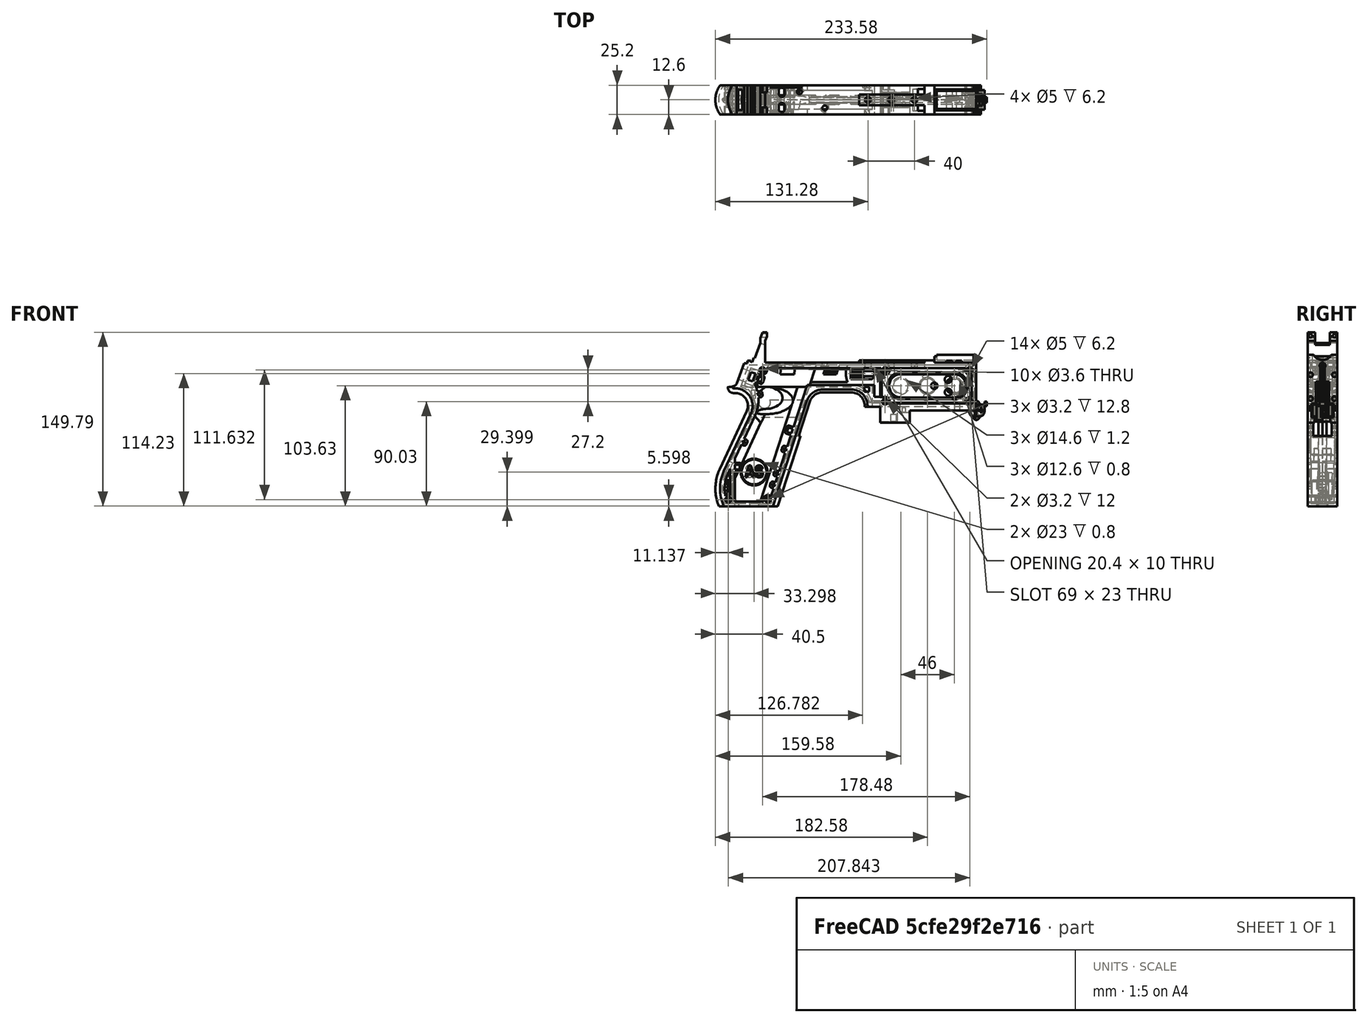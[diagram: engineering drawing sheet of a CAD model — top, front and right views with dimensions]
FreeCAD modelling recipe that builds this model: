
FCSTD DOCUMENT  (FreeCAD 1.0R39319 (Git))
Label: PICON-OF_ver_58
License: All rights reserved
LicenseURL: https://en.wikipedia.org/wiki/All_rights_reserved
objects: Sketcher::SketchObject×124, Part::Extrusion×63, Part::Cut×48, PartDesign::Pad×29, PartDesign::Pocket×21, PartDesign::Chamfer×15, PartDesign::Body×10, PartDesign::Fillet×6, Part::MultiFuse×5, Part::Part2DObjectPython×4, PartDesign::SubtractivePipe×4, PartDesign::SubtractiveLoft×4, PartDesign::Plane×3, PartDesign::SubShapeBinder×2, Part::Sweep×1, PartDesign::ShapeBinder×1, Mesh::Feature×1, PartDesign::Point×1, PartDesign::Groove×1
note: 626 computed .brp shape members not serialized (recipe doc carries the construction recipe); baked Part::Feature solids carry a one-line shape summary decoded from their .brp

FEATURE [Sketcher::SketchObject] Sketch  label="corpo principale"
  ArcFitTolerance = 1e-06
  AttacherType = Attacher::AttachEngine3D
  AttachmentSupport = -> [XZ_Plane]
  FullyConstrained = true
  MakeInternals = false
  MapMode = 5
  Placement = pos=(0,0,0) rot=(1,0,0;1.5708rad)
  sketch-geometry (65):
    g0: LineSegment StartX=0 StartY=0 StartZ=0 EndX=-57.2 EndY=0 EndZ=0
    g1: LineSegment StartX=-57.2 StartY=0 StartZ=0 EndX=-57.2 EndY=-10.4 EndZ=0
    g2: LineSegment StartX=-57.2 StartY=-10.4 StartZ=0 EndX=-82.8 EndY=-10.4 EndZ=0
    g3: LineSegment StartX=-82.8 StartY=-10.4 StartZ=0 EndX=-82.8 EndY=3.2 EndZ=0
    g4: LineSegment StartX=-82.8 StartY=3.2 StartZ=0 EndX=-93.6 EndY=3.2 EndZ=0
    g5: LineSegment StartX=-93.6 StartY=3.2 StartZ=0 EndX=-93.6 EndY=4 EndZ=0
    g6: LineSegment StartX=-107.6 StartY=18 StartZ=0 EndX=-132.428 EndY=18 EndZ=0
    g7: LineSegment StartX=-145.743 StartY=8.32624 StartZ=0 EndX=-175.232 EndY=-82.4316 EndZ=0
    g8: LineSegment StartX=-175.232 StartY=-82.4316 StartZ=0 EndX=-217.232 EndY=-82.4316 EndZ=0
    g9: LineSegment StartX=-217.232 StartY=-52.1862 StartZ=0 EndX=-193.988 EndY=-2.33927 EndZ=0
    g10: LineSegment StartX=-206.196 StartY=23.0857 StartZ=0 EndX=-199.861 EndY=40.4914 EndZ=0
    g11: LineSegment StartX=-199.861 StartY=40.4914 StartZ=0 EndX=-197.061 EndY=40.4914 EndZ=0
    g12: LineSegment StartX=-197.061 StartY=40.4914 StartZ=0 EndX=-197.061 EndY=42.8914 EndZ=0
    g13: LineSegment StartX=-197.061 StartY=42.8914 StartZ=0 EndX=-194.261 EndY=42.8914 EndZ=0
    g14: LineSegment StartX=-194.261 StartY=42.8914 StartZ=0 EndX=-194.535 EndY=42.1397 EndZ=0
    g15: LineSegment StartX=-194.535 StartY=42.1397 StartZ=0 EndX=-193.031 EndY=41.5924 EndZ=0
    g16: LineSegment StartX=-193.031 StartY=41.5924 StartZ=0 EndX=-191.663 EndY=45.3512 EndZ=0
    g17: LineSegment StartX=-191.663 StartY=45.3512 StartZ=0 EndX=-190.536 EndY=44.9408 EndZ=0
    g18: LineSegment StartX=-190.536 StartY=44.9408 StartZ=0 EndX=-185.747 EndY=58.0965 EndZ=0
    g19: LineSegment StartX=-185.747 StartY=58.0965 StartZ=0 EndX=-185.747 EndY=62.0965 EndZ=0
    g20: LineSegment StartX=-185.747 StartY=62.0965 StartZ=0 EndX=-183.832 EndY=67.3588 EndZ=0
    g21: LineSegment StartX=-183.832 StartY=67.3588 StartZ=0 EndX=-180.232 EndY=67.3588 EndZ=0
    g22: LineSegment StartX=-180.232 StartY=67.3588 StartZ=0 EndX=-180.232 EndY=63.7588 EndZ=0
    g23: LineSegment StartX=-180.232 StartY=63.7588 StartZ=0 EndX=-181.6 EndY=60 EndZ=0
    g24: LineSegment StartX=-181.6 StartY=60 StartZ=0 EndX=-181.6 EndY=41.2 EndZ=0
    g25: LineSegment StartX=-181.6 StartY=41.2 StartZ=0 EndX=-100.8 EndY=41.2 EndZ=0
    g26: LineSegment StartX=-36 StartY=43.2 StartZ=0 EndX=-36 EndY=41.2 EndZ=0
    g27: LineSegment StartX=0 StartY=48 StartZ=0 EndX=0 EndY=0 EndZ=0
    g28: LineSegment StartX=-209.901 StartY=19.85 StartZ=0 EndX=-209.901 EndY=20.1 EndZ=0
    g29: LineSegment StartX=-208.001 StartY=22 StartZ=0 EndX=-207.747 EndY=22 EndZ=0
    g30: LineSegment StartX=-207.583 StartY=19 StartZ=0 EndX=-209.051 EndY=19 EndZ=0
    g31: ArcOfCircle CenterX=-208.001 CenterY=20.1 CenterZ=0 NormalX=0 NormalY=0 NormalZ=1 AngleXU=0 Radius=1.9 StartAngle=1.5708 EndAngle=3.14159
    g32: GeomPoint [constr] X=-209.901 Y=22 Z=0
    g33: ArcOfCircle CenterX=-209.051 CenterY=19.85 CenterZ=0 NormalX=0 NormalY=0 NormalZ=1 AngleXU=0 Radius=0.85 StartAngle=3.14159 EndAngle=4.71239
    g34: GeomPoint [constr] X=-209.901 Y=19 Z=0
    g35: ArcOfCircle CenterX=-207.747 CenterY=23.65 CenterZ=0 NormalX=0 NormalY=0 NormalZ=1 AngleXU=0 Radius=1.65 StartAngle=4.71239 EndAngle=5.93412
    g36: GeomPoint [constr] X=-206.591 Y=22 Z=0
    g37: LineSegment StartX=-4 StartY=6 StartZ=0 EndX=-4 EndY=36.4 EndZ=0
    g38: LineSegment StartX=-4 StartY=36.4 StartZ=0 EndX=-185.2 EndY=36.4 EndZ=0
    g39: LineSegment StartX=-185.2 StartY=36.4 StartZ=0 EndX=-190.441 EndY=22 EndZ=0
    g40: LineSegment StartX=-214.575 StartY=-78.4316 StartZ=0 EndX=-178.142 EndY=-78.4316 EndZ=0
    g41: LineSegment StartX=-178.142 StartY=-78.4316 StartZ=0 EndX=-145.51 EndY=22 EndZ=0
    g42: LineSegment StartX=-145.51 StartY=22 StartZ=0 EndX=-87.91 EndY=22 EndZ=0
    g43: LineSegment StartX=-87.91 StartY=22 StartZ=0 EndX=-87.91 EndY=11.6 EndZ=0
    g44: LineSegment StartX=-87.91 StartY=11.6 StartZ=0 EndX=-80.11 EndY=11.6 EndZ=0
    g45: LineSegment StartX=-80.11 StartY=11.6 StartZ=0 EndX=-80.11 EndY=6 EndZ=0
    g46: LineSegment StartX=-80.11 StartY=6 StartZ=0 EndX=-4 EndY=6 EndZ=0
    g47: LineSegment StartX=-190.363 StartY=-4.02975 StartZ=0 EndX=-213.607 EndY=-53.8767 EndZ=0
    g48: ArcOfCircle CenterX=-132.428 CenterY=4 CenterZ=0 NormalX=0 NormalY=0 NormalZ=1 AngleXU=0 Radius=14 StartAngle=1.5708 EndAngle=2.82743
    g49: GeomPoint [constr] X=-142.6 Y=18 Z=0
    g50: ArcOfCircle CenterX=-107.6 CenterY=4 CenterZ=0 NormalX=0 NormalY=0 NormalZ=1 AngleXU=0 Radius=14 StartAngle=0 EndAngle=1.5708
    g51: GeomPoint [constr] X=-93.6 Y=18 Z=0
    g52: ArcOfCircle CenterX=-184.801 CenterY=-67.3089 CenterZ=0 NormalX=0 NormalY=0 NormalZ=1 AngleXU=0 Radius=35.7833 StartAngle=2.70526 EndAngle=3.57792
    g53: ArcOfCircle CenterX=-207.583 CenterY=4 CenterZ=0 NormalX=0 NormalY=0 NormalZ=1 AngleXU=0 Radius=15 StartAngle=5.84685 EndAngle=7.85398
    g54: LineSegment [constr] StartX=-213.607 StartY=-53.8767 StartZ=0 EndX=-217.232 EndY=-52.1862 EndZ=0
    g55: ArcOfCircle CenterX=-184.801 CenterY=-67.3089 CenterZ=0 NormalX=0 NormalY=0 NormalZ=1 AngleXU=0 Radius=31.7833 StartAngle=2.70526 EndAngle=3.49911
    g56: ArcOfCircle CenterX=-218.095 CenterY=8.90192 CenterZ=0 NormalX=0 NormalY=0 NormalZ=1 AngleXU=0 Radius=30.5989 StartAngle=5.84685 EndAngle=6.72553
    g57: LineSegment StartX=-44.6 StartY=43.2 StartZ=0 EndX=-36 EndY=43.2 EndZ=0
    g58: LineSegment StartX=-100.8 StartY=41.2 StartZ=0 EndX=-44.6 EndY=41.2 EndZ=0
    g59: LineSegment StartX=-44.6 StartY=41.2 StartZ=0 EndX=-44.6 EndY=43.2 EndZ=0
    g60: LineSegment StartX=-2.4 StartY=48 StartZ=0 EndX=0 EndY=48 EndZ=0
    g61: LineSegment StartX=-36 StartY=41.2 StartZ=0 EndX=-2.4 EndY=41.2 EndZ=0
    g62: LineSegment StartX=-2.4 StartY=41.2 StartZ=0 EndX=-2.4 EndY=48 EndZ=0
    g63: LineSegment [constr] StartX=-181.6 StartY=36.4 StartZ=0 EndX=-152.209 EndY=36.4 EndZ=0
    g64: LineSegment [constr] StartX=-181.6 StartY=36.4 StartZ=0 EndX=-130.41 EndY=36.4 EndZ=0
  constraints (183):
    c: Coincident(g-1,g0)
    c: PointOnObject(g0,g-1)
    c: Coincident(g0,g1)
    c: Vertical(g1)
    c: Coincident(g1,g2)
    c: Horizontal(g2)
    c: Coincident(g2,g3)
    c: Vertical(g3)
    c: Coincident(g3,g4)
    c: Coincident(g4,g5)
    c: Vertical(g5)
    c: Horizontal(g6)
    c: Coincident(g7,g8)
    c: Horizontal(g8)
    c: Coincident(g10,g11)
    c: Horizontal(g11)
    c: Coincident(g11,g12)
    c: Vertical(g12)
    c: Coincident(g12,g13)
    c: Horizontal(g13)
    c: Coincident(g13,g14)
    c: Coincident(g14,g15)
    c: Coincident(g15,g16)
    c: Coincident(g16,g17)
    c: Coincident(g17,g18)
    c: Coincident(g18,g19)
    c: Vertical(g19)
    c: Coincident(g19,g20)
    c: Coincident(g20,g21)
    c: Horizontal(g21)
    c: Coincident(g21,g22)
    c: Vertical(g22)
    c: Coincident(g22,g23)
    c: Coincident(g23,g24)
    c: Vertical(g24)
    c: Coincident(g24,g25)
    c: Horizontal(g25)
    c: Coincident(g57,g26)
    c: Vertical(g26)
    c: Coincident(g26,g61)
    c: PointOnObject(g60,g-2)
    c: Coincident(g60,g27)
    c: Coincident(g27,g0)
    c: DistanceY(g27,g27) = 48
    c: DistanceY(g1,g1) = 10.4
    c: DistanceX(g0,g0) = 57.2
    c: DistanceX(g2,g2) = 25.6
    c: Horizontal(g4)
    c: DistanceY(g3,g3) = 13.6
    c: DistanceX(g4,g4) = 10.8
    c: DistanceY(g5,g51) = 14.8
    c: DistanceX(g49,g51) = 49
    c: Distance(g7,g49) = 105.6
    c: DistanceX(g61,g60) = 36
    c: DistanceX(g25,g25) = 80.8
    c: DistanceY(g24,g24) = 18.8
    c: DistanceY(g22,g22) = 3.6
    c: Distance(g23) = 4
    c: Angle(g-1,g23) = 1.22173
    c: DistanceX(g21,g21) = 3.6
    c: Distance(g20) = 5.6
    c: Angle(g-1,g20) = 1.22173
    c: DistanceY(g19,g19) = 4
    c: Distance(g18) = 14
    c: Angle(g-1,g18) = 1.22173
    c: Distance(g17) = 1.2
    c: Distance(g16) = 4
    c: Angle(g16) = 1.22173
    c: Perpendicular(g18,g17)
    c: Distance(g15) = 1.6
    c: Perpendicular(g16,g15)
    c: Distance(g14) = 0.8
    c: DistanceX(g13,g13) = 2.8
    c: Perpendicular(g15,g14)
    c: DistanceY(g12,g12) = 2.4
    c: DistanceX(g11,g11) = 2.8
    c: Distance(g9) = 55
    c: Angle(g9,g-1) = 2.00713
    c: Horizontal(g29)
    c: Vertical(g28)
    c: Horizontal(g30)
    c: PointOnObject(g32,g29)
    c: PointOnObject(g32,g28)
    c: Tangent(g29,g31) = 1.5708
    c: Tangent(g28,g31) = 1.5708
    c: PointOnObject(g34,g28)
    c: PointOnObject(g34,g30)
    c: Tangent(g28,g33) = 1.5708
    c: Tangent(g30,g33) = 1.5708
    c: PointOnObject(g36,g29)
    c: PointOnObject(g36,g10)
    c: Tangent(g29,g35) = -1.5708
    c: Tangent(g10,g35) = -1.5708
    c: Angle(g-1,g10) = 1.22173
    c: Radius(g35) = 1.65
    c: Vertical(g37)
    c: Coincident(g37,g38)
    c: Horizontal(g38)
    c: Coincident(g38,g39)
    c: Horizontal(g40)
    c: Coincident(g40,g41)
    c: Coincident(g41,g42)
    c: Horizontal(g42)
    c: Coincident(g42,g43)
    c: Vertical(g43)
    c: Coincident(g43,g44)
    c: Horizontal(g44)
    c: Coincident(g44,g45)
    c: Vertical(g45)
    c: Coincident(g45,g46)
    c: Coincident(g46,g37)
    c: Horizontal(g46)
    c: DistanceY(g0,g37) = 6
    c: DistanceX(g37,g0) = 4
    c: DistanceY(g37,g25) = 4.8
    c: DistanceX(g38,g38) = 181.2
    c: DistanceX(g42,g42) = 57.6
    c: DistanceY(g49,g41) = 4
    c: DistanceX(g41,g49) = 2.91
    c: DistanceY(g43,g43) = 10.4
    c: DistanceX(g44,g44) = 7.8
    c: DistanceY(g7,g40) = 4
    c: Distance(g47) = 55
    c: Angle(g-1,g39) = 1.22173
    c: PointOnObject(g49,g7)
    c: PointOnObject(g49,g6)
    c: Tangent(g7,g48) = -1.5708
    c: Tangent(g6,g48) = -1.5708
    c: PointOnObject(g51,g5)
    c: PointOnObject(g51,g6)
    c: Tangent(g5,g50) = -1.5708
    c: Tangent(g6,g50) = -1.5708
    c: Radius(g50) = 14
    c: Radius(g48) = 14
    c: DistanceX(g8,g8) = 42
    c: Angle(g7,g-1) = 1.88496
    c: Parallel(g41,g7)
    c: Parallel(g47,g9)
    c: Coincident(g52,g8)
    c: Tangent(g52,g9) = 1.5708
    c: DistanceX(g9,g8) = 0
    c: Tangent(g53,g9) = -1.5708
    c: Tangent(g53,g30) = -1.5708
    c: Diameter(g53) = 30
    c: DistanceY(g53,g0) = -4
    c: Coincident(g54,g47)
    c: Distance(g54) = 4
    c: Coincident(g54,g9)
    c: Coincident(g55,g40)
    c: Tangent(g55,g47) = -1.5708
    c: Coincident(g52,g55)
    c: Coincident(g56,g39)
    c: Tangent(g56,g47) = 1.5708
    c: Horizontal(g57)
    c: DistanceX(g57,g57) = 8.6
    c: Coincident(g58,g25)
    c: Horizontal(g58)
    c: Coincident(g59,g58)
    c: Vertical(g59)
    c: DistanceY(g58,g57) = 2
    c: DistanceX(g58,g58) = 56.2
    c: Coincident(g59,g57)
    c: DistanceY(g41,g36) = 0
    c: DistanceY(g36,g39) = 0
    c: DistanceY(g28,g28) = 0.25
    c: DistanceX(g30,g36) = 2.46
    c: DistanceX(g28,g29) = 1.9
    c: Coincident(g62,g60)
    c: Horizontal(g60)
    c: DistanceX(g62,g27) = 2.4
    c: Coincident(g61,g62)
    c: DistanceY(g26,g26) = 2
    c: Vertical(g62)
    c: DistanceY(g61,g60) = 6.8
    c: Horizontal(g61)
    c: Distance(g63) = 29.391
    c: PointOnObject(g63,g38)
    c: PointOnObject(g63,g38)
    c: Distance(g64) = 51.19
    c: PointOnObject(g64,g38)
    c: PointOnObject(g64,g38)
    c: DistanceX(g24,g63) = 0
    c: DistanceX(g24,g64) = 0
FEATURE [Part::Extrusion] Extrude  label="Extrude corpo principale"
  Base = -> Sketch
  Dir = (0,-1,2e-16)
  DirMode = 2
  FaceMakerClass = Part::FaceMakerBullseye
  FaceMakerMode = 3
  LengthFwd = 25.2
  LengthRev = 12.6
  Solid = true
  Symmetric = true
FEATURE [Sketcher::SketchObject] Sketch002  label="scavo grilletto"
  ArcFitTolerance = 1e-06
  AttachmentSupport = -> [XZ_Plane]
  ExternalGeometry = -> [Sketch]
  FullyConstrained = true
  MakeInternals = false
  MapMode = 5
  Placement = pos=(0,0,0) rot=(1,0,0;1.5708rad)
  sketch-geometry (4):
    g0: LineSegment StartX=-89.51 StartY=22 StartZ=0 EndX=-152.71 EndY=22 EndZ=0
    g1: LineSegment StartX=-152.71 StartY=22 StartZ=0 EndX=-167.006 EndY=-22 EndZ=0
    g2: LineSegment StartX=-167.006 StartY=-22 StartZ=0 EndX=-89.51 EndY=-22 EndZ=0
    g3: LineSegment StartX=-89.51 StartY=-22 StartZ=0 EndX=-89.51 EndY=22 EndZ=0
  constraints (12):
    c: Horizontal(g0)
    c: Coincident(g0,g1)
    c: Coincident(g1,g2)
    c: Horizontal(g2)
    c: Coincident(g2,g3)
    c: Coincident(g3,g0)
    c: Vertical(g3)
    c: Angle(g1,g0) = 1.88496
    c: DistanceY(g3,g3) = 44
    c: DistanceX(g0,g0) = 63.2
    c: DistanceX(g0,g-3) = 1.6
    c: DistanceY(g-3,g0) = 0
FEATURE [Sketcher::SketchObject] Sketch004  label="traiettoria arrotondamento impugnatura anteriore"
  ArcFitTolerance = 1e-06
  AttachmentSupport = -> [XZ_Plane]
  ExternalGeometry = -> [Sketch]
  FullyConstrained = true
  MakeInternals = false
  MapMode = 5
  Placement = pos=(0,0,0) rot=(1,0,0;1.5708rad)
  sketch-geometry (13):
    g0: LineSegment StartX=-175.232 StartY=-82.4316 StartZ=0 EndX=-145.743 EndY=8.32624 EndZ=0
    g1: LineSegment StartX=-93.6 StartY=3.2 StartZ=0 EndX=-93.6 EndY=4 EndZ=0
    g2: LineSegment StartX=-132.428 StartY=18 StartZ=0 EndX=-107.6 EndY=18 EndZ=0
    g3: ArcOfCircle CenterX=-132.428 CenterY=4 CenterZ=0 NormalX=0 NormalY=0 NormalZ=1 AngleXU=0 Radius=14 StartAngle=1.5708 EndAngle=2.82743
    g4: ArcOfCircle CenterX=-107.6 CenterY=4 CenterZ=0 NormalX=0 NormalY=0 NormalZ=1 AngleXU=0 Radius=14 StartAngle=0 EndAngle=1.5708
    g5: LineSegment StartX=-175.232 StartY=-82.4316 StartZ=0 EndX=-217.232 EndY=-82.4316 EndZ=0
    g6: LineSegment StartX=-217.232 StartY=-52.1862 StartZ=0 EndX=-193.988 EndY=-2.33927 EndZ=0
    g7: LineSegment StartX=-209.051 StartY=19 StartZ=0 EndX=-207.583 EndY=19 EndZ=0
    g8: LineSegment StartX=-209.901 StartY=20.1 StartZ=0 EndX=-209.901 EndY=19.85 EndZ=0
    g9: ArcOfCircle CenterX=-184.801 CenterY=-67.3089 CenterZ=0 NormalX=0 NormalY=0 NormalZ=1 AngleXU=0 Radius=35.7833 StartAngle=2.70526 EndAngle=3.57792
    g10: ArcOfCircle CenterX=-207.583 CenterY=4 CenterZ=0 NormalX=0 NormalY=0 NormalZ=1 AngleXU=0 Radius=15 StartAngle=5.84685 EndAngle=7.85398
    g11: ArcOfCircle CenterX=-209.051 CenterY=19.85 CenterZ=0 NormalX=0 NormalY=0 NormalZ=1 AngleXU=0 Radius=0.85 StartAngle=3.14159 EndAngle=4.71239
    g12: ArcOfCircle CenterX=-208.001 CenterY=20.1 CenterZ=0 NormalX=0 NormalY=0 NormalZ=1 AngleXU=0 Radius=1.9 StartAngle=1.5708 EndAngle=3.14159
  constraints (26):
    c: Coincident(g0,g-3)
    c: Coincident(g0,g-6)
    c: Coincident(g1,g-8)
    c: Coincident(g1,g-7)
    c: Coincident(g2,g-5)
    c: Coincident(g2,g-4)
    c: Coincident(g3,g2)
    c: Tangent(g3,g0) = 1.5708
    c: Coincident(g4,g1)
    c: Tangent(g4,g2) = 1.5708
    c: Coincident(g5,g0)
    c: Coincident(g5,g-9)
    c: Coincident(g6,g-12)
    c: Coincident(g6,g-11)
    c: Coincident(g7,g-15)
    c: Coincident(g7,g-14)
    c: Coincident(g8,g-16)
    c: Coincident(g8,g-17)
    c: Tangent(g9,g6) = 1.5708
    c: Coincident(g9,g5)
    c: Coincident(g10,g7)
    c: Tangent(g10,g6) = -1.5708
    c: Tangent(g11,g7) = -1.5708
    c: Coincident(g11,g8)
    c: Tangent(g12,g8) = -1.5708
    c: Coincident(g12,g-17)
FEATURE [PartDesign::Plane] DatumPlane  label="Piano per disegno arrotondamento impugnatura"
  AttachmentSupport = -> [Sketch]
  Length = 73.6581
  MapMode = 7
  Placement = pos=(-145.743,1.8e-15,8.32624) rot=(0.154555,0.154555,0.97582;1.59527rad)
  ResizeMode = 0
  Width = 303.511
FEATURE [Sketcher::SketchObject] Sketch005  label="forma arrotondamento impugnatura anteriore"
  ArcFitTolerance = 1e-06
  AttachmentSupport = -> [DatumPlane]
  FullyConstrained = true
  MakeInternals = false
  MapMode = 5
  Placement = pos=(-145.743,1.8e-15,8.32624) rot=(0.154555,0.154555,0.97582;1.59527rad)
  sketch-geometry (5):
    g0: GeomPoint [constr] X=0 Y=-4 Z=0
    g1: GeomPoint [constr] X=-12.6 Y=7.1e-15 Z=0
    g2: GeomPoint [constr] X=12.6 Y=4.97e-14 Z=0
    g3: LineSegment StartX=-12.6 StartY=7.1e-15 StartZ=0 EndX=12.6 EndY=4.97e-14 EndZ=0
    g4: ArcOfCircle CenterX=-3.88e-14 CenterY=17.845 CenterZ=0 NormalX=0 NormalY=0 NormalZ=1 AngleXU=0 Radius=21.845 StartAngle=4.09759 EndAngle=5.32718
  constraints (11):
    c: DistanceY(g0,g-1) = 4
    c: DistanceX(g-1,g0) = 0
    c: DistanceX(g1,g-1) = 12.6
    c: DistanceX(g-1,g2) = 12.6
    c: DistanceY(g-1,g2) = 0
    c: DistanceY(g-1,g1) = 0
    c: Coincident(g3,g1)
    c: Coincident(g3,g2)
    c: Coincident(g4,g1)
    c: Coincident(g4,g2)
    c: PointOnObject(g0,g4)
FEATURE [Part::Sweep] Sweep  label="Sweep impugnatura"
  Frenet = true
  Sections = -> [Sketch005]
  Solid = true
  Spine = -> Sketch [Edge32,Edge33,Edge34,Edge35,Edge36,Edge37,Edge38,Edge39,Edge40,Edge41,Edge42,Edge43,Edge44]
  Transition = 1
FEATURE [Sketcher::SketchObject] Sketch008  label="buchi e pulizie varie"
  ArcFitTolerance = 1e-06
  AttachmentSupport = -> [XZ_Plane]
  ExternalGeometry = -> [Sketch]
  FullyConstrained = true
  MakeInternals = false
  MapMode = 5
  Placement = pos=(0,0,0) rot=(1,0,0;1.5708rad)
  sketch-geometry (26):
    g0: LineSegment StartX=-96.278 StartY=20.155 StartZ=0 EndX=-92.278 EndY=20.155 EndZ=0
    g1: LineSegment StartX=-92.278 StartY=20.155 StartZ=0 EndX=-92.278 EndY=16.155 EndZ=0
    g2: LineSegment StartX=-92.278 StartY=16.155 StartZ=0 EndX=-96.278 EndY=16.155 EndZ=0
    g3: LineSegment StartX=-96.278 StartY=16.155 StartZ=0 EndX=-96.278 EndY=20.155 EndZ=0
    g4: LineSegment StartX=-222.232 StartY=-82.4316 StartZ=0 EndX=-170.232 EndY=-82.4316 EndZ=0
    g5: LineSegment StartX=-170.232 StartY=-82.4316 StartZ=0 EndX=-170.232 EndY=-86.4316 EndZ=0
    g6: LineSegment StartX=-170.232 StartY=-86.4316 StartZ=0 EndX=-222.232 EndY=-86.4316 EndZ=0
    g7: LineSegment StartX=-222.232 StartY=-86.4316 StartZ=0 EndX=-222.232 EndY=-82.4316 EndZ=0
    g8: LineSegment StartX=-213.901 StartY=20.1 StartZ=0 EndX=-213.901 EndY=26 EndZ=0
    g9: LineSegment StartX=-213.901 StartY=26 StartZ=0 EndX=-206.196 EndY=26 EndZ=0
    g10: LineSegment StartX=-17.4 StartY=42.8 StartZ=0 EndX=-12.4 EndY=42.8 EndZ=0
    g11: LineSegment StartX=-12.4 StartY=42.8 StartZ=0 EndX=-12.4 EndY=41.2 EndZ=0
    g12: LineSegment StartX=-12.4 StartY=41.2 StartZ=0 EndX=-17.4 EndY=41.2 EndZ=0
    g13: LineSegment StartX=-17.4 StartY=41.2 StartZ=0 EndX=-17.4 EndY=42.8 EndZ=0
    g14: LineSegment StartX=-25.9 StartY=42.8 StartZ=0 EndX=-20.9 EndY=42.8 EndZ=0
    g15: LineSegment StartX=-20.9 StartY=42.8 StartZ=0 EndX=-20.9 EndY=41.2 EndZ=0
    g16: LineSegment StartX=-20.9 StartY=41.2 StartZ=0 EndX=-25.9 EndY=41.2 EndZ=0
    g17: LineSegment StartX=-25.9 StartY=41.2 StartZ=0 EndX=-25.9 EndY=42.8 EndZ=0
    g18: GeomPoint [constr] X=-206.196 Y=23.0857 Z=0
    g19: GeomPoint [constr] X=-213.901 Y=20.1 Z=0
    g20: BSplineCurve PolesCount=4 KnotsCount=2 Degree=3 IsPeriodic=0
    g21-g24: Circle [constr] x4 (B-spline internal-alignment scaffolding for g20; pole/knot coordinates omitted)
    g25: LineSegment StartX=-206.196 StartY=26 StartZ=0 EndX=-206.196 EndY=23.0857 EndZ=0
  constraints (73):
    c: Horizontal(g0)
    c: Coincident(g1,g0)
    c: Vertical(g1)
    c: Coincident(g2,g1)
    c: Horizontal(g2)
    c: Coincident(g3,g2)
    c: Coincident(g3,g0)
    c: Vertical(g3)
    c: DistanceX(g0,g-4) = 4.368
    c: DistanceY(g0,g-4) = 1.845
    c: DistanceY(g1,g1) = 4
    c: DistanceX(g2,g2) = 4
    c: Horizontal(g4)
    c: Coincident(g5,g4)
    c: Vertical(g5)
    c: Coincident(g6,g5)
    c: Horizontal(g6)
    c: Coincident(g7,g6)
    c: Coincident(g7,g4)
    c: Vertical(g7)
    c: DistanceY(g7,g7) = 4
    c: DistanceX(g4,g-5) = 5
    c: DistanceX(g-5,g4) = 5
    c: DistanceY(g4,g-5) = 0
    c: Coincident(g9,g8)
    c: Parallel(g9,g-6)
    c: DistanceX(g8,g-8) = 4
    c: Horizontal(g10)
    c: Coincident(g11,g10)
    c: Vertical(g11)
    c: Coincident(g12,g11)
    c: Horizontal(g12)
    c: Coincident(g13,g12)
    c: Coincident(g13,g10)
    c: Vertical(g13)
    c: Horizontal(g14)
    c: Coincident(g15,g14)
    c: Vertical(g15)
    c: Coincident(g16,g15)
    c: Horizontal(g16)
    c: Coincident(g17,g16)
    c: Coincident(g17,g14)
    c: Vertical(g17)
    c: DistanceY(g11,g10) = 1.6
    c: DistanceX(g10,g10) = 5
    c: DistanceY(g15,g14) = 1.6
    c: DistanceX(g14,g14) = 5
    c: DistanceX(g15,g12) = 3.5
    c: DistanceX(g11,g-9) = 10
    c: DistanceY(g-9,g11) = 0
    c: DistanceY(g-9,g15) = 0
    c: Perpendicular(g8,g9)
    c: DistanceY(g-7,g9) = 4
    c: DistanceY(g8,g-8) = 0
    c: InternalAlignment(g18,g20)
    c: InternalAlignment(g19,g20)
    c: InternalAlignment(g21,g20)
    c: Weight(g21) = 1
    c: InternalAlignment(g22,g20)
    c: Equal(g22,g21)
    c: InternalAlignment(g23,g20)
    c: Equal(g23,g21)
    c: InternalAlignment(g24,g20)
    c: Equal(g24,g21)
    c: Coincident(g18,g-12)
    c: Coincident(g19,g8)
    c: Coincident(g25,g9)
    c: Coincident(g25,g20)
    c: Vertical(g25)
    c: DistanceY(g20,g23) = 0
    c: DistanceY(g22,g18) = 2.26
    c: DistanceX(g22,g18) = 0.93
    c: DistanceX(g20,g23) = 2.9
FEATURE [Part::Extrusion] Extrude004  label="Extrude Buchi e pulizie varie"
  Base = -> Sketch008
  Dir = (0,-1,2e-16)
  DirMode = 2
  FaceMakerClass = Part::FaceMakerBullseye
  FaceMakerMode = 3
  LengthFwd = 25.2
  LengthRev = 0
  Solid = true
  Symmetric = true
FEATURE [Sketcher::SketchObject] Sketch009  label="rinforzi"
  ArcFitTolerance = 1e-06
  AttachmentSupport = -> [XZ_Plane]
  ExternalGeometry = -> [Sketch]
  FullyConstrained = true
  MakeInternals = false
  MapMode = 5
  Placement = pos=(0,0,0) rot=(1,0,0;1.5708rad)
  sketch-geometry (9):
    g0: LineSegment StartX=-87.91 StartY=22 StartZ=0 EndX=-87.91 EndY=36.4 EndZ=0
    g1: LineSegment StartX=-87.91 StartY=36.4 StartZ=0 EndX=-97.91 EndY=36.4 EndZ=0
    g2: LineSegment StartX=-97.91 StartY=36.4 StartZ=0 EndX=-97.91 EndY=22 EndZ=0
    g3: LineSegment StartX=-97.91 StartY=22 StartZ=0 EndX=-87.91 EndY=22 EndZ=0
    g4: LineSegment StartX=-149.713 StartY=9.06563 StartZ=0 EndX=-154.586 EndY=-5.93437 EndZ=0
    g5: LineSegment StartX=-154.586 StartY=-5.93437 StartZ=0 EndX=-191.863 EndY=-5.93437 EndZ=0
    g6: LineSegment StartX=-191.863 StartY=-5.93437 StartZ=0 EndX=-191.863 EndY=9.06563 EndZ=0
    g7: LineSegment StartX=-191.863 StartY=9.06563 StartZ=0 EndX=-149.713 EndY=9.06563 EndZ=0
    g8: LineSegment [constr] StartX=-145.51 StartY=22 StartZ=0 EndX=-149.713 EndY=9.06563 EndZ=0
  constraints (25):
    c: Vertical(g0)
    c: Coincident(g1,g0)
    c: Horizontal(g1)
    c: Coincident(g2,g1)
    c: Vertical(g2)
    c: Coincident(g3,g2)
    c: Coincident(g3,g0)
    c: Horizontal(g3)
    c: Coincident(g0,g-4)
    c: DistanceX(g3,g3) = 10
    c: DistanceY(g0,g-3) = 0
    c: Coincident(g5,g4)
    c: Horizontal(g5)
    c: Coincident(g6,g5)
    c: Vertical(g6)
    c: Coincident(g7,g6)
    c: Coincident(g7,g4)
    c: Horizontal(g7)
    c: Distance(g8) = 13.6
    c: Parallel(g-6,g8)
    c: Coincident(g-6,g8)
    c: Parallel(g4,g-6)
    c: DistanceY(g4,g4) = 15
    c: Coincident(g4,g8)
    c: DistanceX(g-5,g5) = -1.5
FEATURE [Part::Extrusion] Extrude001  label="Extrude scavo grilletto"
  Base = -> Sketch002
  Dir = (0,-1,2e-16)
  DirMode = 2
  FaceMakerClass = Part::FaceMakerBullseye
  FaceMakerMode = 3
  LengthFwd = 16
  LengthRev = 0
  Solid = true
  Symmetric = true
FEATURE [Part::Extrusion] Extrude005  label="Extrude Rinforzi"
  Base = -> Sketch009
  Dir = (0,-1,2e-16)
  DirMode = 2
  FaceMakerClass = Part::FaceMakerBullseye
  FaceMakerMode = 3
  LengthFwd = 2
  LengthRev = 0
  Placement = pos=(0,12.6,0) rot=(0,0,1;0rad)
  Solid = true
  Symmetric = false
FEATURE [PartDesign::ShapeBinder] CopyCut
  TraceSupport = false
FEATURE [PartDesign::Plane] DatumPlane001
  AttachmentSupport = -> [CopyCut]
  Length = 283.944
  MapMode = 5
  Placement = pos=(0,12.6,0) rot=(0,0.707107,0.707107;3.14159rad)
  ResizeMode = 0
  Width = 188.15
FEATURE [Sketcher::SketchObject] Sketch010  label="buco neopixel"
  ArcFitTolerance = 1e-06
  AttachmentSupport = -> [XZ_Plane]
  ExternalGeometry = -> [Sketch]
  FullyConstrained = true
  MakeInternals = false
  MapMode = 5
  Placement = pos=(0,0,0) rot=(1,0,0;1.5708rad)
  sketch-geometry (5):
    g0: LineSegment [constr] StartX=-199.861 StartY=40.4914 StartZ=0 EndX=-201.368 EndY=36.3521 EndZ=0
    g1: LineSegment StartX=-201.368 StartY=36.3521 StartZ=0 EndX=-204.932 EndY=26.5605 EndZ=0
    g2: LineSegment StartX=-201.368 StartY=36.3521 StartZ=0 EndX=-180.2 EndY=28.6477 EndZ=0
    g3: LineSegment StartX=-180.2 StartY=28.6477 StartZ=0 EndX=-183.764 EndY=18.8561 EndZ=0
    g4: LineSegment StartX=-183.764 StartY=18.8561 StartZ=0 EndX=-204.932 EndY=26.5605 EndZ=0
  constraints (14):
    c: Parallel(g0,g-3)
    c: Distance(g0) = 4.405
    c: Coincident(g0,g-3)
    c: Coincident(g2,g1)
    c: Coincident(g3,g2)
    c: Coincident(g4,g3)
    c: Coincident(g4,g1)
    c: Parallel(g1,g-3)
    c: Distance(g1) = 10.42
    c: Coincident(g1,g0)
    c: Parallel(g2,g4)
    c: Perpendicular(g1,g2)
    c: DistanceX(g-4,g2) = 5
    c: Parallel(g3,g1)
FEATURE [Part::Extrusion] Extrude006  label="Extrude buco neopixel"
  Base = -> Sketch010
  Dir = (0,-1,2e-16)
  DirMode = 2
  FaceMakerClass = Part::FaceMakerBullseye
  FaceMakerMode = 3
  LengthFwd = 17.2
  LengthRev = 0
  Solid = true
  Symmetric = true
FEATURE [Sketcher::SketchObject] Sketch011  label="fermo grilletto"
  ArcFitTolerance = 1e-06
  AttachmentSupport = -> [XZ_Plane]
  ExternalGeometry = -> [Sketch]
  FullyConstrained = true
  MakeInternals = false
  MapMode = 5
  Placement = pos=(0,0,0) rot=(1,0,0;1.5708rad)
  sketch-geometry (18):
    g0: LineSegment [constr] StartX=-145.51 StartY=22 StartZ=0 EndX=-157.347 EndY=-14.4293 EndZ=0
    g1: LineSegment [constr] StartX=-157.347 StartY=-14.4293 StartZ=0 EndX=-157.841 EndY=-15.951 EndZ=0
    g2: LineSegment StartX=-161.151 StartY=-13.1932 StartZ=0 EndX=-155.825 EndY=-14.9237 EndZ=0
    g3: LineSegment StartX=-163.167 StartY=-14.2205 StartZ=0 EndX=-164.403 EndY=-18.0247 EndZ=0
    g4: LineSegment StartX=-163.376 StartY=-20.0408 StartZ=0 EndX=-158.05 EndY=-21.7713 EndZ=0
    g5: LineSegment StartX=-158.05 StartY=-21.7713 StartZ=0 EndX=-155.825 EndY=-14.9237 EndZ=0
    g6: LineSegment StartX=-161.645 StartY=-14.7149 StartZ=0 EndX=-157.841 EndY=-15.951 EndZ=0
    g7: LineSegment StartX=-157.841 StartY=-15.951 StartZ=0 EndX=-159.077 EndY=-19.7552 EndZ=0
    g8: LineSegment StartX=-159.077 StartY=-19.7552 StartZ=0 EndX=-162.881 EndY=-18.5191 EndZ=0
    g9: LineSegment StartX=-162.881 StartY=-18.5191 StartZ=0 EndX=-161.645 EndY=-14.7149 EndZ=0
    g10: LineSegment [constr] StartX=-161.645 StartY=-14.7149 StartZ=0 EndX=-161.151 EndY=-13.1932 EndZ=0
    g11: LineSegment [constr] StartX=-159.077 StartY=-19.7552 StartZ=0 EndX=-157.555 EndY=-20.2496 EndZ=0
    g12: LineSegment [constr] StartX=-159.077 StartY=-19.7552 StartZ=0 EndX=-159.572 EndY=-21.2769 EndZ=0
    g13: LineSegment [constr] StartX=-161.645 StartY=-14.7149 StartZ=0 EndX=-163.167 EndY=-14.2205 EndZ=0
    g14: ArcOfCircle CenterX=-161.645 CenterY=-14.7149 CenterZ=0 NormalX=0 NormalY=0 NormalZ=1 AngleXU=0 Radius=1.6 StartAngle=1.25664 EndAngle=2.82743
    g15: GeomPoint [constr] X=-162.673 Y=-12.6988 Z=0
    g16: ArcOfCircle CenterX=-162.881 CenterY=-18.5191 CenterZ=0 NormalX=0 NormalY=0 NormalZ=1 AngleXU=0 Radius=1.6 StartAngle=2.82743 EndAngle=4.39823
    g17: GeomPoint [constr] X=-164.897 Y=-19.5464 Z=0
  constraints (48):
    c: Parallel(g0,g-3)
    c: Distance(g0) = 38.304
    c: Coincident(g0,g-3)
    c: Parallel(g1,g-3)
    c: Distance(g1) = 1.6
    c: Coincident(g1,g0)
    c: Coincident(g5,g4)
    c: Coincident(g5,g2)
    c: Coincident(g7,g6)
    c: Coincident(g8,g7)
    c: Coincident(g9,g8)
    c: Coincident(g9,g6)
    c: Parallel(g7,g-3)
    c: Parallel(g9,g7)
    c: Perpendicular(g6,g7)
    c: Parallel(g6,g8)
    c: Distance(g6) = 4
    c: Distance(g9) = 4
    c: Parallel(g5,g7)
    c: Parallel(g9,g3)
    c: Parallel(g2,g6)
    c: Parallel(g4,g8)
    c: Parallel(g13,g6)
    c: Parallel(g10,g9)
    c: Parallel(g11,g8)
    c: Parallel(g12,g7)
    c: Distance(g10) = 1.6
    c: Distance(g13) = 1.6
    c: Distance(g12) = 1.6
    c: Distance(g11) = 1.6
    c: Coincident(g10,g6)
    c: Coincident(g13,g6)
    c: Coincident(g12,g7)
    c: Coincident(g11,g7)
    c: Distance(g10,g15) = 1.6
    c: Distance(g15,g13) = 1.6
    c: Distance(g4,g12) = 1.6
    c: Distance(g4,g11) = 1.6
    c: PointOnObject(g15,g2)
    c: Tangent(g3,g14) = -1.5708
    c: Tangent(g2,g14) = 1.5708
    c: PointOnObject(g17,g4)
    c: PointOnObject(g17,g3)
    c: Tangent(g4,g16) = -1.5708
    c: Tangent(g3,g16) = -1.5708
    c: Equal(g16,g14)
    c: Coincident(g16,g8)
    c: Coincident(g6,g1)
FEATURE [Part::Extrusion] Extrude007  label="Extrude fermo grilletto"
  Base = -> Sketch011
  Dir = (0,-1,2e-16)
  DirMode = 2
  FaceMakerClass = Part::FaceMakerBullseye
  FaceMakerMode = 3
  LengthFwd = 25.2
  LengthRev = 0
  Solid = true
  Symmetric = true
FEATURE [Sketcher::SketchObject] Sketch012  label="buco oled"
  ArcFitTolerance = 1e-06
  AttachmentSupport = -> [XZ_Plane]
  ExternalGeometry = -> [Sketch]
  FullyConstrained = true
  MakeInternals = false
  MapMode = 5
  Placement = pos=(0,0,0) rot=(1,0,0;1.5708rad)
  sketch-geometry (4):
    g0: LineSegment StartX=-185.747 StartY=58.0965 StartZ=0 EndX=-180.232 EndY=56.0891 EndZ=0
    g1: LineSegment StartX=-185.747 StartY=58.0965 StartZ=0 EndX=-185.747 EndY=67.3588 EndZ=0
    g2: LineSegment StartX=-185.747 StartY=67.3588 StartZ=0 EndX=-180.232 EndY=67.3588 EndZ=0
    g3: LineSegment StartX=-180.232 StartY=67.3588 StartZ=0 EndX=-180.232 EndY=56.0891 EndZ=0
  constraints (10):
    c: Coincident(g1,g0)
    c: Coincident(g2,g1)
    c: Coincident(g3,g2)
    c: Coincident(g3,g0)
    c: Parallel(g1,g-5)
    c: Perpendicular(g-3,g0)
    c: Parallel(g2,g-6)
    c: Parallel(g3,g-4)
    c: Coincident(g0,g-5)
    c: Coincident(g2,g-6)
FEATURE [Part::Extrusion] Extrude008  label="Extrude buco oled"
  Base = -> Sketch012
  Dir = (0,-1,2e-16)
  DirMode = 2
  FaceMakerClass = Part::FaceMakerBullseye
  FaceMakerMode = 3
  LengthFwd = 12.8
  LengthRev = 0
  Solid = true
  Symmetric = true
FEATURE [Sketcher::SketchObject] Sketch013  label="buco pompa"
  ArcFitTolerance = 1e-06
  AttachmentSupport = -> [XZ_Plane]
  ExternalGeometry = -> [Sketch]
  FullyConstrained = true
  MakeInternals = false
  MapMode = 5
  Placement = pos=(0,0,0) rot=(1,0,0;1.5708rad)
  sketch-geometry (8):
    g0: LineSegment StartX=-82.8 StartY=-10.4 StartZ=0 EndX=-82.8 EndY=-9.6 EndZ=0
    g1: LineSegment StartX=-82.8 StartY=-9.6 StartZ=0 EndX=-67.9 EndY=-9.6 EndZ=0
    g2: LineSegment StartX=-67.9 StartY=-9.6 StartZ=0 EndX=-67.9 EndY=6 EndZ=0
    g3: LineSegment StartX=-67.9 StartY=6 StartZ=0 EndX=-65.9 EndY=6 EndZ=0
    g4: LineSegment StartX=-65.9 StartY=6 StartZ=0 EndX=-65.9 EndY=-1.7 EndZ=0
    g5: LineSegment StartX=-65.9 StartY=-1.7 StartZ=0 EndX=-57.2 EndY=-1.7 EndZ=0
    g6: LineSegment StartX=-57.2 StartY=-1.7 StartZ=0 EndX=-57.2 EndY=-10.4 EndZ=0
    g7: LineSegment StartX=-57.2 StartY=-10.4 StartZ=0 EndX=-82.8 EndY=-10.4 EndZ=0
  constraints (22):
    c: Vertical(g0)
    c: Coincident(g1,g0)
    c: Horizontal(g1)
    c: Coincident(g2,g1)
    c: Vertical(g2)
    c: Coincident(g3,g2)
    c: Horizontal(g3)
    c: Coincident(g4,g3)
    c: Vertical(g4)
    c: Coincident(g5,g4)
    c: Horizontal(g5)
    c: Coincident(g6,g5)
    c: Vertical(g6)
    c: Coincident(g7,g6)
    c: Coincident(g7,g0)
    c: DistanceY(g0,g0) = 0.8
    c: DistanceY(g6,g6) = 8.7
    c: DistanceX(g1,g1) = 14.9
    c: DistanceX(g3,g3) = 2
    c: Coincident(g0,g-4)
    c: DistanceY(g2,g-6) = 0
    c: Coincident(g6,g-5)
FEATURE [Part::Extrusion] Extrude009  label="Extrude buco pompa"
  Base = -> Sketch013
  Dir = (0,-1,2e-16)
  DirMode = 2
  FaceMakerClass = Part::FaceMakerBullseye
  FaceMakerMode = 3
  LengthFwd = 13.2
  LengthRev = 0
  Solid = true
  Symmetric = true
FEATURE [Sketcher::SketchObject] Sketch014  label="buco frontale"
  ArcFitTolerance = 1e-06
  AttachmentSupport = -> [XZ_Plane]
  ExternalGeometry = -> [Sketch]
  FullyConstrained = true
  MakeInternals = false
  MapMode = 5
  Placement = pos=(0,0,0) rot=(1,0,0;1.5708rad)
  sketch-geometry (10):
    g0: LineSegment StartX=0 StartY=0 StartZ=0 EndX=0 EndY=24.671 EndZ=0
    g1: LineSegment StartX=0 StartY=24.671 StartZ=0 EndX=-4 EndY=24.671 EndZ=0
    g2: LineSegment StartX=-4 StartY=24.671 StartZ=0 EndX=-4 EndY=16 EndZ=0
    g3: LineSegment StartX=-4 StartY=16 StartZ=0 EndX=-2.4 EndY=16 EndZ=0
    g4: LineSegment StartX=-2.4 StartY=16 StartZ=0 EndX=-2.4 EndY=10 EndZ=0
    g5: LineSegment StartX=-2.4 StartY=10 StartZ=0 EndX=-12 EndY=10 EndZ=0
    g6: LineSegment StartX=-12 StartY=10 StartZ=0 EndX=-12 EndY=6 EndZ=0
    g7: LineSegment StartX=-12 StartY=6 StartZ=0 EndX=-2.4 EndY=6 EndZ=0
    g8: LineSegment StartX=-2.4 StartY=6 StartZ=0 EndX=-2.4 EndY=0 EndZ=0
    g9: LineSegment StartX=-2.4 StartY=0 StartZ=0 EndX=0 EndY=0 EndZ=0
  constraints (29):
    c: Vertical(g0)
    c: Coincident(g1,g0)
    c: Horizontal(g1)
    c: Coincident(g2,g1)
    c: Vertical(g2)
    c: Coincident(g3,g2)
    c: Horizontal(g3)
    c: Coincident(g4,g3)
    c: Vertical(g4)
    c: Coincident(g5,g4)
    c: Horizontal(g5)
    c: Coincident(g6,g5)
    c: Vertical(g6)
    c: Coincident(g7,g6)
    c: Coincident(g8,g7)
    c: Vertical(g8)
    c: Coincident(g9,g8)
    c: Coincident(g9,g0)
    c: Horizontal(g9)
    c: DistanceY(g0,g0) = 24.671
    c: Horizontal(g7)
    c: DistanceY(g6,g6) = 4
    c: DistanceY(g4,g4) = 6
    c: DistanceX(g9,g9) = 2.4
    c: Coincident(g0,g-1)
    c: DistanceY(g-3,g7) = 0
    c: DistanceX(g8,g4) = 0
    c: DistanceX(g-3,g1) = 0
    c: DistanceX(g6,g-3) = 8
FEATURE [Part::Extrusion] Extrude010  label="Extrude buco frontale"
  Base = -> Sketch014
  Dir = (0,-1,2e-16)
  DirMode = 2
  FaceMakerClass = Part::FaceMakerBullseye
  FaceMakerMode = 3
  LengthFwd = 11.2
  LengthRev = 0
  Solid = true
  Symmetric = true
FEATURE [Sketcher::SketchObject] Sketch015  label="guida rail"
  ArcFitTolerance = 1e-06
  AttachmentSupport = -> [XZ_Plane]
  ExternalGeometry = -> [Sketch]
  FullyConstrained = true
  MakeInternals = false
  MapMode = 5
  Placement = pos=(0,0,0) rot=(1,0,0;1.5708rad)
  sketch-geometry (4):
    g0: LineSegment StartX=-100.8 StartY=43.2 StartZ=0 EndX=-44.6 EndY=43.2 EndZ=0
    g1: LineSegment StartX=-44.6 StartY=43.2 StartZ=0 EndX=-44.6 EndY=41.2 EndZ=0
    g2: LineSegment StartX=-44.6 StartY=41.2 StartZ=0 EndX=-100.8 EndY=41.2 EndZ=0
    g3: LineSegment StartX=-100.8 StartY=41.2 StartZ=0 EndX=-100.8 EndY=43.2 EndZ=0
  constraints (9):
    c: Horizontal(g0)
    c: Coincident(g1,g0)
    c: Coincident(g2,g1)
    c: Coincident(g3,g2)
    c: Coincident(g3,g0)
    c: Vertical(g3)
    c: Coincident(g2,g-3)
    c: Coincident(g1,g-3)
    c: Coincident(g0,g-4)
FEATURE [Part::Extrusion] Extrude011  label="Extrude guida rail"
  Base = -> Sketch015
  Dir = (0,-1,2e-16)
  DirMode = 2
  FaceMakerClass = Part::FaceMakerBullseye
  FaceMakerMode = 3
  LengthFwd = 9
  LengthRev = 0
  Solid = true
  Symmetric = true
FEATURE [Sketcher::SketchObject] Sketch016  label="guide per coperture laterali"
  ArcFitTolerance = 1e-06
  AttachmentSupport = -> [XZ_Plane]
  ExternalGeometry = -> [Sketch]
  FullyConstrained = true
  MakeInternals = false
  MapMode = 5
  Placement = pos=(0,0,0) rot=(1,0,0;1.5708rad)
  sketch-geometry (14):
    g0: Circle CenterX=-5.6 CenterY=7.6 CenterZ=0 NormalX=0 NormalY=0 NormalZ=1 AngleXU=0 Radius=1.6
    g1: Circle CenterX=-5.6 CenterY=7.6 CenterZ=0 NormalX=0 NormalY=0 NormalZ=1 AngleXU=0 Radius=4
    g2: Circle CenterX=-5.6 CenterY=34.8 CenterZ=0 NormalX=0 NormalY=0 NormalZ=1 AngleXU=0 Radius=1.6
    g3: Circle CenterX=-5.6 CenterY=34.8 CenterZ=0 NormalX=0 NormalY=0 NormalZ=1 AngleXU=0 Radius=4
    g4: Circle CenterX=-184.08 CenterY=34.8 CenterZ=0 NormalX=0 NormalY=0 NormalZ=1 AngleXU=0 Radius=1.6
    g5: Circle CenterX=-184.08 CenterY=34.8 CenterZ=0 NormalX=0 NormalY=0 NormalZ=1 AngleXU=0 Radius=4
    g6: Circle CenterX=-179.305 CenterY=-76.8316 CenterZ=0 NormalX=0 NormalY=0 NormalZ=1 AngleXU=0 Radius=1.6
    g7: Circle CenterX=-179.305 CenterY=-76.8316 CenterZ=0 NormalX=0 NormalY=0 NormalZ=1 AngleXU=0 Radius=4
    g8: Circle CenterX=-213.443 CenterY=-76.8316 CenterZ=0 NormalX=0 NormalY=0 NormalZ=1 AngleXU=0 Radius=1.6
    g9: Circle CenterX=-213.443 CenterY=-76.8316 CenterZ=0 NormalX=0 NormalY=0 NormalZ=1 AngleXU=0 Radius=4
    g10: Circle CenterX=-78.51 CenterY=7.6 CenterZ=0 NormalX=0 NormalY=0 NormalZ=1 AngleXU=0 Radius=1.6
    g11: Circle CenterX=-78.51 CenterY=7.6 CenterZ=0 NormalX=0 NormalY=0 NormalZ=1 AngleXU=0 Radius=4
    g12: Circle CenterX=-78.51 CenterY=34.8 CenterZ=0 NormalX=0 NormalY=0 NormalZ=1 AngleXU=0 Radius=1.6
    g13: Circle CenterX=-78.51 CenterY=34.8 CenterZ=0 NormalX=0 NormalY=0 NormalZ=1 AngleXU=0 Radius=4
  constraints (35):
    c: Diameter(g0) = 3.2
    c: Diameter(g1) = 8
    c: Coincident(g0,g1)
    c: Diameter(g2) = 3.2
    c: Diameter(g3) = 8
    c: Coincident(g3,g2)
    c: Tangent(g2,g-7)
    c: Diameter(g4) = 3.2
    c: Diameter(g5) = 8
    c: Coincident(g5,g4)
    c: Tangent(g4,g-7)
    c: Tangent(g4,g-8)
    c: Diameter(g6) = 3.2
    c: Diameter(g7) = 8
    c: Coincident(g7,g6)
    c: Tangent(g6,g-9)
    c: Tangent(g6,g-10)
    c: Diameter(g8) = 3.2
    c: Diameter(g9) = 8
    c: Coincident(g9,g8)
    c: Tangent(g8,g-10)
    c: Tangent(g8,g-11)
    c: Diameter(g10) = 3.2
    c: Diameter(g11) = 8
    c: Diameter(g12) = 3.2
    c: Diameter(g13) = 8
    c: Coincident(g12,g13)
    c: Coincident(g10,g11)
    c: Tangent(g12,g-7)
    c: DistanceX(g12,g10) = 0
    c: Tangent(g2,g-6)
    c: Tangent(g0,g-6)
    c: Tangent(g0,g-3)
    c: Tangent(g10,g-3)
    c: Tangent(g10,g-4)
FEATURE [Part::Extrusion] Extrude012  label="extrude guide per coperture laterali"
  Base = -> Sketch016
  Dir = (0,-1,2e-16)
  DirMode = 2
  FaceMakerClass = Part::FaceMakerBullseye
  FaceMakerMode = 3
  LengthFwd = 25.2
  LengthRev = 0
  Solid = true
  Symmetric = true
FEATURE [Sketcher::SketchObject] Sketch017  label="supporto CAM"
  ArcFitTolerance = 1e-06
  AttachmentSupport = -> [XZ_Plane]
  ExternalGeometry = -> [Sketch]
  FullyConstrained = true
  MakeInternals = false
  MapMode = 5
  Placement = pos=(0,0,0) rot=(1,0,0;1.5708rad)
  sketch-geometry (6):
    g0: LineSegment StartX=-2.4 StartY=48 StartZ=0 EndX=-2.4 EndY=41.2 EndZ=0
    g1: LineSegment StartX=-2.4 StartY=48 StartZ=0 EndX=-34 EndY=48 EndZ=0
    g2: LineSegment StartX=-34 StartY=48 StartZ=0 EndX=-34 EndY=46.72 EndZ=0
    g3: LineSegment StartX=-34 StartY=46.72 StartZ=0 EndX=-36 EndY=46.72 EndZ=0
    g4: LineSegment StartX=-36 StartY=46.72 StartZ=0 EndX=-36 EndY=41.2 EndZ=0
    g5: LineSegment StartX=-36 StartY=41.2 StartZ=0 EndX=-2.4 EndY=41.2 EndZ=0
  constraints (15):
    c: Coincident(g1,g0)
    c: Horizontal(g1)
    c: Coincident(g2,g1)
    c: Vertical(g2)
    c: Coincident(g3,g2)
    c: Horizontal(g3)
    c: Coincident(g4,g3)
    c: Coincident(g5,g4)
    c: DistanceX(g1,g0) = 31.6
    c: Coincident(g5,g0)
    c: Vertical(g4)
    c: DistanceY(g2,g1) = 1.28
    c: Coincident(g0,g-3)
    c: Coincident(g0,g-3)
    c: Coincident(g4,g-4)
FEATURE [Part::Extrusion] Extrude013  label="Extrude supporto CAM"
  Base = -> Sketch017
  Dir = (0,-1,2e-16)
  DirMode = 2
  FaceMakerClass = Part::FaceMakerBullseye
  FaceMakerMode = 3
  LengthFwd = 17.8
  LengthRev = 0
  Solid = true
  Symmetric = true
FEATURE [Sketcher::SketchObject] Sketch018  label="Scavo CAM"
  ArcFitTolerance = 1e-06
  AttachmentSupport = -> [YZ_Plane]
  ExternalGeometry = -> [Sketch]
  FullyConstrained = true
  MakeInternals = false
  MapMode = 5
  Placement = pos=(0,0,0) rot=(0.57735,0.57735,0.57735;2.0944rad)
  sketch-geometry (4):
    g0: LineSegment StartX=-7.73 StartY=48 StartZ=0 EndX=7.73 EndY=48 EndZ=0
    g1: LineSegment [constr] StartX=1.07e-14 StartY=48 StartZ=0 EndX=0 EndY=43.5155 EndZ=0
    g2: ArcOfCircle CenterX=9e-15 CenterY=52.42 CenterZ=0 NormalX=0 NormalY=0 NormalZ=1 AngleXU=0 Radius=8.90445 StartAngle=3.66102 EndAngle=5.76376
    g3: Circle [constr] CenterX=9e-15 CenterY=52.42 CenterZ=0 NormalX=0 NormalY=0 NormalZ=1 AngleXU=0 Radius=8.9
  constraints (13):
    c: Horizontal(g0)
    c: DistanceY(g-3,g0) = 0
    c: DistanceX(g0,g0) = 15.46
    c: DistanceX(g0,g-3) = 7.73
    c: DistanceX(g-3) = 0
    c: Coincident(g1,g-3)
    c: PointOnObject(g1,g-2)
    c: Coincident(g2,g0)
    c: Coincident(g2,g0)
    c: PointOnObject(g1,g2)
    c: Diameter(g3) = 17.8
    c: DistanceY(g1,g3) = 4.42
    c: Coincident(g2,g3)
FEATURE [Part::Extrusion] Extrude014  label="Extrude Scavo CAM"
  Base = -> Sketch018
  Dir = (1,0,0)
  DirMode = 2
  FaceMakerClass = Part::FaceMakerBullseye
  FaceMakerMode = 3
  LengthFwd = -34
  LengthRev = 0
  Solid = true
  Symmetric = false
FEATURE [Sketcher::SketchObject] Sketch019  label="scavo rumble"
  ArcFitTolerance = 1e-06
  AttachmentSupport = -> [XZ_Plane]
  ExternalGeometry = -> [Sketch]
  FullyConstrained = true
  MakeInternals = false
  MapMode = 5
  Placement = pos=(0,0,0) rot=(1,0,0;1.5708rad)
  sketch-geometry (6):
    g0: LineSegment StartX=-168.716 StartY=-37.1227 StartZ=0 EndX=-163.58 EndY=-38.7914 EndZ=0
    g1: LineSegment StartX=-163.58 StartY=-38.7914 StartZ=0 EndX=-170.687 EndY=-60.6657 EndZ=0
    g2: LineSegment StartX=-170.687 StartY=-60.6657 StartZ=0 EndX=-175.823 EndY=-58.997 EndZ=0
    g3: LineSegment StartX=-175.823 StartY=-58.997 StartZ=0 EndX=-168.716 EndY=-37.1227 EndZ=0
    g4: LineSegment [constr] StartX=-145.51 StartY=22 StartZ=0 EndX=-165.102 EndY=-38.297 EndZ=0
    g5: LineSegment [constr] StartX=-163.58 StartY=-38.7914 StartZ=0 EndX=-165.102 EndY=-38.297 EndZ=0
  constraints (17):
    c: Coincident(g1,g0)
    c: Coincident(g2,g1)
    c: Coincident(g3,g2)
    c: Coincident(g3,g0)
    c: Parallel(g3,g-3)
    c: Parallel(g3,g1)
    c: Perpendicular(g3,g0)
    c: Perpendicular(g2,g3)
    c: Distance(g2,g0) = 23
    c: Parallel(g4,g-3)
    c: Distance(g4) = 63.4
    c: Coincident(g4,g-3)
    c: Parallel(g5,g0)
    c: Coincident(g5,g0)
    c: Coincident(g5,g4)
    c: Distance(g4,g0) = 3.8
    c: Distance(g4,g0) = 1.6
FEATURE [Part::Extrusion] Extrude015  label="scavo rumble001"
  Base = -> Sketch019
  Dir = (0,-1,2e-16)
  DirMode = 2
  FaceMakerClass = Part::FaceMakerBullseye
  FaceMakerMode = 3
  LengthFwd = 21
  LengthRev = 0
  Solid = true
  Symmetric = true
FEATURE [Sketcher::SketchObject] Sketch020  label="fermo rumble"
  ArcFitTolerance = 1e-06
  AttachmentSupport = -> [XZ_Plane]
  ExternalGeometry = -> [Sketch019,Sketch]
  FullyConstrained = true
  MakeInternals = false
  MapMode = 5
  Placement = pos=(0,0,0) rot=(1,0,0;1.5708rad)
  sketch-geometry (16):
    g0: LineSegment [constr] StartX=-170.849 StartY=-55.9866 StartZ=0 EndX=-172.209 EndY=-60.1713 EndZ=0
    g1: LineSegment [constr] StartX=-172.209 StartY=-60.1713 StartZ=0 EndX=-170.687 EndY=-60.6657 EndZ=0
    g2: LineSegment StartX=-172.262 StartY=-53.2145 StartZ=0 EndX=-170.17 EndY=-53.8943 EndZ=0
    g3: LineSegment StartX=-170.17 StartY=-53.8943 StartZ=0 EndX=-170.849 EndY=-55.9866 EndZ=0
    g4: LineSegment StartX=-170.849 StartY=-55.9866 StartZ=0 EndX=-172.942 EndY=-55.3068 EndZ=0
    g5: LineSegment StartX=-172.942 StartY=-55.3068 StartZ=0 EndX=-172.262 EndY=-53.2145 EndZ=0
    g6: LineSegment StartX=-171.767 StartY=-51.6928 StartZ=0 EndX=-168.344 EndY=-52.8052 EndZ=0
    g7: LineSegment StartX=-168.344 StartY=-52.8052 StartZ=0 EndX=-169.951 EndY=-57.7507 EndZ=0
    g8: LineSegment StartX=-169.951 StartY=-57.7507 StartZ=0 EndX=-173.374 EndY=-56.6383 EndZ=0
    g9: LineSegment StartX=-174.402 StartY=-54.6222 StartZ=0 EndX=-173.784 EndY=-52.72 EndZ=0
    g10: LineSegment [constr] StartX=-173.784 StartY=-52.72 StartZ=0 EndX=-173.289 EndY=-51.1984 EndZ=0
    g11: LineSegment [constr] StartX=-173.289 StartY=-51.1984 StartZ=0 EndX=-171.767 EndY=-51.6928 EndZ=0
    g12: ArcOfCircle CenterX=-172.88 CenterY=-55.1166 CenterZ=0 NormalX=0 NormalY=0 NormalZ=1 AngleXU=0 Radius=1.6 StartAngle=2.82743 EndAngle=4.39823
    g13: GeomPoint [constr] X=-174.896 Y=-56.1438 Z=0
    g14: ArcOfCircle CenterX=-172.262 CenterY=-53.2145 CenterZ=0 NormalX=0 NormalY=0 NormalZ=1 AngleXU=0 Radius=1.6 StartAngle=1.25664 EndAngle=2.82743
    g15: GeomPoint [constr] X=-173.289 Y=-51.1984 Z=0
  constraints (42):
    c: Parallel(g0,g-4)
    c: Distance(g0) = 4.4
    c: Coincident(g1,g0)
    c: Perpendicular(g0,g1)
    c: Distance(g1) = 1.6
    c: Coincident(g1,g-5)
    c: Coincident(g3,g2)
    c: Coincident(g4,g3)
    c: Coincident(g5,g4)
    c: Coincident(g5,g2)
    c: Parallel(g3,g-4)
    c: Parallel(g3,g5)
    c: Perpendicular(g2,g3)
    c: Parallel(g4,g2)
    c: Distance(g2) = 2.2
    c: Distance(g3) = 2.2
    c: Coincident(g7,g6)
    c: Coincident(g8,g7)
    c: Parallel(g7,g-4)
    c: Parallel(g7,g9)
    c: Perpendicular(g6,g7)
    c: Parallel(g6,g8)
    c: Distance(g6,g15) = 5.2
    c: Distance(g7) = 5.2
    c: Coincident(g11,g10)
    c: Parallel(g10,g9)
    c: Parallel(g11,g6)
    c: Distance(g10) = 1.6
    c: Distance(g11) = 1.6
    c: Coincident(g10,g15)
    c: Distance(g11,g2) = 1.6
    c: Distance(g2,g10) = 1.6
    c: PointOnObject(g13,g8)
    c: PointOnObject(g13,g9)
    c: Tangent(g8,g12) = 1.5708
    c: Tangent(g9,g12) = 1.5708
    c: PointOnObject(g15,g9)
    c: Tangent(g6,g14) = 1.5708
    c: Tangent(g9,g14) = 1.5708
    c: Equal(g12,g14)
    c: Coincident(g6,g11)
    c: Coincident(g3,g0)
FEATURE [Part::Extrusion] Extrude016  label="Extrude fermo rumble"
  Base = -> Sketch020
  Dir = (0,-1,2e-16)
  DirMode = 2
  FaceMakerClass = Part::FaceMakerBullseye
  FaceMakerMode = 3
  LengthFwd = 25.2
  LengthRev = 0
  Solid = true
  Symmetric = true
FEATURE [Sketcher::SketchObject] Sketch021  label="perno fermo rumble001"
  ArcFitTolerance = 1e-06
  AttachmentSupport = -> [XZ_Plane001]
  FullyConstrained = true
  MakeInternals = false
  MapMode = 5
  Placement = pos=(0,0,0) rot=(1,0,0;1.5708rad)
  sketch-geometry (16):
    g0: LineSegment StartX=0 StartY=0.45 StartZ=0 EndX=0 EndY=1.55 EndZ=0
    g1: LineSegment StartX=0.45 StartY=2 StartZ=0 EndX=1.55 EndY=2 EndZ=0
    g2: LineSegment StartX=2 StartY=1.55 StartZ=0 EndX=2 EndY=0.45 EndZ=0
    g3: LineSegment StartX=1.55 StartY=0 StartZ=0 EndX=0.45 EndY=0 EndZ=0
    g4: ArcOfCircle [constr] CenterX=0.45 CenterY=1.55 CenterZ=0 NormalX=0 NormalY=0 NormalZ=1 AngleXU=0 Radius=0.45 StartAngle=1.5708 EndAngle=3.14159
    g5: GeomPoint [constr] X=0 Y=2 Z=0
    g6: LineSegment StartX=0.45 StartY=2 StartZ=0 EndX=0 EndY=1.55 EndZ=0
    g7: ArcOfCircle [constr] CenterX=1.55 CenterY=1.55 CenterZ=0 NormalX=0 NormalY=0 NormalZ=1 AngleXU=0 Radius=0.45 StartAngle=0 EndAngle=1.5708
    g8: GeomPoint [constr] X=2 Y=2 Z=0
    g9: LineSegment StartX=2 StartY=1.55 StartZ=0 EndX=1.55 EndY=2 EndZ=0
    g10: ArcOfCircle [constr] CenterX=1.55 CenterY=0.45 CenterZ=0 NormalX=0 NormalY=0 NormalZ=1 AngleXU=0 Radius=0.45 StartAngle=4.71239 EndAngle=6.28319
    g11: GeomPoint [constr] X=2 Y=0 Z=0
    g12: LineSegment StartX=1.55 StartY=0 StartZ=0 EndX=2 EndY=0.45 EndZ=0
    g13: ArcOfCircle [constr] CenterX=0.45 CenterY=0.45 CenterZ=0 NormalX=0 NormalY=0 NormalZ=1 AngleXU=0 Radius=0.45 StartAngle=3.14159 EndAngle=4.71239
    g14: GeomPoint [constr] X=0 Y=0 Z=0
    g15: LineSegment StartX=0 StartY=0.45 StartZ=0 EndX=0.45 EndY=0 EndZ=0
  constraints (35):
    c: Coincident(g14,g-1)
    c: PointOnObject(g5,g-2)
    c: Horizontal(g1)
    c: Vertical(g2)
    c: Horizontal(g3)
    c: DistanceX(g5,g8) = 2
    c: DistanceY(g11,g8) = 2
    c: PointOnObject(g5,g0)
    c: PointOnObject(g5,g1)
    c: Tangent(g0,g4) = 1.5708
    c: Tangent(g1,g4) = 1.5708
    c: Coincident(g6,g0)
    c: Coincident(g6,g1)
    c: PointOnObject(g8,g2)
    c: PointOnObject(g8,g1)
    c: Tangent(g2,g7) = 1.5708
    c: Tangent(g1,g7) = 1.5708
    c: Coincident(g9,g2)
    c: Coincident(g9,g1)
    c: PointOnObject(g11,g2)
    c: PointOnObject(g11,g3)
    c: Tangent(g2,g10) = 1.5708
    c: Tangent(g3,g10) = 1.5708
    c: Coincident(g12,g2)
    c: Coincident(g12,g3)
    c: PointOnObject(g14,g0)
    c: PointOnObject(g14,g3)
    c: Tangent(g0,g13) = 1.5708
    c: Tangent(g3,g13) = 1.5708
    c: Coincident(g15,g0)
    c: Coincident(g15,g3)
    c: Equal(g6,g9)
    c: Equal(g9,g12)
    c: Equal(g12,g15)
    c: DistanceX(g14,g3) = 0.45
FEATURE [Sketcher::SketchObject] Sketch022  label="fori per M3x5(OD)x6(L)"
  ArcFitTolerance = 1e-06
  AttachmentSupport = -> [XZ_Plane]
  ExternalGeometry = -> [Sketch016]
  FullyConstrained = true
  MakeInternals = false
  MapMode = 5
  Placement = pos=(0,0,0) rot=(1,0,0;1.5708rad)
  sketch-geometry (7):
    g0: Circle CenterX=-5.6 CenterY=34.8 CenterZ=0 NormalX=0 NormalY=0 NormalZ=1 AngleXU=0 Radius=2.5
    g1: Circle CenterX=-5.6 CenterY=7.6 CenterZ=0 NormalX=0 NormalY=0 NormalZ=1 AngleXU=0 Radius=2.5
    g2: Circle CenterX=-78.51 CenterY=34.8 CenterZ=0 NormalX=0 NormalY=0 NormalZ=1 AngleXU=0 Radius=2.5
    g3: Circle CenterX=-78.51 CenterY=7.6 CenterZ=0 NormalX=0 NormalY=0 NormalZ=1 AngleXU=0 Radius=2.5
    g4: Circle CenterX=-184.08 CenterY=34.8 CenterZ=0 NormalX=0 NormalY=0 NormalZ=1 AngleXU=0 Radius=2.5
    g5: Circle CenterX=-179.305 CenterY=-76.8316 CenterZ=0 NormalX=0 NormalY=0 NormalZ=1 AngleXU=0 Radius=2.5
    g6: Circle CenterX=-213.443 CenterY=-76.8316 CenterZ=0 NormalX=0 NormalY=0 NormalZ=1 AngleXU=0 Radius=2.5
  constraints (14):
    c: Diameter(g0) = 5
    c: Diameter(g1) = 5
    c: Diameter(g2) = 5
    c: Diameter(g3) = 5
    c: Diameter(g4) = 5
    c: Diameter(g5) = 5
    c: Diameter(g6) = 5
    c: Coincident(g0,g-8)
    c: Coincident(g1,g-9)
    c: Coincident(g2,g-6)
    c: Coincident(g3,g-7)
    c: Coincident(g4,g-5)
    c: Coincident(g5,g-4)
    c: Coincident(g6,g-3)
FEATURE [Part::Extrusion] Extrude018  label="Extrude fori M3x5x6 - dx"
  Base = -> Sketch022
  Dir = (0,-1,2e-16)
  DirMode = 2
  FaceMakerClass = Part::FaceMakerBullseye
  FaceMakerMode = 3
  LengthFwd = 6.2
  LengthRev = 0
  Placement = pos=(0,-9.5,0) rot=(0,0,1;0rad)
  Solid = true
  Symmetric = true
FEATURE [Part::Extrusion] Extrude019  label="Extrude fori M3x5x6 - sx"
  Base = -> Sketch022
  Dir = (0,-1,2e-16)
  DirMode = 2
  FaceMakerClass = Part::FaceMakerBullseye
  FaceMakerMode = 3
  LengthFwd = 6.2
  LengthRev = 0
  Placement = pos=(0,9.5,0) rot=(0,0,1;0rad)
  Solid = true
  Symmetric = true
FEATURE [Sketcher::SketchObject] Sketch023  label="foro anteriore M3x5x6"
  ArcFitTolerance = 1e-06
  AttachmentSupport = -> [YZ_Plane]
  FullyConstrained = true
  MakeInternals = false
  MapMode = 5
  Placement = pos=(0,0,0) rot=(0.57735,0.57735,0.57735;2.0944rad)
  sketch-geometry (2):
    g0: LineSegment [constr] StartX=0 StartY=0 StartZ=0 EndX=0 EndY=38.6 EndZ=0
    g1: Circle CenterX=0 CenterY=38.6 CenterZ=0 NormalX=0 NormalY=0 NormalZ=1 AngleXU=0 Radius=2.5
  constraints (5):
    c: Coincident(g0,g-1)
    c: PointOnObject(g0,g-2)
    c: DistanceY(g0,g0) = 38.6
    c: Diameter(g1) = 5
    c: Coincident(g1,g0)
FEATURE [Part::Extrusion] Extrude020  label="Extrude foro anteriore M3x5x6"
  Base = -> Sketch023
  Dir = (1,0,0)
  DirMode = 2
  FaceMakerClass = Part::FaceMakerBullseye
  FaceMakerMode = 3
  LengthFwd = -6.2
  LengthRev = 0
  Solid = true
  Symmetric = false
FEATURE [Sketcher::SketchObject] Sketch024  label="fori per viti frontale"
  ArcFitTolerance = 1e-06
  AttachmentSupport = -> [YZ_Plane]
  FullyConstrained = true
  MakeInternals = false
  MapMode = 5
  Placement = pos=(0,0,0) rot=(0.57735,0.57735,0.57735;2.0944rad)
  sketch-geometry (9):
    g0: LineSegment [constr] StartX=-10.3 StartY=30.721 StartZ=0 EndX=10.3 EndY=30.721 EndZ=0
    g1: LineSegment [constr] StartX=10.3 StartY=30.721 StartZ=0 EndX=10.3 EndY=10.121 EndZ=0
    g2: LineSegment [constr] StartX=10.3 StartY=10.121 StartZ=0 EndX=-10.3 EndY=10.121 EndZ=0
    g3: LineSegment [constr] StartX=-10.3 StartY=10.121 StartZ=0 EndX=-10.3 EndY=30.721 EndZ=0
    g4: LineSegment [constr] StartX=0 StartY=0 StartZ=0 EndX=0 EndY=10.121 EndZ=0
    g5: Circle CenterX=-10.3 CenterY=30.721 CenterZ=0 NormalX=0 NormalY=0 NormalZ=1 AngleXU=0 Radius=2
    g6: Circle CenterX=10.3 CenterY=30.721 CenterZ=0 NormalX=0 NormalY=0 NormalZ=1 AngleXU=0 Radius=2
    g7: Circle CenterX=-10.3 CenterY=10.121 CenterZ=0 NormalX=0 NormalY=0 NormalZ=1 AngleXU=0 Radius=2
    g8: Circle CenterX=10.3 CenterY=10.121 CenterZ=0 NormalX=0 NormalY=0 NormalZ=1 AngleXU=0 Radius=2
  constraints (22):
    c: Horizontal(g0)
    c: Coincident(g1,g0)
    c: Vertical(g1)
    c: Coincident(g2,g1)
    c: Horizontal(g2)
    c: Coincident(g3,g2)
    c: Coincident(g3,g0)
    c: Vertical(g3)
    c: DistanceX(g0,g0) = 20.6
    c: DistanceY(g3,g3) = 20.6
    c: Coincident(g4,g-1)
    c: PointOnObject(g4,g-2)
    c: DistanceY(g4,g4) = 10.121
    c: Symmetric(g2,g2,g4)
    c: Diameter(g5) = 4
    c: Diameter(g6) = 4
    c: Diameter(g7) = 4
    c: Diameter(g8) = 4
    c: Coincident(g5,g0)
    c: Coincident(g6,g0)
    c: Coincident(g7,g2)
    c: Coincident(g8,g1)
FEATURE [Part::Extrusion] Extrude021  label="Extrude fori per viti frontale"
  Base = -> Sketch024
  Dir = (1,0,0)
  DirMode = 2
  FaceMakerClass = Part::FaceMakerBullseye
  FaceMakerMode = 3
  LengthFwd = -2.4
  LengthRev = 0
  Solid = true
  Symmetric = false
FEATURE [Sketcher::SketchObject] Sketch025  label="foro per filo CAM"
  ArcFitTolerance = 1e-06
  AttachmentSupport = -> [XZ_Plane]
  ExternalGeometry = -> [Sketch]
  FullyConstrained = true
  MakeInternals = false
  MapMode = 5
  Placement = pos=(0,0,0) rot=(1,0,0;1.5708rad)
  sketch-geometry (4):
    g0: LineSegment StartX=-44.6 StartY=41.2 StartZ=0 EndX=-44.6 EndY=36.4 EndZ=0
    g1: LineSegment StartX=-44.6 StartY=36.4 StartZ=0 EndX=-54.6 EndY=36.4 EndZ=0
    g2: LineSegment StartX=-54.6 StartY=36.4 StartZ=0 EndX=-50.4 EndY=41.2 EndZ=0
    g3: LineSegment StartX=-50.4 StartY=41.2 StartZ=0 EndX=-44.6 EndY=41.2 EndZ=0
  constraints (11):
    c: Vertical(g0)
    c: Coincident(g1,g0)
    c: Horizontal(g1)
    c: Coincident(g2,g1)
    c: Coincident(g3,g2)
    c: Coincident(g3,g0)
    c: Horizontal(g3)
    c: Coincident(g0,g-3)
    c: DistanceY(g0,g-4) = 0
    c: DistanceX(g3,g3) = 5.8
    c: DistanceX(g1,g1) = 10
FEATURE [Part::Extrusion] Extrude022  label="Extrude foro per filo CAM dx"
  Base = -> Sketch025
  Dir = (0,-1,2e-16)
  DirMode = 2
  FaceMakerClass = Part::FaceMakerBullseye
  FaceMakerMode = 3
  LengthFwd = 4.9
  LengthRev = 0
  Placement = pos=(0,6.95,0) rot=(0,0,1;0rad)
  Solid = true
  Symmetric = true
FEATURE [Part::Extrusion] Extrude023  label="Extrude foro per filo CAM sx"
  Base = -> Sketch025
  Dir = (0,-1,2e-16)
  DirMode = 2
  FaceMakerClass = Part::FaceMakerBullseye
  FaceMakerMode = 3
  LengthFwd = 4.9
  LengthRev = 0
  Placement = pos=(0,-6.95,0) rot=(0,0,1;0rad)
  Solid = true
  Symmetric = true
FEATURE [Sketcher::SketchObject] Sketch026  label="foro sotto anteriore M3x5x6"
  ArcFitTolerance = 1e-06
  AttachmentSupport = -> [XY_Plane]
  FullyConstrained = true
  MakeInternals = false
  MapMode = 5
  sketch-geometry (2):
    g0: LineSegment [constr] StartX=0 StartY=0 StartZ=0 EndX=-16.5 EndY=0 EndZ=0
    g1: Circle CenterX=-16.5 CenterY=0 CenterZ=0 NormalX=0 NormalY=0 NormalZ=1 AngleXU=0 Radius=2.5
  constraints (5):
    c: Distance(g0) = 16.5
    c: Coincident(g0,g-1)
    c: PointOnObject(g0,g-1)
    c: Diameter(g1) = 5
    c: Coincident(g0,g1)
FEATURE [Sketcher::SketchObject] Sketch027  label="foro sotto posteriore M3x5x6"
  ArcFitTolerance = 1e-06
  AttachmentSupport = -> [XY_Plane]
  ExternalGeometry = -> [Sketch]
  FullyConstrained = true
  MakeInternals = false
  MapMode = 5
  sketch-geometry (2):
    g0: LineSegment [constr] StartX=-82.8 StartY=2e-16 StartZ=0 EndX=-71.3 EndY=2e-16 EndZ=0
    g1: Circle CenterX=-71.3 CenterY=2e-16 CenterZ=0 NormalX=0 NormalY=0 NormalZ=1 AngleXU=0 Radius=2.5
  constraints (5):
    c: Distance(g0) = 11.5
    c: Coincident(g0,g-3)
    c: PointOnObject(g0,g-3)
    c: Diameter(g1) = 5
    c: Coincident(g1,g0)
FEATURE [Sketcher::SketchObject] Sketch029  label="fori sotto impugnatura"
  ArcFitTolerance = 1e-06
  AttachmentSupport = -> [XY_Plane]
  ExternalGeometry = -> [Sketch]
  FullyConstrained = true
  MakeInternals = false
  MapMode = 5
  sketch-geometry (15):
    g0: LineSegment [constr] StartX=-175.232 StartY=-1.83e-14 StartZ=0 EndX=-191.232 EndY=0 EndZ=0
    g1: Circle CenterX=-191.232 CenterY=0 CenterZ=0 NormalX=0 NormalY=0 NormalZ=1 AngleXU=0 Radius=3.95
    g2: LineSegment [constr] StartX=-175.232 StartY=-1.83e-14 StartZ=0 EndX=-204.275 EndY=0 EndZ=0
    g3: LineSegment StartX=-204.275 StartY=3.525 StartZ=0 EndX=-204.275 EndY=-3.525 EndZ=0
    g4: LineSegment StartX=-205.4 StartY=-4.65 StartZ=0 EndX=-206.65 EndY=-4.65 EndZ=0
    g5: LineSegment StartX=-207.775 StartY=-3.525 StartZ=0 EndX=-207.775 EndY=3.525 EndZ=0
    g6: LineSegment StartX=-206.65 StartY=4.65 StartZ=0 EndX=-205.4 EndY=4.65 EndZ=0
    g7: ArcOfCircle CenterX=-206.65 CenterY=3.525 CenterZ=0 NormalX=0 NormalY=0 NormalZ=1 AngleXU=0 Radius=1.125 StartAngle=1.5708 EndAngle=3.14159
    g8: GeomPoint [constr] X=-207.775 Y=4.65 Z=0
    g9: ArcOfCircle CenterX=-205.4 CenterY=3.525 CenterZ=0 NormalX=0 NormalY=0 NormalZ=1 AngleXU=0 Radius=1.125 StartAngle=0 EndAngle=1.5708
    g10: GeomPoint [constr] X=-204.275 Y=4.65 Z=0
    g11: ArcOfCircle CenterX=-205.4 CenterY=-3.525 CenterZ=0 NormalX=0 NormalY=0 NormalZ=1 AngleXU=0 Radius=1.125 StartAngle=4.71239 EndAngle=6.28319
    g12: GeomPoint [constr] X=-204.275 Y=-4.65 Z=0
    g13: ArcOfCircle CenterX=-206.65 CenterY=-3.525 CenterZ=0 NormalX=0 NormalY=0 NormalZ=1 AngleXU=0 Radius=1.125 StartAngle=3.14159 EndAngle=4.71239
    g14: GeomPoint [constr] X=-207.775 Y=-4.65 Z=0
  constraints (35):
    c: Distance(g0) = 16
    c: Coincident(g0,g-3)
    c: PointOnObject(g0,g-1)
    c: Diameter(g1) = 7.9
    c: Coincident(g1,g0)
    c: Coincident(g2,g0)
    c: PointOnObject(g2,g-1)
    c: Vertical(g3)
    c: Horizontal(g4)
    c: Vertical(g5)
    c: Horizontal(g6)
    c: DistanceY(g12,g10) = 9.3
    c: DistanceX(g8,g10) = 3.5
    c: Symmetric(g10,g12,g2)
    c: PointOnObject(g8,g5)
    c: PointOnObject(g8,g6)
    c: Tangent(g5,g7) = 1.5708
    c: Tangent(g6,g7) = 1.5708
    c: PointOnObject(g10,g3)
    c: PointOnObject(g10,g6)
    c: Tangent(g3,g9) = 1.5708
    c: Tangent(g6,g9) = 1.5708
    c: PointOnObject(g12,g3)
    c: PointOnObject(g12,g4)
    c: Tangent(g3,g11) = 1.5708
    c: Tangent(g4,g11) = 1.5708
    c: PointOnObject(g14,g4)
    c: PointOnObject(g14,g5)
    c: Tangent(g4,g13) = 1.5708
    c: Tangent(g5,g13) = 1.5708
    c: Equal(g7,g9)
    c: Equal(g9,g11)
    c: Equal(g11,g13)
    c: DistanceX(g6,g6) = 1.25
    c: DistanceX(g-5,g5) = 6.8
FEATURE [Sketcher::SketchObject] Sketch030  label="fori superiori per solenoide e oled"
  ArcFitTolerance = 1e-06
  AttachmentSupport = -> [XY_Plane]
  ExternalGeometry = -> [Sketch]
  FullyConstrained = true
  MakeInternals = false
  MapMode = 5
  sketch-geometry (33):
    g0: LineSegment [constr] StartX=-181.6 StartY=1.12e-14 StartZ=0 EndX=-169.91 EndY=0 EndZ=0
    g1: LineSegment [constr] StartX=-169.91 StartY=0 StartZ=0 EndX=-169.91 EndY=-2.6 EndZ=0
    g2: LineSegment [constr] StartX=-169.91 StartY=0 StartZ=0 EndX=-169.91 EndY=2.6 EndZ=0
    g3: LineSegment StartX=-169.91 StartY=4.975 StartZ=0 EndX=-169.91 EndY=8.225 EndZ=0
    g4: LineSegment StartX=-167.535 StartY=10.6 StartZ=0 EndX=-167.285 EndY=10.6 EndZ=0
    g5: LineSegment StartX=-164.91 StartY=8.225 StartZ=0 EndX=-164.91 EndY=4.975 EndZ=0
    g6: LineSegment StartX=-167.285 StartY=2.6 StartZ=0 EndX=-167.535 EndY=2.6 EndZ=0
    g7: LineSegment StartX=-169.91 StartY=-4.975 StartZ=0 EndX=-169.91 EndY=-8.225 EndZ=0
    g8: LineSegment StartX=-167.535 StartY=-10.6 StartZ=0 EndX=-167.285 EndY=-10.6 EndZ=0
    g9: LineSegment StartX=-164.91 StartY=-8.225 StartZ=0 EndX=-164.91 EndY=-4.975 EndZ=0
    g10: LineSegment StartX=-167.285 StartY=-2.6 StartZ=0 EndX=-167.535 EndY=-2.6 EndZ=0
    g11: ArcOfCircle CenterX=-167.535 CenterY=8.225 CenterZ=0 NormalX=0 NormalY=0 NormalZ=1 AngleXU=0 Radius=2.375 StartAngle=1.5708 EndAngle=3.14159
    g12: GeomPoint [constr] X=-169.91 Y=10.6 Z=0
    g13: ArcOfCircle CenterX=-167.285 CenterY=8.225 CenterZ=0 NormalX=0 NormalY=0 NormalZ=1 AngleXU=0 Radius=2.375 StartAngle=0 EndAngle=1.5708
    g14: GeomPoint [constr] X=-164.91 Y=10.6 Z=0
    g15: ArcOfCircle CenterX=-167.285 CenterY=4.975 CenterZ=0 NormalX=0 NormalY=0 NormalZ=1 AngleXU=0 Radius=2.375 StartAngle=4.71239 EndAngle=6.28319
    g16: GeomPoint [constr] X=-164.91 Y=2.6 Z=0
    g17: ArcOfCircle CenterX=-167.535 CenterY=4.975 CenterZ=0 NormalX=0 NormalY=0 NormalZ=1 AngleXU=0 Radius=2.375 StartAngle=3.14159 EndAngle=4.71239
    g18: GeomPoint [constr] X=-169.91 Y=2.6 Z=0
    g19: ArcOfCircle CenterX=-167.535 CenterY=-4.975 CenterZ=0 NormalX=0 NormalY=0 NormalZ=1 AngleXU=0 Radius=2.375 StartAngle=1.5708 EndAngle=3.14159
    g20: GeomPoint [constr] X=-169.91 Y=-2.6 Z=0
    g21: ArcOfCircle CenterX=-167.285 CenterY=-4.975 CenterZ=0 NormalX=0 NormalY=0 NormalZ=1 AngleXU=0 Radius=2.375 StartAngle=0 EndAngle=1.5708
    g22: GeomPoint [constr] X=-164.91 Y=-2.6 Z=0
    g23: ArcOfCircle CenterX=-167.285 CenterY=-8.225 CenterZ=0 NormalX=0 NormalY=0 NormalZ=1 AngleXU=0 Radius=2.375 StartAngle=4.71239 EndAngle=6.28319
    g24: GeomPoint [constr] X=-164.91 Y=-10.6 Z=0
    g25: ArcOfCircle CenterX=-167.535 CenterY=-8.225 CenterZ=0 NormalX=0 NormalY=0 NormalZ=1 AngleXU=0 Radius=2.375 StartAngle=3.14159 EndAngle=4.71239
    g26: GeomPoint [constr] X=-169.91 Y=-10.6 Z=0
    g27: LineSegment [constr] StartX=-181.6 StartY=1.12e-14 StartZ=0 EndX=-152.209 EndY=0 EndZ=0
    g28: LineSegment [constr] StartX=-181.6 StartY=1.12e-14 StartZ=0 EndX=-130.41 EndY=0 EndZ=0
    g29: LineSegment [constr] StartX=-152.209 StartY=0 StartZ=0 EndX=-152.209 EndY=6.95 EndZ=0
    g30: LineSegment [constr] StartX=-130.41 StartY=0 StartZ=0 EndX=-130.41 EndY=-6.95 EndZ=0
    g31: Circle CenterX=-152.209 CenterY=6.95 CenterZ=0 NormalX=0 NormalY=0 NormalZ=1 AngleXU=0 Radius=2.1
    g32: Circle CenterX=-130.41 CenterY=-6.95 CenterZ=0 NormalX=0 NormalY=0 NormalZ=1 AngleXU=0 Radius=2.1
  constraints (79):
    c: Distance(g0) = 11.69
    c: PointOnObject(g0,g-1)
    c: Coincident(g-4,g0)
    c: Distance(g1) = 2.6
    c: Coincident(g1,g0)
    c: Vertical(g1)
    c: Distance(g2) = 2.6
    c: Coincident(g2,g0)
    c: Vertical(g2)
    c: Distance(g18,g12) = 8
    c: Coincident(g18,g2)
    c: Vertical(g3)
    c: Distance(g14,g12) = 5
    c: Horizontal(g4)
    c: Distance(g16,g14) = 8
    c: Vertical(g5)
    c: Distance(g26,g20) = 8
    c: Coincident(g20,g1)
    c: Vertical(g7)
    c: Distance(g26,g24) = 5
    c: Horizontal(g8)
    c: Distance(g24,g22) = 8
    c: Vertical(g9)
    c: PointOnObject(g12,g3)
    c: PointOnObject(g12,g4)
    c: Tangent(g3,g11) = 1.5708
    c: Tangent(g4,g11) = 1.5708
    c: PointOnObject(g14,g5)
    c: PointOnObject(g14,g4)
    c: Tangent(g5,g13) = 1.5708
    c: Tangent(g4,g13) = 1.5708
    c: PointOnObject(g16,g5)
    c: PointOnObject(g16,g6)
    c: Tangent(g5,g15) = 1.5708
    c: Tangent(g6,g15) = 1.5708
    c: PointOnObject(g18,g3)
    c: PointOnObject(g18,g6)
    c: Tangent(g3,g17) = 1.5708
    c: Tangent(g6,g17) = 1.5708
    c: Equal(g11,g13)
    c: Equal(g13,g15)
    c: Equal(g15,g17)
    c: DistanceX(g4,g4) = 0.25
    c: PointOnObject(g20,g7)
    c: PointOnObject(g20,g10)
    c: Tangent(g7,g19) = -1.5708
    c: Tangent(g10,g19) = -1.5708
    c: PointOnObject(g22,g9)
    c: PointOnObject(g22,g10)
    c: Tangent(g9,g21) = -1.5708
    c: Tangent(g10,g21) = -1.5708
    c: PointOnObject(g24,g9)
    c: PointOnObject(g24,g8)
    c: Tangent(g9,g23) = -1.5708
    c: Tangent(g8,g23) = -1.5708
    c: PointOnObject(g26,g8)
    c: PointOnObject(g26,g7)
    c: Tangent(g8,g25) = -1.5708
    c: Tangent(g7,g25) = -1.5708
    c: Equal(g19,g21)
    c: Equal(g21,g23)
    c: Equal(g23,g25)
    c: DistanceX(g10,g10) = 0.25
    c: Distance(g27) = 29.391
    c: Coincident(g27,g0)
    c: PointOnObject(g27,g-1)
    c: Distance(g28) = 51.19
    c: Coincident(g28,g0)
    c: PointOnObject(g28,g-1)
    c: Distance(g29) = 6.95
    c: Coincident(g29,g27)
    c: Vertical(g29)
    c: Distance(g30) = 6.95
    c: Coincident(g30,g28)
    c: Vertical(g30)
    c: Diameter(g31) = 4.2
    c: Diameter(g32) = 4.2
    c: Coincident(g32,g30)
    c: Coincident(g31,g29)
FEATURE [Sketcher::SketchObject] Sketch031  label="fori inferiori switch pompa"
  ArcFitTolerance = 1e-06
  AttachmentSupport = -> [XY_Plane]
  ExternalGeometry = -> [Sketch]
  FullyConstrained = true
  MakeInternals = false
  MapMode = 5
  sketch-geometry (4):
    g0: LineSegment [constr] StartX=-57.2 StartY=1.9e-15 StartZ=0 EndX=-62.45 EndY=1.9e-15 EndZ=0
    g1: LineSegment [constr] StartX=-62.45 StartY=3.25 StartZ=0 EndX=-62.45 EndY=-3.25 EndZ=0
    g2: Circle CenterX=-62.45 CenterY=3.25 CenterZ=0 NormalX=0 NormalY=0 NormalZ=1 AngleXU=0 Radius=1.6
    g3: Circle CenterX=-62.45 CenterY=-3.25 CenterZ=0 NormalX=0 NormalY=0 NormalZ=1 AngleXU=0 Radius=1.6
  constraints (10):
    c: Distance(g0) = 5.25
    c: Coincident(g0,g-3)
    c: PointOnObject(g0,g-3)
    c: Vertical(g1)
    c: DistanceY(g1,g1) = 6.5
    c: Symmetric(g1,g1,g0)
    c: Diameter(g2) = 3.2
    c: Diameter(g3) = 3.2
    c: Coincident(g2,g1)
    c: Coincident(g3,g1)
FEATURE [Sketcher::SketchObject] Sketch032  label="spazio per PILA 18650"
  ArcFitTolerance = 1e-06
  AttachmentSupport = -> [XY_Plane]
  ExternalGeometry = -> [Sketch]
  FullyConstrained = true
  MakeInternals = false
  MapMode = 5
  sketch-geometry (2):
    g0: LineSegment [constr] StartX=-178.142 StartY=-1.74e-14 StartZ=0 EndX=-191.142 EndY=-1.83e-14 EndZ=0
    g1: Circle CenterX=-191.142 CenterY=-1.83e-14 CenterZ=0 NormalX=0 NormalY=0 NormalZ=1 AngleXU=0 Radius=10.5
  constraints (5):
    c: Distance(g0) = 13
    c: Coincident(g0,g-3)
    c: PointOnObject(g0,g-4)
    c: Diameter(g1) = 21
    c: Coincident(g1,g0)
FEATURE [Part::Extrusion] Extrude030  label="Extrude spazio per PILA 18650"
  Base = -> Sketch032
  Dir = (0,0,1)
  DirLink = -> Sketch [Edge45]
  DirMode = 2
  FaceMakerClass = Part::FaceMakerBullseye
  FaceMakerMode = 3
  LengthFwd = 76
  LengthRev = 0
  Placement = pos=(6,0,-72) rot=(0,0,1;0rad)
  Solid = true
  Symmetric = false
FEATURE [Sketcher::SketchObject] Sketch033  label="fermo per scheda micro"
  ArcFitTolerance = 1e-06
  AttachmentSupport = -> [XZ_Plane]
  ExternalGeometry = -> [Sketch]
  FullyConstrained = true
  MakeInternals = false
  MapMode = 5
  Placement = pos=(0,0,0) rot=(1,0,0;1.5708rad)
  sketch-geometry (12):
    g0: LineSegment StartX=-11.6 StartY=6 StartZ=0 EndX=-4 EndY=6 EndZ=0
    g1: LineSegment StartX=-4 StartY=6 StartZ=0 EndX=-4 EndY=36.4 EndZ=0
    g2: LineSegment StartX=-4 StartY=36.4 StartZ=0 EndX=-11.6 EndY=36.4 EndZ=0
    g3: LineSegment StartX=-11.6 StartY=36.4 StartZ=0 EndX=-11.6 EndY=6 EndZ=0
    g4: LineSegment StartX=-80.11 StartY=11.6 StartZ=0 EndX=-70.51 EndY=11.6 EndZ=0
    g5: LineSegment StartX=-70.51 StartY=11.6 StartZ=0 EndX=-70.51 EndY=6 EndZ=0
    g6: LineSegment StartX=-70.51 StartY=6 StartZ=0 EndX=-80.11 EndY=6 EndZ=0
    g7: LineSegment StartX=-80.11 StartY=6 StartZ=0 EndX=-80.11 EndY=11.6 EndZ=0
    g8: LineSegment StartX=-78.51 StartY=36.4 StartZ=0 EndX=-70.51 EndY=36.4 EndZ=0
    g9: LineSegment StartX=-70.51 StartY=36.4 StartZ=0 EndX=-70.51 EndY=30.8 EndZ=0
    g10: LineSegment StartX=-70.51 StartY=30.8 StartZ=0 EndX=-78.51 EndY=30.8 EndZ=0
    g11: LineSegment StartX=-78.51 StartY=30.8 StartZ=0 EndX=-78.51 EndY=36.4 EndZ=0
  constraints (33):
    c: Horizontal(g0)
    c: Coincident(g1,g0)
    c: Coincident(g2,g1)
    c: Horizontal(g2)
    c: Coincident(g3,g2)
    c: Coincident(g3,g0)
    c: Vertical(g3)
    c: DistanceX(g2,g2) = 7.6
    c: Coincident(g1,g-3)
    c: Coincident(g0,g-3)
    c: Horizontal(g4)
    c: Coincident(g5,g4)
    c: Vertical(g5)
    c: Coincident(g6,g5)
    c: Horizontal(g6)
    c: Coincident(g7,g6)
    c: Coincident(g7,g4)
    c: Vertical(g7)
    c: DistanceY(g5,g5) = 5.6
    c: DistanceX(g4,g4) = 9.6
    c: Coincident(g9,g8)
    c: Vertical(g9)
    c: Coincident(g10,g9)
    c: Horizontal(g10)
    c: Coincident(g11,g10)
    c: Coincident(g11,g8)
    c: Vertical(g11)
    c: DistanceY(g9,g9) = 5.6
    c: DistanceX(g10,g10) = 8
    c: Coincident(g4,g-4)
    c: DistanceX(g4,g10) = 1.6
    c: Horizontal(g8)
    c: DistanceY(g8,g1) = 0
FEATURE [Sketcher::SketchObject] Sketch034  label="buchi guida rail"
  ArcFitTolerance = 1e-06
  AttachmentSupport = -> [XY_Plane]
  ExternalGeometry = -> [Sketch]
  FullyConstrained = true
  MakeInternals = false
  MapMode = 5
  sketch-geometry (6):
    g0: LineSegment [constr] StartX=-100.8 StartY=9.1e-15 StartZ=0 EndX=-93.3 EndY=0 EndZ=0
    g1: LineSegment [constr] StartX=-93.3 StartY=0 StartZ=0 EndX=-73.3 EndY=0 EndZ=0
    g2: LineSegment [constr] StartX=-73.3 StartY=0 StartZ=0 EndX=-53.3 EndY=0 EndZ=0
    g3: Circle CenterX=-93.3 CenterY=0 CenterZ=0 NormalX=0 NormalY=0 NormalZ=1 AngleXU=0 Radius=2.5
    g4: Circle CenterX=-73.3 CenterY=0 CenterZ=0 NormalX=0 NormalY=0 NormalZ=1 AngleXU=0 Radius=2.5
    g5: Circle CenterX=-53.3 CenterY=0 CenterZ=0 NormalX=0 NormalY=0 NormalZ=1 AngleXU=0 Radius=2.5
  constraints (15):
    c: Distance(g0) = 7.5
    c: Coincident(g0,g-3)
    c: PointOnObject(g0,g-1)
    c: Distance(g1) = 20
    c: Coincident(g1,g0)
    c: PointOnObject(g1,g-1)
    c: Distance(g2) = 20
    c: Coincident(g2,g1)
    c: PointOnObject(g2,g-1)
    c: Diameter(g3) = 5
    c: Diameter(g4) = 5
    c: Diameter(g5) = 5
    c: Coincident(g3,g0)
    c: Coincident(g4,g1)
    c: Coincident(g5,g2)
FEATURE [Part::Extrusion] Extrude032  label="Extrude buchi guida rail"
  Base = -> Sketch034
  Dir = (0,0,1)
  DirMode = 2
  FaceMakerClass = Part::FaceMakerBullseye
  FaceMakerMode = 3
  LengthFwd = -6.2
  LengthRev = 0
  Placement = pos=(0,0,43.2) rot=(0,0,1;0rad)
  Solid = true
  Symmetric = false
FEATURE [Part::Extrusion] Extrude033  label="Extrude fori superiori per solenoide e oled001"
  Base = -> Sketch030
  Dir = (0,0,1)
  DirMode = 2
  FaceMakerClass = Part::FaceMakerBullseye
  FaceMakerMode = 3
  LengthFwd = -4.8
  LengthRev = 0
  Placement = pos=(0,0,41.2) rot=(0,0,1;0rad)
  Solid = true
  Symmetric = false
FEATURE [Part::Extrusion] Extrude034  label="Extrude fori sotto impugnatura001"
  Base = -> Sketch029
  Dir = (0,0,1)
  DirMode = 2
  FaceMakerClass = Part::FaceMakerBullseye
  FaceMakerMode = 3
  LengthFwd = 5
  LengthRev = 0
  Placement = pos=(0,0,-83) rot=(0,0,1;0rad)
  Solid = true
  Symmetric = false
FEATURE [Part::Extrusion] Extrude035  label="Extrude fori inferiori switch pompa001"
  Base = -> Sketch031
  Dir = (0,0,1)
  DirMode = 2
  FaceMakerClass = Part::FaceMakerBullseye
  FaceMakerMode = 3
  LengthFwd = 4
  LengthRev = 0
  Placement = pos=(0,0,-1.7) rot=(0,0,1;0rad)
  Solid = true
  Symmetric = false
FEATURE [Part::Extrusion] Extrude036  label="Extrude foro sotto posteriore M3x5x007"
  Base = -> Sketch027
  Dir = (0,0,1)
  DirMode = 2
  FaceMakerClass = Part::FaceMakerBullseye
  FaceMakerMode = 3
  LengthFwd = 6.2
  LengthRev = 0
  Placement = pos=(0,0,-9.6) rot=(0,0,1;0rad)
  Solid = true
  Symmetric = false
FEATURE [Part::Extrusion] Extrude037  label="Extrude foro sotto anteriore M3x5x007"
  Base = -> Sketch026
  Dir = (0,0,1)
  DirMode = 2
  FaceMakerClass = Part::FaceMakerBullseye
  FaceMakerMode = 3
  LengthFwd = 6.2
  LengthRev = 0
  Solid = true
  Symmetric = false
FEATURE [Sketcher::SketchObject] Sketch035  label="foro per fissaggio micro"
  ArcFitTolerance = 1e-06
  AttachmentSupport = -> [XZ_Plane]
  ExternalGeometry = -> [Sketch,Sketch033]
  FullyConstrained = true
  MakeInternals = false
  MapMode = 5
  Placement = pos=(0,0,0) rot=(1,0,0;1.5708rad)
  sketch-geometry (3):
    g0: Circle CenterX=-7.8 CenterY=21.2 CenterZ=0 NormalX=0 NormalY=0 NormalZ=1 AngleXU=0 Radius=1.6
    g1: GeomPoint [constr] X=-4 Y=21.2 Z=0
    g2: LineSegment [constr] StartX=-4 StartY=21.2 StartZ=0 EndX=-11.6 EndY=21.2 EndZ=0
  constraints (6):
    c: Diameter(g0) = 3.2
    c: Symmetric(g-3,g-3,g1)
    c: Coincident(g2,g1)
    c: Horizontal(g2)
    c: DistanceX(g-4,g2) = 0
    c: Symmetric(g2,g1,g0)
FEATURE [Part::Extrusion] Extrude038  label="Extrude foro per fissaggio micro"
  Base = -> Sketch035
  Dir = (0,-1,2e-16)
  DirMode = 2
  FaceMakerClass = Part::FaceMakerBullseye
  FaceMakerMode = 3
  LengthFwd = 3
  LengthRev = 0
  Placement = pos=(0,8.6,0) rot=(0,0,1;0rad)
  Solid = true
  Symmetric = false
FEATURE [Sketcher::SketchObject] Sketch036  label="supporto per alimentatore"
  ArcFitTolerance = 1e-06
  AttachmentSupport = -> [XZ_Plane]
  ExternalGeometry = -> [Sketch,Sketch016,Sketch022]
  FullyConstrained = true
  MakeInternals = false
  MapMode = 5
  Placement = pos=(0,0,0) rot=(1,0,0;1.5708rad)
  sketch-geometry (5):
    g0: LineSegment StartX=-211.843 StartY=-50.0944 StartZ=0 EndX=-211.843 EndY=-80.4316 EndZ=0
    g1: LineSegment StartX=-211.843 StartY=-50.0944 StartZ=0 EndX=-207.775 EndY=-41.3701 EndZ=0
    g2: LineSegment [constr] StartX=-209.443 StartY=-50.0944 StartZ=0 EndX=-209.443 EndY=-80.4316 EndZ=0
    g3: LineSegment StartX=-207.775 StartY=-41.3701 StartZ=0 EndX=-207.775 EndY=-80.4316 EndZ=0
    g4: LineSegment StartX=-211.843 StartY=-80.4316 StartZ=0 EndX=-207.775 EndY=-80.4316 EndZ=0
  constraints (15):
    c: Vertical(g0)
    c: Coincident(g1,g0)
    c: Vertical(g2)
    c: Tangent(g2,g-5)
    c: Coincident(g3,g1)
    c: Vertical(g3)
    c: DistanceY(g-3,g3) = -2
    c: Tangent(g1,g-8)
    c: DistanceY(g-3,g0) = -2
    c: Coincident(g4,g0)
    c: Coincident(g4,g3)
    c: Tangent(g0,g-6)
    c: DistanceY(g-3,g2) = -2
    c: DistanceY(g2,g0) = 0
    c: DistanceX(g-3,g3) = 6.8
FEATURE [Part::Extrusion] Extrude039  label="Extrude039 supporto alimentatore"
  Base = -> Sketch036
  Dir = (0,-1,2e-16)
  DirMode = 2
  FaceMakerClass = Part::FaceMakerBullseye
  FaceMakerMode = 3
  LengthFwd = 25.2
  LengthRev = 0
  Solid = true
  Symmetric = true
FEATURE [Sketcher::SketchObject] Sketch037  label="scavo per alimentatore"
  ArcFitTolerance = 1e-06
  AttachmentSupport = -> [XZ_Plane]
  ExternalGeometry = -> [Sketch036]
  FullyConstrained = true
  MakeInternals = false
  MapMode = 5
  Placement = pos=(0,0,0) rot=(1,0,0;1.5708rad)
  sketch-geometry (4):
    g0: LineSegment StartX=-209.575 StartY=-50.4316 StartZ=0 EndX=-209.575 EndY=-80.4316 EndZ=0
    g1: LineSegment StartX=-209.575 StartY=-50.4316 StartZ=0 EndX=-207.775 EndY=-50.4316 EndZ=0
    g2: LineSegment StartX=-207.775 StartY=-50.4316 StartZ=0 EndX=-207.775 EndY=-80.4316 EndZ=0
    g3: LineSegment StartX=-207.775 StartY=-80.4316 StartZ=0 EndX=-209.575 EndY=-80.4316 EndZ=0
  constraints (11):
    c: Vertical(g0)
    c: Coincident(g1,g0)
    c: Horizontal(g1)
    c: Coincident(g2,g1)
    c: Vertical(g2)
    c: Coincident(g3,g2)
    c: Coincident(g3,g0)
    c: Horizontal(g3)
    c: DistanceX(g1,g1) = 1.8
    c: Coincident(g2,g-3)
    c: DistanceY(g2,g2) = 30
FEATURE [Part::Extrusion] Extrude040  label="Extrude040 scavo alimentatore"
  Base = -> Sketch037
  Dir = (0,-1,2e-16)
  DirMode = 2
  FaceMakerClass = Part::FaceMakerBullseye
  FaceMakerMode = 3
  LengthFwd = 19.5
  LengthRev = 0
  Solid = true
  Symmetric = true
FEATURE [Part::Extrusion] Extrude031  label="Extrude fermo per scheda micro"
  Base = -> Sketch033
  Dir = (0,-1,2e-16)
  DirMode = 2
  FaceMakerClass = Part::FaceMakerBullseye
  FaceMakerMode = 3
  LengthFwd = 3
  LengthRev = 0
  Placement = pos=(0,8.6,0) rot=(0,0,1;0rad)
  Solid = true
  Symmetric = false
FEATURE [Sketcher::SketchObject] Sketch038  label="scavo driver solenoide"
  ArcFitTolerance = 1e-06
  AttachmentSupport = -> [XZ_Plane]
  ExternalGeometry = -> [Sketch,Sketch036]
  FullyConstrained = true
  MakeInternals = false
  MapMode = 5
  Placement = pos=(0,0,0) rot=(1,0,0;1.5708rad)
  sketch-geometry (7):
    g0: LineSegment StartX=-192.222 StartY=-8.0175 StartZ=0 EndX=-194.941 EndY=-6.74965 EndZ=0
    g1: LineSegment StartX=-194.941 StartY=-6.74965 StartZ=0 EndX=-212.269 EndY=-43.9083 EndZ=0
    g2: LineSegment StartX=-192.222 StartY=-8.0175 StartZ=0 EndX=-188.779 EndY=-9.62345 EndZ=0
    g3: LineSegment StartX=-188.779 StartY=-9.62345 StartZ=0 EndX=-205.357 EndY=-45.1761 EndZ=0
    g4: LineSegment StartX=-205.357 StartY=-45.1761 StartZ=0 EndX=-209.55 EndY=-45.1761 EndZ=0
    g5: LineSegment [constr] StartX=-212.269 StartY=-43.9083 StartZ=0 EndX=-209.55 EndY=-45.1761 EndZ=0
    g6: LineSegment StartX=-212.269 StartY=-43.9083 StartZ=0 EndX=-209.55 EndY=-45.1761 EndZ=0
  constraints (20):
    c: Coincident(g1,g0)
    c: Coincident(g3,g2)
    c: Coincident(g4,g3)
    c: Distance(g2) = 3.8
    c: Distance(g1) = 41
    c: Coincident(g5,g1)
    c: Distance(g5) = 3
    c: Perpendicular(g5,g-3)
    c: Parallel(g1,g-3)
    c: Perpendicular(g1,g0)
    c: Distance(g0) = 3
    c: Coincident(g6,g1)
    c: Parallel(g3,g-3)
    c: Perpendicular(g2,g3)
    c: Coincident(g2,g0)
    c: Perpendicular(g-4,g4)
    c: PointOnObject(g5,g-3)
    c: Distance(g-3,g5) = 9.6
    c: Coincident(g4,g5)
    c: Coincident(g6,g4)
FEATURE [Part::Extrusion] Extrude041  label="Extrude scavo driver solenoide"
  Base = -> Sketch038
  Dir = (0,-1,2e-16)
  DirMode = 2
  FaceMakerClass = Part::FaceMakerBullseye
  FaceMakerMode = 3
  LengthFwd = 20.6
  LengthRev = 0
  Solid = true
  Symmetric = true
FEATURE [Sketcher::SketchObject] Sketch039  label="scavo per cavo usb per micro"
  ArcFitTolerance = 1e-06
  AttachmentSupport = -> [XZ_Plane]
  ExternalGeometry = -> [Sketch,Sketch016]
  FullyConstrained = true
  MakeInternals = false
  MapMode = 5
  Placement = pos=(0,0,0) rot=(1,0,0;1.5708rad)
  sketch-geometry (4):
    g0: LineSegment StartX=-82.51 StartY=36.4 StartZ=0 EndX=-74.51 EndY=36.4 EndZ=0
    g1: LineSegment StartX=-74.51 StartY=36.4 StartZ=0 EndX=-74.51 EndY=30.8 EndZ=0
    g2: LineSegment StartX=-74.51 StartY=30.8 StartZ=0 EndX=-82.51 EndY=30.8 EndZ=0
    g3: LineSegment StartX=-82.51 StartY=30.8 StartZ=0 EndX=-82.51 EndY=36.4 EndZ=0
  constraints (11):
    c: Coincident(g1,g0)
    c: Vertical(g1)
    c: Coincident(g2,g1)
    c: Horizontal(g2)
    c: Coincident(g3,g2)
    c: Coincident(g3,g0)
    c: Vertical(g3)
    c: Tangent(g0,g-3)
    c: Tangent(g2,g-4)
    c: Tangent(g3,g-4)
    c: Tangent(g1,g-4)
FEATURE [Part::Extrusion] Extrude042  label="Extrude scavo per cavo usb per micro"
  Base = -> Sketch039
  Dir = (0,-1,2e-16)
  DirMode = 2
  FaceMakerClass = Part::FaceMakerBullseye
  FaceMakerMode = 3
  LengthFwd = 11.2
  LengthRev = 0
  Solid = true
  Symmetric = true
FEATURE [Sketcher::SketchObject] Sketch040  label="scavo saldature alimentatore connettore 5v"
  ArcFitTolerance = 1e-06
  AttachmentSupport = -> [XZ_Plane]
  ExternalGeometry = -> [Sketch037]
  FullyConstrained = true
  MakeInternals = false
  MapMode = 5
  Placement = pos=(0,0,0) rot=(1,0,0;1.5708rad)
  sketch-geometry (4):
    g0: LineSegment StartX=-211.175 StartY=-52.4316 StartZ=0 EndX=-211.175 EndY=-56.4316 EndZ=0
    g1: LineSegment StartX=-211.175 StartY=-52.4316 StartZ=0 EndX=-209.575 EndY=-52.4316 EndZ=0
    g2: LineSegment StartX=-209.575 StartY=-52.4316 StartZ=0 EndX=-209.575 EndY=-56.4316 EndZ=0
    g3: LineSegment StartX=-209.575 StartY=-56.4316 StartZ=0 EndX=-211.175 EndY=-56.4316 EndZ=0
  constraints (11):
    c: Vertical(g0)
    c: Coincident(g1,g0)
    c: Horizontal(g1)
    c: Coincident(g2,g1)
    c: Coincident(g3,g2)
    c: Coincident(g3,g0)
    c: Horizontal(g3)
    c: DistanceX(g1,g1) = 1.6
    c: DistanceY(g2,g2) = 4
    c: Tangent(g2,g-3)
    c: DistanceY(g1,g-3) = 2
FEATURE [Part::Extrusion] Extrude043  label="Extrude scavo saldature alimentatore connettore 5v"
  Base = -> Sketch040
  Dir = (0,-1,2e-16)
  DirMode = 2
  FaceMakerClass = Part::FaceMakerBullseye
  FaceMakerMode = 3
  LengthFwd = 8
  LengthRev = 0
  Solid = true
  Symmetric = true
FEATURE [Sketcher::SketchObject] Sketch041  label="scavo saldature alimentatore connettore 5v verticali"
  ArcFitTolerance = 1e-06
  AttachmentSupport = -> [XZ_Plane]
  ExternalGeometry = -> [Sketch037]
  FullyConstrained = true
  MakeInternals = false
  MapMode = 5
  Placement = pos=(0,0,0) rot=(1,0,0;1.5708rad)
  sketch-geometry (4):
    g0: LineSegment StartX=-211.175 StartY=-53.6316 StartZ=0 EndX=-209.575 EndY=-53.6316 EndZ=0
    g1: LineSegment StartX=-209.575 StartY=-53.6316 StartZ=0 EndX=-209.575 EndY=-76.6316 EndZ=0
    g2: LineSegment StartX=-209.575 StartY=-76.6316 StartZ=0 EndX=-211.175 EndY=-76.6316 EndZ=0
    g3: LineSegment StartX=-211.175 StartY=-76.6316 StartZ=0 EndX=-211.175 EndY=-53.6316 EndZ=0
  constraints (11):
    c: Horizontal(g0)
    c: Coincident(g1,g0)
    c: Coincident(g2,g1)
    c: Horizontal(g2)
    c: Coincident(g3,g2)
    c: Coincident(g3,g0)
    c: Vertical(g3)
    c: DistanceY(g3,g3) = 23
    c: DistanceX(g0,g0) = 1.6
    c: Tangent(g1,g-3)
    c: DistanceY(g0,g-3) = 3.2
FEATURE [Part::Extrusion] Extrude044  label="Extrude scavo saldature alimentatore connettore 5v verticali"
  Base = -> Sketch041
  Dir = (0,-1,2e-16)
  DirMode = 2
  FaceMakerClass = Part::FaceMakerBullseye
  FaceMakerMode = 3
  LengthFwd = 3.2
  LengthRev = 0
  Placement = pos=(0,8.3,0) rot=(0,0,1;0rad)
  Solid = true
  Symmetric = false
FEATURE [Sketcher::SketchObject] Sketch042  label="fermi per driver solenoide e alimentatore"
  ArcFitTolerance = 1e-06
  AttachmentSupport = -> [XZ_Plane]
  ExternalGeometry = -> [Sketch036,Sketch037,Sketch,Sketch038]
  FullyConstrained = true
  MakeInternals = false
  MapMode = 5
  Placement = pos=(0,0,0) rot=(1,0,0;1.5708rad)
  sketch-geometry (27):
    g0: LineSegment StartX=-200.506 StartY=-25.7811 StartZ=0 EndX=-201.436 EndY=-27.775 EndZ=0
    g1: LineSegment StartX=-201.436 StartY=-27.775 StartZ=0 EndX=-199.442 EndY=-28.7048 EndZ=0
    g2: LineSegment StartX=-199.442 StartY=-28.7048 StartZ=0 EndX=-198.512 EndY=-26.7109 EndZ=0
    g3: LineSegment StartX=-198.512 StartY=-26.7109 StartZ=0 EndX=-200.506 EndY=-25.7811 EndZ=0
    g4: LineSegment StartX=-201.28 StartY=-23.6549 StartZ=0 EndX=-203.562 EndY=-28.5489 EndZ=0
    g5: LineSegment StartX=-203.562 StartY=-28.5489 StartZ=0 EndX=-200.118 EndY=-30.1549 EndZ=0
    g6: LineSegment StartX=-197.992 StartY=-29.381 StartZ=0 EndX=-197.062 EndY=-27.3871 EndZ=0
    g7: LineSegment StartX=-197.836 StartY=-25.2608 StartZ=0 EndX=-201.28 EndY=-23.6549 EndZ=0
    g8: LineSegment [constr] StartX=-198.668 StartY=-30.8311 StartZ=0 EndX=-197.992 EndY=-29.381 EndZ=0
    g9: LineSegment [constr] StartX=-198.668 StartY=-30.8311 StartZ=0 EndX=-200.118 EndY=-30.1549 EndZ=0
    g10: ArcOfCircle CenterX=-198.512 CenterY=-26.7109 CenterZ=0 NormalX=0 NormalY=0 NormalZ=1 AngleXU=0 Radius=1.6 StartAngle=5.84685 EndAngle=7.41765
    g11: GeomPoint [constr] X=-196.386 Y=-25.937 Z=0
    g12: ArcOfCircle CenterX=-199.442 CenterY=-28.7048 CenterZ=0 NormalX=0 NormalY=0 NormalZ=1 AngleXU=0 Radius=1.6 StartAngle=4.27606 EndAngle=5.84685
    g13: GeomPoint [constr] X=-198.668 Y=-30.8311 Z=0
    g14: LineSegment StartX=-207.775 StartY=-46.8316 StartZ=0 EndX=-207.775 EndY=-50.8316 EndZ=0
    g15: LineSegment StartX=-207.775 StartY=-46.8316 StartZ=0 EndX=-203.775 EndY=-46.8316 EndZ=0
    g16: LineSegment StartX=-203.775 StartY=-46.8316 StartZ=0 EndX=-203.775 EndY=-50.8316 EndZ=0
    g17: LineSegment StartX=-207.775 StartY=-50.8316 StartZ=0 EndX=-203.775 EndY=-50.8316 EndZ=0
    g18: LineSegment StartX=-209.375 StartY=-52.4316 StartZ=0 EndX=-203.775 EndY=-52.4316 EndZ=0
    g19: LineSegment StartX=-202.175 StartY=-50.8316 StartZ=0 EndX=-202.175 EndY=-46.8316 EndZ=0
    g20: LineSegment StartX=-203.775 StartY=-45.2316 StartZ=0 EndX=-209.375 EndY=-45.2316 EndZ=0
    g21: LineSegment StartX=-209.375 StartY=-45.2316 StartZ=0 EndX=-209.375 EndY=-52.4316 EndZ=0
    g22: ArcOfCircle CenterX=-203.775 CenterY=-46.8316 CenterZ=0 NormalX=0 NormalY=0 NormalZ=1 AngleXU=0 Radius=1.6 StartAngle=1.8e-15 EndAngle=1.5708
    g23: GeomPoint [constr] X=-202.175 Y=-45.2316 Z=0
    g24: ArcOfCircle CenterX=-203.775 CenterY=-50.8316 CenterZ=0 NormalX=0 NormalY=0 NormalZ=1 AngleXU=0 Radius=1.6 StartAngle=4.71239 EndAngle=6.28319
    g25: GeomPoint [constr] X=-202.175 Y=-52.4316 Z=0
    g26: LineSegment [constr] StartX=-207.775 StartY=-50.4316 StartZ=0 EndX=-207.775 EndY=-50.8316 EndZ=0
  constraints (69):
    c: Coincident(g1,g0)
    c: Coincident(g2,g1)
    c: Coincident(g3,g2)
    c: Coincident(g3,g0)
    c: Parallel(g0,g2)
    c: Perpendicular(g3,g0)
    c: Perpendicular(g1,g0)
    c: Coincident(g5,g4)
    c: Coincident(g7,g4)
    c: Distance(g3) = 2.2
    c: Distance(g2) = 2.2
    c: Parallel(g6,g2)
    c: Parallel(g6,g4)
    c: Perpendicular(g5,g6)
    c: Perpendicular(g7,g6)
    c: Distance(g13,g11) = 5.4
    c: Distance(g5,g13) = 5.4
    c: Coincident(g9,g8)
    c: Distance(g8) = 1.6
    c: Distance(g9) = 1.6
    c: Perpendicular(g9,g8)
    c: Parallel(g8,g6)
    c: Coincident(g8,g13)
    c: Distance(g8,g1) = 1.6
    c: Distance(g9,g1) = 1.6
    c: Tangent(g0,g-5)
    c: Distance(g0,g-6) = 19.2
    c: PointOnObject(g11,g7)
    c: PointOnObject(g11,g6)
    c: Tangent(g7,g10) = -1.5708
    c: Tangent(g6,g10) = -1.5708
    c: PointOnObject(g13,g5)
    c: Tangent(g5,g12) = -1.5708
    c: Tangent(g6,g12) = -1.5708
    c: Equal(g10,g12)
    c: Coincident(g10,g2)
    c: Vertical(g14)
    c: Coincident(g15,g14)
    c: Horizontal(g15)
    c: Coincident(g16,g15)
    c: Vertical(g16)
    c: Coincident(g17,g14)
    c: Coincident(g17,g16)
    c: Horizontal(g17)
    c: Distance(g16) = 4
    c: Distance(g15) = 4
    c: Horizontal(g18)
    c: Vertical(g19)
    c: Horizontal(g20)
    c: Coincident(g21,g20)
    c: Coincident(g21,g18)
    c: Vertical(g21)
    c: Distance(g20,g23) = 7.2
    c: Distance(g25,g23) = 7.2
    c: DistanceY(g18,g14) = 1.6
    c: DistanceX(g18,g14) = 1.6
    c: PointOnObject(g23,g20)
    c: PointOnObject(g23,g19)
    c: Tangent(g20,g22) = -1.5708
    c: Tangent(g19,g22) = -1.5708
    c: PointOnObject(g25,g19)
    c: Tangent(g18,g24) = -1.5708
    c: Tangent(g19,g24) = -1.5708
    c: Equal(g22,g24)
    c: Coincident(g22,g15)
    c: Vertical(g26)
    c: Distance(g26) = 0.4
    c: Coincident(g26,g-4)
    c: Coincident(g14,g26)
FEATURE [Part::Extrusion] Extrude045  label="Extrude fermi per driver solenoide e alimentatore"
  Base = -> Sketch042
  Dir = (0,-1,2e-16)
  DirMode = 2
  FaceMakerClass = Part::FaceMakerBullseye
  FaceMakerMode = 3
  LengthFwd = 25.2
  LengthRev = 0
  Solid = true
  Symmetric = true
FEATURE [Sketcher::SketchObject] Sketch043  label="scavo pulizia fermo alimentatore"
  ArcFitTolerance = 1e-06
  AttachmentSupport = -> [XZ_Plane]
  ExternalGeometry = -> [Sketch042,Sketch036,Sketch037]
  FullyConstrained = true
  MakeInternals = false
  MapMode = 5
  Placement = pos=(0,0,0) rot=(1,0,0;1.5708rad)
  sketch-geometry (6):
    g0: LineSegment StartX=-209.375 StartY=-52.4316 StartZ=0 EndX=-209.375 EndY=-50.4316 EndZ=0
    g1: LineSegment StartX=-209.375 StartY=-50.4316 StartZ=0 EndX=-207.775 EndY=-50.4316 EndZ=0
    g2: LineSegment StartX=-207.775 StartY=-50.4316 StartZ=0 EndX=-207.775 EndY=-45.2316 EndZ=0
    g3: LineSegment StartX=-207.775 StartY=-45.2316 StartZ=0 EndX=-202.175 EndY=-45.2316 EndZ=0
    g4: LineSegment StartX=-202.175 StartY=-45.2316 StartZ=0 EndX=-202.175 EndY=-52.4316 EndZ=0
    g5: LineSegment StartX=-202.175 StartY=-52.4316 StartZ=0 EndX=-209.375 EndY=-52.4316 EndZ=0
  constraints (13):
    c: Vertical(g0)
    c: Coincident(g1,g0)
    c: Coincident(g2,g1)
    c: Coincident(g3,g2)
    c: Coincident(g4,g3)
    c: Coincident(g5,g4)
    c: Coincident(g5,g0)
    c: Horizontal(g5)
    c: Coincident(g0,g-6)
    c: Tangent(g1,g-8)
    c: Tangent(g2,g-4)
    c: Tangent(g3,g-7)
    c: Tangent(g4,g-3)
FEATURE [Part::Extrusion] Extrude046  label="Extrude scavo pulizia fermo alimentatore"
  Base = -> Sketch043
  Dir = (0,-1,2e-16)
  DirMode = 2
  FaceMakerClass = Part::FaceMakerBullseye
  FaceMakerMode = 3
  LengthFwd = 19.5
  LengthRev = 0
  Solid = true
  Symmetric = true
FEATURE [Sketcher::SketchObject] Sketch044  label="buchini per fissaggio oled"
  ArcFitTolerance = 1e-06
  AttachmentSupport = -> [YZ_Plane]
  ExternalGeometry = -> [Sketch]
  FullyConstrained = true
  MakeInternals = false
  MapMode = 5
  Placement = pos=(0,0,0) rot=(0.57735,0.57735,0.57735;2.0944rad)
  sketch-geometry (5):
    g0: LineSegment [constr] StartX=1.5e-14 StartY=67.3588 StartZ=0 EndX=0 EndY=64.3588 EndZ=0
    g1: LineSegment [constr] StartX=0 StartY=64.3588 StartZ=0 EndX=10.4 EndY=64.3588 EndZ=0
    g2: LineSegment [constr] StartX=0 StartY=64.3588 StartZ=0 EndX=-10.4 EndY=64.3588 EndZ=0
    g3: Circle CenterX=10.4 CenterY=64.3588 CenterZ=0 NormalX=0 NormalY=0 NormalZ=1 AngleXU=0 Radius=1.5
    g4: Circle CenterX=-10.4 CenterY=64.3588 CenterZ=0 NormalX=0 NormalY=0 NormalZ=1 AngleXU=0 Radius=1.5
  constraints (13):
    c: Distance(g0) = 3
    c: PointOnObject(g0,g-2)
    c: Coincident(g1,g0)
    c: Horizontal(g1)
    c: Coincident(g2,g0)
    c: Horizontal(g2)
    c: DistanceX(g1,g1) = 10.4
    c: Coincident(g3,g1)
    c: Diameter(g4) = 3
    c: Coincident(g4,g2)
    c: Coincident(g0,g-7)
    c: Equal(g1,g2)
    c: Equal(g4,g3)
FEATURE [Part::Extrusion] Extrude047  label="Extrude buchini per fissaggio oled"
  Base = -> Sketch044
  Dir = (1,0,0)
  DirMode = 2
  FaceMakerClass = Part::FaceMakerBullseye
  FaceMakerMode = 3
  LengthFwd = 10
  LengthRev = 0
  Placement = pos=(-186,0,0) rot=(0,0,1;0rad)
  Solid = true
  Symmetric = false
FEATURE [Sketcher::SketchObject] Sketch046  label="scavo 5x5 neopixel"
  ArcFitTolerance = 1e-06
  AttachmentSupport = -> [YZ_Plane002]
  FullyConstrained = true
  MakeInternals = false
  MapMode = 5
  Placement = pos=(0,0,0) rot=(0.57735,0.57735,0.57735;2.0944rad)
  sketch-geometry (4):
    g0: LineSegment StartX=-2.7 StartY=2.7 StartZ=0 EndX=2.7 EndY=2.7 EndZ=0
    g1: LineSegment StartX=2.7 StartY=2.7 StartZ=0 EndX=2.7 EndY=-2.7 EndZ=0
    g2: LineSegment StartX=2.7 StartY=-2.7 StartZ=0 EndX=-2.7 EndY=-2.7 EndZ=0
    g3: LineSegment StartX=-2.7 StartY=-2.7 StartZ=0 EndX=-2.7 EndY=2.7 EndZ=0
  constraints (11):
    c: Horizontal(g0)
    c: Coincident(g1,g0)
    c: Vertical(g1)
    c: Coincident(g2,g1)
    c: Horizontal(g2)
    c: Coincident(g3,g2)
    c: Coincident(g3,g0)
    c: Vertical(g3)
    c: DistanceX(g0,g0) = 5.4
    c: DistanceY(g1,g1) = 5.4
    c: Symmetric(g0,g1,g-1)
FEATURE [Sketcher::SketchObject] Sketch047  label="scavo 10x10 neopixel corpo"
  ArcFitTolerance = 1e-06
  AttachmentOffset = pos=(0,0,1) rot=(0,0,1;0rad)
  AttachmentSupport = -> [YZ_Plane002]
  FullyConstrained = true
  MakeInternals = false
  MapMode = 5
  Placement = pos=(1,0,0) rot=(0.57735,0.57735,0.57735;2.0944rad)
  sketch-geometry (4):
    g0: LineSegment StartX=-5 StartY=5.1 StartZ=0 EndX=5 EndY=5.1 EndZ=0
    g1: LineSegment StartX=5 StartY=5.1 StartZ=0 EndX=5 EndY=-5.1 EndZ=0
    g2: LineSegment StartX=5 StartY=-5.1 StartZ=0 EndX=-5 EndY=-5.1 EndZ=0
    g3: LineSegment StartX=-5 StartY=-5.1 StartZ=0 EndX=-5 EndY=5.1 EndZ=0
  constraints (11):
    c: Horizontal(g0)
    c: Coincident(g1,g0)
    c: Vertical(g1)
    c: Coincident(g2,g1)
    c: Horizontal(g2)
    c: Coincident(g3,g2)
    c: Coincident(g3,g0)
    c: Vertical(g3)
    c: DistanceX(g0,g0) = 10
    c: DistanceY(g1,g1) = 10.2
    c: Symmetric(g0,g2,g-1)
FEATURE [Sketcher::SketchObject] Sketch048  label="buco per perno blocco neopixel"
  ArcFitTolerance = 1e-06
  AttachmentSupport = -> [XZ_Plane002]
  FullyConstrained = true
  MakeInternals = false
  MapMode = 5
  Placement = pos=(0,0,0) rot=(1,0,0;1.5708rad)
  sketch-geometry (4):
    g0: LineSegment StartX=3 StartY=1.2 StartZ=0 EndX=3 EndY=-1.2 EndZ=0
    g1: LineSegment StartX=3 StartY=-1.2 StartZ=0 EndX=5.4 EndY=-1.2 EndZ=0
    g2: LineSegment StartX=5.4 StartY=-1.2 StartZ=0 EndX=5.4 EndY=1.2 EndZ=0
    g3: LineSegment StartX=5.4 StartY=1.2 StartZ=0 EndX=3 EndY=1.2 EndZ=0
  constraints (11):
    c: Coincident(g1,g0)
    c: Horizontal(g1)
    c: Coincident(g2,g1)
    c: Vertical(g2)
    c: Coincident(g3,g2)
    c: Coincident(g3,g0)
    c: Horizontal(g3)
    c: DistanceX(g1,g1) = 2.4
    c: DistanceY(g2,g2) = 2.4
    c: Symmetric(g0,g0,g-1)
    c: DistanceX(g-1,g0) = 3
FEATURE [Sketcher::SketchObject] Sketch045  label="blocco principale per neopixel"
  ArcFitTolerance = 1e-06
  AttachmentSupport = -> [XZ_Plane002]
  ExternalGeometry = -> [Sketch048]
  FullyConstrained = true
  MakeInternals = false
  MapMode = 5
  Placement = pos=(0,0,0) rot=(1,0,0;1.5708rad)
  sketch-geometry (6):
    g0: LineSegment StartX=0 StartY=5.1 StartZ=0 EndX=0 EndY=-5.1 EndZ=0
    g1: LineSegment StartX=0 StartY=-5.1 StartZ=0 EndX=3 EndY=-5.1 EndZ=0
    g2: LineSegment StartX=7 StartY=-1.1 StartZ=0 EndX=7 EndY=5.1 EndZ=0
    g3: LineSegment StartX=7 StartY=5.1 StartZ=0 EndX=0 EndY=5.1 EndZ=0
    g4: ArcOfCircle CenterX=3 CenterY=-1.1 CenterZ=0 NormalX=0 NormalY=0 NormalZ=1 AngleXU=0 Radius=4 StartAngle=4.71239 EndAngle=6.28319
    g5: GeomPoint [constr] X=7 Y=-5.1 Z=0
  constraints (15):
    c: Vertical(g0)
    c: Coincident(g1,g0)
    c: Horizontal(g1)
    c: Vertical(g2)
    c: Coincident(g3,g2)
    c: Coincident(g3,g0)
    c: Horizontal(g3)
    c: DistanceY(g0,g0) = 10.2
    c: Symmetric(g0,g0,g-1)
    c: DistanceX(g3,g3) = 7
    c: PointOnObject(g5,g2)
    c: PointOnObject(g5,g1)
    c: Tangent(g2,g4) = -1.5708
    c: Tangent(g1,g4) = -1.5708
    c: DistanceX(g-3,g1) = 0
FEATURE [Sketcher::SketchObject] Sketch049  label="rinforzi esterni per corpo neopoixel"
  ArcFitTolerance = 1e-06
  AttachmentSupport = -> [XZ_Plane002]
  ExternalGeometry = -> [Sketch045]
  FullyConstrained = true
  MakeInternals = false
  MapMode = 5
  Placement = pos=(0,0,0) rot=(1,0,0;1.5708rad)
  sketch-geometry (8):
    g0: LineSegment StartX=1 StartY=-4.1 StartZ=0 EndX=2 EndY=-4.1 EndZ=0
    g1: LineSegment StartX=2 StartY=-4.1 StartZ=0 EndX=2 EndY=-5.1 EndZ=0
    g2: LineSegment StartX=2 StartY=-5.1 StartZ=0 EndX=1 EndY=-5.1 EndZ=0
    g3: LineSegment StartX=1 StartY=-5.1 StartZ=0 EndX=1 EndY=-4.1 EndZ=0
    g4: LineSegment StartX=1 StartY=5.1 StartZ=0 EndX=2 EndY=5.1 EndZ=0
    g5: LineSegment StartX=2 StartY=5.1 StartZ=0 EndX=2 EndY=4.1 EndZ=0
    g6: LineSegment StartX=2 StartY=4.1 StartZ=0 EndX=1 EndY=4.1 EndZ=0
    g7: LineSegment StartX=1 StartY=4.1 StartZ=0 EndX=1 EndY=5.1 EndZ=0
  constraints (24):
    c: Horizontal(g0)
    c: Coincident(g1,g0)
    c: Vertical(g1)
    c: Coincident(g2,g1)
    c: Horizontal(g2)
    c: Coincident(g3,g2)
    c: Coincident(g3,g0)
    c: Vertical(g3)
    c: Horizontal(g4)
    c: Coincident(g5,g4)
    c: Vertical(g5)
    c: Coincident(g6,g5)
    c: Horizontal(g6)
    c: Coincident(g7,g6)
    c: Coincident(g7,g4)
    c: Vertical(g7)
    c: DistanceX(g4,g4) = 1
    c: DistanceY(g5,g5) = 1
    c: DistanceX(g0,g0) = 1
    c: DistanceY(g1,g1) = 1
    c: DistanceX(g-3,g4) = 1
    c: DistanceY(g-3,g4) = 0
    c: DistanceX(g-4,g2) = 1
    c: DistanceY(g2,g-4) = 0
FEATURE [Sketcher::SketchObject] Sketch052  label="scavo saldature driver solenoide"
  ArcFitTolerance = 1e-06
  AttachmentSupport = -> [XZ_Plane]
  ExternalGeometry = -> [Sketch038]
  FullyConstrained = true
  MakeInternals = false
  MapMode = 5
  Placement = pos=(0,0,0) rot=(1,0,0;1.5708rad)
  sketch-geometry (4):
    g0: LineSegment StartX=-195.304 StartY=-6.5806 StartZ=0 EndX=-196.994 EndY=-10.2058 EndZ=0
    g1: LineSegment StartX=-196.994 StartY=-10.2058 StartZ=0 EndX=-196.632 EndY=-10.3749 EndZ=0
    g2: LineSegment StartX=-196.632 StartY=-10.3749 StartZ=0 EndX=-194.941 EndY=-6.74965 EndZ=0
    g3: LineSegment StartX=-194.941 StartY=-6.74965 StartZ=0 EndX=-195.304 EndY=-6.5806 EndZ=0
  constraints (11):
    c: Coincident(g1,g0)
    c: Coincident(g2,g1)
    c: Coincident(g3,g2)
    c: Coincident(g3,g0)
    c: Parallel(g2,g0)
    c: Perpendicular(g2,g3)
    c: Perpendicular(g1,g2,g1) = 1.5708
    c: Parallel(g2,g-3)
    c: Distance(g2) = 4
    c: Distance(g3) = 0.4
    c: Coincident(g2,g-3)
FEATURE [Part::Extrusion] Extrude055  label="Extrude scavo saldature driver solenoide"
  Base = -> Sketch052
  Dir = (0,-1,2e-16)
  DirMode = 2
  FaceMakerClass = Part::FaceMakerBullseye
  FaceMakerMode = 3
  LengthFwd = 6
  LengthRev = 0
  Solid = true
  Symmetric = true
FEATURE [Sketcher::SketchObject] Sketch053  label="scavo saldature rumble"
  ArcFitTolerance = 1e-06
  AttachmentSupport = -> [XZ_Plane]
  ExternalGeometry = -> [Sketch019]
  FullyConstrained = true
  MakeInternals = false
  MapMode = 5
  Placement = pos=(0,0,0) rot=(1,0,0;1.5708rad)
  sketch-geometry (4):
    g0: LineSegment StartX=-169.451 StartY=-56.8615 StartZ=0 EndX=-170.687 EndY=-60.6657 EndZ=0
    g1: LineSegment StartX=-170.687 StartY=-60.6657 StartZ=0 EndX=-169.546 EndY=-61.0365 EndZ=0
    g2: LineSegment StartX=-169.546 StartY=-61.0365 StartZ=0 EndX=-168.31 EndY=-57.2323 EndZ=0
    g3: LineSegment StartX=-168.31 StartY=-57.2323 StartZ=0 EndX=-169.451 EndY=-56.8615 EndZ=0
  constraints (11):
    c: Coincident(g1,g0)
    c: Coincident(g2,g1)
    c: Coincident(g3,g2)
    c: Coincident(g3,g0)
    c: Parallel(g0,g2)
    c: Perpendicular(g3,g0)
    c: Perpendicular(g1,g0)
    c: Parallel(g0,g-3)
    c: Distance(g0) = 4
    c: Coincident(g0,g-3)
    c: Distance(g1) = 1.2
FEATURE [Part::Extrusion] Extrude056  label="Extrude scavo saldature rumble"
  Base = -> Sketch053
  Dir = (0,-1,2e-16)
  DirMode = 2
  FaceMakerClass = Part::FaceMakerBullseye
  FaceMakerMode = 3
  LengthFwd = 8.4
  LengthRev = 0
  Solid = true
  Symmetric = true
FEATURE [Sketcher::SketchObject] Sketch054  label="scavo saldature alimentatore connettore USB"
  ArcFitTolerance = 1e-06
  AttachmentSupport = -> [XZ_Plane]
  ExternalGeometry = -> [Sketch037]
  FullyConstrained = true
  MakeInternals = false
  MapMode = 5
  Placement = pos=(0,0,0) rot=(1,0,0;1.5708rad)
  sketch-geometry (4):
    g0: LineSegment StartX=-209.575 StartY=-80.4316 StartZ=0 EndX=-210.375 EndY=-80.4316 EndZ=0
    g1: LineSegment StartX=-210.375 StartY=-80.4316 StartZ=0 EndX=-210.375 EndY=-72.4316 EndZ=0
    g2: LineSegment StartX=-210.375 StartY=-72.4316 StartZ=0 EndX=-209.575 EndY=-72.4316 EndZ=0
    g3: LineSegment StartX=-209.575 StartY=-72.4316 StartZ=0 EndX=-209.575 EndY=-80.4316 EndZ=0
  constraints (11):
    c: Horizontal(g0)
    c: Coincident(g1,g0)
    c: Vertical(g1)
    c: Coincident(g2,g1)
    c: Horizontal(g2)
    c: Coincident(g3,g2)
    c: Coincident(g3,g0)
    c: Vertical(g3)
    c: DistanceX(g0,g0) = 0.8
    c: DistanceY(g3,g3) = 8
    c: Coincident(g0,g-4)
FEATURE [Part::Extrusion] Extrude057  label="Extrude scavo saldature alimentatore connettore USB"
  Base = -> Sketch054
  Dir = (0,-1,2e-16)
  DirMode = 2
  FaceMakerClass = Part::FaceMakerBullseye
  FaceMakerMode = 3
  LengthFwd = 11
  LengthRev = 0
  Solid = true
  Symmetric = true
FEATURE [Sketcher::SketchObject] Sketch055  label="buco interno per micro switch"
  ArcFitTolerance = 1e-06
  AttachmentSupport = -> [XZ_Plane]
  ExternalGeometry = -> [Sketch]
  FullyConstrained = true
  MakeInternals = false
  MapMode = 5
  Placement = pos=(0,0,0) rot=(1,0,0;1.5708rad)
  sketch-geometry (11):
    g0: LineSegment [constr] StartX=-194.483 StartY=34.2854 StartZ=0 EndX=-196.022 EndY=30.0568 EndZ=0
    g1: LineSegment [constr] StartX=-196.022 StartY=30.0568 StartZ=0 EndX=-197.561 EndY=25.8282 EndZ=0
    g2: LineSegment [constr] StartX=-196.022 StartY=30.0568 StartZ=0 EndX=-194.143 EndY=29.3727 EndZ=0
    g3: LineSegment [constr] StartX=-196.022 StartY=30.0568 StartZ=0 EndX=-197.902 EndY=30.7408 EndZ=0
    g4: LineSegment StartX=-196.362 StartY=34.9694 StartZ=0 EndX=-192.604 EndY=33.6014 EndZ=0
    g5: LineSegment StartX=-199.441 StartY=26.5122 StartZ=0 EndX=-195.682 EndY=25.1441 EndZ=0
    g6: LineSegment StartX=-192.604 StartY=33.6014 StartZ=0 EndX=-195.682 EndY=25.1441 EndZ=0
    g7: LineSegment StartX=-196.362 StartY=34.9694 StartZ=0 EndX=-199.441 EndY=26.5122 EndZ=0
    g8: GeomPoint [constr] X=-187.821 Y=29.2 Z=0
    g9: LineSegment [constr] StartX=-188.505 StartY=27.3206 StartZ=0 EndX=-196.022 EndY=30.0568 EndZ=0
    g10: LineSegment [constr] StartX=-187.821 StartY=29.2 StartZ=0 EndX=-188.505 EndY=27.3206 EndZ=0
  constraints (27):
    c: Coincident(g2,g0)
    c: Parallel(g0,g-3)
    c: Tangent(g1,g0) = -1.5708
    c: Perpendicular(g0,g2)
    c: Tangent(g2,g3)
    c: Distance(g0,g1) = 9
    c: Equal(g0,g1)
    c: Distance(g3,g2) = 4
    c: Equal(g2,g3)
    c: Parallel(g3,g4)
    c: Symmetric(g4,g4,g0)
    c: Parallel(g6,g1)
    c: Parallel(g7,g1)
    c: Symmetric(g6,g6,g2)
    c: Symmetric(g5,g5,g1)
    c: Symmetric(g7,g7,g3)
    c: Coincident(g7,g4)
    c: Coincident(g6,g4)
    c: Coincident(g5,g6)
    c: Symmetric(g-3,g-3,g8)
    c: Perpendicular(g-3,g9)
    c: Distance(g9) = 8
    c: Coincident(g3,g9)
    c: Coincident(g10,g8)
    c: Parallel(g10,g-3)
    c: Distance(g10) = 2
    c: Coincident(g10,g9)
FEATURE [Sketcher::SketchObject] Sketch056  label="buco esterno per micro switch"
  ArcFitTolerance = 1e-06
  AttachmentSupport = -> [XZ_Plane]
  ExternalGeometry = -> [Sketch055]
  FullyConstrained = true
  MakeInternals = false
  MapMode = 5
  Placement = pos=(0,0,0) rot=(1,0,0;1.5708rad)
  sketch-geometry (17):
    g0: GeomPoint [constr] X=-194.143 Y=29.3727 Z=0
    g1: GeomPoint [constr] X=-194.483 Y=34.2854 Z=0
    g2: GeomPoint [constr] X=-197.902 Y=30.7408 Z=0
    g3: GeomPoint [constr] X=-197.561 Y=25.8282 Z=0
    g4: GeomPoint [constr] X=-196.022 Y=30.0568 Z=0
    g5: LineSegment [constr] StartX=-194.483 StartY=34.2854 StartZ=0 EndX=-196.022 EndY=30.0568 EndZ=0
    g6: LineSegment [constr] StartX=-196.022 StartY=30.0568 StartZ=0 EndX=-197.561 EndY=25.8282 EndZ=0
    g7: LineSegment [constr] StartX=-197.902 StartY=30.7408 StartZ=0 EndX=-196.022 EndY=30.0568 EndZ=0
    g8: LineSegment [constr] StartX=-196.022 StartY=30.0568 StartZ=0 EndX=-194.143 EndY=29.3727 EndZ=0
    g9: LineSegment [constr] StartX=-195.338 StartY=31.9362 StartZ=0 EndX=-196.022 EndY=30.0568 EndZ=0
    g10: LineSegment [constr] StartX=-196.022 StartY=30.0568 StartZ=0 EndX=-196.706 EndY=28.1774 EndZ=0
    g11: LineSegment [constr] StartX=-196.022 StartY=30.0568 StartZ=0 EndX=-196.821 EndY=30.3475 EndZ=0
    g12: LineSegment [constr] StartX=-196.022 StartY=30.0568 StartZ=0 EndX=-195.223 EndY=29.7661 EndZ=0
    g13: LineSegment StartX=-194.539 StartY=31.6454 StartZ=0 EndX=-195.907 EndY=27.8867 EndZ=0
    g14: LineSegment StartX=-196.137 StartY=32.2269 StartZ=0 EndX=-197.505 EndY=28.4681 EndZ=0
    g15: LineSegment StartX=-196.137 StartY=32.2269 StartZ=0 EndX=-194.539 EndY=31.6454 EndZ=0
    g16: LineSegment StartX=-197.505 StartY=28.4681 StartZ=0 EndX=-195.907 EndY=27.8867 EndZ=0
  constraints (34):
    c: Symmetric(g-5,g-5,g1)
    c: Symmetric(g-5,g-6,g0)
    c: Symmetric(g-6,g-6,g3)
    c: Symmetric(g-5,g-6,g2)
    c: Coincident(g5,g1)
    c: Coincident(g5,g4)
    c: Coincident(g6,g4)
    c: Coincident(g6,g3)
    c: Equal(g5,g6)
    c: Coincident(g7,g2)
    c: Coincident(g7,g4)
    c: Coincident(g8,g4)
    c: Coincident(g8,g0)
    c: Equal(g7,g8)
    c: Coincident(g11,g9)
    c: Coincident(g12,g9)
    c: Tangent(g10,g9) = -1.5708
    c: Perpendicular(g11,g9)
    c: Parallel(g9,g-4)
    c: Equal(g9,g10)
    c: Parallel(g12,g11)
    c: Equal(g11,g12)
    c: Distance(g11,g12) = 1.7
    c: Distance(g9,g10) = 4
    c: Symmetric(g13,g13,g12)
    c: Parallel(g13,g9)
    c: Symmetric(g14,g14,g11)
    c: Symmetric(g15,g15,g9)
    c: Parallel(g15,g11)
    c: Symmetric(g16,g16,g10)
    c: Coincident(g16,g14)
    c: Coincident(g15,g14)
    c: Coincident(g13,g15)
    c: Coincident(g9,g4)
FEATURE [Sketcher::SketchObject] Sketch057  label="buco interno per SWITCH"
  ArcFitTolerance = 1e-06
  AttachmentSupport = -> [XZ_Plane]
  ExternalGeometry = -> [Sketch]
  FullyConstrained = true
  MakeInternals = false
  MapMode = 5
  Placement = pos=(0,0,0) rot=(1,0,0;1.5708rad)
  sketch-geometry (10):
    g0: GeomPoint [constr] X=-187.821 Y=29.2 Z=0
    g1: LineSegment [constr] StartX=-188.505 StartY=27.3206 StartZ=0 EndX=-193.203 EndY=29.0307 EndZ=0
    g2: LineSegment [constr] StartX=-190.809 StartY=35.6086 StartZ=0 EndX=-195.597 EndY=22.4529 EndZ=0
    g3: GeomPoint [constr] X=-193.203 Y=29.0307 Z=0
    g4: LineSegment [constr] StartX=-196.492 StartY=30.2278 StartZ=0 EndX=-189.914 EndY=27.8336 EndZ=0
    g5: LineSegment StartX=-194.098 StartY=36.8056 StartZ=0 EndX=-187.52 EndY=34.4115 EndZ=0
    g6: LineSegment StartX=-194.098 StartY=36.8056 StartZ=0 EndX=-198.886 EndY=23.6499 EndZ=0
    g7: LineSegment StartX=-187.52 StartY=34.4115 StartZ=0 EndX=-192.308 EndY=21.2558 EndZ=0
    g8: LineSegment StartX=-198.886 StartY=23.6499 StartZ=0 EndX=-192.308 EndY=21.2558 EndZ=0
    g9: LineSegment [constr] StartX=-187.821 StartY=29.2 StartZ=0 EndX=-188.505 EndY=27.3206 EndZ=0
  constraints (23):
    c: Symmetric(g-3,g-3,g0)
    c: Perpendicular(g1,g-3)
    c: Parallel(g2,g-3)
    c: Symmetric(g2,g2,g3)
    c: Perpendicular(g2,g4)
    c: Symmetric(g4,g4,g3)
    c: Distance(g2) = 14
    c: Distance(g4) = 7
    c: Distance(g1) = 5
    c: Parallel(g5,g4)
    c: Parallel(g7,g2)
    c: Symmetric(g5,g5,g2)
    c: Symmetric(g6,g6,g4)
    c: Symmetric(g7,g7,g4)
    c: Symmetric(g8,g8,g2)
    c: Coincident(g6,g5)
    c: Coincident(g7,g5)
    c: Coincident(g8,g7)
    c: Coincident(g3,g1)
    c: Coincident(g9,g0)
    c: Parallel(g9,g-3)
    c: Distance(g9) = 2
    c: Coincident(g1,g9)
FEATURE [Sketcher::SketchObject] Sketch058  label="buco esterno per SWITCH"
  ArcFitTolerance = 1e-06
  AttachmentSupport = -> [XZ_Plane]
  ExternalGeometry = -> [Sketch057]
  FullyConstrained = true
  MakeInternals = false
  MapMode = 5
  Placement = pos=(0,0,0) rot=(1,0,0;1.5708rad)
  sketch-geometry (12):
    g0: GeomPoint [constr] X=-190.809 Y=35.6086 Z=0
    g1: GeomPoint [constr] X=-196.492 Y=30.2278 Z=0
    g2: GeomPoint [constr] X=-189.914 Y=27.8336 Z=0
    g3: GeomPoint [constr] X=-195.597 Y=22.4529 Z=0
    g4: GeomPoint [constr] X=-193.203 Y=29.0307 Z=0
    g5: LineSegment [constr] StartX=-192.006 StartY=32.3196 StartZ=0 EndX=-194.4 EndY=25.7418 EndZ=0
    g6: GeomPoint [constr] X=-193.203 Y=29.0307 Z=0
    g7: LineSegment [constr] StartX=-195.082 StartY=29.7148 StartZ=0 EndX=-191.324 EndY=28.3467 EndZ=0
    g8: LineSegment StartX=-193.885 StartY=33.0037 StartZ=0 EndX=-190.127 EndY=31.6356 EndZ=0
    g9: LineSegment StartX=-190.127 StartY=31.6356 StartZ=0 EndX=-192.521 EndY=25.0578 EndZ=0
    g10: LineSegment StartX=-196.28 StartY=26.4258 StartZ=0 EndX=-192.521 EndY=25.0578 EndZ=0
    g11: LineSegment StartX=-193.885 StartY=33.0037 StartZ=0 EndX=-196.28 EndY=26.4258 EndZ=0
  constraints (21):
    c: Symmetric(g-6,g-6,g3)
    c: Symmetric(g-4,g-6,g2)
    c: Symmetric(g-5,g-4,g0)
    c: Symmetric(g-5,g-6,g1)
    c: Symmetric(g1,g2,g4)
    c: Parallel(g5,g-4)
    c: Symmetric(g5,g5,g6)
    c: Perpendicular(g7,g5)
    c: Symmetric(g7,g7,g6)
    c: Distance(g5) = 7
    c: Distance(g7) = 4
    c: Parallel(g8,g7)
    c: Parallel(g11,g5)
    c: Symmetric(g8,g8,g5)
    c: Symmetric(g9,g9,g7)
    c: Symmetric(g10,g10,g5)
    c: Symmetric(g11,g11,g7)
    c: Coincident(g11,g8)
    c: Coincident(g9,g8)
    c: Coincident(g9,g10)
    c: Coincident(g6,g4)
FEATURE [Part::Extrusion] Extrude060  label="Extrude buco interno per SWITCH destro"
  Base = -> Sketch057
  Dir = (0,-1,2e-16)
  DirMode = 2
  FaceMakerClass = Part::FaceMakerBullseye
  FaceMakerMode = 3
  LengthFwd = 13.2
  LengthRev = 0
  Placement = pos=(0,2.6,0) rot=(0,0,1;0rad)
  Solid = true
  Symmetric = false
FEATURE [Part::Extrusion] Extrude061  label="Extrude buco esterno per SWITCH destro"
  Base = -> Sketch058
  Dir = (0,-1,2e-16)
  DirMode = 2
  FaceMakerClass = Part::FaceMakerBullseye
  FaceMakerMode = 3
  LengthFwd = 2
  LengthRev = 0
  Placement = pos=(0,-10.6,0) rot=(0,0,1;0rad)
  Solid = true
  Symmetric = false
FEATURE [Sketcher::SketchObject] Sketch059  label="buco per spazio introduzione SWITCH"
  ArcFitTolerance = 1e-06
  AttachmentSupport = -> [XZ_Plane]
  ExternalGeometry = -> [Sketch057,Sketch010]
  FullyConstrained = true
  MakeInternals = false
  MapMode = 5
  Placement = pos=(0,0,0) rot=(1,0,0;1.5708rad)
  sketch-geometry (8):
    g0: LineSegment [constr] StartX=-201.368 StartY=36.3521 StartZ=0 EndX=-195.094 EndY=34.0687 EndZ=0
    g1: LineSegment [constr] StartX=-194.098 StartY=36.8056 StartZ=0 EndX=-195.094 EndY=34.0687 EndZ=0
    g2: LineSegment StartX=-198.658 StartY=24.2771 StartZ=0 EndX=-199.654 EndY=21.5401 EndZ=0
    g3: LineSegment StartX=-199.654 StartY=21.5401 StartZ=0 EndX=-181.196 EndY=14.822 EndZ=0
    g4: LineSegment StartX=-181.196 StartY=14.822 StartZ=0 EndX=-180.2 EndY=17.559 EndZ=0
    g5: LineSegment StartX=-180.2 StartY=17.559 StartZ=0 EndX=-198.658 EndY=24.2771 EndZ=0
    g6: LineSegment [constr] StartX=-204.932 StartY=26.5605 StartZ=0 EndX=-198.658 EndY=24.2771 EndZ=0
    g7: LineSegment [constr] StartX=-198.658 StartY=24.2771 StartZ=0 EndX=-199.654 EndY=21.5401 EndZ=0
  constraints (20):
    c: Parallel(g1,g-3)
    c: Parallel(g0,g-4)
    c: Coincident(g0,g-4)
    c: Coincident(g1,g-3)
    c: Coincident(g0,g1)
    c: Coincident(g3,g2)
    c: Coincident(g4,g3)
    c: Coincident(g5,g4)
    c: Coincident(g5,g2)
    c: Parallel(g5,g-5)
    c: Parallel(g3,g-5)
    c: Parallel(g4,g-6)
    c: DistanceX(g-6,g4) = 0
    c: Coincident(g6,g-5)
    c: Equal(g6,g0)
    c: Coincident(g7,g6)
    c: Equal(g7,g1)
    c: Tangent(g7,g-3)
    c: Coincident(g2,g6)
    c: Coincident(g2,g7)
FEATURE [Part::Extrusion] Extrude062  label="Extrude buco per spazio introduzione SWITCH"
  Base = -> Sketch059
  Dir = (0,-1,2e-16)
  DirMode = 2
  FaceMakerClass = Part::FaceMakerBullseye
  FaceMakerMode = 3
  LengthFwd = 13.2
  LengthRev = 0
  Solid = true
  Symmetric = true
FEATURE [Part::Extrusion] Extrude063  label="Extrude buco interno per SWITCH sinistro"
  Base = -> Sketch057
  Dir = (0,-1,2e-16)
  DirMode = 2
  FaceMakerClass = Part::FaceMakerBullseye
  FaceMakerMode = 3
  LengthFwd = 13.2
  LengthRev = 0
  Placement = pos=(0,10.6,0) rot=(0,0,1;0rad)
  Solid = true
  Symmetric = false
FEATURE [Part::Extrusion] Extrude064  label="Extrude buco esterno per SWITCH sinistro"
  Base = -> Sketch058
  Dir = (0,-1,2e-16)
  DirMode = 2
  FaceMakerClass = Part::FaceMakerBullseye
  FaceMakerMode = 3
  LengthFwd = 2
  LengthRev = 0
  Placement = pos=(0,12.6,0) rot=(0,0,1;0rad)
  Solid = true
  Symmetric = false
FEATURE [Sketcher::SketchObject] Sketch061  label="struttura esterna blocco switch"
  ArcFitTolerance = 1e-06
  AttachmentSupport = -> [XZ_Plane003]
  FullyConstrained = true
  MakeInternals = false
  MapMode = 5
  Placement = pos=(0,0,0) rot=(1,0,0;1.5708rad)
  sketch-geometry (5):
    g0: LineSegment StartX=-1 StartY=-5.1 StartZ=0 EndX=1 EndY=-5.1 EndZ=0
    g1: LineSegment StartX=1 StartY=-5.1 StartZ=0 EndX=1 EndY=5.1 EndZ=0
    g2: LineSegment StartX=1 StartY=5.1 StartZ=0 EndX=-1 EndY=5.1 EndZ=0
    g3: LineSegment StartX=-1 StartY=5.1 StartZ=0 EndX=-1 EndY=-5.1 EndZ=0
    g4: GeomPoint [constr] X=0 Y=0 Z=0
  constraints (12):
    c: Coincident(g0,g1)
    c: Coincident(g1,g2)
    c: Coincident(g2,g3)
    c: Coincident(g3,g0)
    c: Horizontal(g0)
    c: Horizontal(g2)
    c: Vertical(g1)
    c: Vertical(g3)
    c: Symmetric(g2,g0,g4)
    c: Distance(g1,g3) = 2
    c: Distance(g0,g2) = 10.2
    c: Coincident(g4,g-1)
FEATURE [Sketcher::SketchObject] Sketch062  label="struttura interna blocco switch"
  ArcFitTolerance = 1e-06
  AttachmentSupport = -> [XZ_Plane003]
  ExternalGeometry = -> [Sketch061]
  FullyConstrained = true
  MakeInternals = false
  MapMode = 5
  Placement = pos=(0,0,0) rot=(1,0,0;1.5708rad)
  sketch-geometry (5):
    g0: LineSegment StartX=-1 StartY=3.1 StartZ=0 EndX=-1 EndY=-3.1 EndZ=0
    g1: LineSegment StartX=-1 StartY=-3.1 StartZ=0 EndX=1 EndY=-3.1 EndZ=0
    g2: LineSegment StartX=1 StartY=-3.1 StartZ=0 EndX=1 EndY=3.1 EndZ=0
    g3: LineSegment StartX=1 StartY=3.1 StartZ=0 EndX=-1 EndY=3.1 EndZ=0
    g4: GeomPoint [constr] X=0 Y=0 Z=0
  constraints (12):
    c: Coincident(g0,g1)
    c: Coincident(g1,g2)
    c: Coincident(g2,g3)
    c: Coincident(g3,g0)
    c: Vertical(g0)
    c: Vertical(g2)
    c: Horizontal(g1)
    c: Horizontal(g3)
    c: Symmetric(g2,g0,g4)
    c: Coincident(g4,g-1)
    c: Distance(g0) = 6.2
    c: Equal(g3,g-3)
FEATURE [Sketcher::SketchObject] Sketch063  label="blocchi tra switch"
  ArcFitTolerance = 1e-06
  AttachmentSupport = -> [XZ_Plane003]
  ExternalGeometry = -> [Sketch061,Sketch062]
  FullyConstrained = true
  MakeInternals = false
  MapMode = 5
  Placement = pos=(0,0,0) rot=(1,0,0;1.5708rad)
  sketch-geometry (8):
    g0: LineSegment StartX=-3 StartY=5.1 StartZ=0 EndX=-1 EndY=5.1 EndZ=0
    g1: LineSegment StartX=-1 StartY=5.1 StartZ=0 EndX=-1 EndY=3.1 EndZ=0
    g2: LineSegment StartX=-1 StartY=3.1 StartZ=0 EndX=-3 EndY=3.1 EndZ=0
    g3: LineSegment StartX=-3 StartY=3.1 StartZ=0 EndX=-3 EndY=5.1 EndZ=0
    g4: LineSegment StartX=-3 StartY=-3.1 StartZ=0 EndX=-1 EndY=-3.1 EndZ=0
    g5: LineSegment StartX=-1 StartY=-3.1 StartZ=0 EndX=-1 EndY=-5.1 EndZ=0
    g6: LineSegment StartX=-1 StartY=-5.1 StartZ=0 EndX=-3 EndY=-5.1 EndZ=0
    g7: LineSegment StartX=-3 StartY=-5.1 StartZ=0 EndX=-3 EndY=-3.1 EndZ=0
  constraints (20):
    c: Horizontal(g0)
    c: Coincident(g1,g0)
    c: Coincident(g2,g1)
    c: Horizontal(g2)
    c: Coincident(g3,g2)
    c: Coincident(g3,g0)
    c: Vertical(g3)
    c: Horizontal(g4)
    c: Coincident(g5,g4)
    c: Coincident(g6,g5)
    c: Horizontal(g6)
    c: Coincident(g7,g6)
    c: Coincident(g7,g4)
    c: Vertical(g7)
    c: Coincident(g0,g-4)
    c: Coincident(g1,g-5)
    c: Coincident(g4,g-6)
    c: Coincident(g5,g-7)
    c: Distance(g0) = 2
    c: Distance(g4) = 2
FEATURE [Sketcher::SketchObject] Sketch066  label="piano per rampino"
  ArcFitTolerance = 1e-06
  AttachmentSupport = -> [XZ_Plane002]
  ExternalGeometry = -> [Sketch045]
  FullyConstrained = true
  MakeInternals = false
  MapMode = 5
  Placement = pos=(0,0,0) rot=(1,0,0;1.5708rad)
  sketch-geometry (4):
    g0: LineSegment StartX=5.4 StartY=5.1 StartZ=0 EndX=5.4 EndY=3.9 EndZ=0
    g1: LineSegment StartX=5.4 StartY=3.9 StartZ=0 EndX=7 EndY=3.9 EndZ=0
    g2: LineSegment StartX=7 StartY=3.9 StartZ=0 EndX=7 EndY=5.1 EndZ=0
    g3: LineSegment StartX=7 StartY=5.1 StartZ=0 EndX=5.4 EndY=5.1 EndZ=0
  constraints (11):
    c: Coincident(g0,g1)
    c: Coincident(g1,g2)
    c: Coincident(g2,g3)
    c: Coincident(g3,g0)
    c: Vertical(g0)
    c: Vertical(g2)
    c: Horizontal(g1)
    c: Horizontal(g3)
    c: Distance(g0,g2) = 1.6
    c: Distance(g1,g3) = 1.2
    c: Coincident(g2,g-3)
FEATURE [Sketcher::SketchObject] Sketch064  label="rampini_per_serraggio_struttura"
  ArcFitTolerance = 1e-06
  AttachmentSupport = -> [XZ_Plane002]
  ExternalGeometry = -> [Sketch066,Sketch045]
  FullyConstrained = true
  MakeInternals = false
  MapMode = 5
  Placement = pos=(0,0,0) rot=(1,0,0;1.5708rad)
  sketch-geometry (7):
    g0: LineSegment StartX=7 StartY=5.1 StartZ=0 EndX=7 EndY=3.9 EndZ=0
    g1: LineSegment StartX=7 StartY=3.9 StartZ=0 EndX=9 EndY=3.9 EndZ=0
    g2: LineSegment StartX=7 StartY=5.1 StartZ=0 EndX=7 EndY=5.1 EndZ=0
    g3: LineSegment StartX=7 StartY=5.1 StartZ=0 EndX=7 EndY=7.5 EndZ=0
    g4: LineSegment StartX=9 StartY=5.1 StartZ=0 EndX=9 EndY=3.9 EndZ=0
    g5: LineSegment StartX=7 StartY=7.5 StartZ=0 EndX=9 EndY=7.5 EndZ=0
    g6: LineSegment StartX=9 StartY=7.5 StartZ=0 EndX=9 EndY=5.1 EndZ=0
  constraints (20):
    c: Vertical(g0)
    c: Coincident(g1,g0)
    c: Horizontal(g1)
    c: Coincident(g2,g0)
    c: Horizontal(g2)
    c: Coincident(g3,g2)
    c: Vertical(g3)
    c: Coincident(g5,g3)
    c: Coincident(g4,g6)
    c: Coincident(g4,g1)
    c: Vertical(g4)
    c: Coincident(g0,g-3)
    c: DistanceY(g-4,g3) = 2.4
    c: DistanceX(g1,g1) = 2
    c: DistanceY(g2,g6) = 0
    c: DistanceX(g2,g2) = 0
    c: DistanceY(g0,g0) = 1.2
    c: Coincident(g5,g6)
    c: Horizontal(g5)
    c: Vertical(g6)
FEATURE [Sketcher::SketchObject] Sketch067  label="perno per blocco switch"
  ArcFitTolerance = 1e-06
  AttachmentSupport = -> [XZ_Plane]
  ExternalGeometry = -> [Sketch,Sketch010]
  FullyConstrained = true
  MakeInternals = false
  MapMode = 5
  Placement = pos=(0,0,0) rot=(1,0,0;1.5708rad)
  sketch-geometry (14):
    g0: LineSegment StartX=-191.073 StartY=24.9429 StartZ=0 EndX=-185.81 EndY=23.0276 EndZ=0
    g1: LineSegment StartX=-183.76 StartY=23.9839 StartZ=0 EndX=-182.392 EndY=27.7427 EndZ=0
    g2: LineSegment StartX=-183.348 StartY=29.7934 StartZ=0 EndX=-188.61 EndY=31.7087 EndZ=0
    g3: LineSegment StartX=-188.61 StartY=31.7087 StartZ=0 EndX=-191.073 EndY=24.9429 EndZ=0
    g4: GeomPoint [constr] X=-186.459 Y=27.0946 Z=0
    g5: LineSegment StartX=-189.022 StartY=25.8992 StartZ=0 EndX=-185.263 EndY=24.5311 EndZ=0
    g6: LineSegment StartX=-185.263 StartY=24.5311 StartZ=0 EndX=-183.895 EndY=28.2899 EndZ=0
    g7: LineSegment StartX=-183.895 StartY=28.2899 StartZ=0 EndX=-187.654 EndY=29.658 EndZ=0
    g8: LineSegment StartX=-187.654 StartY=29.658 StartZ=0 EndX=-189.022 EndY=25.8992 EndZ=0
    g9: GeomPoint [constr] X=-186.459 Y=27.0946 Z=0
    g10: ArcOfCircle CenterX=-185.263 CenterY=24.5311 CenterZ=0 NormalX=0 NormalY=0 NormalZ=1 AngleXU=0 Radius=1.6 StartAngle=4.36332 EndAngle=5.93412
    g11: GeomPoint [constr] X=-184.307 Y=22.4804 Z=0
    g12: ArcOfCircle CenterX=-183.895 CenterY=28.2899 CenterZ=0 NormalX=0 NormalY=0 NormalZ=1 AngleXU=0 Radius=1.6 StartAngle=5.93412 EndAngle=7.50492
    g13: GeomPoint [constr] X=-181.844 Y=29.2462 Z=0
  constraints (30):
    c: Coincident(g2,g3)
    c: Coincident(g3,g0)
    c: Symmetric(g13,g0,g4)
    c: Distance(g11,g3) = 7.2
    c: Distance(g0,g2) = 7.2
    c: Parallel(g3,g1)
    c: Parallel(g2,g0)
    c: Perpendicular(g2,g3)
    c: Coincident(g5,g6)
    c: Coincident(g6,g7)
    c: Coincident(g7,g8)
    c: Coincident(g8,g5)
    c: Symmetric(g7,g5,g9)
    c: Distance(g6,g8) = 4
    c: Distance(g5,g7) = 4
    c: Coincident(g9,g4)
    c: Parallel(g8,g6)
    c: Parallel(g7,g5)
    c: Perpendicular(g7,g8)
    c: Tangent(g8,g-3)
    c: Tangent(g2,g-4)
    c: PointOnObject(g11,g1)
    c: PointOnObject(g11,g0)
    c: Tangent(g1,g10) = -1.5708
    c: Tangent(g0,g10) = -1.5708
    c: PointOnObject(g13,g1)
    c: Tangent(g1,g12) = -1.5708
    c: Tangent(g2,g12) = -1.5708
    c: Equal(g10,g12)
    c: Coincident(g10,g5)
FEATURE [Part::Extrusion] Extrude072  label="Extrude perno per blocco switch"
  Base = -> Sketch067
  Dir = (0,-1,2e-16)
  DirMode = 2
  FaceMakerClass = Part::FaceMakerBullseye
  FaceMakerMode = 3
  LengthFwd = 25.2
  LengthRev = 0
  Solid = true
  Symmetric = true
FEATURE [Part::MultiFuse] Fusion
  Refine = true
  Shapes = -> [Extrude,Sweep,Extrude007,Extrude011,Extrude005,Extrude012,Extrude013,Extrude016,Extrude031,Extrude039,Extrude045,Extrude072]
FEATURE [Part::Cut] Cut
  Base = -> Fusion
  Refine = true
  Tool = -> Extrude001
FEATURE [Part::Cut] Cut001
  Base = -> Cut
  Refine = true
  Tool = -> Extrude004
FEATURE [Part::Cut] Cut002
  Base = -> Cut001
  Refine = true
  Tool = -> Extrude006
FEATURE [Part::Cut] Cut003
  Base = -> Cut002
  Refine = true
  Tool = -> Extrude008
FEATURE [Part::Cut] Cut004
  Base = -> Cut003
  Refine = true
  Tool = -> Extrude009
FEATURE [Part::Cut] Cut005
  Base = -> Cut004
  Refine = true
  Tool = -> Extrude010
FEATURE [Part::Cut] Cut006
  Base = -> Cut005
  Refine = true
  Tool = -> Extrude014
FEATURE [Part::Cut] Cut007
  Base = -> Cut006
  Refine = true
  Tool = -> Extrude015
FEATURE [Part::Cut] Cut008
  Base = -> Cut007
  Refine = true
  Tool = -> Extrude018
FEATURE [Part::Cut] Cut009
  Base = -> Cut008
  Refine = true
  Tool = -> Extrude019
FEATURE [Part::Cut] Cut010
  Base = -> Cut009
  Refine = true
  Tool = -> Extrude020
FEATURE [Part::Cut] Cut011
  Base = -> Cut010
  Refine = true
  Tool = -> Extrude021
FEATURE [Part::Cut] Cut012
  Base = -> Cut011
  Refine = true
  Tool = -> Extrude022
FEATURE [Part::Cut] Cut013
  Base = -> Cut012
  Refine = true
  Tool = -> Extrude023
FEATURE [Part::Cut] Cut014
  Base = -> Cut013
  Refine = true
  Tool = -> Extrude032
FEATURE [Part::Cut] Cut015
  Base = -> Cut014
  Refine = true
  Tool = -> Extrude033
FEATURE [Part::Cut] Cut016
  Base = -> Cut015
  Refine = true
  Tool = -> Extrude034
FEATURE [Part::Cut] Cut017
  Base = -> Cut016
  Refine = true
  Tool = -> Extrude035
FEATURE [Part::Cut] Cut018
  Base = -> Cut017
  Refine = true
  Tool = -> Extrude036
FEATURE [Part::Cut] Cut019
  Base = -> Cut018
  Refine = true
  Tool = -> Extrude037
FEATURE [Part::Cut] Cut020
  Base = -> Cut019
  Refine = true
  Tool = -> Extrude030
FEATURE [Part::Cut] Cut022
  Base = -> Cut020
  Refine = true
  Tool = -> Extrude038
FEATURE [Part::Cut] Cut023
  Base = -> Cut022
  Refine = true
  Tool = -> Extrude041
FEATURE [Part::Cut] Cut024
  Base = -> Cut023
  Refine = true
  Tool = -> Extrude040
FEATURE [Part::Cut] Cut025
  Base = -> Cut024
  Refine = true
  Tool = -> Extrude042
FEATURE [Part::Cut] Cut026
  Base = -> Cut025
  Refine = true
  Tool = -> Extrude043
FEATURE [Part::Cut] Cut027
  Base = -> Cut026
  Refine = true
  Tool = -> Extrude044
FEATURE [Part::Cut] Cut028
  Base = -> Cut027
  Refine = true
  Tool = -> Extrude046
FEATURE [Part::Cut] Cut029
  Base = -> Cut028
  Refine = true
  Tool = -> Extrude047
FEATURE [Part::Cut] Cut033
  Base = -> Cut029
  Refine = true
  Tool = -> Extrude055
FEATURE [Part::Cut] Cut034
  Base = -> Cut033
  Refine = true
  Tool = -> Extrude056
FEATURE [Part::Cut] Cut035
  Base = -> Cut034
  Refine = true
  Tool = -> Extrude057
FEATURE [Part::Cut] Cut037
  Base = -> Cut035
  Refine = true
  Tool = -> Extrude060
FEATURE [Part::Cut] Cut038
  Base = -> Cut037
  Refine = true
  Tool = -> Extrude061
FEATURE [Part::Cut] Cut039
  Base = -> Cut038
  Refine = true
  Tool = -> Extrude063
FEATURE [Part::Cut] Cut040
  Base = -> Cut039
  Refine = true
  Tool = -> Extrude064
FEATURE [Part::Cut] Cut041
  Base = -> Cut040
  Refine = true
  Tool = -> Extrude062
FEATURE [Sketcher::SketchObject] Sketch068  label="base con smusso sopra neopixel"
  ArcFitTolerance = 1e-06
  AttachmentSupport = -> [YZ_Plane002]
  FullyConstrained = true
  MakeInternals = false
  MapMode = 5
  Placement = pos=(0,0,0) rot=(0.57735,0.57735,0.57735;2.0944rad)
  sketch-geometry (5):
    g0: LineSegment StartX=-9.5 StartY=-6.1 StartZ=0 EndX=9.5 EndY=-6.1 EndZ=0
    g1: LineSegment StartX=9.5 StartY=-6.1 StartZ=0 EndX=9.5 EndY=6.1 EndZ=0
    g2: LineSegment StartX=9.5 StartY=6.1 StartZ=0 EndX=-9.5 EndY=6.1 EndZ=0
    g3: LineSegment StartX=-9.5 StartY=6.1 StartZ=0 EndX=-9.5 EndY=-6.1 EndZ=0
    g4: GeomPoint [constr] X=0 Y=0 Z=0
  constraints (12):
    c: Coincident(g0,g1)
    c: Coincident(g1,g2)
    c: Coincident(g2,g3)
    c: Coincident(g3,g0)
    c: Horizontal(g0)
    c: Horizontal(g2)
    c: Vertical(g1)
    c: Vertical(g3)
    c: Symmetric(g2,g0,g4)
    c: Distance(g1,g3) = 19
    c: Distance(g0,g2) = 12.2
    c: Coincident(g4,g-1)
FEATURE [Sketcher::SketchObject] Sketch069  label="cilindro minore"
  ArcFitTolerance = 1e-06
  AttachmentSupport = -> [XZ_Plane004]
  FullyConstrained = true
  MakeInternals = false
  MapMode = 5
  Placement = pos=(0,0,0) rot=(1,0,0;1.5708rad)
  sketch-geometry (1):
    g0: Circle CenterX=0 CenterY=0 CenterZ=0 NormalX=0 NormalY=0 NormalZ=1 AngleXU=0 Radius=5.8
  constraints (2):
    c: Diameter(g0) = 11.6
    c: Coincident(g0,g-1)
FEATURE [Sketcher::SketchObject] Sketch070  label="cilindro maggiore"
  ArcFitTolerance = 1e-06
  AttachmentSupport = -> [XZ_Plane004]
  ExternalGeometry = -> [Sketch069]
  FullyConstrained = true
  MakeInternals = false
  MapMode = 5
  Placement = pos=(0,0,0) rot=(1,0,0;1.5708rad)
  sketch-geometry (1):
    g0: Circle CenterX=0 CenterY=0 CenterZ=0 NormalX=0 NormalY=0 NormalZ=1 AngleXU=0 Radius=6.5
  constraints (2):
    c: Coincident(g0,g-1)
    c: Diameter(g0) = 13
FEATURE [Sketcher::SketchObject] Sketch071  label="buco interno"
  ArcFitTolerance = 1e-06
  AttachmentSupport = -> [XZ_Plane004]
  ExternalGeometry = -> [Sketch069]
  FullyConstrained = true
  MakeInternals = false
  MapMode = 5
  Placement = pos=(0,0,0) rot=(1,0,0;1.5708rad)
  sketch-geometry (1):
    g0: Circle CenterX=0 CenterY=0 CenterZ=0 NormalX=0 NormalY=0 NormalZ=1 AngleXU=0 Radius=5
  constraints (2):
    c: Coincident(g0,g-1)
    c: Diameter(g0) = 10
FEATURE [PartDesign::Pad] Pad
  Direction = (0,-1,2e-16)
  Length = 1.2
  Length2 = 10
  Placement = pos=(0,0,0) rot=(1,0,0;1.5708rad)
  Profile = -> Sketch070
  ReferenceAxis = -> Sketch070 [N_Axis]
  Refine = true
  Suppressed = false
  Type = 0
FEATURE [PartDesign::Pad] Pad001
  BaseFeature = -> Pad
  Direction = (0,-1,2e-16)
  Length = 5.6
  Length2 = 10
  Placement = pos=(0,0,0) rot=(1,0,0;1.5708rad)
  Profile = -> Sketch069
  ReferenceAxis = -> Sketch069 [N_Axis]
  Refine = true
  Suppressed = false
  Type = 0
FEATURE [PartDesign::Pocket] Pocket
  BaseFeature = -> Pad001
  Direction = (0,1,-2e-16)
  Length = 7
  Length2 = 5
  Midplane = true
  Placement = pos=(0,0,0) rot=(1,0,0;1.5708rad)
  Profile = -> Sketch071
  ReferenceAxis = -> Sketch071 [N_Axis]
  Refine = true
  Suppressed = false
  Type = 0
FEATURE [PartDesign::Fillet] Fillet
  Base = -> Pocket [Face7]
  BaseFeature = -> Pocket
  Placement = pos=(0,0,0) rot=(1,0,0;1.5708rad)
  Radius = 1
  Refine = true
  SupportTransform = false
  Suppressed = false
  UseAllEdges = false
FEATURE [PartDesign::Body] Body004  label="pulsanti lato sinistro"
  AllowCompound = false
  Group = -> [Sketch069,Sketch070,Sketch071,Pad,Pad001,Pocket,Fillet]
  Origin = -> Origin004
  Tip = -> Fillet
FEATURE [Sketcher::SketchObject] Sketch072  label="buco per saldature e diodo driver solenoide"
  ArcFitTolerance = 1e-06
  AttachmentSupport = -> [XZ_Plane]
  ExternalGeometry = -> [Sketch038]
  FullyConstrained = true
  MakeInternals = false
  MapMode = 5
  Placement = pos=(0,0,0) rot=(1,0,0;1.5708rad)
  sketch-geometry (4):
    g0: LineSegment StartX=-212.269 StartY=-43.9083 StartZ=0 EndX=-207.197 EndY=-33.0326 EndZ=0
    g1: LineSegment StartX=-207.197 StartY=-33.0326 StartZ=0 EndX=-207.56 EndY=-32.8635 EndZ=0
    g2: LineSegment StartX=-207.56 StartY=-32.8635 StartZ=0 EndX=-212.631 EndY=-43.7392 EndZ=0
    g3: LineSegment StartX=-212.631 StartY=-43.7392 StartZ=0 EndX=-212.269 EndY=-43.9083 EndZ=0
  constraints (11):
    c: Coincident(g1,g0)
    c: Coincident(g2,g1)
    c: Coincident(g3,g2)
    c: Coincident(g3,g0)
    c: Parallel(g-3,g0)
    c: Parallel(g0,g2)
    c: Perpendicular(g0,g3)
    c: Perpendicular(g1,g0)
    c: Distance(g3) = 0.4
    c: Distance(g2) = 12
    c: Coincident(g0,g-3)
FEATURE [Part::Extrusion] Extrude074  label="Extrude buco per saldature e diodo driver solenoide"
  Base = -> Sketch072
  Dir = (0,-1,2e-16)
  DirMode = 2
  FaceMakerClass = Part::FaceMakerBullseye
  FaceMakerMode = 3
  LengthFwd = 14.6
  LengthRev = 0
  Solid = true
  Symmetric = true
FEATURE [Part::Cut] Cut042
  Base = -> Cut041
  Refine = true
  Tool = -> Extrude074
FEATURE [Sketcher::SketchObject] Sketch073  label="fori slargati blocco solenoide"
  ArcFitTolerance = 1e-06
  AttachmentSupport = -> [XY_Plane]
  ExternalGeometry = -> [Sketch030]
  FullyConstrained = true
  MakeInternals = false
  MapMode = 5
  sketch-geometry (2):
    g0: Circle CenterX=-152.209 CenterY=6.95 CenterZ=0 NormalX=0 NormalY=0 NormalZ=1 AngleXU=0 Radius=3.7
    g1: Circle CenterX=-130.41 CenterY=-6.95 CenterZ=0 NormalX=0 NormalY=0 NormalZ=1 AngleXU=0 Radius=3.7
  constraints (4):
    c: Diameter(g0) = 7.4
    c: Coincident(g0,g-3)
    c: Diameter(g1) = 7.4
    c: Coincident(g1,g-4)
FEATURE [Part::Extrusion] Extrude075  label="Extrude fori slargati blocco solenoide"
  Base = -> Sketch073
  Dir = (0,0,1)
  DirMode = 2
  FaceMakerClass = Part::FaceMakerBullseye
  FaceMakerMode = 3
  LengthFwd = 1.5
  LengthRev = 0
  Placement = pos=(0,0,36.4) rot=(0,0,1;0rad)
  Solid = true
  Symmetric = false
FEATURE [Part::Cut] Cut043
  Base = -> Cut042
  Refine = true
  Tool = -> Extrude075
FEATURE [Sketcher::SketchObject] Sketch074  label="lato sx pistola"
  ArcFitTolerance = 1e-06
  AttachmentSupport = -> [XZ_Plane]
  ExternalGeometry = -> [Sketch016,Sketch,Sketch058]
  FullyConstrained = true
  MakeInternals = false
  MapMode = 5
  Placement = pos=(0,0,0) rot=(1,0,0;1.5708rad)
  sketch-geometry (37):
    g0: LineSegment StartX=-82.8 StartY=3.2 StartZ=0 EndX=0 EndY=3.2 EndZ=0
    g1: LineSegment StartX=-82.8 StartY=3.2 StartZ=0 EndX=-82.8 EndY=6.2 EndZ=0
    g2: LineSegment [constr] StartX=-107.6 StartY=18 StartZ=0 EndX=-107.6 EndY=20 EndZ=0
    g3: LineSegment [constr] StartX=-132.428 StartY=18 StartZ=0 EndX=-132.428 EndY=20 EndZ=0
    g4: LineSegment StartX=-132.428 StartY=20 StartZ=0 EndX=-107.6 EndY=20 EndZ=0
    g5: ArcOfCircle CenterX=-107.6 CenterY=4 CenterZ=0 NormalX=0 NormalY=0 NormalZ=1 AngleXU=0 Radius=16 StartAngle=0.137937 EndAngle=1.5708
    g6: LineSegment StartX=-82.8 StartY=6.2 StartZ=0 EndX=-91.752 EndY=6.2 EndZ=0
    g7: LineSegment [constr] StartX=-145.743 StartY=8.32624 StartZ=0 EndX=-147.645 EndY=8.94427 EndZ=0
    g8: ArcOfCircle CenterX=-132.428 CenterY=4 CenterZ=0 NormalX=0 NormalY=0 NormalZ=1 AngleXU=0 Radius=16 StartAngle=1.5708 EndAngle=2.82743
    g9: LineSegment StartX=-215.932 StartY=-80.4316 StartZ=0 EndX=-176.685 EndY=-80.4316 EndZ=0
    g10: LineSegment StartX=-147.645 StartY=8.94427 StartZ=0 EndX=-176.685 EndY=-80.4316 EndZ=0
    g11: LineSegment [constr] StartX=-193.988 StartY=-2.33927 StartZ=0 EndX=-192.176 EndY=-3.18451 EndZ=0
    g12: LineSegment [constr] StartX=-217.232 StartY=-52.1862 StartZ=0 EndX=-215.42 EndY=-53.0314 EndZ=0
    g13: LineSegment StartX=-192.176 StartY=-3.18451 StartZ=0 EndX=-215.42 EndY=-53.0314 EndZ=0
    g14: ArcOfCircle CenterX=-184.801 CenterY=-67.3089 CenterZ=0 NormalX=0 NormalY=0 NormalZ=1 AngleXU=0 Radius=33.7833 StartAngle=2.70526 EndAngle=3.54053
    g15: ArcOfCircle CenterX=-207.583 CenterY=4 CenterZ=0 NormalX=0 NormalY=0 NormalZ=1 AngleXU=0 Radius=17 StartAngle=5.84685 EndAngle=7.56663
    g16: LineSegment StartX=-202.765 StartY=20.303 StartZ=0 EndX=-195.887 EndY=39.2 EndZ=0
    g17: LineSegment [constr] StartX=-193.885 StartY=33.0037 StartZ=0 EndX=-197.644 EndY=34.3718 EndZ=0
    g18: LineSegment StartX=-195.887 StartY=39.2 StartZ=0 EndX=0 EndY=39.2 EndZ=0
    g19: LineSegment StartX=0 StartY=3.2 StartZ=0 EndX=0 EndY=39.2 EndZ=0
    g20: LineSegment StartX=-189.939 StartY=31.5672 StartZ=0 EndX=-192.333 EndY=24.9893 EndZ=0
    g21: LineSegment StartX=-196.467 StartY=26.4942 StartZ=0 EndX=-194.073 EndY=33.0721 EndZ=0
    g22: Circle CenterX=-213.443 CenterY=-76.8316 CenterZ=0 NormalX=0 NormalY=0 NormalZ=1 AngleXU=0 Radius=1.8
    g23: Circle CenterX=-179.305 CenterY=-76.8316 CenterZ=0 NormalX=0 NormalY=0 NormalZ=1 AngleXU=0 Radius=1.8
    g24: Circle CenterX=-184.08 CenterY=34.8 CenterZ=0 NormalX=0 NormalY=0 NormalZ=1 AngleXU=0 Radius=1.8
    g25: Circle CenterX=-78.51 CenterY=34.8 CenterZ=0 NormalX=0 NormalY=0 NormalZ=1 AngleXU=0 Radius=1.8
    g26: Circle CenterX=-78.51 CenterY=7.6 CenterZ=0 NormalX=0 NormalY=0 NormalZ=1 AngleXU=0 Radius=1.8
    g27: Circle CenterX=-5.6 CenterY=34.8 CenterZ=0 NormalX=0 NormalY=0 NormalZ=1 AngleXU=0 Radius=1.8
    g28: Circle CenterX=-5.6 CenterY=7.6 CenterZ=0 NormalX=0 NormalY=0 NormalZ=1 AngleXU=0 Radius=1.8
    g29: LineSegment StartX=-190.127 StartY=31.6356 StartZ=0 EndX=-189.939 EndY=31.5672 EndZ=0
    g30: LineSegment StartX=-194.073 StartY=33.0721 StartZ=0 EndX=-193.885 EndY=33.0037 EndZ=0
    g31: LineSegment StartX=-193.885 StartY=33.0037 StartZ=0 EndX=-190.127 EndY=31.6356 EndZ=0
    g32: LineSegment StartX=-196.467 StartY=26.4942 StartZ=0 EndX=-192.333 EndY=24.9893 EndZ=0
    g33: Circle CenterX=-19 CenterY=21.2 CenterZ=0 NormalX=0 NormalY=0 NormalZ=1 AngleXU=0 Radius=6.3
    g34: Circle CenterX=-42 CenterY=21.2 CenterZ=0 NormalX=0 NormalY=0 NormalZ=1 AngleXU=0 Radius=6.3
    g35: Circle CenterX=-65 CenterY=21.2 CenterZ=0 NormalX=0 NormalY=0 NormalZ=1 AngleXU=0 Radius=6.3
    g36: LineSegment [constr] StartX=-4 StartY=21.2 StartZ=0 EndX=-65 EndY=21.2 EndZ=0
  constraints (96):
    c: Coincident(g0,g-41)
    c: Horizontal(g0)
    c: PointOnObject(g0,g-39)
    c: Coincident(g1,g0)
    c: Vertical(g1)
    c: DistanceY(g1,g1) = 3
    c: Coincident(g2,g-17)
    c: Vertical(g2)
    c: Coincident(g3,g-16)
    c: Vertical(g3)
    c: DistanceY(g2,g2) = 2
    c: DistanceY(g3,g3) = 2
    c: Coincident(g4,g3)
    c: Coincident(g4,g2)
    c: Coincident(g5,g-17)
    c: Coincident(g5,g2)
    c: Coincident(g6,g1)
    c: Horizontal(g6)
    c: Coincident(g6,g5)
    c: Coincident(g7,g-15)
    c: Coincident(g8,g7)
    c: Coincident(g8,g3)
    c: Coincident(g8,g-15)
    c: Horizontal(g9)
    c: DistanceY(g-13,g9) = 2
    c: Coincident(g10,g7)
    c: Parallel(g10,g-14)
    c: Coincident(g9,g10)
    c: Distance(g11) = 2
    c: Coincident(g11,g-11)
    c: Perpendicular(g-11,g11)
    c: Distance(g12) = 2
    c: Coincident(g12,g-12)
    c: Perpendicular(g-11,g12)
    c: Coincident(g13,g11)
    c: Coincident(g13,g12)
    c: Coincident(g14,g-32)
    c: Coincident(g14,g12)
    c: Coincident(g14,g9)
    c: Coincident(g15,g-10)
    c: Coincident(g15,g11)
    c: Parallel(g16,g-22)
    c: Distance(g17) = 4
    c: PointOnObject(g17,g16)
    c: Coincident(g15,g16)
    c: Horizontal(g18)
    c: Coincident(g18,g16)
    c: Coincident(g19,g0)
    c: PointOnObject(g19,g-39)
    c: DistanceY(g19,g-36) = 2
    c: Coincident(g18,g19)
    c: Diameter(g22) = 3.6
    c: Coincident(g22,g-9)
    c: Diameter(g23) = 3.6
    c: Coincident(g23,g-8)
    c: Diameter(g24) = 3.6
    c: Diameter(g25) = 3.6
    c: Diameter(g26) = 3.6
    c: Diameter(g27) = 3.6
    c: Diameter(g28) = 3.6
    c: Coincident(g27,g-4)
    c: Coincident(g28,g-3)
    c: Coincident(g25,g-6)
    c: Coincident(g26,g-5)
    c: Coincident(g24,g-7)
    c: Parallel(g20,g-21)
    c: Equal(g20,g-21)
    c: Parallel(g21,g-19)
    c: Equal(g21,g-19)
    c: Distance(g29) = 0.2
    c: Distance(g30) = 0.2
    c: Parallel(g29,g-20)
    c: Parallel(g31,g-20)
    c: Equal(g31,g-20)
    c: Coincident(g30,g31)
    c: Coincident(g31,g29)
    c: Coincident(g29,g-21)
    c: Parallel(g30,g31)
    c: Coincident(g17,g30)
    c: Coincident(g20,g29)
    c: Coincident(g21,g30)
    c: Perpendicular(g16,g17)
    c: Coincident(g32,g21)
    c: Coincident(g32,g20)
    c: Perpendicular(g10,g7)
    c: Diameter(g33) = 12.6
    c: Diameter(g34) = 12.6
    c: Diameter(g35) = 12.6
    c: Horizontal(g36)
    c: PointOnObject(g33,g36)
    c: PointOnObject(g34,g36)
    c: DistanceX(g34,g33) = 23
    c: DistanceX(g35,g34) = 23
    c: DistanceX(g33,g36) = 15
    c: Symmetric(g-24,g-24,g36)
    c: Coincident(g36,g35)
FEATURE [Sketcher::SketchObject] Sketch075  label="lato dx pistola"
  ArcFitTolerance = 1e-06
  AttachmentSupport = -> [XZ_Plane]
  ExternalGeometry = -> [Sketch016,Sketch,Sketch058,Sketch074]
  FullyConstrained = true
  MakeInternals = false
  MapMode = 5
  Placement = pos=(0,0,0) rot=(1,0,0;1.5708rad)
  sketch-geometry (61):
    g0: LineSegment StartX=-82.8 StartY=3.2 StartZ=0 EndX=0 EndY=3.2 EndZ=0
    g1: LineSegment StartX=-82.8 StartY=3.2 StartZ=0 EndX=-82.8 EndY=6.2 EndZ=0
    g2: LineSegment [constr] StartX=-107.6 StartY=18 StartZ=0 EndX=-107.6 EndY=20 EndZ=0
    g3: LineSegment [constr] StartX=-132.428 StartY=18 StartZ=0 EndX=-132.428 EndY=20 EndZ=0
    g4: LineSegment StartX=-132.428 StartY=20 StartZ=0 EndX=-107.6 EndY=20 EndZ=0
    g5: ArcOfCircle CenterX=-107.6 CenterY=4 CenterZ=0 NormalX=0 NormalY=0 NormalZ=1 AngleXU=0 Radius=16 StartAngle=0.137937 EndAngle=1.5708
    g6: LineSegment StartX=-82.8 StartY=6.2 StartZ=0 EndX=-91.752 EndY=6.2 EndZ=0
    g7: LineSegment [constr] StartX=-145.743 StartY=8.32624 StartZ=0 EndX=-147.645 EndY=8.94427 EndZ=0
    g8: ArcOfCircle CenterX=-132.428 CenterY=4 CenterZ=0 NormalX=0 NormalY=0 NormalZ=1 AngleXU=0 Radius=16 StartAngle=1.5708 EndAngle=2.82743
    g9: LineSegment StartX=-215.932 StartY=-80.4316 StartZ=0 EndX=-176.685 EndY=-80.4316 EndZ=0
    g10: LineSegment StartX=-147.645 StartY=8.94427 StartZ=0 EndX=-176.685 EndY=-80.4316 EndZ=0
    g11: LineSegment [constr] StartX=-193.988 StartY=-2.33927 StartZ=0 EndX=-192.176 EndY=-3.18451 EndZ=0
    g12: LineSegment [constr] StartX=-217.232 StartY=-52.1862 StartZ=0 EndX=-215.42 EndY=-53.0314 EndZ=0
    g13: LineSegment StartX=-192.176 StartY=-3.18451 StartZ=0 EndX=-215.42 EndY=-53.0314 EndZ=0
    g14: ArcOfCircle CenterX=-184.801 CenterY=-67.3089 CenterZ=0 NormalX=0 NormalY=0 NormalZ=1 AngleXU=0 Radius=33.7833 StartAngle=2.70526 EndAngle=3.54053
    g15: ArcOfCircle CenterX=-207.583 CenterY=4 CenterZ=0 NormalX=0 NormalY=0 NormalZ=1 AngleXU=0 Radius=17 StartAngle=5.84685 EndAngle=7.56663
    g16: LineSegment StartX=-202.765 StartY=20.303 StartZ=0 EndX=-195.887 EndY=39.2 EndZ=0
    g17: LineSegment [constr] StartX=-193.885 StartY=33.0037 StartZ=0 EndX=-197.644 EndY=34.3718 EndZ=0
    g18: LineSegment StartX=-195.887 StartY=39.2 StartZ=0 EndX=0 EndY=39.2 EndZ=0
    g19: LineSegment StartX=0 StartY=3.2 StartZ=0 EndX=0 EndY=39.2 EndZ=0
    g20: LineSegment StartX=-189.939 StartY=31.5672 StartZ=0 EndX=-192.333 EndY=24.9893 EndZ=0
    g21: LineSegment StartX=-196.467 StartY=26.4942 StartZ=0 EndX=-194.073 EndY=33.0721 EndZ=0
    g22: Circle CenterX=-213.443 CenterY=-76.8316 CenterZ=0 NormalX=0 NormalY=0 NormalZ=1 AngleXU=0 Radius=1.8
    g23: Circle CenterX=-179.305 CenterY=-76.8316 CenterZ=0 NormalX=0 NormalY=0 NormalZ=1 AngleXU=0 Radius=1.8
    g24: Circle CenterX=-184.08 CenterY=34.8 CenterZ=0 NormalX=0 NormalY=0 NormalZ=1 AngleXU=0 Radius=1.8
    g25: Circle CenterX=-78.51 CenterY=34.8 CenterZ=0 NormalX=0 NormalY=0 NormalZ=1 AngleXU=0 Radius=1.8
    g26: Circle CenterX=-78.51 CenterY=7.6 CenterZ=0 NormalX=0 NormalY=0 NormalZ=1 AngleXU=0 Radius=1.8
    g27: Circle CenterX=-5.6 CenterY=34.8 CenterZ=0 NormalX=0 NormalY=0 NormalZ=1 AngleXU=0 Radius=1.8
    g28: Circle CenterX=-5.6 CenterY=7.6 CenterZ=0 NormalX=0 NormalY=0 NormalZ=1 AngleXU=0 Radius=1.8
    g29: LineSegment StartX=-190.127 StartY=31.6356 StartZ=0 EndX=-189.939 EndY=31.5672 EndZ=0
    g30: LineSegment StartX=-194.073 StartY=33.0721 StartZ=0 EndX=-193.885 EndY=33.0037 EndZ=0
    g31: LineSegment StartX=-193.885 StartY=33.0037 StartZ=0 EndX=-190.127 EndY=31.6356 EndZ=0
    g32: LineSegment StartX=-196.467 StartY=26.4942 StartZ=0 EndX=-192.333 EndY=24.9893 EndZ=0
    g33: LineSegment [constr] StartX=-4 StartY=21.2 StartZ=0 EndX=-87.91 EndY=21.2 EndZ=0
    g34: GeomPoint [constr] X=-4 Y=21.2 Z=0
    g35: LineSegment [constr] StartX=-15.2 StartY=33.7 StartZ=0 EndX=-15.2 EndY=8.7 EndZ=0
    g36: LineSegment [constr] StartX=-15.2 StartY=33.7 StartZ=0 EndX=-56.2 EndY=33.7 EndZ=0
    g37: LineSegment [constr] StartX=-15.2 StartY=8.7 StartZ=0 EndX=-56.2 EndY=8.7 EndZ=0
    g38: LineSegment [constr] StartX=-56.2 StartY=33.7 StartZ=0 EndX=-56.2 EndY=8.7 EndZ=0
    g39: Circle CenterX=-18.6 CenterY=30.3 CenterZ=0 NormalX=0 NormalY=0 NormalZ=1 AngleXU=0 Radius=3.4
    g40: Circle CenterX=-18.6 CenterY=12.1 CenterZ=0 NormalX=0 NormalY=0 NormalZ=1 AngleXU=0 Radius=3.4
    g41: Circle CenterX=-43.2 CenterY=30.3 CenterZ=0 NormalX=0 NormalY=0 NormalZ=1 AngleXU=0 Radius=3.4
    g42: Circle CenterX=-43.2 CenterY=12.1 CenterZ=0 NormalX=0 NormalY=0 NormalZ=1 AngleXU=0 Radius=3.4
    g43: LineSegment [constr] StartX=-4 StartY=21.2 StartZ=0 EndX=-15.2 EndY=21.2 EndZ=0
    g44: LineSegment [constr] StartX=-15.2 StartY=21.2 StartZ=0 EndX=-36.2 EndY=21.2 EndZ=0
    g45: LineSegment [constr] StartX=-41.5 StartY=16.2 StartZ=0 EndX=-30.9 EndY=16.2 EndZ=0
    g46: LineSegment [constr] StartX=-30.9 StartY=16.2 StartZ=0 EndX=-30.9 EndY=26.2 EndZ=0
    g47: LineSegment [constr] StartX=-30.9 StartY=26.2 StartZ=0 EndX=-41.5 EndY=26.2 EndZ=0
    g48: LineSegment [constr] StartX=-41.5 StartY=26.2 StartZ=0 EndX=-41.5 EndY=16.2 EndZ=0
    g49: GeomPoint [constr] X=-36.2 Y=21.2 Z=0
    g50: Circle CenterX=-36.2 CenterY=21.2 CenterZ=0 NormalX=0 NormalY=0 NormalZ=1 AngleXU=0 Radius=2.8
    g51: LineSegment [constr] StartX=-24.2 StartY=26.7 StartZ=0 EndX=-24.2 EndY=15.7 EndZ=0
    g52: Circle CenterX=-24.2 CenterY=26.7 CenterZ=0 NormalX=0 NormalY=0 NormalZ=1 AngleXU=0 Radius=3
    g53: Circle CenterX=-24.2 CenterY=15.7 CenterZ=0 NormalX=0 NormalY=0 NormalZ=1 AngleXU=0 Radius=3
    g54: GeomPoint X=-18.6 Y=30.3 Z=0
    g55: GeomPoint X=-18.6 Y=12.1 Z=0
    g56: GeomPoint X=-43.2 Y=12.1 Z=0
    g57: GeomPoint X=-43.2 Y=30.3 Z=0
    g58: Circle CenterX=-65 CenterY=21.2 CenterZ=0 NormalX=0 NormalY=0 NormalZ=1 AngleXU=0 Radius=1.5
    g59: Circle CenterX=-42 CenterY=21.2 CenterZ=0 NormalX=0 NormalY=0 NormalZ=1 AngleXU=0 Radius=1.5
    g60: Circle CenterX=-19 CenterY=21.2 CenterZ=0 NormalX=0 NormalY=0 NormalZ=1 AngleXU=0 Radius=1.5
  constraints (149):
    c: Coincident(g0,g-41)
    c: Horizontal(g0)
    c: PointOnObject(g0,g-39)
    c: Coincident(g1,g0)
    c: Vertical(g1)
    c: DistanceY(g1,g1) = 3
    c: Coincident(g2,g-17)
    c: Vertical(g2)
    c: Coincident(g3,g-16)
    c: Vertical(g3)
    c: DistanceY(g2,g2) = 2
    c: DistanceY(g3,g3) = 2
    c: Coincident(g4,g3)
    c: Coincident(g4,g2)
    c: Coincident(g5,g-17)
    c: Coincident(g5,g2)
    c: Coincident(g6,g1)
    c: Horizontal(g6)
    c: Coincident(g6,g5)
    c: Coincident(g7,g-15)
    c: Coincident(g8,g7)
    c: Coincident(g8,g3)
    c: Coincident(g8,g-15)
    c: Horizontal(g9)
    c: DistanceY(g-13,g9) = 2
    c: Coincident(g10,g7)
    c: Parallel(g10,g-14)
    c: Coincident(g9,g10)
    c: Distance(g11) = 2
    c: Coincident(g11,g-11)
    c: Perpendicular(g-11,g11)
    c: Distance(g12) = 2
    c: Coincident(g12,g-12)
    c: Perpendicular(g-11,g12)
    c: Coincident(g13,g11)
    c: Coincident(g13,g12)
    c: Coincident(g14,g-32)
    c: Coincident(g14,g12)
    c: Coincident(g14,g9)
    c: Coincident(g15,g-10)
    c: Coincident(g15,g11)
    c: Parallel(g16,g-22)
    c: Distance(g17) = 4
    c: PointOnObject(g17,g16)
    c: Coincident(g15,g16)
    c: Horizontal(g18)
    c: Coincident(g18,g16)
    c: Coincident(g19,g0)
    c: PointOnObject(g19,g-39)
    c: DistanceY(g19,g-36) = 2
    c: Coincident(g18,g19)
    c: Diameter(g22) = 3.6
    c: Coincident(g22,g-9)
    c: Diameter(g23) = 3.6
    c: Coincident(g23,g-8)
    c: Diameter(g24) = 3.6
    c: Diameter(g25) = 3.6
    c: Diameter(g26) = 3.6
    c: Diameter(g27) = 3.6
    c: Diameter(g28) = 3.6
    c: Coincident(g27,g-4)
    c: Coincident(g28,g-3)
    c: Coincident(g25,g-6)
    c: Coincident(g26,g-5)
    c: Coincident(g24,g-7)
    c: Parallel(g20,g-21)
    c: Equal(g20,g-21)
    c: Parallel(g21,g-19)
    c: Equal(g21,g-19)
    c: Distance(g29) = 0.2
    c: Distance(g30) = 0.2
    c: Parallel(g29,g-20)
    c: Parallel(g31,g-20)
    c: Equal(g31,g-20)
    c: Coincident(g30,g31)
    c: Coincident(g31,g29)
    c: Coincident(g29,g-21)
    c: Parallel(g30,g31)
    c: Coincident(g17,g30)
    c: Coincident(g20,g29)
    c: Coincident(g21,g30)
    c: Perpendicular(g16,g17)
    c: Coincident(g32,g21)
    c: Coincident(g32,g20)
    c: Perpendicular(g10,g7)
    c: Horizontal(g33)
    c: Symmetric(g-24,g-24,g33)
    c: PointOnObject(g33,g-28)
    c: Symmetric(g-24,g-24,g34)
    c: DistanceY(g35,g35) = 25
    c: Symmetric(g35,g35,g33)
    c: Distance(g36) = 41
    c: Coincident(g36,g35)
    c: Horizontal(g36)
    c: Coincident(g37,g35)
    c: Horizontal(g37)
    c: Coincident(g38,g36)
    c: Vertical(g38)
    c: Coincident(g37,g38)
    c: Diameter(g39) = 6.8
    c: Diameter(g40) = 6.8
    c: Tangent(g39,g36)
    c: Tangent(g40,g37)
    c: Tangent(g39,g35)
    c: Tangent(g40,g35)
    c: Diameter(g41) = 6.8
    c: Diameter(g42) = 6.8
    c: Tangent(g41,g36)
    c: Tangent(g42,g37)
    c: DistanceX(g41,g39) = 24.6
    c: DistanceX(g42,g40) = 24.6
    c: Distance(g43) = 11.2
    c: Coincident(g43,g33)
    c: PointOnObject(g43,g33)
    c: PointOnObject(g43,g35)
    c: Distance(g44) = 21
    c: Coincident(g44,g43)
    c: PointOnObject(g44,g33)
    c: Coincident(g45,g46)
    c: Coincident(g46,g47)
    c: Coincident(g47,g48)
    c: Coincident(g48,g45)
    c: Horizontal(g45)
    c: Horizontal(g47)
    c: Vertical(g46)
    c: Vertical(g48)
    c: Symmetric(g47,g45,g49)
    c: Distance(g46,g48) = 10.6
    c: Distance(g45,g47) = 10
    c: Coincident(g49,g44)
    c: Diameter(g50) = 5.6
    c: Coincident(g50,g44)
    c: Distance(g51) = 11
    c: Symmetric(g51,g51,g33)
    c: DistanceX(g51,g43) = 9
    c: Diameter(g52) = 6
    c: Coincident(g52,g51)
    c: Diameter(g53) = 6
    c: Coincident(g53,g51)
    c: Coincident(g40,g55)
    c: Coincident(g39,g54)
    c: Coincident(g41,g57)
    c: Coincident(g42,g56)
    c: Diameter(g58) = 3
    c: Diameter(g59) = 3
    c: Diameter(g60) = 3
    c: Coincident(g58,g-44)
    c: Coincident(g59,g-46)
    c: Coincident(g60,g-45)
FEATURE [Sketcher::SketchObject] Sketch078
  ArcFitTolerance = 1e-06
  AttachmentSupport = -> [XZ_Plane005]
  FullyConstrained = true
  MakeInternals = false
  MapMode = 5
  Placement = pos=(0,0,0) rot=(1,0,0;1.5708rad)
  sketch-geometry (5):
    g0: LineSegment [constr] StartX=0 StartY=5.5 StartZ=0 EndX=0 EndY=-5.5 EndZ=0
    g1: ArcOfCircle CenterX=0 CenterY=5.5 CenterZ=0 NormalX=0 NormalY=0 NormalZ=1 AngleXU=0 Radius=2.7 StartAngle=0 EndAngle=3.14159
    g2: ArcOfCircle CenterX=0 CenterY=-5.5 CenterZ=0 NormalX=0 NormalY=0 NormalZ=1 AngleXU=0 Radius=2.7 StartAngle=3.1416 EndAngle=6.28318
    g3: LineSegment StartX=-2.7 StartY=5.5 StartZ=0 EndX=-2.7 EndY=-5.50001 EndZ=0
    g4: LineSegment StartX=2.7 StartY=5.5 StartZ=0 EndX=2.7 EndY=-5.50001 EndZ=0
  constraints (13):
    c: Distance(g0) = 11
    c: Vertical(g0)
    c: Symmetric(g0,g0,g-1)
    c: Radius(g1) = 2.7
    c: Coincident(g1,g0)
    c: Radius(g2) = 2.7
    c: Coincident(g2,g0)
    c: Vertical(g3)
    c: Vertical(g4)
    c: Coincident(g2,g4)
    c: Coincident(g2,g3)
    c: Tangent(g3,g1) = -1.5708
    c: Tangent(g4,g1) = 1.5708
FEATURE [PartDesign::Pad] Pad002
  Direction = (0,-1,2e-16)
  Length = 0.8
  Length2 = 10
  Placement = pos=(0,0,0) rot=(1,0,0;1.5708rad)
  Profile = -> Sketch078
  ReferenceAxis = -> Sketch078 [N_Axis]
  Refine = true
  Suppressed = false
  Type = 0
FEATURE [Sketcher::SketchObject] Sketch079
  ArcFitTolerance = 1e-06
  AttachmentSupport = -> [XZ_Plane005]
  ExternalGeometry = -> [Sketch078]
  FullyConstrained = true
  MakeInternals = false
  MapMode = 5
  Placement = pos=(0,0,0) rot=(1,0,0;1.5708rad)
  sketch-geometry (2):
    g0: Circle CenterX=-1e-16 CenterY=5.5 CenterZ=0 NormalX=0 NormalY=0 NormalZ=1 AngleXU=0 Radius=2.7
    g1: Circle CenterX=0 CenterY=-5.5 CenterZ=0 NormalX=0 NormalY=0 NormalZ=1 AngleXU=0 Radius=2.7
  constraints (4):
    c: Coincident(g0,g-3)
    c: PointOnObject(g-3,g0)
    c: Coincident(g1,g-4)
    c: Equal(g1,g-4)
FEATURE [PartDesign::Pad] Pad003
  BaseFeature = -> Pad002
  Direction = (0,-1,2e-16)
  Length = 5
  Length2 = 10
  Placement = pos=(0,0,0) rot=(1,0,0;1.5708rad)
  Profile = -> Sketch079
  ReferenceAxis = -> Sketch079 [N_Axis]
  Refine = true
  Suppressed = false
  Type = 0
FEATURE [PartDesign::Fillet] Fillet001
  Base = -> Pad003 [Edge16,Edge14]
  BaseFeature = -> Pad003
  Placement = pos=(0,0,0) rot=(1,0,0;1.5708rad)
  Radius = 0.4
  Refine = true
  SupportTransform = false
  Suppressed = false
  UseAllEdges = false
FEATURE [PartDesign::Body] Body005  label="pulsanti lato destro"
  AllowCompound = false
  Group = -> [Sketch078,Pad002,Sketch079,Pad003,Fillet001]
  Origin = -> Origin005
  Tip = -> Fillet001
FEATURE [PartDesign::SubShapeBinder] Binder
  BindCopyOnChange = 0
  BindMode = 0
  ClaimChildren = false
  Context = -> Body006 [Binder.]
  Fuse = false
  MakeFace = true
  OffsetFill = false
  OffsetIntersection = false
  OffsetJoinType = 0
  OffsetOpenResult = false
  PartialLoad = false
  Refine = true
  Relative = true
  Support = -> [Body[Sketch074.]]
  _Version = 2
FEATURE [PartDesign::SubShapeBinder] Binder001
  BindCopyOnChange = 0
  BindMode = 0
  ClaimChildren = false
  Context = -> Body007 [Binder001.]
  Fuse = false
  MakeFace = true
  OffsetFill = false
  OffsetIntersection = false
  OffsetJoinType = 0
  OffsetOpenResult = false
  PartialLoad = false
  Refine = true
  Relative = true
  Support = -> [Body[Sketch075.]]
  _Version = 2
FEATURE [Mesh::Feature] logo_per_PCB_definitivo_positivo
  Placement = pos=(-191,17,-66) rot=(0,1,1;0rad)
FEATURE [Sketcher::SketchObject] Sketch114  label="Sketch114 - base lato DX"
  ArcFitTolerance = 1e-06
  AttachmentSupport = -> [Binder001]
  ExternalGeometry = -> [Binder001]
  FullyConstrained = true
  MakeInternals = false
  MapMode = 5
  Placement = pos=(0,1e-15,0) rot=(0,0.707107,0.707107;3.14159rad)
  sketch-geometry (30):
    g0: Circle CenterX=5.6 CenterY=34.8 CenterZ=0 NormalX=0 NormalY=0 NormalZ=1 AngleXU=0 Radius=1.8
    g1: Circle CenterX=5.6 CenterY=7.6 CenterZ=0 NormalX=0 NormalY=0 NormalZ=1 AngleXU=0 Radius=1.8
    g2: Circle CenterX=24.2 CenterY=26.7 CenterZ=0 NormalX=0 NormalY=0 NormalZ=1 AngleXU=0 Radius=3
    g3: Circle CenterX=24.2 CenterY=15.7 CenterZ=0 NormalX=0 NormalY=0 NormalZ=1 AngleXU=0 Radius=3
    g4: Circle CenterX=36.2 CenterY=21.2 CenterZ=0 NormalX=0 NormalY=0 NormalZ=1 AngleXU=0 Radius=2.8
    g5: Circle CenterX=78.51 CenterY=34.8 CenterZ=0 NormalX=0 NormalY=0 NormalZ=1 AngleXU=0 Radius=1.8
    g6: Circle CenterX=78.51 CenterY=7.6 CenterZ=0 NormalX=0 NormalY=0 NormalZ=1 AngleXU=0 Radius=1.8
    g7: Circle CenterX=184.08 CenterY=34.8 CenterZ=0 NormalX=0 NormalY=0 NormalZ=1 AngleXU=0 Radius=1.8
    g8: Circle CenterX=213.443 CenterY=-76.8316 CenterZ=0 NormalX=0 NormalY=0 NormalZ=1 AngleXU=0 Radius=1.8
    g9: Circle CenterX=179.305 CenterY=-76.8316 CenterZ=0 NormalX=0 NormalY=0 NormalZ=1 AngleXU=0 Radius=1.8
    g10: ArcOfCircle [constr] CenterX=132.428 CenterY=4 CenterZ=0 NormalX=0 NormalY=0 NormalZ=1 AngleXU=0 Radius=16 StartAngle=0.314159 EndAngle=1.5708
    g11: ArcOfCircle CenterX=107.6 CenterY=4 CenterZ=0 NormalX=0 NormalY=0 NormalZ=1 AngleXU=0 Radius=16 StartAngle=1.5708 EndAngle=3.00366
    g12: ArcOfCircle CenterX=207.583 CenterY=4 CenterZ=0 NormalX=0 NormalY=0 NormalZ=1 AngleXU=0 Radius=17 StartAngle=1.85815 EndAngle=3.57792
    g13: ArcOfCircle CenterX=184.801 CenterY=-67.3089 CenterZ=0 NormalX=0 NormalY=0 NormalZ=1 AngleXU=0 Radius=33.7833 StartAngle=5.88425 EndAngle=6.71952
    g14: LineSegment StartX=0 StartY=39.2 StartZ=0 EndX=0 EndY=3.2 EndZ=0
    g15: LineSegment StartX=0 StartY=3.2 StartZ=0 EndX=82.8 EndY=3.2 EndZ=0
    g16: LineSegment StartX=82.8 StartY=3.2 StartZ=0 EndX=82.8 EndY=6.2 EndZ=0
    g17: LineSegment StartX=82.8 StartY=6.2 StartZ=0 EndX=91.752 EndY=6.2 EndZ=0
    g18: LineSegment StartX=107.6 StartY=20 StartZ=0 EndX=132.428 EndY=20 EndZ=0
    g19: LineSegment StartX=147.645 StartY=8.94427 StartZ=0 EndX=176.685 EndY=-80.4316 EndZ=0
    g20: LineSegment StartX=176.685 StartY=-80.4316 StartZ=0 EndX=215.932 EndY=-80.4316 EndZ=0
    g21: LineSegment StartX=215.42 StartY=-53.0314 StartZ=0 EndX=192.176 EndY=-3.18451 EndZ=0
    g22: LineSegment StartX=202.765 StartY=20.303 StartZ=0 EndX=195.887 EndY=39.2 EndZ=0
    g23: LineSegment StartX=195.887 StartY=39.2 StartZ=0 EndX=0 EndY=39.2 EndZ=0
    g24: LineSegment StartX=196.467 StartY=26.4942 StartZ=0 EndX=194.073 EndY=33.0721 EndZ=0
    g25: LineSegment StartX=194.073 StartY=33.0721 StartZ=0 EndX=189.939 EndY=31.5672 EndZ=0
    g26: LineSegment StartX=189.939 StartY=31.5672 StartZ=0 EndX=192.333 EndY=24.9893 EndZ=0
    g27: LineSegment StartX=192.333 StartY=24.9893 StartZ=0 EndX=196.467 EndY=26.4942 EndZ=0
    g28: LineSegment StartX=132.428 StartY=20 StartZ=0 EndX=144.053 EndY=20 EndZ=0
    g29: LineSegment StartX=144.053 StartY=20 StartZ=0 EndX=147.645 EndY=8.94427 EndZ=0
  constraints (65):
    c: Equal(g0,g-25)
    c: Equal(g2,g-29)
    c: Equal(g3,g-30)
    c: Equal(g4,g-28)
    c: Equal(g1,g-26)
    c: Coincident(g0,g-25)
    c: Coincident(g1,g-26)
    c: Coincident(g2,g-29)
    c: Coincident(g3,g-30)
    c: Coincident(g4,g-28)
    c: Equal(g5,g-23)
    c: Equal(g6,g-24)
    c: Coincident(g5,g-23)
    c: Coincident(g6,g-24)
    c: Equal(g7,g-20)
    c: Coincident(g7,g-20)
    c: Equal(g9,g-22)
    c: Coincident(g9,g-22)
    c: Equal(g8,g-21)
    c: Coincident(g8,g-21)
    c: Equal(g13,g-12)
    c: Equal(g12,g-14)
    c: Equal(g10,g-9)
    c: Equal(g11,g-7)
    c: Coincident(g14,g-27)
    c: Coincident(g14,g-27)
    c: Coincident(g15,g14)
    c: Coincident(g15,g-5)
    c: Coincident(g16,g15)
    c: Coincident(g16,g-6)
    c: Coincident(g17,g16)
    c: Coincident(g17,g-7)
    c: Coincident(g11,g17)
    c: Coincident(g11,g-8)
    c: Coincident(g18,g11)
    c: Coincident(g18,g-9)
    c: Coincident(g10,g18)
    c: Coincident(g10,g-10)
    c: Coincident(g19,g10)
    c: Coincident(g19,g-11)
    c: Coincident(g20,g19)
    c: Coincident(g20,g-12)
    c: Coincident(g13,g20)
    c: Coincident(g13,g-13)
    c: Coincident(g21,g13)
    c: Coincident(g21,g-14)
    c: Coincident(g12,g21)
    c: Coincident(g12,g-15)
    c: Coincident(g22,g12)
    c: Coincident(g22,g-15)
    c: Coincident(g23,g22)
    c: Coincident(g23,g14)
    c: Coincident(g24,g-18)
    c: Coincident(g24,g-16)
    c: Coincident(g25,g24)
    c: Coincident(g25,g-19)
    c: Coincident(g26,g25)
    c: Coincident(g26,g-19)
    c: Coincident(g27,g26)
    c: Coincident(g27,g24)
    c: Coincident(g29,g10)
    c: Coincident(g28,g10)
    c: Coincident(g29,g28)
    c: Parallel(g28,g18)
    c: Parallel(g29,g19)
FEATURE [PartDesign::Pad] Pad011
  Direction = (0,1,-2e-16)
  Length = 2
  Length2 = 10
  Profile = -> Sketch114
  ReferenceAxis = -> Sketch114 [N_Axis]
  Refine = true
  Reversed = true
  Suppressed = false
  Type = 0
FEATURE [Sketcher::SketchObject] Sketch115
  ArcFitTolerance = 1e-06
  AttachmentSupport = -> [Pad011]
  ExternalGeometry = -> [Binder001]
  FullyConstrained = true
  MakeInternals = false
  MapMode = 5
  Placement = pos=(0,1.7e-15,0) rot=(0,0.707107,0.707107;3.14159rad)
  sketch-geometry (4):
    g0: ArcOfCircle CenterX=24.2 CenterY=26.7 CenterZ=0 NormalX=0 NormalY=0 NormalZ=1 AngleXU=0 Radius=3 StartAngle=4.48384e-08 EndAngle=3.14159
    g1: ArcOfCircle CenterX=24.2 CenterY=15.7 CenterZ=0 NormalX=0 NormalY=0 NormalZ=1 AngleXU=0 Radius=3 StartAngle=3.14159 EndAngle=6.28318
    g2: LineSegment StartX=21.2 StartY=26.7 StartZ=0 EndX=21.2 EndY=15.7 EndZ=0
    g3: LineSegment StartX=27.2 StartY=26.7 StartZ=0 EndX=27.2 EndY=15.7 EndZ=0
  constraints (12):
    c: Equal(g1,g-4)
    c: Equal(g0,g-3)
    c: Coincident(g0,g-3)
    c: Coincident(g1,g-4)
    c: Vertical(g2)
    c: Vertical(g3)
    c: Tangent(g3,g-3)
    c: Tangent(g2,g-3)
    c: Coincident(g0,g2)
    c: Coincident(g0,g3)
    c: Coincident(g1,g2)
    c: Coincident(g3,g1)
FEATURE [Sketcher::SketchObject] Sketch117  label="Sketch117 - fori per inserto M3 x 3 x 4.5"
  ArcFitTolerance = 1e-06
  AttachmentSupport = -> [Pad011]
  ExternalGeometry = -> [Binder001]
  FullyConstrained = true
  MakeInternals = false
  MapMode = 5
  Placement = pos=(0,1.7e-15,0) rot=(0,0.707107,0.707107;3.14159rad)
  sketch-geometry (4):
    g0: Circle CenterX=43.2 CenterY=30.3 CenterZ=0 NormalX=0 NormalY=0 NormalZ=1 AngleXU=0 Radius=2.25
    g1: Circle CenterX=43.2 CenterY=12.1 CenterZ=0 NormalX=0 NormalY=0 NormalZ=1 AngleXU=0 Radius=2.25
    g2: Circle CenterX=18.6 CenterY=30.3 CenterZ=0 NormalX=0 NormalY=0 NormalZ=1 AngleXU=0 Radius=2.25
    g3: Circle CenterX=18.6 CenterY=12.1 CenterZ=0 NormalX=0 NormalY=0 NormalZ=1 AngleXU=0 Radius=2.25
  constraints (8):
    c: Diameter(g0) = 4.5
    c: Diameter(g1) = 4.5
    c: Diameter(g2) = 4.5
    c: Diameter(g3) = 4.5
    c: Coincident(g2,g-3)
    c: Coincident(g3,g-6)
    c: Coincident(g0,g-4)
    c: Coincident(g1,g-5)
FEATURE [Sketcher::SketchObject] Sketch118
  ArcFitTolerance = 1e-06
  AttachmentSupport = -> [Pad011]
  ExternalGeometry = -> [Binder001]
  FullyConstrained = true
  MakeInternals = false
  MapMode = 5
  Placement = pos=(0,-2,0) rot=(1,0,0;1.5708rad)
  sketch-geometry (12):
    g0: Circle CenterX=-78.51 CenterY=34.8 CenterZ=0 NormalX=0 NormalY=0 NormalZ=1 AngleXU=0 Radius=1.8
    g1: Circle CenterX=-78.51 CenterY=7.6 CenterZ=0 NormalX=0 NormalY=0 NormalZ=1 AngleXU=0 Radius=1.8
    g2: Circle CenterX=-5.6 CenterY=34.8 CenterZ=0 NormalX=0 NormalY=0 NormalZ=1 AngleXU=0 Radius=1.8
    g3: Circle CenterX=-5.6 CenterY=7.6 CenterZ=0 NormalX=0 NormalY=0 NormalZ=1 AngleXU=0 Radius=1.8
    g4: LineSegment StartX=0 StartY=39.2 StartZ=0 EndX=0 EndY=3.2 EndZ=0
    g5: LineSegment StartX=0 StartY=3.2 StartZ=0 EndX=-82.8 EndY=3.2 EndZ=0
    g6: LineSegment StartX=-82.8 StartY=3.2 StartZ=0 EndX=-82.8 EndY=39.2 EndZ=0
    g7: LineSegment StartX=-82.8 StartY=39.2 StartZ=0 EndX=0 EndY=39.2 EndZ=0
    g8: ArcOfCircle CenterX=-65 CenterY=21.2 CenterZ=0 NormalX=0 NormalY=0 NormalZ=1 AngleXU=0 Radius=10 StartAngle=1.5708 EndAngle=4.71239
    g9: ArcOfCircle CenterX=-19 CenterY=21.2 CenterZ=0 NormalX=0 NormalY=0 NormalZ=1 AngleXU=0 Radius=10 StartAngle=4.71239 EndAngle=7.85398
    g10: LineSegment StartX=-65 StartY=31.2 StartZ=0 EndX=-19 EndY=31.2 EndZ=0
    g11: LineSegment StartX=-65 StartY=11.2 StartZ=0 EndX=-19 EndY=11.2 EndZ=0
  constraints (25):
    c: Equal(g2,g-5)
    c: Equal(g3,g-7)
    c: Equal(g1,g-6)
    c: Equal(g0,g-4)
    c: Coincident(g0,g-4)
    c: Coincident(g1,g-6)
    c: Coincident(g3,g-7)
    c: Coincident(g2,g-5)
    c: Coincident(g4,g-8)
    c: Coincident(g4,g-9)
    c: Coincident(g5,g4)
    c: Coincident(g5,g-10)
    c: Coincident(g6,g5)
    c: PointOnObject(g6,g-3)
    c: Vertical(g6)
    c: Coincident(g7,g6)
    c: Coincident(g7,g4)
    c: Tangent(g8,g10) = 1.5708
    c: Tangent(g8,g11) = -1.5708
    c: Tangent(g9,g10) = 1.5708
    c: Tangent(g9,g11) = -1.5708
    c: Equal(g8,g9)
    c: Radius(g8) = 10
    c: Coincident(g8,g-11)
    c: Coincident(g9,g-12)
FEATURE [Sketcher::SketchObject] Sketch120
  ArcFitTolerance = 1e-06
  AttachmentSupport = -> [Pad011]
  ExternalGeometry = -> [Binder001]
  FullyConstrained = true
  MakeInternals = false
  MapMode = 5
  Placement = pos=(0,-2,0) rot=(1,0,0;1.5708rad)
  sketch-geometry (4):
    g0: LineSegment StartX=-137.815 StartY=39.2 StartZ=0 EndX=-142.655 EndY=24.303 EndZ=0
    g1: LineSegment StartX=-137.815 StartY=39.2 StartZ=0 EndX=-110.815 EndY=39.2 EndZ=0
    g2: LineSegment StartX=-142.655 StartY=24.303 StartZ=0 EndX=-110.815 EndY=24.303 EndZ=0
    g3: ArcOfCircle CenterX=-92.2534 CenterY=31.7515 CenterZ=0 NormalX=0 NormalY=0 NormalZ=1 AngleXU=0 Radius=20 StartAngle=2.75997 EndAngle=3.52321
  constraints (12):
    c: PointOnObject(g0,g-3)
    c: Coincident(g1,g0)
    c: PointOnObject(g1,g-3)
    c: Coincident(g2,g0)
    c: Horizontal(g2)
    c: Tangent(g0,g-4)
    c: Vertical(g2,g1)
    c: DistanceX(g1,g1) = 27
    c: DistanceY(g-6,g0) = 4
    c: Radius(g3) = 20
    c: Coincident(g3,g1)
    c: Coincident(g3,g2)
FEATURE [Sketcher::SketchObject] Sketch121
  ArcFitTolerance = 1e-06
  AttachmentSupport = -> [Pad011]
  ExternalGeometry = -> [Binder001]
  FullyConstrained = true
  MakeInternals = false
  MapMode = 5
  Placement = pos=(0,-2,0) rot=(1,0,0;1.5708rad)
  sketch-geometry (15):
    g0: LineSegment StartX=-137.815 StartY=39.2 StartZ=0 EndX=-143.955 EndY=20.303 EndZ=0
    g1: LineSegment StartX=-143.955 StartY=20.303 StartZ=0 EndX=-190.141 EndY=20.303 EndZ=0
    g2: LineSegment StartX=-190.141 StartY=20.303 StartZ=0 EndX=-186.139 EndY=31.3 EndZ=0
    g3: LineSegment StartX=-178.754 StartY=39.2 StartZ=0 EndX=-180.791 EndY=33.6029 EndZ=0
    g4: ArcOfCircle CenterX=-184.08 CenterY=34.8 CenterZ=0 NormalX=0 NormalY=0 NormalZ=1 AngleXU=0 Radius=3.5 StartAngle=4.71239 EndAngle=5.93412
    g5: LineSegment StartX=-184.08 StartY=31.3 StartZ=0 EndX=-186.139 EndY=31.3 EndZ=0
    g6: LineSegment StartX=-137.815 StartY=39.2 StartZ=0 EndX=-156.815 EndY=39.2 EndZ=0
    g7: LineSegment StartX=-168.815 StartY=39.2 StartZ=0 EndX=-178.754 EndY=39.2 EndZ=0
    g8: LineSegment StartX=-157.815 StartY=39.2 StartZ=0 EndX=-167.815 EndY=39.2 EndZ=0
    g9: LineSegment StartX=-168.815 StartY=31.2 StartZ=0 EndX=-156.815 EndY=31.2 EndZ=0
    g10: LineSegment StartX=-167.436 StartY=36.2 StartZ=0 EndX=-157.436 EndY=36.2 EndZ=0
    g11: ArcOfCircle CenterX=-176.411 CenterY=35.2 CenterZ=0 NormalX=0 NormalY=0 NormalZ=1 AngleXU=0 Radius=20 StartAngle=6.08183 EndAngle=6.48454
    g12: ArcOfCircle CenterX=-188.411 CenterY=35.2 CenterZ=0 NormalX=0 NormalY=0 NormalZ=1 AngleXU=0 Radius=20 StartAngle=6.08183 EndAngle=6.48454
    g13: ArcOfCircle CenterX=-177.411 CenterY=35.2 CenterZ=0 NormalX=0 NormalY=0 NormalZ=1 AngleXU=0 Radius=20 StartAngle=0.0500209 EndAngle=0.201358
    g14: ArcOfCircle CenterX=-187.411 CenterY=35.2 CenterZ=0 NormalX=0 NormalY=0 NormalZ=1 AngleXU=0 Radius=20 StartAngle=0.0500209 EndAngle=0.201358
  constraints (46):
    c: PointOnObject(g0,g-3)
    c: Tangent(g0,g-5)
    c: Coincident(g1,g0)
    c: Horizontal(g1)
    c: Coincident(g2,g1)
    c: PointOnObject(g3,g-3)
    c: Parallel(g3,g-6)
    c: Parallel(g2,g-6)
    c: Radius(g4) = 3.5
    c: Coincident(g4,g-7)
    c: Tangent(g3,g4) = 1.5708
    c: Horizontal(g5)
    c: Tangent(g5,g4) = 1.5708
    c: DistanceX(g-8,g5) = 3.8
    c: Coincident(g2,g5)
    c: Coincident(g6,g0)
    c: PointOnObject(g6,g-3)
    c: DistanceX(g6,g6) = 19
    c: PointOnObject(g7,g-3)
    c: DistanceX(g7,g6) = 12
    c: Coincident(g7,g3)
    c: PointOnObject(g8,g-3)
    c: PointOnObject(g8,g-3)
    c: DistanceX(g8,g8) = 10
    c: DistanceX(g8,g6) = 1
    c: Horizontal(g9)
    c: Vertical(g7,g9)
    c: Vertical(g6,g9)
    c: DistanceY(g9,g7) = 8
    c: Horizontal(g10)
    c: Equal(g8,g10)
    c: DistanceY(g10,g8) = 3
    c: Radius(g11) = 20
    c: Coincident(g11,g6)
    c: Coincident(g11,g9)
    c: Radius(g12) = 20
    c: Coincident(g12,g7)
    c: Coincident(g12,g9)
    c: Equal(g13,g11)
    c: Coincident(g13,g8)
    c: Coincident(g13,g10)
    c: Horizontal(g13,g11)
    c: Equal(g14,g12)
    c: Coincident(g14,g8)
    c: Coincident(g14,g10)
    c: Horizontal(g1,g-6)
FEATURE [Sketcher::SketchObject] Sketch122
  ArcFitTolerance = 1e-06
  AttachmentSupport = -> [Pad011]
  ExternalGeometry = -> [Binder001]
  FullyConstrained = true
  MakeInternals = false
  MapMode = 5
  Placement = pos=(0,-2,0) rot=(1,0,0;1.5708rad)
  sketch-geometry (8):
    g0: ArcOfCircle CenterX=-184.801 CenterY=-67.3089 CenterZ=0 NormalX=0 NormalY=0 NormalZ=1 AngleXU=0 Radius=33.7833 StartAngle=2.70526 EndAngle=3.54053
    g1: LineSegment StartX=-176.685 StartY=-80.4316 StartZ=0 EndX=-215.932 EndY=-80.4316 EndZ=0
    g2: LineSegment StartX=-215.42 StartY=-53.0314 StartZ=0 EndX=-192.176 EndY=-3.18454 EndZ=0
    g3: ArcOfCircle CenterX=-207.583 CenterY=4 CenterZ=0 NormalX=0 NormalY=0 NormalZ=1 AngleXU=0 Radius=17 StartAngle=5.84685 EndAngle=7.56663
    g4: Circle CenterX=-213.443 CenterY=-76.8316 CenterZ=0 NormalX=0 NormalY=0 NormalZ=1 AngleXU=0 Radius=3
    g5: Circle CenterX=-179.305 CenterY=-76.8316 CenterZ=0 NormalX=0 NormalY=0 NormalZ=1 AngleXU=0 Radius=3
    g6: LineSegment StartX=-143.955 StartY=20.303 StartZ=0 EndX=-176.685 EndY=-80.4316 EndZ=0
    g7: LineSegment StartX=-202.765 StartY=20.303 StartZ=0 EndX=-143.955 EndY=20.303 EndZ=0
  constraints (18):
    c: Coincident(g0,g-7)
    c: Coincident(g0,g-8)
    c: Coincident(g1,g0)
    c: Tangent(g2,g-5)
    c: Coincident(g3,g-6)
    c: Coincident(g2,g3)
    c: Coincident(g0,g2)
    c: Diameter(g4) = 6
    c: Diameter(g5) = 6
    c: Coincident(g4,g-9)
    c: Coincident(g5,g-10)
    c: Horizontal(g1)
    c: Coincident(g6,g1)
    c: Tangent(g6,g-4)
    c: Coincident(g3,g-6)
    c: Coincident(g7,g3)
    c: Horizontal(g7)
    c: Coincident(g7,g6)
FEATURE [Sketcher::SketchObject] Sketch123
  ArcFitTolerance = 1e-06
  AttachmentSupport = -> [Pad011]
  ExternalGeometry = -> [Binder001]
  FullyConstrained = true
  MakeInternals = false
  MapMode = 5
  Placement = pos=(0,-2,0) rot=(1,0,0;1.5708rad)
  sketch-geometry (4):
    g0: LineSegment StartX=-108 StartY=36.8 StartZ=0 EndX=-90 EndY=36.8 EndZ=0
    g1: LineSegment StartX=-108 StartY=36.8 StartZ=0 EndX=-108 EndY=26.8 EndZ=0
    g2: LineSegment StartX=-108 StartY=26.8 StartZ=0 EndX=-90 EndY=26.8 EndZ=0
    g3: ArcOfCircle CenterX=-94 CenterY=31.8 CenterZ=0 NormalX=0 NormalY=0 NormalZ=1 AngleXU=0 Radius=6.40312 StartAngle=5.38713 EndAngle=7.17924
  constraints (13):
    c: Horizontal(g0)
    c: Coincident(g1,g0)
    c: Vertical(g1)
    c: Coincident(g2,g1)
    c: Horizontal(g2)
    c: DistanceX(g0,g0) = 18
    c: DistanceY(g1,g1) = 10
    c: Equal(g0,g2)
    c: DistanceX(g0,g-3) = 90
    c: DistanceY(g0,g-3) = 2.4
    c: Coincident(g3,g0)
    c: Coincident(g3,g2)
    c: DistanceX(g3,g0) = 4
FEATURE [PartDesign::Chamfer] Chamfer014
  Angle = 45
  Base = -> Pad011 [Edge80,Edge4,Edge7]
  BaseFeature = -> Pad011
  ChamferType = 0
  FlipDirection = false
  Refine = true
  Size = 1.9
  Size2 = 1
  SupportTransform = false
  Suppressed = false
  UseAllEdges = false
FEATURE [PartDesign::Pocket] Pocket006
  BaseFeature = -> Chamfer014
  Direction = (0,-1,2e-16)
  Length = 1.2
  Length2 = 5
  Profile = -> Sketch115
  ReferenceAxis = -> Sketch115 [N_Axis]
  Refine = true
  Suppressed = false
  Type = 0
FEATURE [Sketcher::SketchObject] Sketch116  label="Sketch116 - pieno per inserto M3 x 3 x 4,5"
  ArcFitTolerance = 1e-06
  AttachmentSupport = -> [Pocket006]
  ExternalGeometry = -> [Binder001]
  FullyConstrained = true
  MakeInternals = false
  MapMode = 5
  Placement = pos=(0,1.7e-15,0) rot=(0,0.707107,0.707107;3.14159rad)
  sketch-geometry (4):
    g0: Circle CenterX=43.2 CenterY=30.3 CenterZ=0 NormalX=0 NormalY=0 NormalZ=1 AngleXU=0 Radius=3.4
    g1: Circle CenterX=43.2 CenterY=12.1 CenterZ=0 NormalX=0 NormalY=0 NormalZ=1 AngleXU=0 Radius=3.4
    g2: Circle CenterX=18.6 CenterY=30.3 CenterZ=0 NormalX=0 NormalY=0 NormalZ=1 AngleXU=0 Radius=3.4
    g3: Circle CenterX=18.6 CenterY=12.1 CenterZ=0 NormalX=0 NormalY=0 NormalZ=1 AngleXU=0 Radius=3.4
  constraints (8):
    c: Diameter(g0) = 6.8
    c: Diameter(g1) = 6.8
    c: Diameter(g2) = 6.8
    c: Diameter(g3) = 6.8
    c: Coincident(g2,g-3)
    c: Coincident(g0,g-4)
    c: Coincident(g3,g-6)
    c: Coincident(g1,g-5)
FEATURE [PartDesign::Pad] Pad012
  BaseFeature = -> Pocket006
  Direction = (0,1,-2e-16)
  Length = 2.4
  Length2 = 10
  Profile = -> Sketch116
  ReferenceAxis = -> Sketch116 [N_Axis]
  Refine = true
  Suppressed = false
  Type = 0
FEATURE [PartDesign::Pocket] Pocket007
  BaseFeature = -> Pad012
  Direction = (0,-1,2e-16)
  Length = 0.6
  Length2 = 2.4
  Profile = -> Sketch117
  ReferenceAxis = -> Sketch117 [N_Axis]
  Refine = true
  Suppressed = false
  Type = 4
FEATURE [PartDesign::Pad] Pad013
  BaseFeature = -> Pocket007
  Direction = (0,-1,2e-16)
  Length = 1.6
  Length2 = 10
  Profile = -> Sketch118
  ReferenceAxis = -> Sketch118 [N_Axis]
  Refine = true
  Suppressed = false
  Type = 0
FEATURE [Sketcher::SketchObject] Sketch119
  ArcFitTolerance = 1e-06
  AttachmentSupport = -> [Pad013]
  ExternalGeometry = -> [Binder001]
  FullyConstrained = true
  MakeInternals = false
  MapMode = 5
  Placement = pos=(0,-3.6,0) rot=(1,0,0;1.5708rad)
  sketch-geometry (21):
    g0: LineSegment [constr] StartX=-82.8 StartY=3.2 StartZ=0 EndX=-82.8 EndY=39.2 EndZ=0
    g1: ArcOfCircle CenterX=-78.51 CenterY=34.8 CenterZ=0 NormalX=0 NormalY=0 NormalZ=1 AngleXU=0 Radius=3.5 StartAngle=4.71239 EndAngle=6.28319
    g2: ArcOfCircle CenterX=-78.51 CenterY=7.6 CenterZ=0 NormalX=0 NormalY=0 NormalZ=1 AngleXU=0 Radius=3.5 StartAngle=0 EndAngle=1.5708
    g3: ArcOfCircle CenterX=-5.6 CenterY=34.8 CenterZ=0 NormalX=0 NormalY=0 NormalZ=1 AngleXU=0 Radius=3.5 StartAngle=3.14159 EndAngle=4.71239
    g4: ArcOfCircle CenterX=-5.6 CenterY=7.6 CenterZ=0 NormalX=0 NormalY=0 NormalZ=1 AngleXU=0 Radius=3.5 StartAngle=1.5708 EndAngle=3.14159
    g5: LineSegment StartX=0 StartY=39.2 StartZ=0 EndX=0 EndY=31.3 EndZ=0
    g6: LineSegment StartX=0 StartY=39.2 StartZ=0 EndX=-9.1 EndY=39.2 EndZ=0
    g7: LineSegment StartX=0 StartY=3.2 StartZ=0 EndX=0 EndY=11.1 EndZ=0
    g8: LineSegment StartX=0 StartY=3.2 StartZ=0 EndX=-9.1 EndY=3.2 EndZ=0
    g9: LineSegment StartX=-82.8 StartY=3.2 StartZ=0 EndX=-75.01 EndY=3.2 EndZ=0
    g10: LineSegment StartX=-82.8 StartY=3.2 StartZ=0 EndX=-82.8 EndY=11.1 EndZ=0
    g11: LineSegment StartX=-82.8 StartY=39.2 StartZ=0 EndX=-82.8 EndY=31.3 EndZ=0
    g12: LineSegment StartX=-82.8 StartY=39.2 StartZ=0 EndX=-75.01 EndY=39.2 EndZ=0
    g13: LineSegment StartX=-82.8 StartY=31.3 StartZ=0 EndX=-78.51 EndY=31.3 EndZ=0
    g14: LineSegment StartX=-75.01 StartY=39.2 StartZ=0 EndX=-75.01 EndY=34.8 EndZ=0
    g15: LineSegment StartX=-82.8 StartY=11.1 StartZ=0 EndX=-78.51 EndY=11.1 EndZ=0
    g16: LineSegment StartX=-75.01 StartY=3.2 StartZ=0 EndX=-75.01 EndY=7.6 EndZ=0
    g17: LineSegment StartX=-9.1 StartY=39.2 StartZ=0 EndX=-9.1 EndY=34.8 EndZ=0
    g18: LineSegment StartX=0 StartY=31.3 StartZ=0 EndX=-5.6 EndY=31.3 EndZ=0
    g19: LineSegment StartX=0 StartY=11.1 StartZ=0 EndX=-5.6 EndY=11.1 EndZ=0
    g20: LineSegment StartX=-9.1 StartY=3.2 StartZ=0 EndX=-9.1 EndY=7.6 EndZ=0
  constraints (51):
    c: Coincident(g0,g-10)
    c: PointOnObject(g0,g-8)
    c: Vertical(g0)
    c: Coincident(g1,g-3)
    c: Coincident(g2,g-4)
    c: Coincident(g3,g-5)
    c: Coincident(g4,g-6)
    c: Radius(g4) = 3.5
    c: Radius(g3) = 3.5
    c: Radius(g1) = 3.5
    c: Radius(g2) = 3.5
    c: Coincident(g5,g-9)
    c: PointOnObject(g5,g-9)
    c: Coincident(g6,g5)
    c: PointOnObject(g6,g-8)
    c: Coincident(g7,g-9)
    c: PointOnObject(g7,g-9)
    c: Coincident(g8,g7)
    c: PointOnObject(g8,g-7)
    c: Coincident(g9,g0)
    c: PointOnObject(g9,g-7)
    c: Coincident(g10,g0)
    c: PointOnObject(g10,g0)
    c: Coincident(g11,g0)
    c: PointOnObject(g11,g0)
    c: Coincident(g12,g0)
    c: PointOnObject(g12,g-8)
    c: Coincident(g13,g11)
    c: Horizontal(g13)
    c: Coincident(g14,g12)
    c: Vertical(g14)
    c: Coincident(g15,g10)
    c: Horizontal(g15)
    c: Coincident(g16,g9)
    c: Vertical(g16)
    c: Coincident(g17,g6)
    c: Vertical(g17)
    c: Coincident(g18,g5)
    c: Horizontal(g18)
    c: Coincident(g19,g7)
    c: Horizontal(g19)
    c: Coincident(g20,g8)
    c: Vertical(g20)
    c: Tangent(g20,g4) = 1.5708
    c: Tangent(g4,g19) = -1.5708
    c: Tangent(g18,g3) = 1.5708
    c: Tangent(g3,g17) = -1.5708
    c: Tangent(g13,g1) = -1.5708
    c: Tangent(g1,g14) = 1.5708
    c: Tangent(g16,g2) = -1.5708
    c: Tangent(g2,g15) = 1.5708
FEATURE [PartDesign::Pocket] Pocket008
  BaseFeature = -> Pad013
  Direction = (0,1,-2e-16)
  Length = 1.6
  Length2 = 5
  Profile = -> Sketch119
  ReferenceAxis = -> Sketch119 [N_Axis]
  Refine = true
  Suppressed = false
  Type = 0
FEATURE [PartDesign::Pad] Pad017
  BaseFeature = -> Pocket008
  Direction = (0,-1,2e-16)
  Length = 1.6
  Length2 = 10
  Profile = -> Sketch123
  ReferenceAxis = -> Sketch123 [N_Axis]
  Refine = true
  Suppressed = false
  Type = 0
FEATURE [Sketcher::SketchObject] Sketch125
  ArcFitTolerance = 1e-06
  AttachmentSupport = -> [Pad017]
  ExternalGeometry = -> [Pad017]
  FullyConstrained = true
  MakeInternals = false
  MapMode = 5
  Placement = pos=(0,-3.6,8e-16) rot=(1,0,0;1.5708rad)
  sketch-geometry (20):
    g0: LineSegment StartX=-108 StartY=35.8 StartZ=0 EndX=-108 EndY=35 EndZ=0
    g1: LineSegment StartX=-108 StartY=35 StartZ=0 EndX=-97 EndY=35 EndZ=0
    g2: LineSegment StartX=-97 StartY=35 StartZ=0 EndX=-97 EndY=35.8 EndZ=0
    g3: LineSegment StartX=-97 StartY=35.8 StartZ=0 EndX=-108 EndY=35.8 EndZ=0
    g4: LineSegment StartX=-108 StartY=28.6 StartZ=0 EndX=-108 EndY=27.8 EndZ=0
    g5: LineSegment StartX=-108 StartY=27.8 StartZ=0 EndX=-97 EndY=27.8 EndZ=0
    g6: LineSegment StartX=-97 StartY=27.8 StartZ=0 EndX=-97 EndY=28.6 EndZ=0
    g7: LineSegment StartX=-97 StartY=28.6 StartZ=0 EndX=-108 EndY=28.6 EndZ=0
    g8: LineSegment StartX=-108 StartY=30.4 StartZ=0 EndX=-108 EndY=29.6 EndZ=0
    g9: LineSegment StartX=-108 StartY=29.6 StartZ=0 EndX=-97 EndY=29.6 EndZ=0
    g10: LineSegment StartX=-97 StartY=29.6 StartZ=0 EndX=-97 EndY=30.4 EndZ=0
    g11: LineSegment StartX=-97 StartY=30.4 StartZ=0 EndX=-108 EndY=30.4 EndZ=0
    g12: LineSegment StartX=-108 StartY=32.2 StartZ=0 EndX=-108 EndY=31.4 EndZ=0
    g13: LineSegment StartX=-108 StartY=31.4 StartZ=0 EndX=-97 EndY=31.4 EndZ=0
    g14: LineSegment StartX=-97 StartY=31.4 StartZ=0 EndX=-97 EndY=32.2 EndZ=0
    g15: LineSegment StartX=-97 StartY=32.2 StartZ=0 EndX=-108 EndY=32.2 EndZ=0
    g16: LineSegment StartX=-108 StartY=34 StartZ=0 EndX=-108 EndY=33.2 EndZ=0
    g17: LineSegment StartX=-108 StartY=33.2 StartZ=0 EndX=-97 EndY=33.2 EndZ=0
    g18: LineSegment StartX=-97 StartY=33.2 StartZ=0 EndX=-97 EndY=34 EndZ=0
    g19: LineSegment StartX=-97 StartY=34 StartZ=0 EndX=-108 EndY=34 EndZ=0
  constraints (55):
    c: Coincident(g1,g0)
    c: Horizontal(g1)
    c: Coincident(g2,g1)
    c: Vertical(g2)
    c: Coincident(g3,g2)
    c: Horizontal(g3)
    c: Coincident(g3,g0)
    c: DistanceX(g1,g1) = 11
    c: DistanceY(g2,g2) = 0.8
    c: Coincident(g5,g4)
    c: Horizontal(g5)
    c: Coincident(g6,g5)
    c: Vertical(g6)
    c: Coincident(g7,g6)
    c: Horizontal(g7)
    c: Coincident(g7,g4)
    c: Coincident(g9,g8)
    c: Horizontal(g9)
    c: Coincident(g10,g9)
    c: Vertical(g10)
    c: Coincident(g11,g10)
    c: Horizontal(g11)
    c: Coincident(g11,g8)
    c: Coincident(g13,g12)
    c: Horizontal(g13)
    c: Coincident(g14,g13)
    c: Vertical(g14)
    c: Coincident(g15,g14)
    c: Horizontal(g15)
    c: Coincident(g15,g12)
    c: Coincident(g17,g16)
    c: Horizontal(g17)
    c: Coincident(g18,g17)
    c: Vertical(g18)
    c: Coincident(g19,g18)
    c: Horizontal(g19)
    c: Coincident(g19,g16)
    c: Equal(g3,g19)
    c: Equal(g3,g15)
    c: Equal(g3,g11)
    c: Equal(g3,g7)
    c: Equal(g2,g18)
    c: Equal(g2,g14)
    c: Equal(g2,g10)
    c: Equal(g2,g6)
    c: DistanceY(g-4,g4) = 1
    c: DistanceY(g4,g8) = 1
    c: DistanceY(g8,g12) = 1
    c: DistanceY(g12,g16) = 1
    c: DistanceY(g16,g0) = 1
    c: Tangent(g0,g-5)
    c: Tangent(g16,g-5)
    c: Tangent(g12,g-5)
    c: Tangent(g8,g-5)
    c: Tangent(g4,g-5)
FEATURE [PartDesign::Chamfer] Chamfer009
  Angle = 45
  Base = -> Pad017 [Edge151,Edge154]
  BaseFeature = -> Pad017
  ChamferType = 1
  FlipDirection = false
  Refine = true
  Size = 1.5
  Size2 = 2.8
  SupportTransform = false
  Suppressed = false
  UseAllEdges = false
FEATURE [PartDesign::Pocket] Pocket009
  BaseFeature = -> Chamfer009
  Direction = (0,1,-2e-16)
  Length = 1
  Length2 = 5
  Profile = -> Sketch125
  ReferenceAxis = -> Sketch125 [N_Axis]
  Refine = true
  Suppressed = false
  Type = 0
FEATURE [PartDesign::Pad] Pad014
  BaseFeature = -> Pocket009
  Direction = (0,-1,2e-16)
  Length = 0.8
  Length2 = 10
  Profile = -> Sketch120
  ReferenceAxis = -> Sketch120 [N_Axis]
  Refine = true
  Suppressed = false
  Type = 0
FEATURE [Sketcher::SketchObject] Sketch124
  ArcFitTolerance = 1e-06
  AttachmentSupport = -> [Pad014]
  ExternalGeometry = -> [Binder001]
  FullyConstrained = true
  MakeInternals = false
  MapMode = 5
  Placement = pos=(0,-2.8,6e-16) rot=(1,0,0;1.5708rad)
  sketch-geometry (4):
    g0: LineSegment StartX=-129 StartY=39.2 StartZ=0 EndX=-131.599 EndY=31.2 EndZ=0
    g1: LineSegment StartX=-118 StartY=39.2 StartZ=0 EndX=-120.599 EndY=31.2 EndZ=0
    g2: LineSegment StartX=-129 StartY=39.2 StartZ=0 EndX=-118 EndY=39.2 EndZ=0
    g3: LineSegment StartX=-120.599 StartY=31.2 StartZ=0 EndX=-131.599 EndY=31.2 EndZ=0
  constraints (12):
    c: PointOnObject(g0,g-3)
    c: PointOnObject(g1,g-3)
    c: Parallel(g-4,g0)
    c: Parallel(g-4,g1)
    c: Coincident(g2,g0)
    c: Coincident(g2,g1)
    c: DistanceX(g2,g2) = 11
    c: DistanceY(g1,g1) = 8
    c: Coincident(g3,g1)
    c: Horizontal(g3)
    c: Coincident(g3,g0)
    c: DistanceX(g1,g-3) = 118
FEATURE [PartDesign::Pad] Pad018
  BaseFeature = -> Pad014
  Direction = (0,-1,2e-16)
  Length = 1.2
  Length2 = 10
  Profile = -> Sketch124
  ReferenceAxis = -> Sketch124 [N_Axis]
  Refine = true
  Suppressed = false
  Type = 0
FEATURE [Sketcher::SketchObject] Sketch126
  ArcFitTolerance = 1e-06
  AttachmentSupport = -> [Pad018]
  ExternalGeometry = -> [Pad018]
  FullyConstrained = true
  MakeInternals = false
  MapMode = 5
  Placement = pos=(0,-4,0) rot=(1,0,0;1.5708rad)
  sketch-geometry (8):
    g0: LineSegment StartX=-129.877 StartY=36.5 StartZ=0 EndX=-130.137 EndY=35.7 EndZ=0
    g1: LineSegment StartX=-130.69 StartY=34 StartZ=0 EndX=-130.95 EndY=33.2 EndZ=0
    g2: LineSegment StartX=-129.877 StartY=36.5 StartZ=0 EndX=-118.877 EndY=36.5 EndZ=0
    g3: LineSegment StartX=-130.137 StartY=35.7 StartZ=0 EndX=-119.137 EndY=35.7 EndZ=0
    g4: LineSegment StartX=-130.69 StartY=34 StartZ=0 EndX=-119.69 EndY=34 EndZ=0
    g5: LineSegment StartX=-130.95 StartY=33.2 StartZ=0 EndX=-119.95 EndY=33.2 EndZ=0
    g6: LineSegment StartX=-118.877 StartY=36.5 StartZ=0 EndX=-119.137 EndY=35.7 EndZ=0
    g7: LineSegment StartX=-119.69 StartY=34 StartZ=0 EndX=-119.95 EndY=33.2 EndZ=0
  constraints (20):
    c: Coincident(g2,g0)
    c: Horizontal(g2)
    c: Coincident(g3,g0)
    c: Horizontal(g3)
    c: Coincident(g4,g1)
    c: Horizontal(g4)
    c: Coincident(g5,g1)
    c: Horizontal(g5)
    c: Coincident(g6,g2)
    c: Coincident(g6,g3)
    c: Coincident(g7,g4)
    c: Coincident(g7,g5)
    c: Tangent(g0,g-4)
    c: Tangent(g6,g-5)
    c: Tangent(g1,g-4)
    c: Tangent(g7,g-5)
    c: DistanceY(g3,g2) = 0.8
    c: DistanceY(g5,g4) = 0.8
    c: DistanceY(g-6,g1) = 2
    c: DistanceY(g-6,g0) = 4.5
FEATURE [PartDesign::Chamfer] Chamfer008
  Angle = 45
  Base = -> Pad018 [Edge257]
  BaseFeature = -> Pad018
  ChamferType = 1
  FlipDirection = false
  Refine = true
  Size = 1
  Size2 = 6
  SupportTransform = false
  Suppressed = false
  UseAllEdges = false
FEATURE [PartDesign::Pocket] Pocket010
  BaseFeature = -> Chamfer008
  Direction = (0,1,-2e-16)
  Length = 1
  Length2 = 5
  Profile = -> Sketch126
  ReferenceAxis = -> Sketch126 [N_Axis]
  Refine = true
  Suppressed = false
  Type = 0
FEATURE [PartDesign::Pad] Pad015
  BaseFeature = -> Pocket010
  Direction = (0,-1,2e-16)
  Length = 2
  Length2 = 10
  Profile = -> Sketch121
  ReferenceAxis = -> Sketch121 [N_Axis]
  Refine = true
  Suppressed = false
  Type = 0
FEATURE [PartDesign::Pad] Pad016
  BaseFeature = -> Pad015
  Direction = (0,-1,2e-16)
  Length = 1.6
  Length2 = 10
  Profile = -> Sketch122
  ReferenceAxis = -> Sketch122 [N_Axis]
  Refine = true
  Suppressed = false
  Type = 0
FEATURE [Sketcher::SketchObject] Sketch129
  ArcFitTolerance = 1e-06
  AttachmentSupport = -> [Pad016]
  ExternalGeometry = -> [Binder001]
  FullyConstrained = true
  MakeInternals = false
  MapMode = 5
  Placement = pos=(0,-3.6,0) rot=(1,0,0;1.5708rad)
  sketch-geometry (12):
    g0: LineSegment [constr] StartX=-192.176 StartY=-3.18451 StartZ=0 EndX=-181.223 EndY=20.303 EndZ=0
    g1: LineSegment [constr] StartX=-202.765 StartY=20.303 StartZ=0 EndX=-181.223 EndY=20.303 EndZ=0
    g2: LineSegment StartX=-202.765 StartY=20.303 StartZ=0 EndX=-181.223 EndY=20.303 EndZ=0
    g3: LineSegment StartX=-192.176 StartY=-3.18451 StartZ=0 EndX=-196.804 EndY=-13.1107 EndZ=0
    g4: ArcOfCircle CenterX=-207.583 CenterY=4 CenterZ=0 NormalX=0 NormalY=0 NormalZ=1 AngleXU=0 Radius=17 StartAngle=5.84685 EndAngle=7.56663
    g5: ArcOfEllipse CenterX=-181.223 CenterY=8.55923 CenterZ=0 NormalX=0 NormalY=0 NormalZ=1 MajorRadius=23.4779 MinorRadius=11.7437 AngleXU=2e-16 StartAngle=4.71239 EndAngle=7.85398
    g6: LineSegment [constr] StartX=-157.745 StartY=8.55923 StartZ=0 EndX=-204.701 EndY=8.55923 EndZ=0
    g7: LineSegment [constr] StartX=-181.223 StartY=20.303 StartZ=0 EndX=-181.223 EndY=-3.18451 EndZ=0
    g8: GeomPoint [constr] X=-160.894 Y=8.55923 Z=0
    g9: GeomPoint [constr] X=-201.553 Y=8.55923 Z=0
    g10: ArcOfCircle CenterX=-181.223 CenterY=-20.3763 CenterZ=0 NormalX=0 NormalY=0 NormalZ=1 AngleXU=0 Radius=17.1918 StartAngle=1.57079 EndAngle=2.70526
    g11: GeomPoint [constr] X=-181.223 Y=-3.18451 Z=0
  constraints (23):
    c: Coincident(g0,g-5)
    c: Coincident(g1,g-6)
    c: Horizontal(g1)
    c: Coincident(g1,g0)
    c: Parallel(g0,g-4)
    c: Coincident(g2,g1)
    c: Coincident(g2,g0)
    c: Coincident(g3,g0)
    c: Equal(g4,g-5)
    c: Coincident(g4,g1)
    c: Coincident(g4,g0)
    c: InternalAlignment(g6-g9 -> g5) x4
    c: Vertical(g5,g0)
    c: Horizontal(g6)
    c: Coincident(g5,g0)
    c: DistanceX(g6,g-3) = 10.1
    c: Tangent(g10,g3) = -1.5708
    c: PointOnObject(g11,g10)
    c: Tangent(g5,g10,g11) = 1.5708
    c: Coincident(g10,g5)
    c: Coincident(g11,g7)
    c: Parallel(g3,g-4)
    c: Horizontal(g5,g0)
FEATURE [Sketcher::SketchObject] Sketch130
  ArcFitTolerance = 1e-06
  AttachmentOffset = pos=(0,0,-1.6) rot=(0,0,1;0rad)
  AttachmentSupport = -> [Pad016]
  ExternalGeometry = -> [Binder001]
  FullyConstrained = true
  MakeInternals = false
  MapMode = 5
  Placement = pos=(0,-2,-4e-16) rot=(1,0,0;1.5708rad)
  sketch-geometry (12):
    g0: LineSegment [constr] StartX=-192.176 StartY=-3.18451 StartZ=0 EndX=-181.223 EndY=20.303 EndZ=0
    g1: LineSegment [constr] StartX=-202.765 StartY=20.303 StartZ=0 EndX=-181.223 EndY=20.303 EndZ=0
    g2: LineSegment StartX=-202.765 StartY=20.303 StartZ=0 EndX=-181.223 EndY=20.303 EndZ=0
    g3: LineSegment StartX=-192.176 StartY=-3.18451 StartZ=0 EndX=-193.827 EndY=-6.72678 EndZ=0
    g4: ArcOfCircle CenterX=-207.583 CenterY=4 CenterZ=0 NormalX=0 NormalY=0 NormalZ=1 AngleXU=0 Radius=17 StartAngle=5.84685 EndAngle=7.56663
    g5: ArcOfEllipse CenterX=-181.223 CenterY=10.803 CenterZ=0 NormalX=0 NormalY=0 NormalZ=1 MajorRadius=14.4779 MinorRadius=9.5 AngleXU=0 StartAngle=4.71239 EndAngle=7.85398
    g6: LineSegment [constr] StartX=-166.745 StartY=10.803 StartZ=0 EndX=-195.701 EndY=10.803 EndZ=0
    g7: LineSegment [constr] StartX=-181.223 StartY=20.303 StartZ=0 EndX=-181.223 EndY=1.30297 EndZ=0
    g8: GeomPoint [constr] X=-170.298 Y=10.803 Z=0
    g9: GeomPoint [constr] X=-192.148 Y=10.803 Z=0
    g10: ArcOfCircle CenterX=-181.223 CenterY=-12.6042 CenterZ=0 NormalX=0 NormalY=0 NormalZ=1 AngleXU=0 Radius=13.9072 StartAngle=1.5708 EndAngle=2.70526
    g11: GeomPoint [constr] X=-181.223 Y=1.30297 Z=0
  constraints (23):
    c: Coincident(g0,g-5)
    c: Coincident(g1,g-6)
    c: Horizontal(g1)
    c: Coincident(g1,g0)
    c: Parallel(g0,g-4)
    c: Coincident(g2,g1)
    c: Coincident(g2,g0)
    c: Coincident(g3,g0)
    c: Equal(g4,g-5)
    c: Coincident(g4,g1)
    c: Coincident(g4,g0)
    c: InternalAlignment(g6-g9 -> g5) x4
    c: Vertical(g5,g0)
    c: Horizontal(g6)
    c: Coincident(g5,g0)
    c: DistanceX(g6,g-3) = 19.1
    c: Tangent(g10,g3) = -1.5708
    c: PointOnObject(g11,g10)
    c: Tangent(g5,g10,g11) = 1.5708
    c: Coincident(g10,g5)
    c: Coincident(g11,g7)
    c: Parallel(g3,g-4)
    c: DistanceY(g5,g0) = 19
FEATURE [Part::Part2DObjectPython] Clone2D001  label="Sketch130 (2D)"  # Draft 2D object (typed FeaturePython)
  Fuse = false
  Objects = -> [Sketch130]
  Placement = pos=(0,-2,-4e-16) rot=(1,0,0;1.5708rad)
  Scale = (1,1,1)
FEATURE [Sketcher::SketchObject] Sketch131
  ArcFitTolerance = 1e-06
  AttachmentOffset = pos=(0,0,-3.5) rot=(0,0,1;0rad)
  AttachmentSupport = -> [Pad016]
  ExternalGeometry = -> [Binder001]
  FullyConstrained = true
  MakeInternals = false
  MapMode = 5
  Placement = pos=(0,-0.1,-8e-16) rot=(1,0,0;1.5708rad)
  sketch-geometry (1):
    g0: GeomPoint X=-197.47 Y=8.55923 Z=0
  constraints (1):
    c: Symmetric(g-6,g-4,g0)
FEATURE [Sketcher::SketchObject] Sketch132
  ArcFitTolerance = 1e-06
  AttachmentSupport = -> [Pad016]
  ExternalGeometry = -> [Binder001]
  FullyConstrained = true
  MakeInternals = false
  MapMode = 5
  Placement = pos=(0,-3.6,0) rot=(1,0,0;1.5708rad)
  sketch-geometry (3):
    g0: LineSegment [constr] StartX=-215.42 StartY=-53.0314 StartZ=0 EndX=-167.782 EndY=-53.0314 EndZ=0
    g1: Circle CenterX=-191.282 CenterY=-53.0314 CenterZ=0 NormalX=0 NormalY=0 NormalZ=1 AngleXU=0 Radius=11.5
    g2: Circle CenterX=-191.282 CenterY=-53.0314 CenterZ=0 NormalX=0 NormalY=0 NormalZ=1 AngleXU=0 Radius=10.7
  constraints (8):
    c: Coincident(g0,g-3)
    c: PointOnObject(g0,g-4)
    c: Horizontal(g0)
    c: Diameter(g1) = 23
    c: PointOnObject(g1,g0)
    c: DistanceX(g1,g0) = 23.5
    c: Diameter(g2) = 21.4
    c: Coincident(g2,g1)
FEATURE [Part::Part2DObjectPython] ShapeString  # Draft 2D object (typed FeaturePython)
  FontFile = <path>
  Fuse = false
  Justification = 6
  JustificationReference = 0
  KeepLeftMargin = false
  MakeFace = true
  ObliqueAngle = 0
  Placement = pos=(-199,-3.6,-57.5) rot=(1,0,0;1.5708rad)
  ScaleToSize = true
  Size = 10
  String = AS
  Tracking = 0
FEATURE [Sketcher::SketchObject] Sketch133
  ArcFitTolerance = 1e-06
  AttachmentSupport = -> [Binder]
  ExternalGeometry = -> [Binder]
  FullyConstrained = true
  MakeInternals = false
  MapMode = 5
  Placement = pos=(0,9e-16,0) rot=(0,0.707107,0.707107;3.14159rad)
  sketch-geometry (30):
    g0: LineSegment StartX=0 StartY=39.2 StartZ=0 EndX=0 EndY=3.2 EndZ=0
    g1: LineSegment StartX=0 StartY=3.2 StartZ=0 EndX=82.8 EndY=3.2 EndZ=0
    g2: LineSegment StartX=82.8 StartY=3.2 StartZ=0 EndX=82.8 EndY=6.2 EndZ=0
    g3: LineSegment StartX=82.8 StartY=6.2 StartZ=0 EndX=91.752 EndY=6.2 EndZ=0
    g4: LineSegment StartX=0 StartY=39.2 StartZ=0 EndX=195.887 EndY=39.2 EndZ=0
    g5: LineSegment StartX=195.887 StartY=39.2 StartZ=0 EndX=202.765 EndY=20.303 EndZ=0
    g6: LineSegment StartX=192.333 StartY=24.9893 StartZ=0 EndX=196.467 EndY=26.4942 EndZ=0
    g7: LineSegment StartX=196.467 StartY=26.4942 StartZ=0 EndX=194.073 EndY=33.0721 EndZ=0
    g8: LineSegment StartX=194.073 StartY=33.0721 StartZ=0 EndX=189.939 EndY=31.5672 EndZ=0
    g9: LineSegment StartX=189.939 StartY=31.5672 StartZ=0 EndX=192.333 EndY=24.9893 EndZ=0
    g10: ArcOfCircle CenterX=107.6 CenterY=4 CenterZ=0 NormalX=0 NormalY=0 NormalZ=1 AngleXU=0 Radius=16 StartAngle=1.5708 EndAngle=3.00366
    g11: LineSegment StartX=107.6 StartY=20 StartZ=0 EndX=132.428 EndY=20 EndZ=0
    g12: ArcOfCircle [constr] CenterX=132.428 CenterY=4 CenterZ=0 NormalX=0 NormalY=0 NormalZ=1 AngleXU=0 Radius=16 StartAngle=0.314159 EndAngle=1.5708
    g13: LineSegment StartX=147.645 StartY=8.94427 StartZ=0 EndX=176.685 EndY=-80.4316 EndZ=0
    g14: LineSegment StartX=176.685 StartY=-80.4316 StartZ=0 EndX=215.932 EndY=-80.4316 EndZ=0
    g15: ArcOfCircle CenterX=207.583 CenterY=4 CenterZ=0 NormalX=0 NormalY=0 NormalZ=1 AngleXU=0 Radius=17 StartAngle=1.85815 EndAngle=3.57792
    g16: ArcOfCircle CenterX=184.801 CenterY=-67.3089 CenterZ=0 NormalX=0 NormalY=0 NormalZ=1 AngleXU=0 Radius=33.7833 StartAngle=5.88425 EndAngle=6.71952
    g17: LineSegment StartX=192.176 StartY=-3.18451 StartZ=0 EndX=215.42 EndY=-53.0314 EndZ=0
    g18: Circle CenterX=5.6 CenterY=34.8 CenterZ=0 NormalX=0 NormalY=0 NormalZ=1 AngleXU=0 Radius=1.8
    g19: Circle CenterX=5.6 CenterY=7.6 CenterZ=0 NormalX=0 NormalY=0 NormalZ=1 AngleXU=0 Radius=1.8
    g20: Circle CenterX=78.51 CenterY=34.8 CenterZ=0 NormalX=0 NormalY=0 NormalZ=1 AngleXU=0 Radius=1.8
    g21: Circle CenterX=78.51 CenterY=7.6 CenterZ=0 NormalX=0 NormalY=0 NormalZ=1 AngleXU=0 Radius=1.8
    g22: Circle CenterX=184.08 CenterY=34.8 CenterZ=0 NormalX=0 NormalY=0 NormalZ=1 AngleXU=0 Radius=1.8
    g23: Circle CenterX=179.305 CenterY=-76.8316 CenterZ=0 NormalX=0 NormalY=0 NormalZ=1 AngleXU=0 Radius=1.8
    g24: Circle CenterX=213.443 CenterY=-76.8316 CenterZ=0 NormalX=0 NormalY=0 NormalZ=1 AngleXU=0 Radius=1.8
    g25: Circle CenterX=19 CenterY=21.2 CenterZ=0 NormalX=0 NormalY=0 NormalZ=1 AngleXU=0 Radius=6.3
    g26: Circle CenterX=42 CenterY=21.2 CenterZ=0 NormalX=0 NormalY=0 NormalZ=1 AngleXU=0 Radius=6.3
    g27: Circle CenterX=65 CenterY=21.2 CenterZ=0 NormalX=0 NormalY=0 NormalZ=1 AngleXU=0 Radius=6.3
    g28: LineSegment StartX=132.428 StartY=20 StartZ=0 EndX=144.053 EndY=20 EndZ=0
    g29: LineSegment StartX=147.645 StartY=8.94427 StartZ=0 EndX=144.053 EndY=20 EndZ=0
  constraints (65):
    c: Coincident(g0,g-4)
    c: Coincident(g0,g-5)
    c: Coincident(g1,g0)
    c: Coincident(g1,g-6)
    c: Coincident(g2,g1)
    c: Coincident(g2,g-7)
    c: Coincident(g3,g2)
    c: Coincident(g3,g-8)
    c: Coincident(g4,g0)
    c: Coincident(g4,g-16)
    c: Coincident(g5,g4)
    c: Coincident(g5,g-16)
    c: Coincident(g6,g-20)
    c: Coincident(g6,g-21)
    c: Coincident(g7,g6)
    c: Coincident(g7,g-23)
    c: Coincident(g8,g7)
    c: Coincident(g8,g-22)
    c: Coincident(g9,g8)
    c: Coincident(g9,g6)
    c: Equal(g10,g-8)
    c: Coincident(g10,g3)
    c: Coincident(g10,g-9)
    c: Coincident(g11,g10)
    c: Coincident(g11,g-10)
    c: Equal(g12,g-10)
    c: Coincident(g12,g11)
    c: Coincident(g12,g-11)
    c: Coincident(g13,g12)
    c: Coincident(g13,g-12)
    c: Coincident(g14,g13)
    c: Coincident(g14,g-13)
    c: Equal(g15,g-15)
    c: Coincident(g15,g5)
    c: Coincident(g15,g-15)
    c: Equal(g16,g-13)
    c: Coincident(g16,g14)
    c: Coincident(g16,g-14)
    c: Coincident(g17,g15)
    c: Coincident(g17,g16)
    c: Equal(g18,g-28)
    c: Equal(g19,g-29)
    c: Equal(g20,g-26)
    c: Equal(g21,g-27)
    c: Equal(g22,g-17)
    c: Equal(g24,g-25)
    c: Equal(g23,g-24)
    c: Coincident(g23,g-24)
    c: Coincident(g24,g-25)
    c: Coincident(g22,g-17)
    c: Coincident(g20,g-26)
    c: Coincident(g21,g-27)
    c: Coincident(g18,g-28)
    c: Coincident(g19,g-29)
    c: Equal(g25,g-30)
    c: Equal(g26,g-31)
    c: Equal(g27,g-32)
    c: Coincident(g25,g-30)
    c: Coincident(g26,g-31)
    c: Coincident(g27,g-32)
    c: Parallel(g28,g11)
    c: Parallel(g29,g13)
    c: Coincident(g28,g11)
    c: Coincident(g29,g12)
    c: Coincident(g29,g28)
FEATURE [PartDesign::Pad] Pad019
  Direction = (0,1,-2e-16)
  Length = 2
  Length2 = 10
  Profile = -> Sketch133
  ReferenceAxis = -> Sketch133 [N_Axis]
  Refine = true
  Suppressed = false
  Type = 0
FEATURE [Sketcher::SketchObject] Sketch091  label="Sketch091 - forma anteriore"
  ArcFitTolerance = 1e-06
  AttachmentSupport = -> [Pad019]
  ExternalGeometry = -> [Binder]
  FullyConstrained = true
  MakeInternals = false
  MapMode = 5
  Placement = pos=(0,2,0) rot=(0,0.707107,0.707107;3.14159rad)
  sketch-geometry (12):
    g0: Circle CenterX=5.6 CenterY=34.8 CenterZ=0 NormalX=0 NormalY=0 NormalZ=1 AngleXU=0 Radius=1.8
    g1: Circle CenterX=5.6 CenterY=7.6 CenterZ=0 NormalX=0 NormalY=0 NormalZ=1 AngleXU=0 Radius=1.8
    g2: Circle CenterX=78.51 CenterY=34.8 CenterZ=0 NormalX=0 NormalY=0 NormalZ=1 AngleXU=0 Radius=1.8
    g3: Circle CenterX=78.51 CenterY=7.6 CenterZ=0 NormalX=0 NormalY=0 NormalZ=1 AngleXU=0 Radius=1.8
    g4: LineSegment StartX=0 StartY=39.2 StartZ=0 EndX=0 EndY=3.2 EndZ=0
    g5: LineSegment StartX=0 StartY=3.2 StartZ=0 EndX=82.8 EndY=3.2 EndZ=0
    g6: LineSegment StartX=82.8 StartY=3.2 StartZ=0 EndX=82.8 EndY=39.2 EndZ=0
    g7: LineSegment StartX=82.8 StartY=39.2 StartZ=0 EndX=0 EndY=39.2 EndZ=0
    g8: ArcOfCircle CenterX=19 CenterY=21.2 CenterZ=0 NormalX=0 NormalY=0 NormalZ=1 AngleXU=0 Radius=10 StartAngle=1.5708 EndAngle=4.71239
    g9: ArcOfCircle CenterX=65 CenterY=21.2 CenterZ=0 NormalX=0 NormalY=0 NormalZ=1 AngleXU=0 Radius=10 StartAngle=4.71239 EndAngle=7.85398
    g10: LineSegment StartX=19 StartY=31.2 StartZ=0 EndX=65 EndY=31.2 EndZ=0
    g11: LineSegment StartX=19 StartY=11.2 StartZ=0 EndX=65 EndY=11.2 EndZ=0
  constraints (25):
    c: Equal(g2,g-7)
    c: Equal(g3,g-8)
    c: Equal(g1,g-13)
    c: Equal(g0,g-12)
    c: Coincident(g0,g-12)
    c: Coincident(g1,g-13)
    c: Coincident(g3,g-8)
    c: Coincident(g2,g-7)
    c: Coincident(g4,g-4)
    c: Coincident(g4,g-5)
    c: Coincident(g5,g4)
    c: Coincident(g5,g-6)
    c: Coincident(g6,g5)
    c: PointOnObject(g6,g-3)
    c: Vertical(g6)
    c: Coincident(g7,g6)
    c: Coincident(g7,g4)
    c: Tangent(g8,g10) = 1.5708
    c: Tangent(g8,g11) = -1.5708
    c: Tangent(g9,g10) = 1.5708
    c: Tangent(g9,g11) = -1.5708
    c: Equal(g8,g9)
    c: Radius(g8) = 10
    c: Coincident(g8,g-11)
    c: Coincident(g9,g-9)
FEATURE [Sketcher::SketchObject] Sketch093  label="Sketch093 - scavi interni pulsanti"
  ArcFitTolerance = 1e-06
  AttachmentSupport = -> [Pad019]
  ExternalGeometry = -> [Binder]
  FullyConstrained = true
  MakeInternals = false
  MapMode = 5
  Placement = pos=(0,1.8e-15,0) rot=(1,0,0;1.5708rad)
  sketch-geometry (3):
    g0: Circle CenterX=-65 CenterY=21.2 CenterZ=0 NormalX=0 NormalY=0 NormalZ=1 AngleXU=0 Radius=7.3
    g1: Circle CenterX=-42 CenterY=21.2 CenterZ=0 NormalX=0 NormalY=0 NormalZ=1 AngleXU=0 Radius=7.3
    g2: Circle CenterX=-19 CenterY=21.2 CenterZ=0 NormalX=0 NormalY=0 NormalZ=1 AngleXU=0 Radius=7.3
  constraints (6):
    c: Coincident(g0,g-3)
    c: Coincident(g1,g-4)
    c: Coincident(g2,g-5)
    c: Diameter(g0) = 14.6
    c: Diameter(g1) = 14.6
    c: Diameter(g2) = 14.6
FEATURE [Sketcher::SketchObject] Sketch094  label="Sketch094 - forma centrale"
  ArcFitTolerance = 1e-06
  AttachmentSupport = -> [Pad019]
  ExternalGeometry = -> [Binder]
  FullyConstrained = true
  MakeInternals = false
  MapMode = 5
  Placement = pos=(0,2,0) rot=(0,0.707107,0.707107;3.14159rad)
  sketch-geometry (4):
    g0: LineSegment StartX=137.815 StartY=39.2 StartZ=0 EndX=142.655 EndY=24.303 EndZ=0
    g1: LineSegment StartX=110.815 StartY=24.303 StartZ=0 EndX=142.655 EndY=24.303 EndZ=0
    g2: LineSegment StartX=137.815 StartY=39.2 StartZ=0 EndX=110.815 EndY=39.2 EndZ=0
    g3: ArcOfCircle CenterX=92.2534 CenterY=31.7515 CenterZ=0 NormalX=0 NormalY=0 NormalZ=1 AngleXU=0 Radius=20 StartAngle=5.90156 EndAngle=6.66481
  constraints (12):
    c: PointOnObject(g0,g-3)
    c: Tangent(g0,g-5)
    c: Horizontal(g1)
    c: Coincident(g1,g0)
    c: Coincident(g2,g0)
    c: PointOnObject(g2,g-3)
    c: DistanceX(g2,g2) = 27
    c: Vertical(g1,g2)
    c: Coincident(g3,g2)
    c: Radius(g3) = 20
    c: Coincident(g3,g1)
    c: DistanceY(g-6,g0) = 4
FEATURE [Sketcher::SketchObject] Sketch095  label="Sketch095 - forma posteriore"
  ArcFitTolerance = 1e-06
  AttachmentSupport = -> [Pad019]
  ExternalGeometry = -> [Binder]
  FullyConstrained = true
  MakeInternals = false
  MapMode = 5
  Placement = pos=(0,2,0) rot=(0,0.707107,0.707107;3.14159rad)
  sketch-geometry (15):
    g0: LineSegment StartX=137.815 StartY=39.2 StartZ=0 EndX=143.955 EndY=20.303 EndZ=0
    g1: LineSegment StartX=143.955 StartY=20.303 StartZ=0 EndX=190.141 EndY=20.303 EndZ=0
    g2: ArcOfCircle CenterX=184.08 CenterY=34.8 CenterZ=0 NormalX=0 NormalY=0 NormalZ=1 AngleXU=0 Radius=3.5 StartAngle=3.49066 EndAngle=4.71239
    g3: LineSegment StartX=180.791 StartY=33.6029 StartZ=0 EndX=178.754 EndY=39.2 EndZ=0
    g4: LineSegment StartX=184.08 StartY=31.3 StartZ=0 EndX=186.139 EndY=31.3 EndZ=0
    g5: LineSegment StartX=190.141 StartY=20.303 StartZ=0 EndX=186.139 EndY=31.3 EndZ=0
    g6: LineSegment StartX=137.815 StartY=39.2 StartZ=0 EndX=156.815 EndY=39.2 EndZ=0
    g7: LineSegment StartX=178.754 StartY=39.2 StartZ=0 EndX=168.815 EndY=39.2 EndZ=0
    g8: LineSegment StartX=156.815 StartY=31.2 StartZ=0 EndX=168.815 EndY=31.2 EndZ=0
    g9: ArcOfCircle CenterX=176.411 CenterY=35.2 CenterZ=0 NormalX=0 NormalY=0 NormalZ=1 AngleXU=0 Radius=20 StartAngle=2.94023 EndAngle=3.34295
    g10: ArcOfCircle CenterX=188.411 CenterY=35.2 CenterZ=0 NormalX=0 NormalY=0 NormalZ=1 AngleXU=0 Radius=20 StartAngle=2.94023 EndAngle=3.34295
    g11: LineSegment StartX=157.815 StartY=39.2 StartZ=0 EndX=167.815 EndY=39.2 EndZ=0
    g12: LineSegment StartX=157.436 StartY=36.2 StartZ=0 EndX=167.436 EndY=36.2 EndZ=0
    g13: ArcOfCircle CenterX=177.411 CenterY=35.2 CenterZ=0 NormalX=0 NormalY=0 NormalZ=1 AngleXU=0 Radius=20 StartAngle=2.94023 EndAngle=3.09157
    g14: ArcOfCircle CenterX=187.411 CenterY=35.2 CenterZ=0 NormalX=0 NormalY=0 NormalZ=1 AngleXU=0 Radius=20 StartAngle=2.94023 EndAngle=3.09157
  constraints (46):
    c: PointOnObject(g0,g-3)
    c: Tangent(g0,g-6)
    c: Coincident(g1,g0)
    c: Horizontal(g1)
    c: Radius(g2) = 3.5
    c: Coincident(g2,g-5)
    c: PointOnObject(g3,g-3)
    c: Parallel(g3,g-4)
    c: Tangent(g3,g2) = 1.5708
    c: Horizontal(g4)
    c: Tangent(g4,g2) = -1.5708
    c: Coincident(g5,g1)
    c: Parallel(g5,g-4)
    c: Coincident(g5,g4)
    c: DistanceX(g4,g-8) = 3.8
    c: Coincident(g6,g0)
    c: PointOnObject(g6,g-3)
    c: Coincident(g7,g3)
    c: PointOnObject(g7,g-3)
    c: Horizontal(g8)
    c: DistanceX(g6,g7) = 12
    c: Vertical(g8,g6)
    c: Vertical(g7,g8)
    c: DistanceY(g8,g6) = 8
    c: Coincident(g9,g8)
    c: Coincident(g9,g6)
    c: Coincident(g10,g7)
    c: Coincident(g10,g8)
    c: Radius(g9) = 20
    c: Radius(g10) = 20
    c: PointOnObject(g11,g-3)
    c: PointOnObject(g11,g-3)
    c: DistanceX(g11,g11) = 10
    c: DistanceX(g6,g11) = 1
    c: Horizontal(g12)
    c: Equal(g12,g11)
    c: DistanceY(g12,g11) = 3
    c: Coincident(g13,g11)
    c: Coincident(g13,g12)
    c: Radius(g13) = 20
    c: Coincident(g14,g11)
    c: Coincident(g14,g12)
    c: Radius(g14) = 20
    c: DistanceX(g0,g6) = 19
    c: Horizontal(g9,g13)
    c: Horizontal(g0,g-4)
FEATURE [Sketcher::SketchObject] Sketch096  label="Sketch096 - forma impugnatura"
  ArcFitTolerance = 1e-06
  AttachmentSupport = -> [Pad019]
  ExternalGeometry = -> [Binder]
  FullyConstrained = true
  MakeInternals = false
  MapMode = 5
  Placement = pos=(0,2,0) rot=(0,0.707107,0.707107;3.14159rad)
  sketch-geometry (8):
    g0: LineSegment StartX=176.685 StartY=-80.4316 StartZ=0 EndX=143.955 EndY=20.303 EndZ=0
    g1: LineSegment StartX=176.685 StartY=-80.4316 StartZ=0 EndX=215.932 EndY=-80.4316 EndZ=0
    g2: Circle CenterX=179.305 CenterY=-76.8316 CenterZ=0 NormalX=0 NormalY=0 NormalZ=1 AngleXU=0 Radius=3
    g3: Circle CenterX=213.443 CenterY=-76.8316 CenterZ=0 NormalX=0 NormalY=0 NormalZ=1 AngleXU=0 Radius=3
    g4: LineSegment StartX=143.955 StartY=20.303 StartZ=0 EndX=202.765 EndY=20.303 EndZ=0
    g5: LineSegment StartX=215.42 StartY=-53.0314 StartZ=0 EndX=192.176 EndY=-3.18451 EndZ=0
    g6: ArcOfCircle CenterX=184.801 CenterY=-67.3089 CenterZ=0 NormalX=0 NormalY=0 NormalZ=1 AngleXU=0 Radius=33.7833 StartAngle=5.88425 EndAngle=6.71952
    g7: ArcOfCircle CenterX=207.583 CenterY=4 CenterZ=0 NormalX=0 NormalY=0 NormalZ=1 AngleXU=0 Radius=17 StartAngle=1.85815 EndAngle=3.57792
  constraints (19):
    c: Coincident(g0,g-4)
    c: PointOnObject(g0,g-3)
    c: Horizontal(g0,g-7)
    c: Coincident(g1,g0)
    c: Coincident(g1,g-5)
    c: Diameter(g2) = 6
    c: Diameter(g3) = 6
    c: Coincident(g2,g-9)
    c: Coincident(g3,g-10)
    c: Coincident(g4,g0)
    c: Coincident(g5,g-6)
    c: Coincident(g6,g1)
    c: Coincident(g6,g5)
    c: Equal(g-5,g6)
    c: Coincident(g5,g-7)
    c: Coincident(g4,g-7)
    c: Tangent(g7,g-7)
    c: Coincident(g7,g4)
    c: Coincident(g7,g5)
FEATURE [Sketcher::SketchObject] Sketch097
  ArcFitTolerance = 1e-06
  AttachmentSupport = -> [Pad019]
  ExternalGeometry = -> [Binder]
  FullyConstrained = true
  MakeInternals = false
  MapMode = 5
  Placement = pos=(0,2,0) rot=(0,0.707107,0.707107;3.14159rad)
  sketch-geometry (4):
    g0: LineSegment StartX=90 StartY=36.8 StartZ=0 EndX=108 EndY=36.8 EndZ=0
    g1: LineSegment StartX=108 StartY=36.8 StartZ=0 EndX=108 EndY=26.8 EndZ=0
    g2: LineSegment StartX=108 StartY=26.8 StartZ=0 EndX=90 EndY=26.8 EndZ=0
    g3: ArcOfCircle CenterX=94 CenterY=31.8 CenterZ=0 NormalX=0 NormalY=0 NormalZ=1 AngleXU=0 Radius=6.40312 StartAngle=2.24554 EndAngle=4.03765
  constraints (13):
    c: Horizontal(g0)
    c: Coincident(g1,g0)
    c: Vertical(g1)
    c: DistanceX(g0,g0) = 18
    c: DistanceY(g1,g1) = 10
    c: Coincident(g2,g1)
    c: Horizontal(g2)
    c: Equal(g2,g0)
    c: DistanceY(g0,g-3) = 2.4
    c: Coincident(g3,g0)
    c: Coincident(g3,g2)
    c: DistanceX(g2,g3) = 4
    c: DistanceX(g-3,g0) = 90
FEATURE [PartDesign::Chamfer] Chamfer015
  Angle = 45
  Base = -> Pad019 [Edge19,Edge22,Edge79]
  BaseFeature = -> Pad019
  ChamferType = 0
  FlipDirection = false
  Refine = true
  Size = 1.9
  Size2 = 1
  SupportTransform = false
  Suppressed = false
  UseAllEdges = false
FEATURE [PartDesign::Pocket] Pocket002
  BaseFeature = -> Chamfer015
  Direction = (0,1,-2e-16)
  Length = 1.2
  Length2 = 5
  Profile = -> Sketch093
  ReferenceAxis = -> Sketch093 [N_Axis]
  Refine = true
  Suppressed = false
  Type = 0
FEATURE [PartDesign::Pad] Pad005
  BaseFeature = -> Pocket002
  Direction = (0,1,-2e-16)
  Length = 1.6
  Length2 = 10
  Profile = -> Sketch091
  ReferenceAxis = -> Sketch091 [N_Axis]
  Refine = true
  Suppressed = false
  Type = 0
FEATURE [Sketcher::SketchObject] Sketch092  label="Sketch092 - scavi per viti anteriori"
  ArcFitTolerance = 1e-06
  AttachmentSupport = -> [Pad005]
  ExternalGeometry = -> [Binder]
  FullyConstrained = true
  MakeInternals = false
  MapMode = 5
  Placement = pos=(0,3.6,0) rot=(0,0.707107,0.707107;3.14159rad)
  sketch-geometry (20):
    g0: ArcOfCircle CenterX=5.6 CenterY=7.6 CenterZ=0 NormalX=0 NormalY=0 NormalZ=1 AngleXU=0 Radius=3.5 StartAngle=0 EndAngle=1.5708
    g1: ArcOfCircle CenterX=5.6 CenterY=34.8 CenterZ=0 NormalX=0 NormalY=0 NormalZ=1 AngleXU=0 Radius=3.5 StartAngle=4.71239 EndAngle=6.28319
    g2: ArcOfCircle CenterX=78.51 CenterY=34.8 CenterZ=0 NormalX=0 NormalY=0 NormalZ=1 AngleXU=0 Radius=3.5 StartAngle=3.14159 EndAngle=4.71239
    g3: ArcOfCircle CenterX=78.51 CenterY=7.6 CenterZ=0 NormalX=0 NormalY=0 NormalZ=1 AngleXU=0 Radius=3.5 StartAngle=1.5708 EndAngle=3.14159
    g4: LineSegment StartX=0 StartY=3.2 StartZ=0 EndX=0 EndY=11.1 EndZ=0
    g5: LineSegment StartX=0 StartY=11.1 StartZ=0 EndX=5.6 EndY=11.1 EndZ=0
    g6: LineSegment StartX=0 StartY=3.2 StartZ=0 EndX=9.1 EndY=3.2 EndZ=0
    g7: LineSegment StartX=9.1 StartY=3.2 StartZ=0 EndX=9.1 EndY=7.6 EndZ=0
    g8: LineSegment StartX=0 StartY=39.2 StartZ=0 EndX=0 EndY=31.3 EndZ=0
    g9: LineSegment StartX=0 StartY=31.3 StartZ=0 EndX=5.6 EndY=31.3 EndZ=0
    g10: LineSegment StartX=0 StartY=39.2 StartZ=0 EndX=9.1 EndY=39.2 EndZ=0
    g11: LineSegment StartX=9.1 StartY=39.2 StartZ=0 EndX=9.1 EndY=34.8 EndZ=0
    g12: LineSegment StartX=82.8 StartY=39.2 StartZ=0 EndX=75.01 EndY=39.2 EndZ=0
    g13: LineSegment StartX=82.8 StartY=39.2 StartZ=0 EndX=82.8 EndY=31.3 EndZ=0
    g14: LineSegment StartX=82.8 StartY=31.3 StartZ=0 EndX=78.51 EndY=31.3 EndZ=0
    g15: LineSegment StartX=82.8 StartY=3.2 StartZ=0 EndX=75.01 EndY=3.2 EndZ=0
    g16: LineSegment StartX=75.01 StartY=3.2 StartZ=0 EndX=75.01 EndY=7.6 EndZ=0
    g17: LineSegment StartX=82.8 StartY=3.2 StartZ=0 EndX=82.8 EndY=11.1 EndZ=0
    g18: LineSegment StartX=82.8 StartY=11.1 StartZ=0 EndX=78.51 EndY=11.1 EndZ=0
    g19: LineSegment StartX=75.01 StartY=39.2 StartZ=0 EndX=75.01 EndY=34.8 EndZ=0
  constraints (48):
    c: Radius(g0) = 3.5
    c: Coincident(g0,g-10)
    c: Radius(g1) = 3.5
    c: Coincident(g1,g-9)
    c: Radius(g2) = 3.5
    c: Coincident(g2,g-8)
    c: Radius(g3) = 3.5
    c: Coincident(g3,g-7)
    c: Coincident(g4,g-5)
    c: PointOnObject(g4,g-4)
    c: Coincident(g5,g4)
    c: Horizontal(g5)
    c: Coincident(g6,g4)
    c: PointOnObject(g6,g-5)
    c: Coincident(g7,g6)
    c: Vertical(g7)
    c: Coincident(g8,g-4)
    c: PointOnObject(g8,g-4)
    c: Coincident(g9,g8)
    c: Horizontal(g9)
    c: Coincident(g10,g8)
    c: PointOnObject(g10,g-3)
    c: Coincident(g11,g10)
    c: Vertical(g11)
    c: PointOnObject(g12,g-3)
    c: PointOnObject(g12,g-3)
    c: Coincident(g13,g12)
    c: Vertical(g13)
    c: Coincident(g14,g13)
    c: Horizontal(g14)
    c: Coincident(g15,g-6)
    c: PointOnObject(g15,g-5)
    c: Coincident(g16,g15)
    c: Vertical(g16)
    c: Coincident(g17,g15)
    c: Coincident(g18,g17)
    c: Horizontal(g18)
    c: Tangent(g3,g18) = -1.5708
    c: Tangent(g16,g3) = 1.5708
    c: Coincident(g19,g12)
    c: Vertical(g19)
    c: Tangent(g2,g19) = -1.5708
    c: Tangent(g2,g14) = 1.5708
    c: Tangent(g0,g7) = -1.5708
    c: Tangent(g0,g5) = 1.5708
    c: Tangent(g9,g1) = -1.5708
    c: Tangent(g1,g11) = 1.5708
    c: Tangent(g17,g13)
FEATURE [PartDesign::Pocket] Pocket001
  BaseFeature = -> Pad005
  Direction = (0,-1,2e-16)
  Length = 1.6
  Length2 = 5
  Profile = -> Sketch092
  ReferenceAxis = -> Sketch092 [N_Axis]
  Refine = true
  Suppressed = false
  Type = 0
FEATURE [PartDesign::Pad] Pad006
  BaseFeature = -> Pocket001
  Direction = (0,1,-2e-16)
  Length = 0.8
  Length2 = 10
  Profile = -> Sketch094
  ReferenceAxis = -> Sketch094 [N_Axis]
  Refine = true
  Suppressed = false
  Type = 0
FEATURE [PartDesign::Pad] Pad007
  BaseFeature = -> Pad006
  Direction = (0,1,-2e-16)
  Length = 2
  Length2 = 10
  Profile = -> Sketch095
  ReferenceAxis = -> Sketch095 [N_Axis]
  Refine = true
  Suppressed = false
  Type = 0
FEATURE [PartDesign::Pad] Pad008  label="Pad008 - forma impugnatura"
  BaseFeature = -> Pad007
  Direction = (0,1,-2e-16)
  Length = 1.6
  Length2 = 10
  Profile = -> Sketch096
  ReferenceAxis = -> Sketch096 [N_Axis]
  Refine = true
  Suppressed = false
  Type = 0
FEATURE [PartDesign::Pad] Pad009
  BaseFeature = -> Pad008
  Direction = (0,1,-2e-16)
  Length = 1.6
  Length2 = 10
  Profile = -> Sketch097
  ReferenceAxis = -> Sketch097 [N_Axis]
  Refine = true
  Suppressed = false
  Type = 0
FEATURE [Sketcher::SketchObject] Sketch098
  ArcFitTolerance = 1e-06
  AttachmentSupport = -> [Pad006]
  ExternalGeometry = -> [Binder]
  FullyConstrained = true
  MakeInternals = false
  MapMode = 5
  Placement = pos=(0,2.8,-7e-16) rot=(0,0.707107,0.707107;3.14159rad)
  sketch-geometry (4):
    g0: LineSegment StartX=118 StartY=39.2 StartZ=0 EndX=129 EndY=39.2 EndZ=0
    g1: LineSegment StartX=120.599 StartY=31.2 StartZ=0 EndX=131.599 EndY=31.2 EndZ=0
    g2: LineSegment StartX=129 StartY=39.2 StartZ=0 EndX=131.599 EndY=31.2 EndZ=0
    g3: LineSegment StartX=118 StartY=39.2 StartZ=0 EndX=120.599 EndY=31.2 EndZ=0
  constraints (12):
    c: PointOnObject(g0,g-3)
    c: PointOnObject(g0,g-3)
    c: DistanceX(g0,g0) = 11
    c: Horizontal(g1)
    c: Equal(g1,g0)
    c: Coincident(g2,g0)
    c: Coincident(g3,g0)
    c: Parallel(g-4,g2)
    c: Coincident(g1,g2)
    c: Coincident(g1,g3)
    c: DistanceY(g1,g0) = 8
    c: DistanceX(g-3,g0) = 118
FEATURE [Sketcher::SketchObject] Sketch099
  ArcFitTolerance = 1e-06
  AttachmentSupport = -> [Pad008]
  ExternalGeometry = -> [Binder]
  FullyConstrained = true
  MakeInternals = false
  MapMode = 5
  Placement = pos=(0,3.6,0) rot=(0,0.707107,0.707107;3.14159rad)
  sketch-geometry (13):
    g0: LineSegment StartX=192.176 StartY=-3.18451 StartZ=0 EndX=196.804 EndY=-13.1108 EndZ=0
    g1: LineSegment [constr] StartX=202.765 StartY=20.303 StartZ=0 EndX=181.223 EndY=20.303 EndZ=0
    g2: LineSegment [constr] StartX=181.223 StartY=20.303 StartZ=0 EndX=181.223 EndY=-3.18451 EndZ=0
    g3: ArcOfCircle CenterX=181.223 CenterY=-20.3764 CenterZ=0 NormalX=0 NormalY=0 NormalZ=1 AngleXU=0 Radius=17.1918 StartAngle=0.436332 EndAngle=1.57079
    g4: ArcOfEllipse CenterX=181.223 CenterY=8.55923 CenterZ=0 NormalX=0 NormalY=0 NormalZ=1 MajorRadius=23.4779 MinorRadius=11.7437 AngleXU=0 StartAngle=1.5708 EndAngle=4.71239
    g5: LineSegment [constr] StartX=204.701 StartY=8.55923 StartZ=0 EndX=157.745 EndY=8.55923 EndZ=0
    g6: LineSegment [constr] StartX=181.223 StartY=20.303 StartZ=0 EndX=181.223 EndY=-3.18451 EndZ=0
    g7: GeomPoint [constr] X=201.553 Y=8.55923 Z=0
    g8: GeomPoint [constr] X=160.894 Y=8.55923 Z=0
    g9: GeomPoint [constr] X=181.223 Y=-3.18451 Z=0
    g10: LineSegment StartX=181.223 StartY=20.303 StartZ=0 EndX=202.765 EndY=20.303 EndZ=0
    g11: ArcOfCircle CenterX=207.583 CenterY=4 CenterZ=0 NormalX=0 NormalY=0 NormalZ=1 AngleXU=0 Radius=17 StartAngle=1.85815 EndAngle=3.57792
    g12: LineSegment [constr] StartX=172.411 StartY=39.2 StartZ=0 EndX=192.176 EndY=-3.18451 EndZ=0
  constraints (27):
    c: Coincident(g1,g-7)
    c: Horizontal(g1)
    c: Coincident(g2,g1)
    c: Vertical(g2)
    c: Horizontal(g2,g0)
    c: Coincident(g3,g0)
    c: Coincident(g3,g2)
    c: InternalAlignment(g5-g8 -> g4) x4
    c: Horizontal(g5)
    c: PointOnObject(g4,g2)
    c: Coincident(g4,g1)
    c: DistanceX(g-3,g5) = 10.1
    c: Coincident(g4,g2)
    c: Tangent(g3,g-5)
    c: PointOnObject(g9,g4)
    c: PointOnObject(g9,g3)
    c: Tangent(g4,g3,g9) = 1.5708
    c: Coincident(g10,g1)
    c: Coincident(g10,g1)
    c: Equal(g11,g-4)
    c: Coincident(g11,g1)
    c: Coincident(g11,g0)
    c: PointOnObject(g12,g-6)
    c: PointOnObject(g1,g12)
    c: Tangent(g12,g-5) = -1.5708
    c: Tangent(g0,g-5) = -1.5708
    c: Horizontal(g9,g12)
FEATURE [Sketcher::SketchObject] Sketch106  label="Sketch106 - smusso impuniatura interno"
  ArcFitTolerance = 1e-06
  AttachmentSupport = -> [Pad008]
  ExternalGeometry = -> [Pad008]
  FullyConstrained = true
  MakeInternals = false
  MapMode = 5
  Placement = pos=(0,-1.586e-13,-80.4316) rot=(1,0,0;3.14159rad)
  sketch-geometry (9):
    g0: LineSegment StartX=-176.685 StartY=-3.6 StartZ=0 EndX=-176.685 EndY=-1.15e-13 EndZ=0
    g1: LineSegment [constr] StartX=-176.685 StartY=-1.416e-13 StartZ=0 EndX=-176.685 EndY=-1.149e-13 EndZ=0
    g2: LineSegment [constr] StartX=-186.685 StartY=-3.6 StartZ=0 EndX=-186.685 EndY=-1.15e-13 EndZ=0
    g3: ArcOfEllipse CenterX=-186.685 CenterY=-1.149e-13 CenterZ=0 NormalX=0 NormalY=0 NormalZ=1 MajorRadius=10 MinorRadius=3.6 AngleXU=-3.14159 StartAngle=1.5708 EndAngle=3.14159
    g4: LineSegment [constr] StartX=-196.685 StartY=-1.416e-13 StartZ=0 EndX=-176.685 EndY=-1.416e-13 EndZ=0
    g5: LineSegment [constr] StartX=-186.685 StartY=-3.6 StartZ=0 EndX=-186.685 EndY=3.6 EndZ=0
    g6: GeomPoint [constr] X=-196.015 Y=-1.43e-13 Z=0
    g7: GeomPoint [constr] X=-177.356 Y=-1.415e-13 Z=0
    g8: LineSegment StartX=-176.685 StartY=-3.6 StartZ=0 EndX=-186.685 EndY=-3.6 EndZ=0
  constraints (15):
    c: PointOnObject(g2,g-3)
    c: Coincident(g1,g-5)
    c: DistanceY(g1,g1) = 0
    c: Coincident(g0,g1)
    c: DistanceX(g2,g-5) = 10
    c: Vertical(g2)
    c: Horizontal(g2,g0)
    c: InternalAlignment(g4-g7 -> g3) x4
    c: Coincident(g3,g2)
    c: Horizontal(g4)
    c: Coincident(g3,g0)
    c: Tangent(g0,g-5) = 1.5708
    c: Coincident(g3,g2)
    c: Coincident(g8,g0)
    c: Coincident(g8,g2)
FEATURE [Sketcher::SketchObject] Sketch107  label="Sketch107 - smusso impugnatura esterno"
  ArcFitTolerance = 1e-06
  AttachmentSupport = -> [Pad008]
  ExternalGeometry = -> [Pad008]
  FullyConstrained = true
  MakeInternals = false
  MapMode = 5
  Placement = pos=(0,-1.586e-13,-80.4316) rot=(1,0,0;3.14159rad)
  sketch-geometry (9):
    g0: LineSegment [constr] StartX=-215.932 StartY=-1.416e-13 StartZ=0 EndX=-215.932 EndY=-5.02e-14 EndZ=0
    g1: LineSegment StartX=-215.932 StartY=-3.6 StartZ=0 EndX=-215.932 EndY=-5.02e-14 EndZ=0
    g2: LineSegment StartX=-215.932 StartY=-3.6 StartZ=0 EndX=-205.932 EndY=-3.6 EndZ=0
    g3: LineSegment [constr] StartX=-205.932 StartY=-3.6 StartZ=0 EndX=-205.932 EndY=-5.02e-14 EndZ=0
    g4: ArcOfEllipse CenterX=-205.932 CenterY=-5.02e-14 CenterZ=0 NormalX=0 NormalY=0 NormalZ=1 MajorRadius=10 MinorRadius=3.6 AngleXU=-3.14159 StartAngle=-2.66e-14 EndAngle=1.5708
    g5: LineSegment [constr] StartX=-215.932 StartY=-1.416e-13 StartZ=0 EndX=-195.932 EndY=-1.416e-13 EndZ=0
    g6: LineSegment [constr] StartX=-205.932 StartY=-3.6 StartZ=0 EndX=-205.932 EndY=3.6 EndZ=0
    g7: GeomPoint [constr] X=-215.262 Y=-1.425e-13 Z=0
    g8: GeomPoint [constr] X=-196.602 Y=-1.551e-13 Z=0
  constraints (16):
    c: Coincident(g0,g-6)
    c: PointOnObject(g0,g-6)
    c: DistanceY(g0,g0) = 0
    c: Coincident(g1,g-6)
    c: Coincident(g1,g0)
    c: Tangent(g2,g-3)
    c: DistanceX(g2,g2) = 10
    c: Coincident(g3,g2)
    c: Vertical(g3)
    c: Horizontal(g3,g0)
    c: InternalAlignment(g5-g8 -> g4) x4
    c: Coincident(g4,g3)
    c: Horizontal(g5)
    c: Coincident(g4,g0)
    c: Coincident(g4,g2)
    c: PointOnObject(g2,g1)
FEATURE [Sketcher::SketchObject] Sketch108
  ArcFitTolerance = 1e-06
  AttachmentOffset = pos=(0,0,-1.6) rot=(0,0,1;0rad)
  AttachmentSupport = -> [Pad008]
  ExternalGeometry = -> [Binder]
  FullyConstrained = true
  MakeInternals = false
  MapMode = 5
  Placement = pos=(0,2,4e-16) rot=(0,0.707107,0.707107;3.14159rad)
  sketch-geometry (14):
    g0: LineSegment StartX=192.176 StartY=-3.18451 StartZ=0 EndX=193.827 EndY=-6.72678 EndZ=0
    g1: LineSegment [constr] StartX=202.765 StartY=20.303 StartZ=0 EndX=181.223 EndY=20.303 EndZ=0
    g2: LineSegment [constr] StartX=181.223 StartY=20.303 StartZ=0 EndX=181.223 EndY=1.30297 EndZ=0
    g3: ArcOfCircle CenterX=181.223 CenterY=-12.6042 CenterZ=0 NormalX=0 NormalY=0 NormalZ=1 AngleXU=0 Radius=13.9072 StartAngle=0.436332 EndAngle=1.5708
    g4: ArcOfEllipse CenterX=181.223 CenterY=10.803 CenterZ=0 NormalX=0 NormalY=0 NormalZ=1 MajorRadius=14.4779 MinorRadius=9.5 AngleXU=0 StartAngle=1.5708 EndAngle=4.71239
    g5: LineSegment [constr] StartX=195.701 StartY=10.803 StartZ=0 EndX=166.745 EndY=10.803 EndZ=0
    g6: LineSegment [constr] StartX=181.223 StartY=20.303 StartZ=0 EndX=181.223 EndY=1.30297 EndZ=0
    g7: GeomPoint [constr] X=192.148 Y=10.803 Z=0
    g8: GeomPoint [constr] X=170.298 Y=10.803 Z=0
    g9: LineSegment StartX=181.223 StartY=20.303 StartZ=0 EndX=202.765 EndY=20.303 EndZ=0
    g10: ArcOfCircle CenterX=207.583 CenterY=4 CenterZ=0 NormalX=0 NormalY=0 NormalZ=1 AngleXU=0 Radius=17 StartAngle=1.85815 EndAngle=3.57792
    g11: LineSegment [constr] StartX=172.411 StartY=39.2 StartZ=0 EndX=192.176 EndY=-3.18451 EndZ=0
    g12: GeomPoint [constr] X=181.223 Y=1.30297 Z=0
    g13: GeomPoint [constr] X=181.223 Y=1.30297 Z=0
  constraints (28):
    c: Coincident(g1,g-7)
    c: Horizontal(g1)
    c: Coincident(g2,g1)
    c: Vertical(g2)
    c: Coincident(g3,g2)
    c: InternalAlignment(g5-g8 -> g4) x4
    c: Horizontal(g5)
    c: PointOnObject(g4,g2)
    c: Coincident(g4,g1)
    c: DistanceX(g-3,g5) = 19.1
    c: Coincident(g4,g2)
    c: Coincident(g9,g1)
    c: Coincident(g9,g1)
    c: Coincident(g10,g1)
    c: Coincident(g10,g0)
    c: PointOnObject(g11,g-6)
    c: PointOnObject(g1,g11)
    c: DistanceY(g2,g1) = 19
    c: Coincident(g10,g-4)
    c: PointOnObject(g12,g4)
    c: PointOnObject(g12,g3)
    c: Tangent(g11,g-5) = -1.5708
    c: Tangent(g0,g-5) = -1.5708
    c: Tangent(g3,g0) = 1.5708
    c: PointOnObject(g13,g4)
    c: PointOnObject(g13,g3)
    c: Tangent(g4,g3,g13) = 1.5708
    c: Horizontal(g11,g0)
FEATURE [Part::Part2DObjectPython] Clone2D  label="Sketch108 (2D)"  # Draft 2D object (typed FeaturePython)
  Fuse = false
  Objects = -> [Sketch108]
  Placement = pos=(0,2,4e-16) rot=(0,0.707107,0.707107;3.14159rad)
  Scale = (1,1,1)
FEATURE [Sketcher::SketchObject] Sketch109
  ArcFitTolerance = 1e-06
  AttachmentOffset = pos=(0,0,-3.5) rot=(0,0,1;0rad)
  AttachmentSupport = -> [Pad008]
  ExternalGeometry = -> [Binder]
  FullyConstrained = true
  MakeInternals = false
  MapMode = 5
  Placement = pos=(0,0.1,8e-16) rot=(0,0.707107,0.707107;3.14159rad)
  sketch-geometry (1):
    g0: GeomPoint X=197.47 Y=8.55923 Z=0
  constraints (1):
    c: Symmetric(g-7,g-5,g0)
FEATURE [PartDesign::Chamfer] Chamfer005
  Angle = 45
  Base = -> Pad009 [Edge215,Edge212]
  BaseFeature = -> Pad009
  ChamferType = 1
  FlipDirection = false
  Refine = true
  Size = 1.5
  Size2 = 2.8
  SupportTransform = false
  Suppressed = false
  UseAllEdges = false
FEATURE [Sketcher::SketchObject] Sketch111
  ArcFitTolerance = 1e-06
  AttachmentSupport = -> [Pad009]
  ExternalGeometry = -> [Pad009]
  FullyConstrained = true
  MakeInternals = false
  MapMode = 5
  Placement = pos=(0,3.6,-8e-16) rot=(0,0.707107,0.707107;3.14159rad)
  sketch-geometry (21):
    g0: LineSegment [constr] StartX=97 StartY=36.8 StartZ=0 EndX=97 EndY=26.8 EndZ=0
    g1: LineSegment StartX=97 StartY=28.6 StartZ=0 EndX=97 EndY=27.8 EndZ=0
    g2: LineSegment StartX=97 StartY=27.8 StartZ=0 EndX=108 EndY=27.8 EndZ=0
    g3: LineSegment StartX=108 StartY=27.8 StartZ=0 EndX=108 EndY=28.6 EndZ=0
    g4: LineSegment StartX=108 StartY=28.6 StartZ=0 EndX=97 EndY=28.6 EndZ=0
    g5: LineSegment StartX=97 StartY=35.8 StartZ=0 EndX=97 EndY=35 EndZ=0
    g6: LineSegment StartX=97 StartY=35 StartZ=0 EndX=108 EndY=35 EndZ=0
    g7: LineSegment StartX=108 StartY=35 StartZ=0 EndX=108 EndY=35.8 EndZ=0
    g8: LineSegment StartX=108 StartY=35.8 StartZ=0 EndX=97 EndY=35.8 EndZ=0
    g9: LineSegment StartX=97 StartY=30.4 StartZ=0 EndX=97 EndY=29.6 EndZ=0
    g10: LineSegment StartX=97 StartY=29.6 StartZ=0 EndX=108 EndY=29.6 EndZ=0
    g11: LineSegment StartX=108 StartY=29.6 StartZ=0 EndX=108 EndY=30.4 EndZ=0
    g12: LineSegment StartX=108 StartY=30.4 StartZ=0 EndX=97 EndY=30.4 EndZ=0
    g13: LineSegment StartX=97 StartY=34 StartZ=0 EndX=97 EndY=33.2 EndZ=0
    g14: LineSegment StartX=97 StartY=33.2 StartZ=0 EndX=108 EndY=33.2 EndZ=0
    g15: LineSegment StartX=108 StartY=33.2 StartZ=0 EndX=108 EndY=34 EndZ=0
    g16: LineSegment StartX=108 StartY=34 StartZ=0 EndX=97 EndY=34 EndZ=0
    g17: LineSegment StartX=97 StartY=32.2 StartZ=0 EndX=97 EndY=31.4 EndZ=0
    g18: LineSegment StartX=97 StartY=31.4 StartZ=0 EndX=108 EndY=31.4 EndZ=0
    g19: LineSegment StartX=108 StartY=31.4 StartZ=0 EndX=108 EndY=32.2 EndZ=0
    g20: LineSegment StartX=108 StartY=32.2 StartZ=0 EndX=97 EndY=32.2 EndZ=0
  constraints (54):
    c: Vertical(g0)
    c: PointOnObject(g0,g-3)
    c: PointOnObject(g0,g-4)
    c: DistanceX(g0,g-5) = 11
    c: Coincident(g1,g2)
    c: Coincident(g2,g3)
    c: Coincident(g3,g4)
    c: Coincident(g4,g1)
    c: Horizontal(g2)
    c: Horizontal(g4)
    c: Tangent(g1,g0)
    c: Tangent(g3,g-5)
    c: DistanceY(g2,g3) = 0.8
    c: Coincident(g5,g6)
    c: Coincident(g6,g7)
    c: Coincident(g7,g8)
    c: Coincident(g8,g5)
    c: Horizontal(g6)
    c: Horizontal(g8)
    c: DistanceY(g6,g7) = 0.8
    c: Coincident(g9,g10)
    c: Coincident(g10,g11)
    c: Coincident(g11,g12)
    c: Coincident(g12,g9)
    c: Horizontal(g10)
    c: Horizontal(g12)
    c: DistanceY(g10,g11) = 0.8
    c: Tangent(g5,g0)
    c: Tangent(g7,g-5)
    c: Tangent(g9,g0)
    c: Tangent(g11,g-5)
    c: Coincident(g13,g14)
    c: Coincident(g14,g15)
    c: Coincident(g15,g16)
    c: Coincident(g16,g13)
    c: Horizontal(g14)
    c: Horizontal(g16)
    c: DistanceY(g14,g15) = 0.8
    c: Tangent(g13,g0)
    c: Tangent(g15,g-5)
    c: Coincident(g17,g18)
    c: Coincident(g18,g19)
    c: Coincident(g19,g20)
    c: Coincident(g20,g17)
    c: Horizontal(g18)
    c: Horizontal(g20)
    c: DistanceY(g18,g19) = 0.8
    c: Tangent(g17,g0)
    c: Tangent(g19,g-5)
    c: DistanceY(g1,g9) = 1
    c: DistanceY(g9,g17) = 1
    c: DistanceY(g17,g13) = 1
    c: DistanceY(g13,g5) = 1
    c: DistanceY(g0,g1) = 1
FEATURE [PartDesign::Pocket] Pocket004
  BaseFeature = -> Chamfer005
  Direction = (0,-1,2e-16)
  Length = 1
  Length2 = 5
  Profile = -> Sketch111
  ReferenceAxis = -> Sketch111 [N_Axis]
  Refine = true
  Suppressed = false
  Type = 0
FEATURE [PartDesign::Pad] Pad010
  BaseFeature = -> Pocket004
  Direction = (0,1,-2e-16)
  Length = 1.2
  Length2 = 10
  Profile = -> Sketch098
  ReferenceAxis = -> Sketch098 [N_Axis]
  Refine = true
  Suppressed = false
  Type = 0
FEATURE [PartDesign::Chamfer] Chamfer006
  Angle = 45
  Base = -> Pad010 [Edge291]
  BaseFeature = -> Pad010
  ChamferType = 1
  FlipDirection = false
  Refine = true
  Size = 1
  Size2 = 6
  SupportTransform = false
  Suppressed = false
  UseAllEdges = false
FEATURE [Sketcher::SketchObject] Sketch110
  ArcFitTolerance = 1e-06
  AttachmentSupport = -> [Pad010]
  ExternalGeometry = -> [Sketch098]
  FullyConstrained = true
  MakeInternals = false
  MapMode = 5
  Placement = pos=(0,4,-9e-16) rot=(0,0.707107,0.707107;3.14159rad)
  sketch-geometry (8):
    g0: LineSegment StartX=119.69 StartY=34 StartZ=0 EndX=130.69 EndY=34 EndZ=0
    g1: LineSegment StartX=119.95 StartY=33.2 StartZ=0 EndX=130.95 EndY=33.2 EndZ=0
    g2: LineSegment StartX=119.137 StartY=35.7 StartZ=0 EndX=130.137 EndY=35.7 EndZ=0
    g3: LineSegment StartX=118.877 StartY=36.5 StartZ=0 EndX=129.877 EndY=36.5 EndZ=0
    g4: LineSegment StartX=118.877 StartY=36.5 StartZ=0 EndX=119.137 EndY=35.7 EndZ=0
    g5: LineSegment StartX=129.877 StartY=36.5 StartZ=0 EndX=130.137 EndY=35.7 EndZ=0
    g6: LineSegment StartX=119.69 StartY=34 StartZ=0 EndX=119.95 EndY=33.2 EndZ=0
    g7: LineSegment StartX=130.69 StartY=34 StartZ=0 EndX=130.95 EndY=33.2 EndZ=0
  constraints (24):
    c: Horizontal(g0)
    c: Horizontal(g1)
    c: Horizontal(g2)
    c: Horizontal(g3)
    c: Equal(g1,g-5)
    c: Equal(g0,g-5)
    c: Equal(g2,g-5)
    c: Equal(g3,g-5)
    c: PointOnObject(g0,g-3)
    c: PointOnObject(g1,g-3)
    c: PointOnObject(g2,g-3)
    c: PointOnObject(g3,g-3)
    c: Coincident(g4,g3)
    c: Coincident(g4,g2)
    c: Coincident(g5,g3)
    c: Coincident(g5,g2)
    c: Coincident(g6,g0)
    c: Coincident(g6,g1)
    c: Coincident(g7,g0)
    c: Coincident(g7,g1)
    c: DistanceY(g1,g0) = 0.8
    c: DistanceY(g2,g3) = 0.8
    c: DistanceY(g-5,g1) = 2
    c: DistanceY(g-5,g2) = 4.5
FEATURE [PartDesign::Pocket] Pocket003
  BaseFeature = -> Chamfer006
  Direction = (0,-1,2e-16)
  Length = 1
  Length2 = 5
  Profile = -> Sketch110
  ReferenceAxis = -> Sketch110 [N_Axis]
  Refine = true
  Suppressed = false
  Type = 0
FEATURE [PartDesign::SubtractivePipe] SubtractivePipe
  AuxilleryCurvelinear = true
  AuxillerySpineTangent = false
  BaseFeature = -> Pocket003
  Binormal = (0,0,0)
  Mode = 0
  Profile = -> Sketch106
  Refine = true
  Spine = -> Pad008 [Edge215]
  SpineTangent = false
  Suppressed = false
  Transformation = 0
  Transition = 0
FEATURE [PartDesign::SubtractivePipe] SubtractivePipe001
  AuxilleryCurvelinear = true
  AuxillerySpineTangent = false
  BaseFeature = -> SubtractivePipe
  Binormal = (0,0,0)
  Mode = 0
  Profile = -> Sketch107
  Refine = true
  Spine = -> Pad008 [Edge213,Edge216,Edge210]
  SpineTangent = false
  Suppressed = false
  Transformation = 0
  Transition = 0
FEATURE [PartDesign::SubtractiveLoft] SubtractiveLoft
  BaseFeature = -> SubtractivePipe001
  Closed = false
  Profile = -> Sketch099
  Refine = true
  Ruled = false
  Sections = -> [Sketch108]
  Suppressed = false
FEATURE [PartDesign::SubtractiveLoft] SubtractiveLoft001
  BaseFeature = -> SubtractiveLoft
  Closed = false
  Profile = -> Clone2D
  Refine = true
  Ruled = false
  Sections = -> [Sketch109]
  Suppressed = false
FEATURE [Sketcher::SketchObject] Sketch112
  ArcFitTolerance = 1e-06
  AttachmentSupport = -> [Pad008]
  ExternalGeometry = -> [Binder]
  FullyConstrained = true
  MakeInternals = false
  MapMode = 5
  Placement = pos=(0,3.6,0) rot=(0,0.707107,0.707107;3.14159rad)
  sketch-geometry (4):
    g0: LineSegment [constr] StartX=167.782 StartY=-53.0314 StartZ=0 EndX=215.42 EndY=-53.0314 EndZ=0
    g1: GeomPoint [constr] X=191.282 Y=-53.0314 Z=0
    g2: Circle CenterX=191.282 CenterY=-53.0314 CenterZ=0 NormalX=0 NormalY=0 NormalZ=1 AngleXU=0 Radius=11.5
    g3: Circle CenterX=191.282 CenterY=-53.0314 CenterZ=0 NormalX=0 NormalY=0 NormalZ=1 AngleXU=0 Radius=10.7
  constraints (9):
    c: Horizontal(g0)
    c: PointOnObject(g0,g-3)
    c: Diameter(g2) = 23
    c: Coincident(g2,g1)
    c: Diameter(g3) = 21.4
    c: Coincident(g3,g1)
    c: DistanceX(g0,g1) = 23.5
    c: PointOnObject(g1,g0)
    c: Coincident(g0,g-4)
FEATURE [PartDesign::Chamfer] Chamfer016
  Angle = 45
  Base = -> SubtractiveLoft001 [Edge118,Edge117,Edge119,Edge120,Edge109]
  BaseFeature = -> SubtractiveLoft001
  ChamferType = 0
  FlipDirection = false
  Refine = true
  Size = 1.5
  Size2 = 1
  SupportTransform = false
  Suppressed = false
  UseAllEdges = false
FEATURE [PartDesign::Chamfer] Chamfer017
  Angle = 45
  Base = -> Chamfer016 [Edge15]
  BaseFeature = -> Chamfer016
  ChamferType = 0
  FlipDirection = false
  Refine = true
  Size = 1.6
  Size2 = 1
  SupportTransform = false
  Suppressed = false
  UseAllEdges = false
FEATURE [PartDesign::Chamfer] Chamfer018
  Angle = 45
  Base = -> Chamfer017 [Edge10]
  BaseFeature = -> Chamfer017
  ChamferType = 0
  FlipDirection = false
  Refine = true
  Size = 3.5
  Size2 = 1
  SupportTransform = false
  Suppressed = false
  UseAllEdges = false
FEATURE [PartDesign::Chamfer] Chamfer019
  Angle = 45
  Base = -> Chamfer018 [Edge94]
  BaseFeature = -> Chamfer018
  ChamferType = 0
  FlipDirection = false
  Refine = true
  Size = 1.9
  Size2 = 1
  SupportTransform = false
  Suppressed = false
  UseAllEdges = false
FEATURE [PartDesign::Fillet] Fillet009
  Base = -> Chamfer019 [Edge83]
  BaseFeature = -> Chamfer019
  Radius = 1.1
  Refine = true
  SupportTransform = false
  Suppressed = false
  UseAllEdges = false
FEATURE [PartDesign::Fillet] Fillet010
  Base = -> Fillet009 [Edge77]
  BaseFeature = -> Fillet009
  Radius = 1.9
  Refine = true
  SupportTransform = false
  Suppressed = false
  UseAllEdges = false
FEATURE [PartDesign::Pocket] Pocket005
  BaseFeature = -> Fillet010
  Direction = (0,-1,2e-16)
  Length = 0.8
  Length2 = 5
  Profile = -> Sketch112
  ReferenceAxis = -> Sketch112 [N_Axis]
  Refine = true
  Suppressed = false
  Type = 0
FEATURE [Part::Part2DObjectPython] ShapeString001  # Draft 2D object (typed FeaturePython)
  FontFile = <path>
  Fuse = false
  Justification = 6
  JustificationReference = 0
  KeepLeftMargin = false
  MakeFace = true
  ObliqueAngle = 0
  Placement = pos=(-183.5,3.6,-57.5) rot=(0,0.707107,0.707107;3.14159rad)
  ScaleToSize = true
  Size = 10
  String = AS
  Tracking = 0
FEATURE [PartDesign::Pocket] Pocket013
  BaseFeature = -> Pocket005
  Direction = (-1e-16,-1,2e-16)
  Length = 1
  Length2 = 5
  Profile = -> ShapeString001
  ReferenceAxis = -> ShapeString001 [N_Axis]
  Refine = true
  Suppressed = false
  Type = 0
FEATURE [PartDesign::Pad] Pad020
  Direction = (0,-1,2e-16)
  Length = 25.2
  Length2 = 10
  Midplane = true
  Placement = pos=(0,0,0) rot=(1,0,0;1.5708rad)
  Profile = -> Sketch021
  ReferenceAxis = -> Sketch021 [N_Axis]
  Refine = true
  Suppressed = false
  Type = 0
FEATURE [PartDesign::Body] Body001  label="perno fermo rumble e driver solenoide"
  AllowCompound = false
  Group = -> [Sketch021,Pad020]
  Origin = -> Origin001
  Tip = -> Pad020
FEATURE [PartDesign::Pad] Pad021
  Direction = (0,-1,2e-16)
  Length = 16.8
  Length2 = 10
  Midplane = true
  Placement = pos=(0,0,0) rot=(1,0,0;1.5708rad)
  Profile = -> Sketch061
  ReferenceAxis = -> Sketch061 [N_Axis]
  Refine = true
  Suppressed = false
  Type = 0
FEATURE [PartDesign::Pocket] Pocket014
  BaseFeature = -> Pad021
  Direction = (0,1,-2e-16)
  Length = 12.8
  Length2 = 5
  Midplane = true
  Placement = pos=(0,0,0) rot=(1,0,0;1.5708rad)
  Profile = -> Sketch062
  ReferenceAxis = -> Sketch062 [N_Axis]
  Refine = true
  Suppressed = false
  Type = 0
FEATURE [PartDesign::Pad] Pad022
  BaseFeature = -> Pocket014
  Direction = (0,-1,2e-16)
  Length = 7.6
  Length2 = 10
  Midplane = true
  Placement = pos=(0,0,0) rot=(1,0,0;1.5708rad)
  Profile = -> Sketch063
  ReferenceAxis = -> Sketch063 [N_Axis]
  Refine = true
  Suppressed = false
  Type = 0
FEATURE [PartDesign::Body] Body003  label="blocco switch"
  AllowCompound = false
  Group = -> [Sketch061,Sketch062,Sketch063,Pad021,Pocket014,Pad022]
  Origin = -> Origin003
  Tip = -> Pad022
FEATURE [PartDesign::Pad] Pad024
  Direction = (0,-1,2e-16)
  Length = 17
  Length2 = 10
  Midplane = true
  Placement = pos=(0,0,0) rot=(1,0,0;1.5708rad)
  Profile = -> Sketch045
  ReferenceAxis = -> Sketch045 [N_Axis]
  Refine = true
  Suppressed = false
  Type = 0
FEATURE [PartDesign::Pocket] Pocket015
  BaseFeature = -> Pad024
  Direction = (-1,0,0)
  Length = 8
  Length2 = 5
  Placement = pos=(0,0,0) rot=(1,0,0;1.5708rad)
  Profile = -> Sketch047
  ReferenceAxis = -> Sketch047 [N_Axis]
  Refine = true
  Reversed = true
  Suppressed = false
  Type = 0
FEATURE [PartDesign::Pocket] Pocket016
  BaseFeature = -> Pocket015
  Direction = (-1,0,0)
  Length = 1
  Length2 = 5
  Placement = pos=(0,0,0) rot=(1,0,0;1.5708rad)
  Profile = -> Sketch046
  ReferenceAxis = -> Sketch046 [N_Axis]
  Refine = true
  Reversed = true
  Suppressed = false
  Type = 0
FEATURE [PartDesign::Pocket] Pocket017
  BaseFeature = -> Pocket016
  Direction = (0,1,-2e-16)
  Length = 17
  Length2 = 5
  Midplane = true
  Placement = pos=(0,0,0) rot=(1,0,0;1.5708rad)
  Profile = -> Sketch048
  ReferenceAxis = -> Sketch048 [N_Axis]
  Refine = true
  Suppressed = false
  Type = 0
FEATURE [PartDesign::Pad] Pad025
  BaseFeature = -> Pocket017
  Direction = (0,-1,2e-16)
  Length = 17
  Length2 = 10
  Midplane = true
  Placement = pos=(0,0,0) rot=(1,0,0;1.5708rad)
  Profile = -> Sketch049
  ReferenceAxis = -> Sketch049 [N_Axis]
  Refine = true
  Suppressed = false
  Type = 0
FEATURE [PartDesign::Pad] Pad026
  BaseFeature = -> Pad025
  Direction = (0,-1,2e-16)
  Length = 17
  Length2 = 10
  Midplane = true
  Placement = pos=(0,0,0) rot=(1,0,0;1.5708rad)
  Profile = -> Sketch066
  ReferenceAxis = -> Sketch066 [N_Axis]
  Refine = true
  Suppressed = false
  Type = 0
FEATURE [PartDesign::Pad] Pad027
  BaseFeature = -> Pad026
  Direction = (0,-1,2e-16)
  Length = 5
  Length2 = 10
  Midplane = true
  Placement = pos=(0,0,0) rot=(1,0,0;1.5708rad)
  Profile = -> Sketch064
  ReferenceAxis = -> Sketch064 [N_Axis]
  Refine = true
  Suppressed = false
  Type = 0
FEATURE [PartDesign::Pad] Pad028
  BaseFeature = -> Pad027
  Direction = (1,0,0)
  Length = 1
  Length2 = 10
  Placement = pos=(0,0,0) rot=(1,0,0;1.5708rad)
  Profile = -> Sketch068
  ReferenceAxis = -> Sketch068 [N_Axis]
  Refine = true
  Reversed = true
  Suppressed = false
  Type = 0
FEATURE [PartDesign::Chamfer] Chamfer020
  Angle = 45
  Base = -> Pad028 [Edge73,Edge75,Edge78,Edge77]
  BaseFeature = -> Pad028
  ChamferType = 0
  FlipDirection = false
  Placement = pos=(0,0,0) rot=(1,0,0;1.5708rad)
  Refine = true
  Size = 0.5
  Size2 = 1
  SupportTransform = false
  Suppressed = false
  UseAllEdges = false
FEATURE [PartDesign::Body] Body002  label="supporto per neopixel"
  AllowCompound = false
  Group = -> [Sketch045,Sketch047,Sketch046,Sketch048,Sketch049,Sketch066,Sketch064,Sketch068,Pad024,Pocket015,Pocket016,Pocket017,Pad025,Pad026,Pad027,Pad028,Chamfer020]
  Origin = -> Origin002
  Tip = -> Chamfer020
FEATURE [Sketcher::SketchObject] Sketch134  label="perno fermo rumble002"
  ArcFitTolerance = 1e-06
  AttachmentSupport = -> [XZ_Plane008]
  FullyConstrained = true
  MakeInternals = false
  MapMode = 5
  Placement = pos=(0,0,0) rot=(1,0,0;1.5708rad)
  sketch-geometry (16):
    g0: LineSegment StartX=0 StartY=0.45 StartZ=0 EndX=0 EndY=1.55 EndZ=0
    g1: LineSegment StartX=0.45 StartY=2 StartZ=0 EndX=1.55 EndY=2 EndZ=0
    g2: LineSegment StartX=2 StartY=1.55 StartZ=0 EndX=2 EndY=0.45 EndZ=0
    g3: LineSegment StartX=1.55 StartY=0 StartZ=0 EndX=0.45 EndY=0 EndZ=0
    g4: ArcOfCircle [constr] CenterX=0.45 CenterY=1.55 CenterZ=0 NormalX=0 NormalY=0 NormalZ=1 AngleXU=0 Radius=0.45 StartAngle=1.5708 EndAngle=3.14159
    g5: GeomPoint [constr] X=0 Y=2 Z=0
    g6: LineSegment StartX=0.45 StartY=2 StartZ=0 EndX=0 EndY=1.55 EndZ=0
    g7: ArcOfCircle [constr] CenterX=1.55 CenterY=1.55 CenterZ=0 NormalX=0 NormalY=0 NormalZ=1 AngleXU=0 Radius=0.45 StartAngle=0 EndAngle=1.5708
    g8: GeomPoint [constr] X=2 Y=2 Z=0
    g9: LineSegment StartX=2 StartY=1.55 StartZ=0 EndX=1.55 EndY=2 EndZ=0
    g10: ArcOfCircle [constr] CenterX=1.55 CenterY=0.45 CenterZ=0 NormalX=0 NormalY=0 NormalZ=1 AngleXU=0 Radius=0.45 StartAngle=4.71239 EndAngle=6.28319
    g11: GeomPoint [constr] X=2 Y=0 Z=0
    g12: LineSegment StartX=1.55 StartY=0 StartZ=0 EndX=2 EndY=0.45 EndZ=0
    g13: ArcOfCircle [constr] CenterX=0.45 CenterY=0.45 CenterZ=0 NormalX=0 NormalY=0 NormalZ=1 AngleXU=0 Radius=0.45 StartAngle=3.14159 EndAngle=4.71239
    g14: GeomPoint [constr] X=0 Y=0 Z=0
    g15: LineSegment StartX=0 StartY=0.45 StartZ=0 EndX=0.45 EndY=0 EndZ=0
  constraints (35):
    c: Coincident(g14,g-1)
    c: PointOnObject(g5,g-2)
    c: Horizontal(g1)
    c: Vertical(g2)
    c: Horizontal(g3)
    c: DistanceX(g5,g8) = 2
    c: DistanceY(g11,g8) = 2
    c: PointOnObject(g5,g0)
    c: PointOnObject(g5,g1)
    c: Tangent(g0,g4) = 1.5708
    c: Tangent(g1,g4) = 1.5708
    c: Coincident(g6,g0)
    c: Coincident(g6,g1)
    c: PointOnObject(g8,g2)
    c: PointOnObject(g8,g1)
    c: Tangent(g2,g7) = 1.5708
    c: Tangent(g1,g7) = 1.5708
    c: Coincident(g9,g2)
    c: Coincident(g9,g1)
    c: PointOnObject(g11,g2)
    c: PointOnObject(g11,g3)
    c: Tangent(g2,g10) = 1.5708
    c: Tangent(g3,g10) = 1.5708
    c: Coincident(g12,g2)
    c: Coincident(g12,g3)
    c: PointOnObject(g14,g0)
    c: PointOnObject(g14,g3)
    c: Tangent(g0,g13) = 1.5708
    c: Tangent(g3,g13) = 1.5708
    c: Coincident(g15,g0)
    c: Coincident(g15,g3)
    c: Equal(g6,g9)
    c: Equal(g9,g12)
    c: Equal(g12,g15)
    c: DistanceX(g14,g3) = 0.45
FEATURE [PartDesign::Pad] Pad029
  Direction = (0,-1,2e-16)
  Length = 17
  Length2 = 10
  Midplane = true
  Placement = pos=(0,0,0) rot=(1,0,0;1.5708rad)
  Profile = -> Sketch134
  ReferenceAxis = -> Sketch134 [N_Axis]
  Refine = true
  Suppressed = false
  Type = 0
FEATURE [PartDesign::Body] Body008  label="perno fermo neopixel"
  AllowCompound = false
  Group = -> [Sketch134,Pad029]
  Origin = -> Origin008
  Tip = -> Pad029
FEATURE [Sketcher::SketchObject] Sketch135  label="perno fermo rumble003"
  ArcFitTolerance = 1e-06
  AttachmentSupport = -> [XZ_Plane009]
  FullyConstrained = true
  MakeInternals = false
  MapMode = 5
  Placement = pos=(0,0,0) rot=(1,0,0;1.5708rad)
  sketch-geometry (16):
    g0: LineSegment StartX=4.69e-14 StartY=0.8 StartZ=0 EndX=-3.04e-14 EndY=3.1 EndZ=0
    g1: LineSegment StartX=0.8 StartY=3.9 StartZ=0 EndX=3.1 EndY=3.9 EndZ=0
    g2: LineSegment StartX=3.9 StartY=3.1 StartZ=0 EndX=3.9 EndY=0.8 EndZ=0
    g3: LineSegment StartX=3.1 StartY=0 StartZ=0 EndX=0.8 EndY=0 EndZ=0
    g4: ArcOfCircle [constr] CenterX=0.8 CenterY=3.1 CenterZ=0 NormalX=0 NormalY=0 NormalZ=1 AngleXU=0 Radius=0.8 StartAngle=1.5708 EndAngle=3.14159
    g5: GeomPoint [constr] X=0 Y=3.9 Z=0
    g6: LineSegment StartX=0.8 StartY=3.9 StartZ=0 EndX=-3.04e-14 EndY=3.1 EndZ=0
    g7: ArcOfCircle [constr] CenterX=3.1 CenterY=3.1 CenterZ=0 NormalX=0 NormalY=0 NormalZ=1 AngleXU=0 Radius=0.8 StartAngle=-2.4e-14 EndAngle=1.5708
    g8: GeomPoint [constr] X=3.9 Y=3.9 Z=0
    g9: LineSegment StartX=3.9 StartY=3.1 StartZ=0 EndX=3.1 EndY=3.9 EndZ=0
    g10: ArcOfCircle [constr] CenterX=3.1 CenterY=0.8 CenterZ=0 NormalX=0 NormalY=0 NormalZ=1 AngleXU=0 Radius=0.8 StartAngle=4.71239 EndAngle=6.28319
    g11: GeomPoint [constr] X=3.9 Y=0 Z=0
    g12: LineSegment StartX=3.1 StartY=0 StartZ=0 EndX=3.9 EndY=0.8 EndZ=0
    g13: ArcOfCircle [constr] CenterX=0.8 CenterY=0.8 CenterZ=0 NormalX=0 NormalY=0 NormalZ=1 AngleXU=0 Radius=0.8 StartAngle=3.14159 EndAngle=4.71239
    g14: GeomPoint [constr] X=0 Y=0 Z=0
    g15: LineSegment StartX=4.69e-14 StartY=0.8 StartZ=0 EndX=0.8 EndY=0 EndZ=0
  constraints (35):
    c: Coincident(g14,g-1)
    c: PointOnObject(g5,g-2)
    c: Horizontal(g1)
    c: Vertical(g2)
    c: Horizontal(g3)
    c: DistanceX(g5,g8) = 3.9
    c: DistanceY(g11,g8) = 3.9
    c: PointOnObject(g5,g0)
    c: PointOnObject(g5,g1)
    c: Tangent(g0,g4) = 1.5708
    c: Tangent(g1,g4) = 1.5708
    c: Coincident(g6,g0)
    c: Coincident(g6,g1)
    c: PointOnObject(g8,g2)
    c: PointOnObject(g8,g1)
    c: Tangent(g2,g7) = 1.5708
    c: Tangent(g1,g7) = 1.5708
    c: Coincident(g9,g2)
    c: Coincident(g9,g1)
    c: PointOnObject(g11,g2)
    c: PointOnObject(g11,g3)
    c: Tangent(g2,g10) = 1.5708
    c: Tangent(g3,g10) = 1.5708
    c: Coincident(g12,g2)
    c: Coincident(g12,g3)
    c: PointOnObject(g14,g0)
    c: PointOnObject(g14,g3)
    c: Tangent(g0,g13) = 1.5708
    c: Tangent(g3,g13) = 1.5708
    c: Coincident(g15,g0)
    c: Coincident(g15,g3)
    c: Equal(g6,g9)
    c: Equal(g9,g12)
    c: Equal(g12,g15)
    c: DistanceX(g14,g3) = 0.8
FEATURE [PartDesign::Pad] Pad030
  Direction = (0,-1,2e-16)
  Length = 25.2
  Length2 = 10
  Midplane = true
  Placement = pos=(0,0,0) rot=(1,0,0;1.5708rad)
  Profile = -> Sketch135
  ReferenceAxis = -> Sketch135 [N_Axis]
  Refine = true
  Suppressed = false
  Type = 0
FEATURE [PartDesign::Body] Body009  label="perno fermo switch - caricabatterie - grilletto"
  AllowCompound = false
  Group = -> [Sketch135,Pad030]
  Origin = -> Origin009
  Tip = -> Pad030
FEATURE [Sketcher::SketchObject] Sketch136  label="scavo_rele"
  ArcFitTolerance = 1e-06
  AttachmentSupport = -> [XZ_Plane]
  ExternalGeometry = -> [Sketch]
  FullyConstrained = true
  MakeInternals = false
  MapMode = 5
  Placement = pos=(0,0,0) rot=(1,0,0;1.5708rad)
  sketch-geometry (7):
    g0: LineSegment [constr] StartX=-172.456 StartY=-60.9321 StartZ=0 EndX=-176.597 EndY=-73.6763 EndZ=0
    g1: LineSegment [constr] StartX=-172.456 StartY=-60.9321 StartZ=0 EndX=-170.364 EndY=-61.612 EndZ=0
    g2: LineSegment [constr] StartX=-172.456 StartY=-60.9321 StartZ=0 EndX=-176.07 EndY=-59.7579 EndZ=0
    g3: LineSegment StartX=-176.07 StartY=-59.7579 StartZ=0 EndX=-170.364 EndY=-61.612 EndZ=0
    g4: LineSegment StartX=-176.07 StartY=-59.7579 StartZ=0 EndX=-180.211 EndY=-72.502 EndZ=0
    g5: LineSegment StartX=-170.364 StartY=-61.612 StartZ=0 EndX=-174.505 EndY=-74.3561 EndZ=0
    g6: LineSegment StartX=-180.211 StartY=-72.502 StartZ=0 EndX=-174.505 EndY=-74.3561 EndZ=0
  constraints (19):
    c: Tangent(g0,g-3)
    c: Distance(g0,g-3) = 87.2
    c: Distance(g0,g0) = 13.4
    c: Coincident(g1,g0)
    c: Coincident(g2,g0)
    c: Distance(g2) = 3.8
    c: Distance(g1) = 2.2
    c: Perpendicular(g0,g1)
    c: Perpendicular(g0,g2)
    c: Coincident(g3,g2)
    c: Coincident(g3,g1)
    c: Equal(g4,g0)
    c: Equal(g5,g0)
    c: Parallel(g4,g0)
    c: Parallel(g5,g0)
    c: Coincident(g4,g2)
    c: Coincident(g5,g1)
    c: Coincident(g6,g4)
    c: Coincident(g6,g5)
FEATURE [Part::Extrusion] Extrude076  label="Extrude076 - scavo_rele"
  Base = -> Sketch136
  Dir = (0,-1,2e-16)
  DirMode = 2
  FaceMakerClass = Part::FaceMakerBullseye
  FaceMakerMode = 3
  LengthFwd = 18.2
  LengthRev = 0
  Solid = true
  Symmetric = true
FEATURE [Sketcher::SketchObject] Sketch137  label="scavo_nuovo_driver"
  ArcFitTolerance = 1e-06
  AttachmentSupport = -> [XZ_Plane]
  ExternalGeometry = -> [Sketch]
  FullyConstrained = true
  MakeInternals = false
  MapMode = 5
  Placement = pos=(0,0,0) rot=(1,0,0;1.5708rad)
  sketch-geometry (7):
    g0: LineSegment [constr] StartX=-160.034 StartY=-22.6997 StartZ=0 EndX=-164.854 EndY=-37.5361 EndZ=0
    g1: LineSegment [constr] StartX=-160.034 StartY=-22.6997 StartZ=0 EndX=-156.99 EndY=-23.6885 EndZ=0
    g2: LineSegment [constr] StartX=-160.034 StartY=-22.6997 StartZ=0 EndX=-163.648 EndY=-21.5254 EndZ=0
    g3: LineSegment StartX=-163.648 StartY=-21.5254 StartZ=0 EndX=-156.99 EndY=-23.6885 EndZ=0
    g4: LineSegment StartX=-163.648 StartY=-21.5254 StartZ=0 EndX=-168.468 EndY=-36.3619 EndZ=0
    g5: LineSegment StartX=-156.99 StartY=-23.6885 StartZ=0 EndX=-161.811 EndY=-38.525 EndZ=0
    g6: LineSegment StartX=-168.468 StartY=-36.3619 StartZ=0 EndX=-161.811 EndY=-38.525 EndZ=0
  constraints (19):
    c: Distance(g0,g-3) = 47
    c: Distance(g0) = 15.6
    c: Tangent(g0,g-3)
    c: Coincident(g1,g0)
    c: Coincident(g2,g0)
    c: Distance(g1) = 3.2
    c: Distance(g2) = 3.8
    c: Perpendicular(g0,g1)
    c: Perpendicular(g0,g2)
    c: Coincident(g3,g2)
    c: Coincident(g3,g1)
    c: Equal(g4,g0)
    c: Equal(g5,g0)
    c: Parallel(g4,g0)
    c: Parallel(g5,g0)
    c: Coincident(g4,g2)
    c: Coincident(g5,g1)
    c: Coincident(g6,g4)
    c: Coincident(g6,g5)
FEATURE [Part::Extrusion] Extrude077  label="Extrude077 - scavo_nuovo_driver"
  Base = -> Sketch137
  Dir = (0,-1,2e-16)
  DirMode = 2
  FaceMakerClass = Part::FaceMakerBullseye
  FaceMakerMode = 3
  LengthFwd = 20.8
  LengthRev = 0
  Solid = true
  Symmetric = true
FEATURE [Sketcher::SketchObject] Sketch138  label="scavo_nuovo_driver_alto"
  ArcFitTolerance = 1e-06
  AttachmentSupport = -> [XZ_Plane]
  ExternalGeometry = -> [Sketch]
  FullyConstrained = true
  MakeInternals = false
  MapMode = 5
  Placement = pos=(0,0,0) rot=(1,0,0;1.5708rad)
  sketch-geometry (7):
    g0: LineSegment [constr] StartX=-188.796 StartY=17.7274 StartZ=0 EndX=-187.75 EndY=4.97025 EndZ=0
    g1: LineSegment StartX=-187.75 StartY=4.97025 StartZ=0 EndX=-189.743 EndY=4.8067 EndZ=0
    g2: LineSegment StartX=-187.75 StartY=4.97025 StartZ=0 EndX=-182.766 EndY=5.37913 EndZ=0
    g3: LineSegment StartX=-190.79 StartY=17.5638 StartZ=0 EndX=-189.743 EndY=4.8067 EndZ=0
    g4: LineSegment StartX=-183.813 StartY=18.1363 StartZ=0 EndX=-182.766 EndY=5.37913 EndZ=0
    g5: LineSegment StartX=-190.79 StartY=17.5638 StartZ=0 EndX=-188.796 EndY=17.7274 EndZ=0
    g6: LineSegment StartX=-188.796 StartY=17.7274 StartZ=0 EndX=-183.813 EndY=18.1363 EndZ=0
  constraints (20):
    c: Distance(g0) = 12.8
    c: DistanceY(g-3,g0) = 9
    c: PointOnObject(g0,g-4)
    c: PointOnObject(g0,g-4)
    c: Coincident(g1,g0)
    c: Coincident(g2,g0)
    c: Distance(g1) = 2
    c: Distance(g2) = 5
    c: Perpendicular(g0,g1)
    c: Perpendicular(g0,g2)
    c: Equal(g3,g0)
    c: Parallel(g3,g0)
    c: Coincident(g3,g1)
    c: Equal(g4,g0)
    c: Parallel(g4,g0)
    c: Coincident(g4,g2)
    c: Coincident(g5,g3)
    c: Coincident(g5,g0)
    c: Coincident(g6,g0)
    c: Coincident(g6,g4)
FEATURE [Part::Extrusion] Extrude078  label="Extrude078 - scavo_nuovo_driver_alto"
  Base = -> Sketch138
  Dir = (0,-1,2e-16)
  DirMode = 2
  FaceMakerClass = Part::FaceMakerBullseye
  FaceMakerMode = 3
  LengthFwd = 16.6
  LengthRev = 0
  Solid = true
  Symmetric = true
FEATURE [Sketcher::SketchObject] Sketch139  label="fermi_nuovo_driver_alto"
  ArcFitTolerance = 1e-06
  AttachmentSupport = -> [XZ_Plane]
  ExternalGeometry = -> [Sketch138,Sketch]
  FullyConstrained = true
  MakeInternals = false
  MapMode = 5
  Placement = pos=(0,0,0) rot=(1,0,0;1.5708rad)
  sketch-geometry (17):
    g0: LineSegment [constr] StartX=-188.314 StartY=16.4295 StartZ=0 EndX=-187.885 EndY=13.7638 EndZ=0
    g1: LineSegment [constr] StartX=-187.885 StartY=13.7638 StartZ=0 EndX=-187.456 EndY=11.0981 EndZ=0
    g2: LineSegment StartX=-187.885 StartY=13.7638 StartZ=0 EndX=-187.71 EndY=12.6778 EndZ=0
    g3: LineSegment StartX=-187.885 StartY=13.7638 StartZ=0 EndX=-188.06 EndY=14.8499 EndZ=0
    g4: LineSegment StartX=-187.71 StartY=12.6778 StartZ=0 EndX=-185.538 EndY=13.0274 EndZ=0
    g5: LineSegment StartX=-188.06 StartY=14.8499 StartZ=0 EndX=-185.888 EndY=15.1994 EndZ=0
    g6: LineSegment StartX=-185.888 StartY=15.1994 StartZ=0 EndX=-185.538 EndY=13.0274 EndZ=0
    g7: LineSegment StartX=-187.456 StartY=11.0981 StartZ=0 EndX=-189.035 EndY=10.8439 EndZ=0
    g8: LineSegment StartX=-188.314 StartY=16.4295 StartZ=0 EndX=-189.893 EndY=16.1753 EndZ=0
    g9: LineSegment StartX=-189.893 StartY=16.1753 StartZ=0 EndX=-189.035 EndY=10.8439 EndZ=0
    g10: LineSegment StartX=-187.456 StartY=11.0981 StartZ=0 EndX=-185.284 EndY=11.4477 EndZ=0
    g11: LineSegment StartX=-188.314 StartY=16.4295 StartZ=0 EndX=-186.142 EndY=16.7791 EndZ=0
    g12: LineSegment StartX=-184.308 StartY=15.4537 StartZ=0 EndX=-183.958 EndY=13.2816 EndZ=0
    g13: ArcOfCircle CenterX=-185.888 CenterY=15.1994 CenterZ=0 NormalX=0 NormalY=0 NormalZ=1 AngleXU=0 Radius=1.6 StartAngle=0.15957 EndAngle=1.73037
    g14: GeomPoint [constr] X=-184.562 Y=17.0333 Z=0
    g15: ArcOfCircle CenterX=-185.538 CenterY=13.0274 CenterZ=0 NormalX=0 NormalY=0 NormalZ=1 AngleXU=0 Radius=1.6 StartAngle=4.87196 EndAngle=6.44276
    g16: GeomPoint [constr] X=-183.704 Y=11.7019 Z=0
  constraints (43):
    c: Tangent(g1,g0) = -1.5708
    c: Distance(g0) = 2.7
    c: Equal(g1,g0)
    c: Tangent(g1,g-5)
    c: Coincident(g2,g0)
    c: Coincident(g3,g0)
    c: Distance(g2) = 1.1
    c: Equal(g3,g2)
    c: PointOnObject(g3,g2)
    c: Coincident(g4,g2)
    c: Coincident(g5,g3)
    c: Distance(g4) = 2.2
    c: Equal(g4,g5)
    c: Perpendicular(g1,g4)
    c: Perpendicular(g0,g5)
    c: Coincident(g6,g5)
    c: Coincident(g6,g4)
    c: Coincident(g7,g1)
    c: Coincident(g8,g0)
    c: Distance(g7) = 1.6
    c: Equal(g7,g8)
    c: Perpendicular(g1,g7)
    c: Perpendicular(g8,g0)
    c: Coincident(g9,g8)
    c: Coincident(g9,g7)
    c: Coincident(g10,g1)
    c: Coincident(g11,g0)
    c: Distance(g10,g16) = 3.8
    c: Perpendicular(g1,g10)
    c: Perpendicular(g1,g11)
    c: DistanceY(g0,g-4) = 3.8
    c: PointOnObject(g14,g12)
    c: PointOnObject(g14,g11)
    c: Tangent(g12,g13) = 1.5708
    c: Tangent(g11,g13) = 1.5708
    c: PointOnObject(g16,g12)
    c: PointOnObject(g16,g10)
    c: Tangent(g12,g15) = 1.5708
    c: Tangent(g10,g15) = -1.5708
    c: Equal(g13,g15)
    c: Coincident(g13,g5)
    c: Parallel(g2,g0)
    c: PointOnObject(g0,g-5)
FEATURE [Part::Extrusion] Extrude079  label="Extrude079 - fermi_nuovo_driver_alto"
  Base = -> Sketch139
  Dir = (0,-1,2e-16)
  DirMode = 2
  FaceMakerClass = Part::FaceMakerBullseye
  FaceMakerMode = 3
  LengthFwd = 25.2
  LengthRev = 0
  Solid = true
  Symmetric = true
FEATURE [Sketcher::SketchObject] Sketch140  label="scavo_diodo_nuovo_driver_alto"
  ArcFitTolerance = 1e-06
  AttachmentSupport = -> [XZ_Plane]
  ExternalGeometry = -> [Sketch138]
  FullyConstrained = true
  MakeInternals = false
  MapMode = 5
  Placement = pos=(0,0,0) rot=(1,0,0;1.5708rad)
  sketch-geometry (4):
    g0: LineSegment StartX=-190.79 StartY=17.5638 StartZ=0 EndX=-189.743 EndY=4.8067 EndZ=0
    g1: LineSegment StartX=-193.78 StartY=17.3185 StartZ=0 EndX=-192.733 EndY=4.56137 EndZ=0
    g2: LineSegment StartX=-190.79 StartY=17.5638 StartZ=0 EndX=-193.78 EndY=17.3185 EndZ=0
    g3: LineSegment StartX=-192.733 StartY=4.56137 StartZ=0 EndX=-189.743 EndY=4.8067 EndZ=0
  constraints (11):
    c: Equal(g0,g-3)
    c: Parallel(g0,g-3)
    c: Equal(g1,g-3)
    c: Parallel(g1,g-3)
    c: Coincident(g2,g0)
    c: Distance(g2) = 3
    c: Perpendicular(g0,g2)
    c: Coincident(g1,g2)
    c: Coincident(g3,g1)
    c: Coincident(g3,g0)
    c: Coincident(g0,g-3)
FEATURE [Part::Extrusion] Extrude080  label="Extrude080 - scavo_diodo_nuovo_driver_alto"
  Base = -> Sketch140
  Dir = (0,-1,2e-16)
  DirMode = 2
  FaceMakerClass = Part::FaceMakerBullseye
  FaceMakerMode = 3
  LengthFwd = 4
  LengthRev = 0
  Placement = pos=(0,7.8,0) rot=(0,0,1;0rad)
  Solid = true
  Symmetric = false
FEATURE [Part::MultiFuse] Fusion001
  Refine = true
  Shapes = -> [Cut043,Extrude079]
FEATURE [Part::Cut] Cut044
  Base = -> Fusion001
  Refine = true
  Tool = -> Extrude078
FEATURE [Part::Cut] Cut045
  Base = -> Cut044
  Refine = true
  Tool = -> Extrude080
FEATURE [Sketcher::SketchObject] Sketch141  label="fermi_nuovo_driver"
  ArcFitTolerance = 1e-06
  AttachmentSupport = -> [XZ_Plane]
  ExternalGeometry = -> [Sketch,Sketch137]
  FullyConstrained = true
  MakeInternals = false
  MapMode = 5
  Placement = pos=(0,0,0) rot=(1,0,0;1.5708rad)
  sketch-geometry (17):
    g0: LineSegment [constr] StartX=-156.99 StartY=-23.6885 StartZ=0 EndX=-160.034 EndY=-22.6997 EndZ=0
    g1: LineSegment [constr] StartX=-160.034 StartY=-22.6997 StartZ=0 EndX=-162.815 EndY=-31.2592 EndZ=0
    g2: LineSegment [constr] StartX=-162.815 StartY=-31.2592 StartZ=0 EndX=-164.484 EndY=-36.3949 EndZ=0
    g3: LineSegment StartX=-164.484 StartY=-36.3949 StartZ=0 EndX=-166.576 EndY=-35.715 EndZ=0
    g4: LineSegment StartX=-167.603 StartY=-33.6989 StartZ=0 EndX=-166.923 EndY=-31.6066 EndZ=0
    g5: LineSegment StartX=-164.907 StartY=-30.5793 StartZ=0 EndX=-161.293 EndY=-31.7536 EndZ=0
    g6: LineSegment StartX=-161.293 StartY=-31.7536 StartZ=0 EndX=-162.962 EndY=-36.8893 EndZ=0
    g7: LineSegment StartX=-164.484 StartY=-36.3949 StartZ=0 EndX=-162.962 EndY=-36.8893 EndZ=0
    g8: LineSegment StartX=-165.402 StartY=-32.101 StartZ=0 EndX=-166.082 EndY=-34.1933 EndZ=0
    g9: LineSegment StartX=-166.082 StartY=-34.1933 StartZ=0 EndX=-163.989 EndY=-34.8732 EndZ=0
    g10: LineSegment StartX=-163.989 StartY=-34.8732 StartZ=0 EndX=-163.309 EndY=-32.7809 EndZ=0
    g11: LineSegment StartX=-163.309 StartY=-32.7809 StartZ=0 EndX=-165.402 EndY=-32.101 EndZ=0
    g12: ArcOfCircle CenterX=-165.402 CenterY=-32.101 CenterZ=0 NormalX=0 NormalY=0 NormalZ=1 AngleXU=0 Radius=1.6 StartAngle=1.25664 EndAngle=2.82743
    g13: GeomPoint [constr] X=-166.429 Y=-30.0849 Z=0
    g14: ArcOfCircle CenterX=-166.082 CenterY=-34.1933 CenterZ=0 NormalX=0 NormalY=0 NormalZ=1 AngleXU=0 Radius=1.6 StartAngle=2.82743 EndAngle=4.39823
    g15: GeomPoint [constr] X=-168.098 Y=-35.2206 Z=0
    g16: LineSegment [constr] StartX=-160.034 StartY=-22.6997 StartZ=0 EndX=-164.854 EndY=-37.5361 EndZ=0
  constraints (44):
    c: Coincident(g0,g-4)
    c: PointOnObject(g0,g-3)
    c: Parallel(g0,g-4)
    c: Coincident(g1,g0)
    c: Parallel(g1,g-3)
    c: Coincident(g2,g1)
    c: Distance(g2) = 5.4
    c: Coincident(g3,g2)
    c: Parallel(g2,g-3)
    c: Distance(g15,g13) = 5.4
    c: Perpendicular(g3,g2)
    c: Parallel(g4,g2)
    c: Distance(g5,g13) = 5.4
    c: Distance(g3,g15) = 3.8
    c: Perpendicular(g4,g5)
    c: Coincident(g6,g5)
    c: Distance(g6) = 5.4
    c: Parallel(g6,g4)
    c: Coincident(g7,g2)
    c: Coincident(g7,g6)
    c: Coincident(g8,g9)
    c: Coincident(g9,g10)
    c: Coincident(g10,g11)
    c: Coincident(g11,g8)
    c: Distance(g8,g10) = 2.2
    c: Distance(g9,g11) = 2.2
    c: Perpendicular(g11,g8)
    c: Equal(g8,g10)
    c: Equal(g11,g9)
    c: Tangent(g10,g2)
    c: Distance(g10,g1) = 1.6
    c: PointOnObject(g13,g4)
    c: PointOnObject(g13,g5)
    c: Tangent(g4,g12) = 1.5708
    c: Tangent(g5,g12) = 1.5708
    c: PointOnObject(g15,g4)
    c: Tangent(g4,g14) = 1.5708
    c: Tangent(g3,g14) = 1.5708
    c: Equal(g14,g12)
    c: Coincident(g12,g8)
    c: Coincident(g16,g0)
    c: PointOnObject(g16,g-5)
    c: Parallel(g16,g-3)
    c: Distance(g16,g2) = 1.2
FEATURE [Part::Extrusion] Extrude081  label="Extrude081 - fermi_nuovo_driver"
  Base = -> Sketch141
  Dir = (0,-1,2e-16)
  DirMode = 2
  FaceMakerClass = Part::FaceMakerBullseye
  FaceMakerMode = 3
  LengthFwd = 25.2
  LengthRev = 0
  Solid = true
  Symmetric = true
FEATURE [Part::MultiFuse] Fusion002
  Refine = true
  Shapes = -> [Cut045,Extrude081]
FEATURE [Part::Cut] Cut046
  Base = -> Fusion002
  Refine = true
  Tool = -> Extrude077
FEATURE [Sketcher::SketchObject] Sketch142  label="fermi_rele"
  ArcFitTolerance = 1e-06
  AttachmentSupport = -> [XZ_Plane]
  ExternalGeometry = -> [Sketch,Sketch136]
  FullyConstrained = true
  MakeInternals = false
  MapMode = 5
  Placement = pos=(0,0,0) rot=(1,0,0;1.5708rad)
  sketch-geometry (15):
    g0: LineSegment StartX=-176.936 StartY=-62.4208 StartZ=0 EndX=-177.615 EndY=-64.5131 EndZ=0
    g1: LineSegment StartX=-174.919 StartY=-61.3936 StartZ=0 EndX=-171.305 EndY=-62.5678 EndZ=0
    g2: LineSegment StartX=-171.305 StartY=-62.5678 StartZ=0 EndX=-172.974 EndY=-67.7035 EndZ=0
    g3: LineSegment StartX=-176.588 StartY=-66.5293 StartZ=0 EndX=-172.974 EndY=-67.7035 EndZ=0
    g4: LineSegment StartX=-175.414 StartY=-62.9152 StartZ=0 EndX=-173.322 EndY=-63.5951 EndZ=0
    g5: LineSegment StartX=-175.414 StartY=-62.9152 StartZ=0 EndX=-176.094 EndY=-65.0076 EndZ=0
    g6: LineSegment StartX=-173.322 StartY=-63.5951 StartZ=0 EndX=-174.001 EndY=-65.6874 EndZ=0
    g7: LineSegment StartX=-176.094 StartY=-65.0076 StartZ=0 EndX=-174.001 EndY=-65.6874 EndZ=0
    g8: LineSegment [constr] StartX=-173.322 StartY=-63.5951 StartZ=0 EndX=-172.827 EndY=-62.0734 EndZ=0
    g9: LineSegment [constr] StartX=-173.322 StartY=-63.5951 StartZ=0 EndX=-171.8 EndY=-64.0895 EndZ=0
    g10: LineSegment [constr] StartX=-170.364 StartY=-61.612 StartZ=0 EndX=-172.456 EndY=-60.9321 EndZ=0
    g11: ArcOfCircle CenterX=-175.414 CenterY=-62.9152 CenterZ=0 NormalX=0 NormalY=0 NormalZ=1 AngleXU=0 Radius=1.6 StartAngle=1.25664 EndAngle=2.82743
    g12: GeomPoint [constr] X=-176.441 Y=-60.8991 Z=0
    g13: ArcOfCircle CenterX=-176.094 CenterY=-65.0076 CenterZ=0 NormalX=0 NormalY=0 NormalZ=1 AngleXU=0 Radius=1.6 StartAngle=2.82743 EndAngle=4.39823
    g14: GeomPoint [constr] X=-178.11 Y=-66.0348 Z=0
  constraints (39):
    c: Distance(g14,g12) = 5.4
    c: Distance(g1,g12) = 5.4
    c: Perpendicular(g1,g0)
    c: Coincident(g2,g1)
    c: Parallel(g2,g0)
    c: Coincident(g3,g2)
    c: Parallel(g2,g-3)
    c: Coincident(g5,g4)
    c: Distance(g5) = 2.2
    c: Distance(g4) = 2.2
    c: Perpendicular(g4,g5)
    c: Coincident(g6,g4)
    c: Equal(g6,g5)
    c: Parallel(g6,g5)
    c: Coincident(g7,g5)
    c: Coincident(g7,g6)
    c: Coincident(g8,g4)
    c: Coincident(g9,g4)
    c: Distance(g8) = 1.6
    c: Distance(g9) = 1.6
    c: Parallel(g8,g6)
    c: Parallel(g9,g4)
    c: PointOnObject(g8,g1)
    c: PointOnObject(g9,g2)
    c: Coincident(g10,g-4)
    c: Parallel(g10,g-4)
    c: PointOnObject(g10,g-3)
    c: Tangent(g6,g-3) = 1.5708
    c: Distance(g4,g10) = 2.8
    c: PointOnObject(g12,g1)
    c: Tangent(g1,g11) = 1.5708
    c: Tangent(g0,g11) = -1.5708
    c: PointOnObject(g14,g3)
    c: PointOnObject(g14,g0)
    c: Tangent(g3,g13) = -1.5708
    c: Tangent(g0,g13) = -1.5708
    c: Equal(g11,g13)
    c: Coincident(g11,g4)
    c: Parallel(g3,g1)
FEATURE [Part::Extrusion] Extrude082  label="Extrude082 - fermi_rele"
  Base = -> Sketch142
  Dir = (0,-1,2e-16)
  DirMode = 2
  FaceMakerClass = Part::FaceMakerBullseye
  FaceMakerMode = 3
  LengthFwd = 25.2
  LengthRev = 0
  Solid = true
  Symmetric = true
FEATURE [Part::MultiFuse] Fusion003
  Refine = true
  Shapes = -> [Cut046,Extrude082]
FEATURE [Part::Cut] Cut047
  Base = -> Fusion003
  Refine = true
  Tool = -> Extrude076
FEATURE [Sketcher::SketchObject] Sketch143  label="foro_passaggio_cavi_led_batteria"
  ArcFitTolerance = 1e-06
  AttachmentSupport = -> [XZ_Plane]
  ExternalGeometry = -> [Sketch,Sketch042,Sketch036]
  FullyConstrained = true
  MakeInternals = false
  MapMode = 5
  Placement = pos=(0,0,0) rot=(1,0,0;1.5708rad)
  sketch-geometry (4):
    g0: LineSegment StartX=-207.775 StartY=-41.3701 StartZ=0 EndX=-213.607 EndY=-53.8767 EndZ=0
    g1: LineSegment StartX=-213.607 StartY=-53.8767 StartZ=0 EndX=-211.843 EndY=-59.5559 EndZ=0
    g2: LineSegment StartX=-207.775 StartY=-41.3701 StartZ=0 EndX=-207.775 EndY=-50.8316 EndZ=0
    g3: LineSegment StartX=-207.775 StartY=-50.8316 StartZ=0 EndX=-211.843 EndY=-59.5559 EndZ=0
  constraints (9):
    c: Coincident(g0,g-3)
    c: PointOnObject(g1,g-6)
    c: Coincident(g1,g0)
    c: Coincident(g2,g0)
    c: Coincident(g2,g-7)
    c: Coincident(g3,g2)
    c: Parallel(g3,g0)
    c: Coincident(g3,g1)
    c: Coincident(g0,g-5)
FEATURE [Part::Extrusion] Extrude083  label="Extrude083 - foro_passaggio_cavi_led_batteria"
  Base = -> Sketch143
  Dir = (0,-1,2e-16)
  DirMode = 2
  FaceMakerClass = Part::FaceMakerBullseye
  FaceMakerMode = 3
  LengthFwd = 6
  LengthRev = 0
  Solid = true
  Symmetric = true
FEATURE [Part::Cut] Cut048
  Base = -> Cut047
  Refine = true
  Tool = -> Extrude083
FEATURE [Sketcher::SketchObject] Sketch144  label="foro_areazione_alimentatore"
  ArcFitTolerance = 1e-06
  AttachmentSupport = -> [XZ_Plane]
  ExternalGeometry = -> [Sketch036]
  FullyConstrained = true
  MakeInternals = false
  MapMode = 5
  Placement = pos=(0,0,0) rot=(1,0,0;1.5708rad)
  sketch-geometry (4):
    g0: LineSegment StartX=-211.843 StartY=-60.3701 StartZ=0 EndX=-207.775 EndY=-60.3701 EndZ=0
    g1: LineSegment StartX=-207.775 StartY=-60.3701 StartZ=0 EndX=-207.775 EndY=-70.3701 EndZ=0
    g2: LineSegment StartX=-211.843 StartY=-60.3701 StartZ=0 EndX=-211.843 EndY=-70.3701 EndZ=0
    g3: LineSegment StartX=-207.775 StartY=-70.3701 StartZ=0 EndX=-211.843 EndY=-70.3701 EndZ=0
  constraints (11):
    c: Horizontal(g0)
    c: Distance(g1) = 10
    c: Coincident(g1,g0)
    c: Tangent(g1,g-3)
    c: PointOnObject(g0,g-4)
    c: Coincident(g2,g0)
    c: PointOnObject(g2,g-4)
    c: Coincident(g3,g1)
    c: Horizontal(g3)
    c: Coincident(g3,g2)
    c: DistanceY(g0,g-3) = 19
FEATURE [Part::Extrusion] Extrude084  label="Extrude084 - foro_areazione_alimentatore"
  Base = -> Sketch144
  Dir = (0,-1,2e-16)
  DirMode = 2
  FaceMakerClass = Part::FaceMakerBullseye
  FaceMakerMode = 3
  LengthFwd = 10
  LengthRev = 0
  Solid = true
  Symmetric = true
FEATURE [Part::Cut] Cut049
  Base = -> Cut048
  Refine = true
  Tool = -> Extrude084
FEATURE [Sketcher::SketchObject] Sketch145  label="foro_per_condesatore"
  ArcFitTolerance = 1e-06
  AttachmentSupport = -> [XZ_Plane]
  ExternalGeometry = -> [Sketch,Sketch139]
  FullyConstrained = true
  MakeInternals = false
  MapMode = 5
  Placement = pos=(0,0,0) rot=(1,0,0;1.5708rad)
  sketch-geometry (1):
    g0: Circle CenterX=-182.345 CenterY=7.02342 CenterZ=0 NormalX=0 NormalY=0 NormalZ=1 AngleXU=0 Radius=5.2
  constraints (3):
    c: Diameter(g0) = 10.4
    c: Tangent(g0,g-3)
    c: Tangent(g0,g-4)
FEATURE [Part::Extrusion] Extrude085  label="Extrude085 - foro_per_condesatore"
  Base = -> Sketch145
  Dir = (0,-1,2e-16)
  DirMode = 2
  FaceMakerClass = Part::FaceMakerBullseye
  FaceMakerMode = 3
  LengthFwd = 25.2
  LengthRev = 0
  Solid = true
  Symmetric = true
FEATURE [Part::Cut] Cut050
  Base = -> Cut049
  Refine = true
  Tool = -> Extrude085
FEATURE [Sketcher::SketchObject] Sketch146  label="scavo_pulsante_6x6_per_led_batteria"
  ArcFitTolerance = 1e-06
  AttachmentSupport = -> [XZ_Plane]
  ExternalGeometry = -> [Sketch016]
  FullyConstrained = true
  MakeInternals = false
  MapMode = 5
  Placement = pos=(0,0,0) rot=(1,0,0;1.5708rad)
  sketch-geometry (5):
    g0: LineSegment StartX=-216.643 StartY=-65.8316 StartZ=0 EndX=-216.643 EndY=-72.8316 EndZ=0
    g1: LineSegment StartX=-216.643 StartY=-72.8316 StartZ=0 EndX=-210.243 EndY=-72.8316 EndZ=0
    g2: LineSegment StartX=-210.243 StartY=-72.8316 StartZ=0 EndX=-210.243 EndY=-65.8316 EndZ=0
    g3: LineSegment StartX=-210.243 StartY=-65.8316 StartZ=0 EndX=-216.643 EndY=-65.8316 EndZ=0
    g4: GeomPoint [constr] X=-213.443 Y=-69.3316 Z=0
  constraints (13):
    c: Coincident(g0,g1)
    c: Coincident(g1,g2)
    c: Coincident(g2,g3)
    c: Coincident(g3,g0)
    c: Vertical(g0)
    c: Vertical(g2)
    c: Horizontal(g1)
    c: Horizontal(g3)
    c: Distance(g0,g2) = 6.4
    c: Distance(g1,g3) = 7
    c: Tangent(g1,g-3)
    c: Symmetric(g0,g2,g4)
    c: Vertical(g-3,g4)
FEATURE [Part::Extrusion] Extrude086  label="Extrude086 - scavo_pulsante_6x6_per_led_batteria"
  Base = -> Sketch146
  Dir = (0,-1,2e-16)
  DirMode = 2
  FaceMakerClass = Part::FaceMakerBullseye
  FaceMakerMode = 3
  LengthFwd = 4
  LengthRev = 0
  Placement = pos=(0,12.6,0) rot=(0,0,1;0rad)
  Solid = true
  Symmetric = false
FEATURE [Sketcher::SketchObject] Sketch147  label="scavo_led_stato_batteria"
  ArcFitTolerance = 1e-06
  AttachmentSupport = -> [XZ_Plane]
  ExternalGeometry = -> [Sketch016]
  FullyConstrained = true
  MakeInternals = false
  MapMode = 5
  Placement = pos=(0,0,0) rot=(1,0,0;1.5708rad)
  sketch-geometry (5):
    g0: LineSegment StartX=-215.843 StartY=-56.2316 StartZ=0 EndX=-215.843 EndY=-65.4316 EndZ=0
    g1: LineSegment StartX=-215.843 StartY=-65.4316 StartZ=0 EndX=-211.043 EndY=-65.4316 EndZ=0
    g2: LineSegment StartX=-211.043 StartY=-65.4316 StartZ=0 EndX=-211.043 EndY=-56.2316 EndZ=0
    g3: LineSegment StartX=-211.043 StartY=-56.2316 StartZ=0 EndX=-215.843 EndY=-56.2316 EndZ=0
    g4: GeomPoint [constr] X=-213.443 Y=-60.8316 Z=0
  constraints (13):
    c: Coincident(g0,g1)
    c: Coincident(g1,g2)
    c: Coincident(g2,g3)
    c: Coincident(g3,g0)
    c: Distance(g0,g2) = 4.8
    c: Distance(g1,g3) = 9.2
    c: Equal(g0,g2)
    c: Equal(g1,g3)
    c: Perpendicular(g3,g0)
    c: DistanceY(g-3,g0) = 11.4
    c: Vertical(g2)
    c: Symmetric(g0,g2,g4)
    c: Vertical(g4,g-3)
FEATURE [Part::Extrusion] Extrude087  label="Extrude087 - scavo_led_stato_batteria"
  Base = -> Sketch147
  Dir = (0,-1,2e-16)
  DirMode = 2
  FaceMakerClass = Part::FaceMakerBullseye
  FaceMakerMode = 3
  LengthFwd = 2.2
  LengthRev = 0
  Placement = pos=(0,12.6,0) rot=(0,0,1;0rad)
  Solid = true
  Symmetric = false
FEATURE [Sketcher::SketchObject] Sketch148
  ArcFitTolerance = 1e-06
  AttachmentSupport = -> [Pad016]
  ExternalGeometry = -> [Pad016]
  FullyConstrained = true
  MakeInternals = false
  MapMode = 5
  Placement = pos=(0,0,-80.4316) rot=(1,0,0;3.14159rad)
  sketch-geometry (8):
    g0: LineSegment StartX=-176.685 StartY=3.6 StartZ=0 EndX=-186.685 EndY=3.6 EndZ=0
    g1: LineSegment StartX=-176.685 StartY=3.6 StartZ=0 EndX=-176.685 EndY=-9e-16 EndZ=0
    g2: LineSegment [constr] StartX=-186.685 StartY=3.6 StartZ=0 EndX=-186.685 EndY=-9e-16 EndZ=0
    g3: ArcOfEllipse CenterX=-186.685 CenterY=-9e-16 CenterZ=0 NormalX=0 NormalY=0 NormalZ=1 MajorRadius=10 MinorRadius=3.6 AngleXU=0 StartAngle=0 EndAngle=1.5708
    g4: LineSegment [constr] StartX=-176.685 StartY=-1e-15 StartZ=0 EndX=-196.685 EndY=-1e-15 EndZ=0
    g5: LineSegment [constr] StartX=-186.685 StartY=3.6 StartZ=0 EndX=-186.685 EndY=-3.6 EndZ=0
    g6: GeomPoint [constr] X=-177.356 Y=-1e-15 Z=0
    g7: GeomPoint [constr] X=-196.015 Y=-1e-15 Z=0
  constraints (13):
    c: Distance(g0) = 10
    c: Coincident(g0,g-5)
    c: PointOnObject(g0,g-3)
    c: Coincident(g1,g0)
    c: Coincident(g1,g-5)
    c: Coincident(g2,g0)
    c: Vertical(g2)
    c: PointOnObject(g2,g-4)
    c: InternalAlignment(g4-g7 -> g3) x4
    c: Coincident(g3,g2)
    c: Coincident(g3,g0)
    c: Coincident(g3,g1)
    c: Horizontal(g4)
FEATURE [PartDesign::SubtractivePipe] SubtractivePipe004
  AuxilleryCurvelinear = true
  AuxillerySpineTangent = false
  BaseFeature = -> Pad016
  Binormal = (0,0,0)
  Mode = 0
  Profile = -> Sketch148
  Refine = true
  Spine = -> Pad016 [Edge253]
  SpineTangent = false
  Suppressed = false
  Transformation = 0
  Transition = 0
FEATURE [Sketcher::SketchObject] Sketch149
  ArcFitTolerance = 1e-06
  AttachmentSupport = -> [Pad016]
  ExternalGeometry = -> [Pad016]
  FullyConstrained = true
  MakeInternals = false
  MapMode = 5
  Placement = pos=(0,0,-80.4316) rot=(1,0,0;3.14159rad)
  sketch-geometry (8):
    g0: LineSegment StartX=-215.932 StartY=3.6 StartZ=0 EndX=-205.932 EndY=3.6 EndZ=0
    g1: LineSegment StartX=-215.932 StartY=3.6 StartZ=0 EndX=-215.932 EndY=-4e-16 EndZ=0
    g2: LineSegment [constr] StartX=-205.932 StartY=3.6 StartZ=0 EndX=-205.932 EndY=-9e-16 EndZ=0
    g3: ArcOfEllipse CenterX=-205.932 CenterY=-1e-15 CenterZ=0 NormalX=0 NormalY=0 NormalZ=1 MajorRadius=10 MinorRadius=3.6 AngleXU=-3.14159 StartAngle=4.71239 EndAngle=6.28319
    g4: LineSegment [constr] StartX=-215.932 StartY=-1e-15 StartZ=0 EndX=-195.932 EndY=-1e-15 EndZ=0
    g5: LineSegment [constr] StartX=-205.932 StartY=-3.6 StartZ=0 EndX=-205.932 EndY=3.6 EndZ=0
    g6: GeomPoint [constr] X=-215.262 Y=-2.1e-15 Z=0
    g7: GeomPoint [constr] X=-196.602 Y=-9e-16 Z=0
  constraints (13):
    c: Distance(g0) = 10
    c: Coincident(g0,g-5)
    c: PointOnObject(g0,g-5)
    c: Coincident(g1,g0)
    c: Coincident(g1,g-4)
    c: Coincident(g2,g0)
    c: Vertical(g2)
    c: PointOnObject(g2,g-3)
    c: InternalAlignment(g4-g7 -> g3) x4
    c: Coincident(g3,g2)
    c: Coincident(g3,g0)
    c: Coincident(g3,g1)
    c: Horizontal(g4)
FEATURE [PartDesign::SubtractivePipe] SubtractivePipe005
  AuxilleryCurvelinear = true
  AuxillerySpineTangent = false
  BaseFeature = -> SubtractivePipe004
  Binormal = (0,0,0)
  Mode = 0
  Profile = -> Sketch149
  Refine = true
  Spine = -> Pad016 [Edge251,Edge256,Edge255]
  SpineTangent = false
  Suppressed = false
  Transformation = 0
  Transition = 0
FEATURE [PartDesign::SubtractiveLoft] SubtractiveLoft002
  BaseFeature = -> SubtractivePipe005
  Closed = false
  Profile = -> Sketch129
  Refine = true
  Ruled = false
  Sections = -> [Sketch130]
  Suppressed = false
FEATURE [PartDesign::SubtractiveLoft] SubtractiveLoft003
  BaseFeature = -> SubtractiveLoft002
  Closed = false
  Profile = -> Clone2D001
  Refine = true
  Ruled = false
  Sections = -> [Sketch131]
  Suppressed = false
FEATURE [PartDesign::Chamfer] Chamfer010
  Angle = 45
  Base = -> SubtractiveLoft003 [Edge203,Edge204,Edge202,Edge201,Edge195]
  BaseFeature = -> SubtractiveLoft003
  ChamferType = 0
  FlipDirection = false
  Refine = true
  Size = 1.5
  Size2 = 1
  SupportTransform = false
  Suppressed = false
  UseAllEdges = false
FEATURE [PartDesign::Chamfer] Chamfer011
  Angle = 45
  Base = -> Chamfer010 [Edge15]
  BaseFeature = -> Chamfer010
  ChamferType = 0
  FlipDirection = false
  Refine = true
  Size = 1.6
  Size2 = 1
  SupportTransform = false
  Suppressed = false
  UseAllEdges = false
FEATURE [PartDesign::Chamfer] Chamfer012
  Angle = 45
  Base = -> Chamfer011 [Edge10]
  BaseFeature = -> Chamfer011
  ChamferType = 0
  FlipDirection = false
  Refine = true
  Size = 3.5
  Size2 = 1
  SupportTransform = false
  Suppressed = false
  UseAllEdges = false
FEATURE [PartDesign::Chamfer] Chamfer013
  Angle = 45
  Base = -> Chamfer012 [Edge94]
  BaseFeature = -> Chamfer012
  ChamferType = 0
  FlipDirection = false
  Refine = true
  Size = 1.9
  Size2 = 1
  SupportTransform = false
  Suppressed = false
  UseAllEdges = false
FEATURE [PartDesign::Fillet] Fillet007
  Base = -> Chamfer013 [Edge83]
  BaseFeature = -> Chamfer013
  Radius = 1.1
  Refine = true
  SupportTransform = false
  Suppressed = false
  UseAllEdges = false
FEATURE [PartDesign::Fillet] Fillet008
  Base = -> Fillet007 [Edge75]
  BaseFeature = -> Fillet007
  Radius = 1.9
  Refine = true
  SupportTransform = false
  Suppressed = false
  UseAllEdges = false
FEATURE [PartDesign::Pocket] Pocket011
  BaseFeature = -> Fillet008
  Direction = (0,1,-2e-16)
  Length = 0.8
  Length2 = 5
  Profile = -> Sketch132
  ReferenceAxis = -> Sketch132 [N_Axis]
  Refine = true
  Suppressed = false
  Type = 0
FEATURE [PartDesign::Pocket] Pocket012
  BaseFeature = -> Pocket011
  Direction = (0,1,0)
  Length = 1
  Length2 = 5
  Profile = -> ShapeString
  ReferenceAxis = -> ShapeString [N_Axis]
  Refine = true
  Suppressed = false
  Type = 0
FEATURE [Sketcher::SketchObject] Sketch150
  ArcFitTolerance = 1e-06
  AttachmentSupport = -> [Pad008]
  ExternalGeometry = -> [Pad008]
  FullyConstrained = true
  MakeInternals = false
  MapMode = 5
  Placement = pos=(0,3.6,0) rot=(0,0.707107,0.707107;3.14159rad)
  sketch-geometry (7):
    g0: LineSegment [constr] StartX=210.343 StartY=-66.0316 StartZ=0 EndX=210.343 EndY=-72.8316 EndZ=0
    g1: LineSegment [constr] StartX=210.343 StartY=-72.8316 StartZ=0 EndX=216.543 EndY=-72.8316 EndZ=0
    g2: LineSegment [constr] StartX=216.543 StartY=-72.8316 StartZ=0 EndX=216.543 EndY=-66.0316 EndZ=0
    g3: LineSegment [constr] StartX=216.543 StartY=-66.0316 StartZ=0 EndX=210.343 EndY=-66.0316 EndZ=0
    g4: LineSegment [constr] StartX=210.343 StartY=-72.8316 StartZ=0 EndX=216.543 EndY=-66.0316 EndZ=0
    g5: LineSegment [constr] StartX=210.343 StartY=-66.0316 StartZ=0 EndX=213.443 EndY=-69.4316 EndZ=0
    g6: Circle CenterX=213.443 CenterY=-69.4316 CenterZ=0 NormalX=0 NormalY=0 NormalZ=1 AngleXU=0 Radius=2
  constraints (18):
    c: Coincident(g0,g1)
    c: Coincident(g1,g2)
    c: Coincident(g2,g3)
    c: Coincident(g3,g0)
    c: Vertical(g0)
    c: Vertical(g2)
    c: Horizontal(g1)
    c: Horizontal(g3)
    c: Distance(g0,g2) = 6.2
    c: Distance(g1,g3) = 6.8
    c: DistanceY(g-3,g1) = 4
    c: Coincident(g4,g0)
    c: Coincident(g4,g2)
    c: Coincident(g5,g0)
    c: Symmetric(g0,g2,g5)
    c: Diameter(g6) = 4
    c: Coincident(g6,g5)
    c: Vertical(g5,g-3)
FEATURE [Sketcher::SketchObject] Sketch151
  ArcFitTolerance = 1e-06
  AttachmentSupport = -> [Pad008]
  ExternalGeometry = -> [Pad008]
  FullyConstrained = true
  MakeInternals = false
  MapMode = 5
  Placement = pos=(0,3.6,0) rot=(0,0.707107,0.707107;3.14159rad)
  sketch-geometry (10):
    g0: LineSegment [constr] StartX=211.143 StartY=-56.2316 StartZ=0 EndX=211.143 EndY=-65.4316 EndZ=0
    g1: LineSegment [constr] StartX=211.143 StartY=-65.4316 StartZ=0 EndX=215.743 EndY=-65.4316 EndZ=0
    g2: LineSegment [constr] StartX=215.743 StartY=-65.4316 StartZ=0 EndX=215.743 EndY=-56.2316 EndZ=0
    g3: LineSegment [constr] StartX=215.743 StartY=-56.2316 StartZ=0 EndX=211.143 EndY=-56.2316 EndZ=0
    g4: LineSegment StartX=212.243 StartY=-63.8316 StartZ=0 EndX=214.643 EndY=-63.8316 EndZ=0
    g5: LineSegment StartX=214.643 StartY=-63.8316 StartZ=0 EndX=214.643 EndY=-57.0316 EndZ=0
    g6: LineSegment StartX=214.643 StartY=-57.0316 StartZ=0 EndX=212.243 EndY=-57.0316 EndZ=0
    g7: LineSegment StartX=212.243 StartY=-57.0316 StartZ=0 EndX=212.243 EndY=-63.8316 EndZ=0
    g8: GeomPoint [constr] X=213.443 Y=-60.4316 Z=0
    g9: GeomPoint [constr] X=213.443 Y=-60.8316 Z=0
  constraints (26):
    c: Coincident(g0,g1)
    c: Coincident(g1,g2)
    c: Coincident(g2,g3)
    c: Coincident(g3,g0)
    c: Vertical(g0)
    c: Vertical(g2)
    c: Horizontal(g1)
    c: Horizontal(g3)
    c: Distance(g0,g2) = 4.6
    c: Distance(g1,g3) = 9.2
    c: DistanceY(g-3,g1) = 11.4
    c: Coincident(g4,g5)
    c: Coincident(g5,g6)
    c: Coincident(g6,g7)
    c: Coincident(g7,g4)
    c: Horizontal(g4)
    c: Horizontal(g6)
    c: Vertical(g5)
    c: Vertical(g7)
    c: Symmetric(g6,g4,g8)
    c: Distance(g5,g7) = 2.4
    c: Distance(g4,g6) = 6.8
    c: Symmetric(g2,g0,g9)
    c: Vertical(g8,g9)
    c: DistanceY(g1,g4) = 1.6
    c: Vertical(g9,g-3)
FEATURE [PartDesign::Pocket] Pocket019
  BaseFeature = -> Pocket013
  Direction = (0,-1,2e-16)
  Length = 3.6
  Length2 = 5
  Profile = -> Sketch151
  ReferenceAxis = -> Sketch151 [N_Axis]
  Refine = true
  Suppressed = false
  Type = 0
FEATURE [PartDesign::Pocket] Pocket018
  BaseFeature = -> Pocket019
  Direction = (0,-1,2e-16)
  Length = 3.6
  Length2 = 5
  Profile = -> Sketch150
  ReferenceAxis = -> Sketch150 [N_Axis]
  Refine = true
  Suppressed = false
  Type = 0
FEATURE [PartDesign::Point] DatumPoint
  AttacherType = Attacher::AttachEnginePoint
  AttachmentSupport = -> [Sketch150]
  MapMode = 36
  Placement = pos=(-213.443,3.6,-69.4316) rot=(0,1,0;3.14159rad)
FEATURE [PartDesign::Plane] DatumPlane002
  AttachmentSupport = -> [DatumPoint]
  Length = 260.281
  MapMode = 1
  Placement = pos=(-213.443,3.6,-69.4316) rot=(0,0,1;0rad)
  ResizeMode = 0
  Width = 71.8377
FEATURE [Sketcher::SketchObject] Sketch152
  ArcFitTolerance = 1e-06
  AttachmentSupport = -> [DatumPlane002]
  ExternalGeometry = -> [Sketch150]
  FullyConstrained = true
  MakeInternals = false
  MapMode = 5
  Placement = pos=(-213.443,3.6,-69.4316) rot=(0,0,1;0rad)
  sketch-geometry (7):
    g0: LineSegment StartX=0 StartY=0 StartZ=0 EndX=-4 EndY=5.1e-15 EndZ=0
    g1: ArcOfEllipse CenterX=0 CenterY=0 CenterZ=0 NormalX=0 NormalY=0 NormalZ=1 MajorRadius=4 MinorRadius=3.6 AngleXU=3.14159 StartAngle=2e-16 EndAngle=1.5708
    g2: LineSegment [constr] StartX=-4 StartY=9e-16 StartZ=0 EndX=4 EndY=-9e-16 EndZ=0
    g3: LineSegment [constr] StartX=0 StartY=-3.6 StartZ=0 EndX=0 EndY=3.6 EndZ=0
    g4: GeomPoint [constr] X=-1.74356 Y=2.5e-15 Z=0
    g5: GeomPoint [constr] X=1.74356 Y=-2e-15 Z=0
    g6: LineSegment StartX=0 StartY=0 StartZ=0 EndX=-5.5e-15 EndY=-3.6 EndZ=0
  constraints (11):
    c: PointOnObject(g1,g-2)
    c: Distance(g0) = 4
    c: PointOnObject(g0,g-1)
    c: InternalAlignment(g2-g5 -> g1) x4
    c: Coincident(g1,g0)
    c: Vertical(g3)
    c: Coincident(g1,g-1)
    c: Distance(g6) = 3.6
    c: Coincident(g6,g1)
    c: Coincident(g1,g6)
    c: Coincident(g0,g1)
FEATURE [PartDesign::Groove] Groove
  Angle = 360
  Angle2 = 60
  Axis = (0,1,0)
  Base = (-213.443,3.6,-69.4316)
  BaseFeature = -> Pocket018
  Profile = -> Sketch152
  ReferenceAxis = -> Sketch152 [V_Axis]
  Refine = true
  Reversed = true
  Suppressed = false
  Type = 0
FEATURE [PartDesign::Body] Body006  label="lato SX"
  AllowCompound = false
  Group = -> [Binder,Pad019,Chamfer015,Pocket002,Sketch133,Sketch091,Pad005,Sketch092,Pocket001,Sketch093,Sketch094,Pad006,Sketch095,Pad007,Sketch096,Pad008,Sketch097,Pad009,Chamfer005,Pocket004,Sketch098,Pad010,Chamfer006,Pocket003,SubtractivePipe,SubtractivePipe001,Sketch099,Sketch106,Sketch107,Sketch108,Clone2D,Sketch109,SubtractiveLoft,SubtractiveLoft001,Sketch110,Sketch111,Sketch112,Chamfer016,Chamfer017,+15 more]
  Origin = -> Origin006
  Tip = -> Groove
FEATURE [Sketcher::SketchObject] Sketch153  label="ripieno_per_sostegno_led_batteria"
  ArcFitTolerance = 1e-06
  AttachmentSupport = -> [XZ_Plane]
  ExternalGeometry = -> [Sketch036]
  FullyConstrained = true
  MakeInternals = false
  MapMode = 5
  Placement = pos=(0,0,0) rot=(1,0,0;1.5708rad)
  sketch-geometry (4):
    g0: LineSegment StartX=-217.343 StartY=-54.5944 StartZ=0 EndX=-217.343 EndY=-63.1944 EndZ=0
    g1: LineSegment StartX=-217.343 StartY=-63.1944 StartZ=0 EndX=-211.843 EndY=-63.1944 EndZ=0
    g2: LineSegment StartX=-211.843 StartY=-63.1944 StartZ=0 EndX=-211.843 EndY=-54.5944 EndZ=0
    g3: LineSegment StartX=-211.843 StartY=-54.5944 StartZ=0 EndX=-217.343 EndY=-54.5944 EndZ=0
  constraints (11):
    c: Coincident(g0,g1)
    c: Coincident(g1,g2)
    c: Coincident(g2,g3)
    c: Coincident(g3,g0)
    c: Vertical(g0)
    c: Horizontal(g1)
    c: Horizontal(g3)
    c: Tangent(g2,g-3)
    c: DistanceY(g2,g-3) = 4.5
    c: DistanceX(g3,g3) = 5.5
    c: DistanceY(g0,g0) = 8.6
FEATURE [PartDesign::Body] Body  label="Struttura pistola"
  AllowCompound = false
  Group = -> [Sketch,Sketch002,Sketch004,DatumPlane,Sketch005,DatumPlane001,CopyCut,Sketch008,Sketch009,Sketch010,Sketch011,Sketch012,Sketch013,Sketch014,Sketch015,Sketch016,Sketch017,Sketch018,Sketch019,Sketch020,Sketch022,Sketch023,Sketch024,Sketch025,Sketch026,Sketch027,Sketch029,Sketch030,Sketch031,Sketch032,Sketch033,Sketch034,Sketch035,Sketch036,Sketch037,Sketch038,Sketch039,Sketch040,Sketch041,Sketch042,+28 more]
  Origin = -> Origin
FEATURE [Part::Extrusion] Extrude088  label="Extrude088 - ripieno_per_sostegno_led_batteria"
  Base = -> Sketch153
  Dir = (0,-1,2e-16)
  DirMode = 2
  FaceMakerClass = Part::FaceMakerBullseye
  FaceMakerMode = 3
  LengthFwd = 4
  LengthRev = 0
  Placement = pos=(0,12.6,0) rot=(0,0,1;0rad)
  Solid = true
  Symmetric = false
FEATURE [Part::MultiFuse] Fusion004
  Refine = true
  Shapes = -> [Cut050,Extrude088]
FEATURE [Part::Cut] Cut051
  Base = -> Fusion004
  Refine = true
  Tool = -> Extrude087
FEATURE [Part::Cut] Cut052
  Base = -> Cut051
  Refine = true
  Tool = -> Extrude086
FEATURE [Sketcher::SketchObject] Sketch154
  ArcFitTolerance = 1e-06
  AttachmentSupport = -> [Pad016]
  ExternalGeometry = -> [Binder001]
  FullyConstrained = true
  MakeInternals = false
  MapMode = 5
  Placement = pos=(0,-3.6,0) rot=(1,0,0;1.5708rad)
  sketch-geometry (25):
    g0: LineSegment StartX=-214.643 StartY=-72.4316 StartZ=0 EndX=-212.243 EndY=-72.4316 EndZ=0
    g1: LineSegment StartX=-212.243 StartY=-72.4316 StartZ=0 EndX=-212.243 EndY=-71.2316 EndZ=0
    g2: LineSegment StartX=-212.243 StartY=-71.2316 StartZ=0 EndX=-214.643 EndY=-71.2316 EndZ=0
    g3: LineSegment StartX=-214.643 StartY=-71.2316 StartZ=0 EndX=-214.643 EndY=-72.4316 EndZ=0
    g4: GeomPoint [constr] X=-213.443 Y=-71.8316 Z=0
    g5: LineSegment StartX=-214.643 StartY=-69.6316 StartZ=0 EndX=-212.243 EndY=-69.6316 EndZ=0
    g6: LineSegment StartX=-212.243 StartY=-69.6316 StartZ=0 EndX=-212.243 EndY=-68.4316 EndZ=0
    g7: LineSegment StartX=-212.243 StartY=-68.4316 StartZ=0 EndX=-214.643 EndY=-68.4316 EndZ=0
    g8: LineSegment StartX=-214.643 StartY=-68.4316 StartZ=0 EndX=-214.643 EndY=-69.6316 EndZ=0
    g9: GeomPoint [constr] X=-213.443 Y=-69.0316 Z=0
    g10: LineSegment StartX=-214.643 StartY=-66.8316 StartZ=0 EndX=-212.243 EndY=-66.8316 EndZ=0
    g11: LineSegment StartX=-212.243 StartY=-66.8316 StartZ=0 EndX=-212.243 EndY=-65.6316 EndZ=0
    g12: LineSegment StartX=-212.243 StartY=-65.6316 StartZ=0 EndX=-214.643 EndY=-65.6316 EndZ=0
    g13: LineSegment StartX=-214.643 StartY=-65.6316 StartZ=0 EndX=-214.643 EndY=-66.8316 EndZ=0
    g14: GeomPoint [constr] X=-213.443 Y=-66.2316 Z=0
    g15: LineSegment StartX=-214.643 StartY=-64.0316 StartZ=0 EndX=-212.243 EndY=-64.0316 EndZ=0
    g16: LineSegment StartX=-212.243 StartY=-64.0316 StartZ=0 EndX=-212.243 EndY=-62.8316 EndZ=0
    g17: LineSegment StartX=-212.243 StartY=-62.8316 StartZ=0 EndX=-214.643 EndY=-62.8316 EndZ=0
    g18: LineSegment StartX=-214.643 StartY=-62.8316 StartZ=0 EndX=-214.643 EndY=-64.0316 EndZ=0
    g19: GeomPoint [constr] X=-213.443 Y=-63.4316 Z=0
    g20: LineSegment StartX=-214.643 StartY=-61.2316 StartZ=0 EndX=-212.243 EndY=-61.2316 EndZ=0
    g21: LineSegment StartX=-212.243 StartY=-61.2316 StartZ=0 EndX=-212.243 EndY=-60.0316 EndZ=0
    g22: LineSegment StartX=-212.243 StartY=-60.0316 StartZ=0 EndX=-214.643 EndY=-60.0316 EndZ=0
    g23: LineSegment StartX=-214.643 StartY=-60.0316 StartZ=0 EndX=-214.643 EndY=-61.2316 EndZ=0
    g24: GeomPoint [constr] X=-213.443 Y=-60.6316 Z=0
  constraints (65):
    c: Coincident(g0,g1)
    c: Coincident(g1,g2)
    c: Coincident(g2,g3)
    c: Coincident(g3,g0)
    c: Horizontal(g0)
    c: Horizontal(g2)
    c: Vertical(g1)
    c: Vertical(g3)
    c: Symmetric(g2,g0,g4)
    c: Distance(g1,g3) = 2.4
    c: Distance(g0,g2) = 1.2
    c: Coincident(g5,g6)
    c: Coincident(g6,g7)
    c: Coincident(g7,g8)
    c: Coincident(g8,g5)
    c: Horizontal(g5)
    c: Horizontal(g7)
    c: Vertical(g6)
    c: Vertical(g8)
    c: Symmetric(g7,g5,g9)
    c: Distance(g6,g8) = 2.4
    c: Distance(g5,g7) = 1.2
    c: Coincident(g10,g11)
    c: Coincident(g11,g12)
    c: Coincident(g12,g13)
    c: Coincident(g13,g10)
    c: Horizontal(g10)
    c: Horizontal(g12)
    c: Vertical(g11)
    c: Vertical(g13)
    c: Symmetric(g12,g10,g14)
    c: Distance(g11,g13) = 2.4
    c: Distance(g10,g12) = 1.2
    c: Coincident(g15,g16)
    c: Coincident(g16,g17)
    c: Coincident(g17,g18)
    c: Coincident(g18,g15)
    c: Horizontal(g15)
    c: Horizontal(g17)
    c: Vertical(g16)
    c: Vertical(g18)
    c: Symmetric(g17,g15,g19)
    c: Distance(g16,g18) = 2.4
    c: Distance(g15,g17) = 1.2
    c: Vertical(g4,g-3)
    c: Vertical(g9,g-3)
    c: Vertical(g14,g-3)
    c: Vertical(g19,g-3)
    c: DistanceY(g-3,g4) = 5
    c: DistanceY(g4,g9) = 2.8
    c: DistanceY(g9,g14) = 2.8
    c: DistanceY(g14,g19) = 2.8
    c: Coincident(g20,g21)
    c: Coincident(g21,g22)
    c: Coincident(g22,g23)
    c: Coincident(g23,g20)
    c: Horizontal(g20)
    c: Horizontal(g22)
    c: Vertical(g21)
    c: Vertical(g23)
    c: Symmetric(g22,g20,g24)
    c: Distance(g21,g23) = 2.4
    c: Distance(g20,g22) = 1.2
    c: DistanceY(g19,g24) = 2.8
    c: Vertical(g-3,g24)
FEATURE [PartDesign::Pocket] Pocket020
  BaseFeature = -> Pocket012
  Direction = (0,1,-2e-16)
  Length = 3.6
  Length2 = 5
  Profile = -> Sketch154
  ReferenceAxis = -> Sketch154 [N_Axis]
  Refine = true
  Suppressed = false
  Type = 0
FEATURE [PartDesign::Body] Body007  label="lato DX"
  AllowCompound = false
  Group = -> [Binder001,Sketch114,Pad011,Chamfer014,Sketch115,Pocket006,Sketch116,Pad012,Sketch117,Pocket007,Sketch118,Pad013,Sketch119,Pocket008,Pad017,Chamfer009,Pocket009,Sketch123,Sketch120,Pad014,Pad018,Chamfer008,Pocket010,Sketch121,Pad015,Sketch122,Pad016,SubtractivePipe004,SubtractivePipe005,Sketch149,Sketch148,Sketch124,Sketch125,Sketch126,Sketch129,Sketch130,Clone2D001,Sketch131,SubtractiveLoft002,+13 more]
  Origin = -> Origin007
  Tip = -> Pocket020
note: 2 file-system paths scrubbed to <path> (originals preserved in the JSON sidecar)
